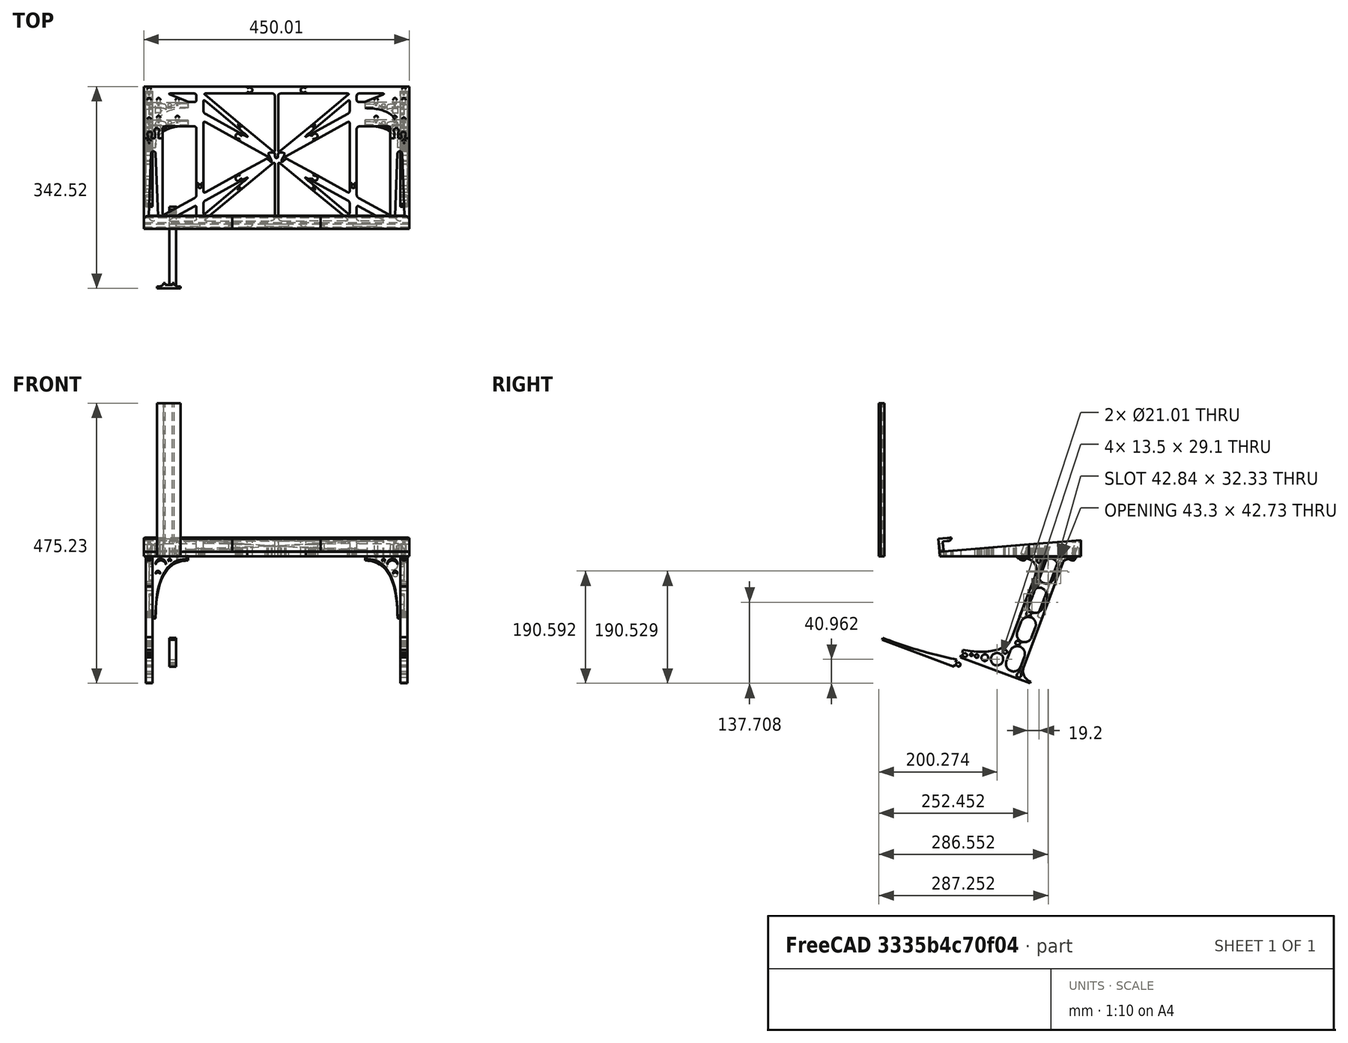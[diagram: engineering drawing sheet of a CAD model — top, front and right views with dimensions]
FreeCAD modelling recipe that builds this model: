
FCSTD DOCUMENT  (FreeCAD 0.19R0.19.2)
Label: laptopStand394
License: All rights reserved
LicenseURL: http://en.wikipedia.org/wiki/All_rights_reserved
objects: Part::Cylinder×164, Part::MultiFuse×151, Part::Box×65, Part::Cut×62, Sketcher::SketchObject×45, Part::Extrusion×44, Part::Fuse×17, Part::Fillet×10, App::MeasureDistance×4, Part::Chamfer×3
note: 561 computed .brp shape members not serialized (recipe doc carries the construction recipe); baked Part::Feature solids carry a one-line shape summary decoded from their .brp

FEATURE [Sketcher::SketchObject] Sketch001  label="legTop"
  FullyConstrained = true
  MapMode = 4
  Placement = pos=(0,0,0) rot=(0.57735,0.57735,0.57735;2.0944rad)
  sketch-geometry (41):
    g0: BSplineCurve PolesCount=3 KnotsCount=2 Degree=2 IsPeriodic=0
    g1: ArcOfCircle CenterX=73.1223 CenterY=-32.291 CenterZ=0 NormalX=0 NormalY=0 NormalZ=1 AngleXU=0 Radius=13 StartAngle=5.92268 EndAngle=9.06428
    g2: ArcOfCircle CenterX=66.7816 CenterY=-49.1439 CenterZ=0 NormalX=0 NormalY=0 NormalZ=1 AngleXU=0 Radius=13 StartAngle=2.78068 EndAngle=5.92131
    g3-g6: Circle x4 (B-spline internal-alignment scaffolding for g7; pole/knot coordinates omitted)
    g7: BSplineCurve PolesCount=4 KnotsCount=2 Degree=3 IsPeriodic=0
    g8: GeomPoint X=28.8094 Y=-19.0875 Z=0
    g9: GeomPoint X=47.0443 Y=-50.4712 Z=0
    g10: Circle CenterX=53.5586 CenterY=-23.2695 CenterZ=0 NormalX=0 NormalY=0 NormalZ=1 AngleXU=0 Radius=3.24518
    g11: LineSegment StartX=17.2232 StartY=-16.0875 StartZ=0 EndX=17.2232 EndY=-19.0875 EndZ=0
    g12: ArcOfCircle CenterX=17.2475 CenterY=-181.166 CenterZ=0 NormalX=0 NormalY=0 NormalZ=1 AngleXU=0 Radius=13 StartAngle=5.92268 EndAngle=7.49361
    g13: ArcOfCircle CenterX=29.5716 CenterY=-148.408 CenterZ=0 NormalX=0 NormalY=0 NormalZ=1 AngleXU=0 Radius=13 StartAngle=4.35228 EndAngle=5.92131
    g14: ArcOfCircle CenterX=35.8967 CenterY=-131.555 CenterZ=0 NormalX=0 NormalY=0 NormalZ=1 AngleXU=0 Radius=13 StartAngle=5.92268 EndAngle=7.49902
    g15: ArcOfCircle CenterX=48.1805 CenterY=-98.7782 CenterZ=0 NormalX=0 NormalY=0 NormalZ=1 AngleXU=0 Radius=13 StartAngle=4.34921 EndAngle=5.92131
    g16: ArcOfCircle CenterX=54.5183 CenterY=-81.9247 CenterZ=0 NormalX=0 NormalY=0 NormalZ=1 AngleXU=0 Radius=13 StartAngle=5.92268 EndAngle=8.70432
    g17: ArcOfCircle CenterX=20.184 CenterY=-217.506 CenterZ=0 NormalX=0 NormalY=0 NormalZ=1 AngleXU=0 Radius=3.81084 StartAngle=1.88136 EndAngle=6.80465
    g18: ArcOfCircle CenterX=36.3663 CenterY=-113.042 CenterZ=0 NormalX=0 NormalY=0 NormalZ=1 AngleXU=0 Radius=3.60555 StartAngle=0.230024 EndAngle=5.3372
    g19: ArcOfCircle CenterX=17.7945 CenterY=-162.686 CenterZ=0 NormalX=0 NormalY=0 NormalZ=1 AngleXU=0 Radius=3.60555 StartAngle=0.230024 EndAngle=5.3372
    g20: ArcOfCircle CenterX=49.8795 CenterY=-62.6074 CenterZ=0 NormalX=0 NormalY=0 NormalZ=1 AngleXU=0 Radius=3.84187 StartAngle=4.46973 EndAngle=9.40343
    g21: LineSegment StartX=48.9563 StartY=-66.3367 StartZ=0 EndX=44.7488 EndY=-73.3482 EndZ=0
    g22: LineSegment StartX=41.085 StartY=-66.3176 StartZ=0 EndX=46.0385 EndY=-62.5254 EndZ=0
    g23: LineSegment StartX=47.0443 StartY=-50.4712 StartZ=0 EndX=41.085 EndY=-66.3176 EndZ=0
    g24: LineSegment StartX=17.2232 StartY=-16.0875 StartZ=0 EndX=117.223 EndY=-16.0875 EndZ=0
    g25: LineSegment StartX=28.8094 StartY=-19.0875 StartZ=0 EndX=17.2232 EndY=-19.0875 EndZ=0
    g26: LineSegment StartX=117.223 StartY=-16.0875 StartZ=0 EndX=117.223 EndY=-19.0875 EndZ=0
    g27: LineSegment StartX=85.2866 StartY=-36.8766 StartZ=0 EndX=78.9396 EndY=-53.7463 EndZ=0
    g28: LineSegment StartX=60.9579 StartY=-27.7053 StartZ=0 EndX=54.6191 EndY=-44.5532 EndZ=0
    g29: LineSegment StartX=23.4884 StartY=-215.608 StartZ=0 EndX=94.6579 EndY=-26.1359 EndZ=0
    g30: LineSegment StartX=19.0195 StartY=-213.878 StartZ=0 EndX=29.4118 EndY=-185.752 EndZ=0
    g31: LineSegment StartX=22.7134 StartY=-166.661 StartZ=0 EndX=21.8316 EndY=-169.001 EndZ=0
    g32: LineSegment StartX=19.9036 StartY=-165.61 StartZ=0 EndX=22.7134 EndY=-166.661 EndZ=0
    g33: LineSegment StartX=21.3051 StartY=-161.864 StartZ=0 EndX=24.1149 EndY=-162.915 EndZ=0
    g34: LineSegment StartX=24.1149 StartY=-162.915 StartZ=0 EndX=24.9906 EndY=-160.574 EndZ=0
    g35: LineSegment StartX=41.7296 StartY=-153.01 StartZ=0 EndX=48.061 EndY=-136.14 EndZ=0
    g36: LineSegment StartX=41.2852 StartY=-117.017 StartZ=0 EndX=40.4148 EndY=-119.365 EndZ=0
    g37: LineSegment StartX=38.4753 StartY=-115.966 StartZ=0 EndX=41.2852 EndY=-117.017 EndZ=0
    g38: LineSegment StartX=39.8769 StartY=-112.22 StartZ=0 EndX=42.6867 EndY=-113.271 EndZ=0
    g39: LineSegment StartX=42.6867 StartY=-113.271 StartZ=0 EndX=43.5622 EndY=-110.93 EndZ=0
    g40: LineSegment StartX=66.6827 StartY=-86.5104 StartZ=0 EndX=60.3386 EndY=-103.381 EndZ=0
  constraints (65):
    c: Block(g0)
    c: Block(g1)
    c: Block(g2)
    c: Weight(g3) = 1
    c: Equal(g3,g4)
    c: Equal(g3,g5)
    c: Equal(g3,g6)
    c: InternalAlignment(g3-g6 -> g7) x4
    c: InternalAlignment(g8,g7)
    c: InternalAlignment(g9,g7)
    c: Block(g10)
    c: Block(g7)
    c: Vertical(g11)
    c: Block(g12)
    c: Block(g13)
    c: Block(g14)
    c: Block(g15)
    c: Block(g16)
    c: Block(g17)
    c: Block(g18)
    c: Block(g19)
    c: Block(g20)
    c: Coincident(g21,g20)
    c: Coincident(g21,g16)
    c: Coincident(g22,g20)
    c: Block(g22)
    c: Coincident(g23,g7)
    c: Coincident(g23,g22)
    c: Coincident(g24,g11)
    c: Horizontal(g24)
    c: Coincident(g25,g7)
    c: Coincident(g25,g11)
    c: Horizontal(g25)
    c: Coincident(g26,g24)
    c: Coincident(g26,g0)
    c: Vertical(g26)
    c: Block(g24)
    c: Coincident(g27,g1)
    c: Coincident(g27,g2)
    c: Coincident(g28,g1)
    c: Coincident(g28,g2)
    c: Coincident(g29,g17)
    c: Coincident(g29,g0)
    c: Coincident(g30,g17)
    c: Coincident(g30,g12)
    c: Coincident(g31,g12)
    c: Coincident(g32,g19)
    c: Coincident(g32,g31)
    c: Block(g31)
    c: Coincident(g33,g19)
    c: Coincident(g34,g33)
    c: Coincident(g34,g13)
    c: Block(g34)
    c: Coincident(g35,g13)
    c: Coincident(g35,g14)
    c: Coincident(g36,g14)
    c: Coincident(g37,g18)
    c: Coincident(g37,g36)
    c: Block(g36)
    c: Coincident(g38,g18)
    c: Coincident(g39,g38)
    c: Coincident(g39,g15)
    c: Block(g39)
    c: Coincident(g40,g16)
    c: Coincident(g40,g15)
FEATURE [Sketcher::SketchObject] Sketch002
  FullyConstrained = true
  sketch-geometry (15):
    g0: LineSegment StartX=-6.77179 StartY=-200.304 StartZ=0 EndX=5.22821 EndY=-200.304 EndZ=0
    g1: LineSegment StartX=5.22821 StartY=-200.304 StartZ=0 EndX=5.22821 EndY=-197.304 EndZ=0
    g2: LineSegment StartX=-6.77179 StartY=-200.304 StartZ=0 EndX=-6.77179 EndY=-197.304 EndZ=0
    g3: LineSegment StartX=5.22821 StartY=-197.304 StartZ=0 EndX=8.22821 EndY=-197.304 EndZ=0
    g4: LineSegment StartX=19.2282 StartY=-203.304 StartZ=0 EndX=19.2282 EndY=-206.304 EndZ=0
    g5: Circle CenterX=19.2282 CenterY=-203.304 CenterZ=0 NormalX=0 NormalY=0 NormalZ=1 AngleXU=0 Radius=1
    g6: Circle CenterX=8.22821 CenterY=-203.304 CenterZ=0 NormalX=0 NormalY=0 NormalZ=1 AngleXU=0 Radius=1
    g7: Circle CenterX=8.22821 CenterY=-197.304 CenterZ=0 NormalX=0 NormalY=0 NormalZ=1 AngleXU=0 Radius=1
    g8: BSplineCurve PolesCount=3 KnotsCount=2 Degree=2 IsPeriodic=0
    g9: GeomPoint X=19.2282 Y=-203.304 Z=0
    g10: GeomPoint X=8.22821 Y=-197.304 Z=0
    g11: LineSegment StartX=19.2282 StartY=-206.304 StartZ=0 EndX=-20.7718 EndY=-206.304 EndZ=0
    g12: LineSegment StartX=-20.7718 StartY=-206.304 StartZ=0 EndX=-20.7718 EndY=-203.304 EndZ=0
    g13: BSplineCurve PolesCount=3 KnotsCount=2 Degree=2 IsPeriodic=0
    g14: LineSegment StartX=-9.77179 StartY=-197.304 StartZ=0 EndX=-6.77179 EndY=-197.304 EndZ=0
  constraints (35):
    c: Horizontal(g0)
    c: Distance(g0) = 12
    c: Coincident(g1,g0)
    c: Vertical(g1)
    c: Distance(g1) = 3
    c: Coincident(g2,g0)
    c: Vertical(g2)
    c: Distance(g2) = 3
    c: Coincident(g3,g1)
    c: Horizontal(g3)
    c: Distance(g3) = 3
    c: Vertical(g4)
    c: Coincident(g8,g4)
    c: Weight(g5) = 1
    c: Equal(g5,g6)
    c: Equal(g5,g7)
    c: Coincident(g8,g3)
    c: InternalAlignment(g5,g8)
    c: InternalAlignment(g6,g8)
    c: InternalAlignment(g7,g8)
    c: InternalAlignment(g9,g8)
    c: InternalAlignment(g10,g8)
    c: Block(g8)
    c: Coincident(g11,g4)
    c: Horizontal(g11)
    c: Distance(g11) = 40
    c: Block(g11)
    c: Coincident(g12,g11)
    c: Vertical(g12)
    c: Block(g12)
    c: Block(g13)
    c: Coincident(g13,g12)
    c: Coincident(g14,g13)
    c: Coincident(g14,g2)
    c: Horizontal(g14)
FEATURE [Part::Extrusion] Extrude003
  Base = -> Sketch002
  Dir = (0,0,1)
  DirMode = 2
  FaceMakerClass = Part::FaceMakerBullseye
  LengthFwd = 260
  LengthRev = 0
  Solid = true
  Symmetric = false
FEATURE [Sketcher::SketchObject] Sketch003  label="original"
  FullyConstrained = false
  sketch-geometry (469):
    g0: LineSegment StartX=-42.9272 StartY=136.221 StartZ=0 EndX=-42.9272 EndY=-103.779 EndZ=0
    g1: LineSegment StartX=407.073 StartY=136.221 StartZ=0 EndX=407.073 EndY=-103.779 EndZ=0
    g2: ArcOfCircle CenterX=-26.9272 CenterY=-83.7794 CenterZ=0 NormalX=0 NormalY=0 NormalZ=1 AngleXU=0 Radius=8 StartAngle=3.14159 EndAngle=6.28319
    g3: ArcOfCircle CenterX=391.073 CenterY=-83.7794 CenterZ=0 NormalX=0 NormalY=0 NormalZ=1 AngleXU=0 Radius=8 StartAngle=3.14159 EndAngle=6.28319
    g4: Circle CenterX=175.022 CenterY=27.0628 CenterZ=0 NormalX=0 NormalY=0 NormalZ=1 AngleXU=0 Radius=1
    g5: Circle CenterX=179.022 CenterY=24.8665 CenterZ=0 NormalX=0 NormalY=0 NormalZ=1 AngleXU=0 Radius=1
    g6: Circle CenterX=179.022 CenterY=27.0628 CenterZ=0 NormalX=0 NormalY=0 NormalZ=1 AngleXU=0 Radius=1
    g7: BSplineCurve PolesCount=3 KnotsCount=2 Degree=2 IsPeriodic=0
    g8: GeomPoint X=175.022 Y=27.0628 Z=0
    g9: GeomPoint X=179.022 Y=27.0628 Z=0
    g10: Circle CenterX=189.124 CenterY=27.0628 CenterZ=0 NormalX=0 NormalY=0 NormalZ=1 AngleXU=0 Radius=1
    g11: Circle CenterX=185.124 CenterY=24.8665 CenterZ=0 NormalX=0 NormalY=0 NormalZ=1 AngleXU=0 Radius=1
    g12: Circle CenterX=185.124 CenterY=27.0628 CenterZ=0 NormalX=0 NormalY=0 NormalZ=1 AngleXU=0 Radius=1
    g13: BSplineCurve PolesCount=3 KnotsCount=2 Degree=2 IsPeriodic=0
    g14: GeomPoint X=189.124 Y=27.0628 Z=0
    g15: GeomPoint X=185.124 Y=27.0628 Z=0
    g16: Circle CenterX=175.022 CenterY=5.37834 CenterZ=0 NormalX=0 NormalY=0 NormalZ=1 AngleXU=0 Radius=1
    g17: Circle CenterX=179.022 CenterY=7.57463 CenterZ=0 NormalX=0 NormalY=0 NormalZ=1 AngleXU=0 Radius=1
    g18: Circle CenterX=179.022 CenterY=5.34704 CenterZ=0 NormalX=0 NormalY=0 NormalZ=1 AngleXU=0 Radius=1
    g19: BSplineCurve PolesCount=3 KnotsCount=2 Degree=2 IsPeriodic=0
    g20: GeomPoint X=175.022 Y=5.37834 Z=0
    g21: GeomPoint X=179.022 Y=5.34704 Z=0
    g22: Circle CenterX=189.124 CenterY=5.37834 CenterZ=0 NormalX=0 NormalY=0 NormalZ=1 AngleXU=0 Radius=1
    g23: Circle CenterX=185.124 CenterY=7.57463 CenterZ=0 NormalX=0 NormalY=0 NormalZ=1 AngleXU=0 Radius=1
    g24: Circle CenterX=185.124 CenterY=5.34704 CenterZ=0 NormalX=0 NormalY=0 NormalZ=1 AngleXU=0 Radius=1
    g25: BSplineCurve PolesCount=3 KnotsCount=2 Degree=2 IsPeriodic=0
    g26: GeomPoint X=189.124 Y=5.37834 Z=0
    g27: GeomPoint X=185.124 Y=5.34704 Z=0
    g28: Circle CenterX=165.871 CenterY=18.1458 CenterZ=0 NormalX=0 NormalY=0 NormalZ=1 AngleXU=0 Radius=1
    g29: Circle CenterX=169.377 CenterY=16.2206 CenterZ=0 NormalX=0 NormalY=0 NormalZ=1 AngleXU=0 Radius=1
    g30: Circle CenterX=165.871 CenterY=14.2956 CenterZ=0 NormalX=0 NormalY=0 NormalZ=1 AngleXU=0 Radius=1
    g31: BSplineCurve PolesCount=3 KnotsCount=2 Degree=2 IsPeriodic=0
    g32: GeomPoint X=165.871 Y=18.1458 Z=0
    g33: GeomPoint X=165.871 Y=14.2956 Z=0
    g34: Circle CenterX=198.275 CenterY=18.1318 CenterZ=0 NormalX=0 NormalY=0 NormalZ=1 AngleXU=0 Radius=1
    g35: Circle CenterX=194.768 CenterY=16.2206 CenterZ=0 NormalX=0 NormalY=0 NormalZ=1 AngleXU=0 Radius=1
    g36: Circle CenterX=198.264 CenterY=14.2963 CenterZ=0 NormalX=0 NormalY=0 NormalZ=1 AngleXU=0 Radius=1
    g37: BSplineCurve PolesCount=3 KnotsCount=2 Degree=2 IsPeriodic=0
    g38: GeomPoint X=198.275 Y=18.1318 Z=0
    g39: GeomPoint X=198.264 Y=14.2963 Z=0
    g40: LineSegment StartX=407.073 StartY=-103.779 StartZ=0 EndX=-42.9272 EndY=-103.779 EndZ=0
    g41: Circle CenterX=125.607 CenterY=54.1951 CenterZ=0 NormalX=0 NormalY=0 NormalZ=1 AngleXU=0 Radius=1
    g42: Circle CenterX=139.632 CenterY=46.4944 CenterZ=0 NormalX=0 NormalY=0 NormalZ=1 AngleXU=0 Radius=1
    g43: Circle CenterX=127.326 CenterY=56.7187 CenterZ=0 NormalX=0 NormalY=0 NormalZ=1 AngleXU=0 Radius=1
    g44: BSplineCurve PolesCount=3 KnotsCount=2 Degree=2 IsPeriodic=0
    g45: GeomPoint X=125.607 Y=54.1951 Z=0
    g46: GeomPoint X=127.326 Y=56.7187 Z=0
    g47: Circle CenterX=236.824 CenterY=56.7187 CenterZ=0 NormalX=0 NormalY=0 NormalZ=1 AngleXU=0 Radius=1
    g48: Circle CenterX=224.513 CenterY=46.4944 CenterZ=0 NormalX=0 NormalY=0 NormalZ=1 AngleXU=0 Radius=1
    g49: Circle CenterX=238.538 CenterY=54.1951 CenterZ=0 NormalX=0 NormalY=0 NormalZ=1 AngleXU=0 Radius=1
    g50: BSplineCurve PolesCount=3 KnotsCount=2 Degree=2 IsPeriodic=0
    g51: GeomPoint X=236.824 Y=56.7187 Z=0
    g52: GeomPoint X=238.538 Y=54.1951 Z=0
    g53: Circle CenterX=238.538 CenterY=-21.7516 CenterZ=0 NormalX=0 NormalY=0 NormalZ=1 AngleXU=0 Radius=1
    g54: Circle CenterX=224.513 CenterY=-14.0532 CenterZ=0 NormalX=0 NormalY=0 NormalZ=1 AngleXU=0 Radius=1
    g55: Circle CenterX=236.584 CenterY=-24.2775 CenterZ=0 NormalX=0 NormalY=0 NormalZ=1 AngleXU=0 Radius=1
    g56: BSplineCurve PolesCount=3 KnotsCount=2 Degree=2 IsPeriodic=0
    g57: GeomPoint X=238.538 Y=-21.7516 Z=0
    g58: GeomPoint X=236.584 Y=-24.2775 Z=0
    g59: Circle CenterX=125.607 CenterY=-21.7539 CenterZ=0 NormalX=0 NormalY=0 NormalZ=1 AngleXU=0 Radius=1
    g60: Circle CenterX=139.632 CenterY=-14.0532 CenterZ=0 NormalX=0 NormalY=0 NormalZ=1 AngleXU=0 Radius=1
    g61: Circle CenterX=127.325 CenterY=-24.2775 CenterZ=0 NormalX=0 NormalY=0 NormalZ=1 AngleXU=0 Radius=1
    g62: BSplineCurve PolesCount=3 KnotsCount=2 Degree=2 IsPeriodic=0
    g63: GeomPoint X=125.607 Y=-21.7539 Z=0
    g64: GeomPoint X=127.325 Y=-24.2775 Z=0
    g65: Circle CenterX=302.996 CenterY=111.695 CenterZ=0 NormalX=0 NormalY=0 NormalZ=1 AngleXU=0 Radius=1
    g66: Circle CenterX=306.073 CenterY=114.251 CenterZ=0 NormalX=0 NormalY=0 NormalZ=1 AngleXU=0 Radius=1
    g67: Circle CenterX=306.073 CenterY=110.251 CenterZ=0 NormalX=0 NormalY=0 NormalZ=1 AngleXU=0 Radius=1
    g68: BSplineCurve PolesCount=3 KnotsCount=2 Degree=2 IsPeriodic=0
    g69: GeomPoint X=302.996 Y=111.695 Z=0
    g70: GeomPoint X=306.073 Y=110.251 Z=0
    g71: Circle CenterX=306.073 CenterY=95.2763 CenterZ=0 NormalX=0 NormalY=0 NormalZ=1 AngleXU=0 Radius=1
    g72: Circle CenterX=306.073 CenterY=91.2763 CenterZ=0 NormalX=0 NormalY=0 NormalZ=1 AngleXU=0 Radius=1
    g73: Circle CenterX=302.567 CenterY=89.3511 CenterZ=0 NormalX=0 NormalY=0 NormalZ=1 AngleXU=0 Radius=1
    g74: BSplineCurve PolesCount=3 KnotsCount=2 Degree=2 IsPeriodic=0
    g75: GeomPoint X=306.073 Y=95.2763 Z=0
    g76: GeomPoint X=302.567 Y=89.3511 Z=0
    g77: LineSegment StartX=306.073 StartY=110.251 StartZ=0 EndX=306.073 EndY=95.2763 EndZ=0
    g78: LineSegment StartX=302.996 StartY=111.695 StartZ=0 EndX=236.824 EndY=56.7187 EndZ=0
    g79: LineSegment StartX=238.538 StartY=54.1951 StartZ=0 EndX=302.567 EndY=89.3511 EndZ=0
    g80: Circle CenterX=61.1496 CenterY=111.695 CenterZ=0 NormalX=0 NormalY=0 NormalZ=1 AngleXU=0 Radius=1
    g81: Circle CenterX=58.0728 CenterY=114.251 CenterZ=0 NormalX=0 NormalY=0 NormalZ=1 AngleXU=0 Radius=1
    g82: Circle CenterX=58.0728 CenterY=110.251 CenterZ=0 NormalX=0 NormalY=0 NormalZ=1 AngleXU=0 Radius=1
    g83: BSplineCurve PolesCount=3 KnotsCount=2 Degree=2 IsPeriodic=0
    g84: GeomPoint X=61.1496 Y=111.695 Z=0
    g85: GeomPoint X=58.0728 Y=110.251 Z=0
    g86: Circle CenterX=61.5791 CenterY=89.3511 CenterZ=0 NormalX=0 NormalY=0 NormalZ=1 AngleXU=0 Radius=1
    g87: Circle CenterX=58.0728 CenterY=91.2763 CenterZ=0 NormalX=0 NormalY=0 NormalZ=1 AngleXU=0 Radius=1
    g88: Circle CenterX=58.0728 CenterY=95.2763 CenterZ=0 NormalX=0 NormalY=0 NormalZ=1 AngleXU=0 Radius=1
    g89: BSplineCurve PolesCount=3 KnotsCount=2 Degree=2 IsPeriodic=0
    g90: GeomPoint X=61.5791 Y=89.3511 Z=0
    g91: GeomPoint X=58.0728 Y=95.2763 Z=0
    g92: LineSegment StartX=58.0728 StartY=110.251 StartZ=0 EndX=58.0728 EndY=95.2763 EndZ=0
    g93: LineSegment StartX=61.1496 StartY=111.695 StartZ=0 EndX=127.326 EndY=56.7187 EndZ=0
    g94: LineSegment StartX=125.607 StartY=54.1951 StartZ=0 EndX=61.5791 EndY=89.3511 EndZ=0
    g95: Circle CenterX=61.5791 CenterY=-56.9099 CenterZ=0 NormalX=0 NormalY=0 NormalZ=1 AngleXU=0 Radius=1
    g96: Circle CenterX=58.0728 CenterY=-58.8351 CenterZ=0 NormalX=0 NormalY=0 NormalZ=1 AngleXU=0 Radius=1
    g97: Circle CenterX=58.0728 CenterY=-62.8351 CenterZ=0 NormalX=0 NormalY=0 NormalZ=1 AngleXU=0 Radius=1
    g98: BSplineCurve PolesCount=3 KnotsCount=2 Degree=2 IsPeriodic=0
    g99: GeomPoint X=61.5791 Y=-56.9099 Z=0
    g100: GeomPoint X=58.0728 Y=-62.8351 Z=0
    g101: Circle CenterX=58.0728 CenterY=-77.8102 CenterZ=0 NormalX=0 NormalY=0 NormalZ=1 AngleXU=0 Radius=1
    g102: Circle CenterX=58.0728 CenterY=-81.8102 CenterZ=0 NormalX=0 NormalY=0 NormalZ=1 AngleXU=0 Radius=1
    g103: Circle CenterX=61.1496 CenterY=-79.2541 CenterZ=0 NormalX=0 NormalY=0 NormalZ=1 AngleXU=0 Radius=1
    g104: BSplineCurve PolesCount=3 KnotsCount=2 Degree=2 IsPeriodic=0
    g105: GeomPoint X=58.0728 Y=-77.8102 Z=0
    g106: GeomPoint X=61.1496 Y=-79.2541 Z=0
    g107: LineSegment StartX=58.0728 StartY=-62.8351 StartZ=0 EndX=58.0728 EndY=-77.8102 EndZ=0
    g108: LineSegment StartX=61.1496 StartY=-79.2541 StartZ=0 EndX=127.325 EndY=-24.2775 EndZ=0
    g109: LineSegment StartX=125.607 StartY=-21.7539 StartZ=0 EndX=61.5791 EndY=-56.9099 EndZ=0
    g110: Circle CenterX=302.567 CenterY=-56.9099 CenterZ=0 NormalX=0 NormalY=0 NormalZ=1 AngleXU=0 Radius=1
    g111: Circle CenterX=306.073 CenterY=-58.8351 CenterZ=0 NormalX=0 NormalY=0 NormalZ=1 AngleXU=0 Radius=1
    g112: Circle CenterX=306.073 CenterY=-62.8351 CenterZ=0 NormalX=0 NormalY=0 NormalZ=1 AngleXU=0 Radius=1
    g113: BSplineCurve PolesCount=3 KnotsCount=2 Degree=2 IsPeriodic=0
    g114: GeomPoint X=302.567 Y=-56.9099 Z=0
    g115: GeomPoint X=306.073 Y=-62.8351 Z=0
    g116: Circle CenterX=302.996 CenterY=-79.2541 CenterZ=0 NormalX=0 NormalY=0 NormalZ=1 AngleXU=0 Radius=1
    g117: Circle CenterX=306.073 CenterY=-81.8102 CenterZ=0 NormalX=0 NormalY=0 NormalZ=1 AngleXU=0 Radius=1
    g118: Circle CenterX=306.073 CenterY=-77.8102 CenterZ=0 NormalX=0 NormalY=0 NormalZ=1 AngleXU=0 Radius=1
    g119: BSplineCurve PolesCount=3 KnotsCount=2 Degree=2 IsPeriodic=0
    g120: GeomPoint X=302.996 Y=-79.2541 Z=0
    g121: GeomPoint X=306.073 Y=-77.8102 Z=0
    g122: LineSegment StartX=306.073 StartY=-62.8351 StartZ=0 EndX=306.073 EndY=-77.8102 EndZ=0
    g123: LineSegment StartX=302.996 StartY=-79.2541 StartZ=0 EndX=236.584 EndY=-24.2775 EndZ=0
    g124: LineSegment StartX=238.538 StartY=-21.7516 StartZ=0 EndX=302.567 EndY=-56.9099 EndZ=0
    g125: Circle CenterX=61.6457 CenterY=-88.8112 CenterZ=0 NormalX=0 NormalY=0 NormalZ=1 AngleXU=0 Radius=1
    g126: Circle CenterX=58.0728 CenterY=-91.7794 CenterZ=0 NormalX=0 NormalY=0 NormalZ=1 AngleXU=0 Radius=1
    g127: Circle CenterX=63.9135 CenterY=-91.7791 CenterZ=0 NormalX=0 NormalY=0 NormalZ=1 AngleXU=0 Radius=1
    g128: BSplineCurve PolesCount=3 KnotsCount=2 Degree=2 IsPeriodic=0
    g129: GeomPoint X=61.6457 Y=-88.8112 Z=0
    g130: GeomPoint X=63.9135 Y=-91.7791 Z=0
    g131: Circle CenterX=179.022 CenterY=-85.8163 CenterZ=0 NormalX=0 NormalY=0 NormalZ=1 AngleXU=0 Radius=1
    g132: Circle CenterX=179.022 CenterY=-91.7794 CenterZ=0 NormalX=0 NormalY=0 NormalZ=1 AngleXU=0 Radius=1
    g133: Circle CenterX=171.895 CenterY=-91.7791 CenterZ=0 NormalX=0 NormalY=0 NormalZ=1 AngleXU=0 Radius=1
    g134: BSplineCurve PolesCount=3 KnotsCount=2 Degree=2 IsPeriodic=0
    g135: GeomPoint X=179.022 Y=-85.8163 Z=0
    g136: GeomPoint X=171.895 Y=-91.7791 Z=0
    g137: Circle CenterX=185.124 CenterY=-86.2028 CenterZ=0 NormalX=0 NormalY=0 NormalZ=1 AngleXU=0 Radius=1
    g138: Circle CenterX=185.124 CenterY=-91.7794 CenterZ=0 NormalX=0 NormalY=0 NormalZ=1 AngleXU=0 Radius=1
    g139: Circle CenterX=191.747 CenterY=-91.7794 CenterZ=0 NormalX=0 NormalY=0 NormalZ=1 AngleXU=0 Radius=1
    g140: BSplineCurve PolesCount=3 KnotsCount=2 Degree=2 IsPeriodic=0
    g141: GeomPoint X=185.124 Y=-86.2028 Z=0
    g142: GeomPoint X=191.747 Y=-91.7794 Z=0
    g143: Circle CenterX=299.888 CenterY=-86.6413 CenterZ=0 NormalX=0 NormalY=0 NormalZ=1 AngleXU=0 Radius=1
    g144: Circle CenterX=306.073 CenterY=-91.7794 CenterZ=0 NormalX=0 NormalY=0 NormalZ=1 AngleXU=0 Radius=1
    g145: Circle CenterX=298.776 CenterY=-91.7794 CenterZ=0 NormalX=0 NormalY=0 NormalZ=1 AngleXU=0 Radius=1
    g146: BSplineCurve PolesCount=3 KnotsCount=2 Degree=2 IsPeriodic=0
    g147: GeomPoint X=299.888 Y=-86.6413 Z=0
    g148: GeomPoint X=298.776 Y=-91.7794 Z=0
    g149: LineSegment StartX=189.124 StartY=5.37834 StartZ=0 EndX=299.888 EndY=-86.6413 EndZ=0
    g150: LineSegment StartX=298.776 StartY=-91.7794 StartZ=0 EndX=191.747 EndY=-91.7794 EndZ=0
    g151: LineSegment StartX=185.124 StartY=-86.2028 StartZ=0 EndX=185.124 EndY=5.34704 EndZ=0
    g152: LineSegment StartX=179.022 StartY=5.34704 StartZ=0 EndX=179.022 EndY=-85.8163 EndZ=0
    g153: LineSegment StartX=171.895 StartY=-91.7791 StartZ=0 EndX=63.9135 EndY=-91.7791 EndZ=0
    g154: LineSegment StartX=61.6457 StartY=-88.8112 StartZ=0 EndX=175.022 EndY=5.37834 EndZ=0
    g155: Circle CenterX=302.073 CenterY=124.221 CenterZ=0 NormalX=0 NormalY=0 NormalZ=1 AngleXU=0 Radius=1
    g156: Circle CenterX=306.073 CenterY=124.221 CenterZ=0 NormalX=0 NormalY=0 NormalZ=1 AngleXU=0 Radius=1
    g157: Circle CenterX=302.996 CenterY=121.665 CenterZ=0 NormalX=0 NormalY=0 NormalZ=1 AngleXU=0 Radius=1
    g158: BSplineCurve PolesCount=3 KnotsCount=2 Degree=2 IsPeriodic=0
    g159: GeomPoint X=302.073 Y=124.221 Z=0
    g160: GeomPoint X=302.996 Y=121.665 Z=0
    g161: Circle CenterX=189.124 CenterY=124.221 CenterZ=0 NormalX=0 NormalY=0 NormalZ=1 AngleXU=0 Radius=1
    g162: Circle CenterX=185.124 CenterY=124.221 CenterZ=0 NormalX=0 NormalY=0 NormalZ=1 AngleXU=0 Radius=1
    g163: Circle CenterX=185.124 CenterY=120.221 CenterZ=0 NormalX=0 NormalY=0 NormalZ=1 AngleXU=0 Radius=1
    g164: BSplineCurve PolesCount=3 KnotsCount=2 Degree=2 IsPeriodic=0
    g165: GeomPoint X=189.124 Y=124.221 Z=0
    g166: GeomPoint X=185.124 Y=120.221 Z=0
    g167: Circle CenterX=175.022 CenterY=124.221 CenterZ=0 NormalX=0 NormalY=0 NormalZ=1 AngleXU=0 Radius=1
    g168: Circle CenterX=179.022 CenterY=124.221 CenterZ=0 NormalX=0 NormalY=0 NormalZ=1 AngleXU=0 Radius=1
    g169: Circle CenterX=179.022 CenterY=120.221 CenterZ=0 NormalX=0 NormalY=0 NormalZ=1 AngleXU=0 Radius=1
    g170: BSplineCurve PolesCount=3 KnotsCount=2 Degree=2 IsPeriodic=0
    g171: GeomPoint X=175.022 Y=124.221 Z=0
    g172: GeomPoint X=179.022 Y=120.221 Z=0
    g173: Circle CenterX=62.0728 CenterY=124.221 CenterZ=0 NormalX=0 NormalY=0 NormalZ=1 AngleXU=0 Radius=1
    g174: Circle CenterX=58.0728 CenterY=124.221 CenterZ=0 NormalX=0 NormalY=0 NormalZ=1 AngleXU=0 Radius=1
    g175: Circle CenterX=61.1496 CenterY=121.665 CenterZ=0 NormalX=0 NormalY=0 NormalZ=1 AngleXU=0 Radius=1
    g176: BSplineCurve PolesCount=3 KnotsCount=2 Degree=2 IsPeriodic=0
    g177: GeomPoint X=62.0728 Y=124.221 Z=0
    g178: GeomPoint X=61.1496 Y=121.665 Z=0
    g179: LineSegment StartX=179.022 StartY=120.221 StartZ=0 EndX=179.022 EndY=27.0628 EndZ=0
    g180: LineSegment StartX=185.124 StartY=27.0628 StartZ=0 EndX=185.124 EndY=120.221 EndZ=0
    g181: LineSegment StartX=302.996 StartY=121.665 StartZ=0 EndX=189.124 EndY=27.0628 EndZ=0
    g182: LineSegment StartX=175.022 StartY=27.0628 StartZ=0 EndX=61.1496 EndY=121.665 EndZ=0
    g183: Circle CenterX=61.5791 CenterY=75.4095 CenterZ=0 NormalX=0 NormalY=0 NormalZ=1 AngleXU=0 Radius=1
    g184: Circle CenterX=58.0728 CenterY=77.3346 CenterZ=0 NormalX=0 NormalY=0 NormalZ=1 AngleXU=0 Radius=1
    g185: Circle CenterX=58.0728 CenterY=73.3346 CenterZ=0 NormalX=0 NormalY=0 NormalZ=1 AngleXU=0 Radius=1
    g186: BSplineCurve PolesCount=3 KnotsCount=2 Degree=2 IsPeriodic=0
    g187: GeomPoint X=61.5791 Y=75.4095 Z=0
    g188: GeomPoint X=58.0728 Y=73.3346 Z=0
    g189: Circle CenterX=58.0728 CenterY=-40.8935 CenterZ=0 NormalX=0 NormalY=0 NormalZ=1 AngleXU=0 Radius=1
    g190: Circle CenterX=58.0728 CenterY=-44.8935 CenterZ=0 NormalX=0 NormalY=0 NormalZ=1 AngleXU=0 Radius=1
    g191: Circle CenterX=61.5791 CenterY=-42.9683 CenterZ=0 NormalX=0 NormalY=0 NormalZ=1 AngleXU=0 Radius=1
    g192: BSplineCurve PolesCount=3 KnotsCount=2 Degree=2 IsPeriodic=0
    g193: GeomPoint X=58.0728 Y=-40.8935 Z=0
    g194: GeomPoint X=61.5791 Y=-42.9683 Z=0
    g195: LineSegment StartX=61.5791 StartY=-42.9683 StartZ=0 EndX=165.871 EndY=14.2956 EndZ=0
    g196: LineSegment StartX=165.871 StartY=18.1458 StartZ=0 EndX=61.5791 EndY=75.4095 EndZ=0
    g197: LineSegment StartX=58.0728 StartY=73.3346 StartZ=0 EndX=58.0728 EndY=-40.8935 EndZ=0
    g198: Circle CenterX=302.567 CenterY=-42.9683 CenterZ=0 NormalX=0 NormalY=0 NormalZ=1 AngleXU=0 Radius=1
    g199: Circle CenterX=306.073 CenterY=-44.8935 CenterZ=0 NormalX=0 NormalY=0 NormalZ=1 AngleXU=0 Radius=1
    g200: Circle CenterX=306.073 CenterY=-40.8935 CenterZ=0 NormalX=0 NormalY=0 NormalZ=1 AngleXU=0 Radius=1
    g201: BSplineCurve PolesCount=3 KnotsCount=2 Degree=2 IsPeriodic=0
    g202: GeomPoint X=302.567 Y=-42.9683 Z=0
    g203: GeomPoint X=306.073 Y=-40.8935 Z=0
    g204: Circle CenterX=306.073 CenterY=73.3346 CenterZ=0 NormalX=0 NormalY=0 NormalZ=1 AngleXU=0 Radius=1
    g205: Circle CenterX=306.073 CenterY=77.3346 CenterZ=0 NormalX=0 NormalY=0 NormalZ=1 AngleXU=0 Radius=1
    g206: Circle CenterX=302.535 CenterY=75.4095 CenterZ=0 NormalX=0 NormalY=0 NormalZ=1 AngleXU=0 Radius=1
    g207: BSplineCurve PolesCount=3 KnotsCount=2 Degree=2 IsPeriodic=0
    g208: GeomPoint X=306.073 Y=73.3346 Z=0
    g209: GeomPoint X=302.535 Y=75.4095 Z=0
    g210: LineSegment StartX=302.567 StartY=-42.9683 StartZ=0 EndX=198.264 EndY=14.2963 EndZ=0
    g211: LineSegment StartX=198.275 StartY=18.1318 StartZ=0 EndX=302.535 EndY=75.4095 EndZ=0
    g212: LineSegment StartX=306.073 StartY=73.3346 StartZ=0 EndX=306.073 EndY=-40.8935 EndZ=0
    g213: LineSegment StartX=322.073 StartY=105.865 StartZ=0 EndX=328.643 EndY=105.865 EndZ=0
    g214: LineSegment StartX=318.073 StartY=120.221 StartZ=0 EndX=318.073 EndY=109.865 EndZ=0
    g215: LineSegment StartX=336.157 StartY=107.779 StartZ=0 EndX=362.567 EndY=122.294 EndZ=0
    g216: Circle CenterX=362.073 CenterY=124.221 CenterZ=0 NormalX=0 NormalY=0 NormalZ=1 AngleXU=0 Radius=1
    g217: Circle CenterX=366.073 CenterY=124.221 CenterZ=0 NormalX=0 NormalY=0 NormalZ=1 AngleXU=0 Radius=1
    g218: Circle CenterX=362.567 CenterY=122.294 CenterZ=0 NormalX=0 NormalY=0 NormalZ=1 AngleXU=0 Radius=1
    g219: BSplineCurve PolesCount=3 KnotsCount=2 Degree=2 IsPeriodic=0
    g220: GeomPoint X=362.073 Y=124.221 Z=0
    g221: GeomPoint X=362.567 Y=122.294 Z=0
    g222: Circle CenterX=322.073 CenterY=124.221 CenterZ=0 NormalX=0 NormalY=0 NormalZ=1 AngleXU=0 Radius=1
    g223: Circle CenterX=318.073 CenterY=124.221 CenterZ=0 NormalX=0 NormalY=0 NormalZ=1 AngleXU=0 Radius=1
    g224: Circle CenterX=318.073 CenterY=120.221 CenterZ=0 NormalX=0 NormalY=0 NormalZ=1 AngleXU=0 Radius=1
    g225: BSplineCurve PolesCount=3 KnotsCount=2 Degree=2 IsPeriodic=0
    g226: GeomPoint X=322.073 Y=124.221 Z=0
    g227: GeomPoint X=318.073 Y=120.221 Z=0
    g228: Circle CenterX=322.073 CenterY=105.865 CenterZ=0 NormalX=0 NormalY=0 NormalZ=1 AngleXU=0 Radius=1
    g229: Circle CenterX=318.073 CenterY=105.865 CenterZ=0 NormalX=0 NormalY=0 NormalZ=1 AngleXU=0 Radius=1
    g230: Circle CenterX=318.073 CenterY=109.865 CenterZ=0 NormalX=0 NormalY=0 NormalZ=1 AngleXU=0 Radius=1
    g231: BSplineCurve PolesCount=3 KnotsCount=2 Degree=2 IsPeriodic=0
    g232: GeomPoint X=322.073 Y=105.865 Z=0
    g233: GeomPoint X=318.073 Y=109.865 Z=0
    g234: Circle CenterX=336.157 CenterY=107.779 CenterZ=0 NormalX=0 NormalY=0 NormalZ=1 AngleXU=0 Radius=1
    g235: Circle CenterX=332.651 CenterY=105.853 CenterZ=0 NormalX=0 NormalY=0 NormalZ=1 AngleXU=0 Radius=1
    g236: Circle CenterX=328.643 CenterY=105.865 CenterZ=0 NormalX=0 NormalY=0 NormalZ=1 AngleXU=0 Radius=1
    g237: BSplineCurve PolesCount=3 KnotsCount=2 Degree=2 IsPeriodic=0
    g238: GeomPoint X=336.157 Y=107.779 Z=0
    g239: GeomPoint X=328.643 Y=105.865 Z=0
    g240: LineSegment StartX=322.073 StartY=124.221 StartZ=0 EndX=362.073 EndY=124.221 EndZ=0
    g241: Circle CenterX=371.567 CenterY=-80.8644 CenterZ=0 NormalX=0 NormalY=0 NormalZ=1 AngleXU=0 Radius=1
    g242: Circle CenterX=375.073 CenterY=-82.7896 CenterZ=0 NormalX=0 NormalY=0 NormalZ=1 AngleXU=0 Radius=1
    g243: Circle CenterX=375.073 CenterY=-78.7896 CenterZ=0 NormalX=0 NormalY=0 NormalZ=1 AngleXU=0 Radius=1
    g244: BSplineCurve PolesCount=3 KnotsCount=2 Degree=2 IsPeriodic=0
    g245: GeomPoint X=371.567 Y=-80.8644 Z=0
    g246: GeomPoint X=375.073 Y=-78.7896 Z=0
    g247: Circle CenterX=321.579 CenterY=-53.4075 CenterZ=0 NormalX=0 NormalY=0 NormalZ=1 AngleXU=0 Radius=1
    g248: Circle CenterX=318.073 CenterY=-51.4823 CenterZ=0 NormalX=0 NormalY=0 NormalZ=1 AngleXU=0 Radius=1
    g249: Circle CenterX=318.073 CenterY=-47.4805 CenterZ=0 NormalX=0 NormalY=0 NormalZ=1 AngleXU=0 Radius=1
    g250: BSplineCurve PolesCount=3 KnotsCount=2 Degree=2 IsPeriodic=0
    g251: GeomPoint X=321.579 Y=-53.4075 Z=0
    g252: GeomPoint X=318.073 Y=-47.4805 Z=0
    g253: LineSegment StartX=371.567 StartY=-80.8644 StartZ=0 EndX=321.579 EndY=-53.4075 EndZ=0
    g254: Circle CenterX=321.579 CenterY=-67.3492 CenterZ=0 NormalX=0 NormalY=0 NormalZ=1 AngleXU=0 Radius=1
    g255: Circle CenterX=318.073 CenterY=-65.424 CenterZ=0 NormalX=0 NormalY=0 NormalZ=1 AngleXU=0 Radius=1
    g256: Circle CenterX=318.073 CenterY=-69.424 CenterZ=0 NormalX=0 NormalY=0 NormalZ=1 AngleXU=0 Radius=1
    g257: BSplineCurve PolesCount=3 KnotsCount=2 Degree=2 IsPeriodic=0
    g258: GeomPoint X=321.579 Y=-67.3492 Z=0
    g259: GeomPoint X=318.073 Y=-69.424 Z=0
    g260: Circle CenterX=362.567 CenterY=-89.8542 CenterZ=0 NormalX=0 NormalY=0 NormalZ=1 AngleXU=0 Radius=1
    g261: Circle CenterX=366.073 CenterY=-91.7794 CenterZ=0 NormalX=0 NormalY=0 NormalZ=1 AngleXU=0 Radius=1
    g262: Circle CenterX=362.073 CenterY=-91.7794 CenterZ=0 NormalX=0 NormalY=0 NormalZ=1 AngleXU=0 Radius=1
    g263: BSplineCurve PolesCount=3 KnotsCount=2 Degree=2 IsPeriodic=0
    g264: GeomPoint X=362.567 Y=-89.8542 Z=0
    g265: GeomPoint X=362.073 Y=-91.7794 Z=0
    g266: Circle CenterX=322.073 CenterY=-91.7794 CenterZ=0 NormalX=0 NormalY=0 NormalZ=1 AngleXU=0 Radius=1
    g267: Circle CenterX=318.073 CenterY=-91.7794 CenterZ=0 NormalX=0 NormalY=0 NormalZ=1 AngleXU=0 Radius=1
    g268: Circle CenterX=318.073 CenterY=-87.7794 CenterZ=0 NormalX=0 NormalY=0 NormalZ=1 AngleXU=0 Radius=1
    g269: BSplineCurve PolesCount=3 KnotsCount=2 Degree=2 IsPeriodic=0
    g270: GeomPoint X=322.073 Y=-91.7794 Z=0
    g271: GeomPoint X=318.073 Y=-87.7794 Z=0
    g272: LineSegment StartX=362.567 StartY=-89.8542 StartZ=0 EndX=321.579 EndY=-67.3492 EndZ=0
    g273: LineSegment StartX=318.073 StartY=-69.424 StartZ=0 EndX=318.073 EndY=-87.7794 EndZ=0
    g274: LineSegment StartX=322.073 StartY=-91.7794 StartZ=0 EndX=362.073 EndY=-91.7794 EndZ=0
    g275: Circle CenterX=2.07281 CenterY=124.221 CenterZ=0 NormalX=0 NormalY=0 NormalZ=1 AngleXU=0 Radius=1
    g276: Circle CenterX=1.57905 CenterY=122.295 CenterZ=0 NormalX=0 NormalY=0 NormalZ=1 AngleXU=0 Radius=1
    g277: BSplineCurve PolesCount=3 KnotsCount=2 Degree=2 IsPeriodic=0
    g278: GeomPoint X=2.07281 Y=124.221 Z=0
    g279: GeomPoint X=1.57905 Y=122.295 Z=0
    g280: Circle CenterX=42.0728 CenterY=124.221 CenterZ=0 NormalX=0 NormalY=0 NormalZ=1 AngleXU=0 Radius=1
    g281: Circle CenterX=46.0728 CenterY=124.221 CenterZ=0 NormalX=0 NormalY=0 NormalZ=1 AngleXU=0 Radius=1
    g282: Circle CenterX=46.0728 CenterY=120.221 CenterZ=0 NormalX=0 NormalY=0 NormalZ=1 AngleXU=0 Radius=1
    g283: BSplineCurve PolesCount=3 KnotsCount=2 Degree=2 IsPeriodic=0
    g284: GeomPoint X=42.0728 Y=124.221 Z=0
    g285: GeomPoint X=46.0728 Y=120.221 Z=0
    g286: Circle CenterX=46.0728 CenterY=109.865 CenterZ=0 NormalX=0 NormalY=0 NormalZ=1 AngleXU=0 Radius=1
    g287: Circle CenterX=46.0728 CenterY=105.865 CenterZ=0 NormalX=0 NormalY=0 NormalZ=1 AngleXU=0 Radius=1
    g288: Circle CenterX=42.0728 CenterY=105.865 CenterZ=0 NormalX=0 NormalY=0 NormalZ=1 AngleXU=0 Radius=1
    g289: BSplineCurve PolesCount=3 KnotsCount=2 Degree=2 IsPeriodic=0
    g290: GeomPoint X=46.0728 Y=109.865 Z=0
    g291: GeomPoint X=42.0728 Y=105.865 Z=0
    g292: Circle CenterX=35.5028 CenterY=105.865 CenterZ=0 NormalX=0 NormalY=0 NormalZ=1 AngleXU=0 Radius=1
    g293: Circle CenterX=31.5028 CenterY=105.865 CenterZ=0 NormalX=0 NormalY=0 NormalZ=1 AngleXU=0 Radius=1
    g294: Circle CenterX=27.9965 CenterY=107.79 CenterZ=0 NormalX=0 NormalY=0 NormalZ=1 AngleXU=0 Radius=1
    g295: BSplineCurve PolesCount=3 KnotsCount=2 Degree=2 IsPeriodic=0
    g296: GeomPoint X=35.5028 Y=105.865 Z=0
    g297: GeomPoint X=27.9965 Y=107.79 Z=0
    g298: LineSegment StartX=2.07281 StartY=124.221 StartZ=0 EndX=42.0728 EndY=124.221 EndZ=0
    g299: LineSegment StartX=46.0728 StartY=120.221 StartZ=0 EndX=46.0728 EndY=109.865 EndZ=0
    g300: LineSegment StartX=42.0728 StartY=105.865 StartZ=0 EndX=35.5028 EndY=105.865 EndZ=0
    g301: LineSegment StartX=27.9965 StartY=107.79 StartZ=0 EndX=1.57905 EndY=122.295 EndZ=0
    g302: Circle CenterX=42.5666 CenterY=-67.3492 CenterZ=0 NormalX=0 NormalY=0 NormalZ=1 AngleXU=0 Radius=1
    g303: Circle CenterX=46.0728 CenterY=-65.424 CenterZ=0 NormalX=0 NormalY=0 NormalZ=1 AngleXU=0 Radius=1
    g304: Circle CenterX=46.0728 CenterY=-69.424 CenterZ=0 NormalX=0 NormalY=0 NormalZ=1 AngleXU=0 Radius=1
    g305: BSplineCurve PolesCount=3 KnotsCount=2 Degree=2 IsPeriodic=0
    g306: GeomPoint X=42.5666 Y=-67.3492 Z=0
    g307: GeomPoint X=46.0728 Y=-69.424 Z=0
    g308: Circle CenterX=46.0728 CenterY=-87.7794 CenterZ=0 NormalX=0 NormalY=0 NormalZ=1 AngleXU=0 Radius=1
    g309: Circle CenterX=46.0728 CenterY=-91.7794 CenterZ=0 NormalX=0 NormalY=0 NormalZ=1 AngleXU=0 Radius=1
    g310: Circle CenterX=42.0728 CenterY=-91.7794 CenterZ=0 NormalX=0 NormalY=0 NormalZ=1 AngleXU=0 Radius=1
    g311: BSplineCurve PolesCount=3 KnotsCount=2 Degree=2 IsPeriodic=0
    g312: GeomPoint X=46.0728 Y=-87.7794 Z=0
    g313: GeomPoint X=42.0728 Y=-91.7794 Z=0
    g314: Circle CenterX=2.07281 CenterY=-91.7794 CenterZ=0 NormalX=0 NormalY=0 NormalZ=1 AngleXU=0 Radius=1
    g315: Circle CenterX=-1.92719 CenterY=-91.7794 CenterZ=0 NormalX=0 NormalY=0 NormalZ=1 AngleXU=0 Radius=1
    g316: Circle CenterX=1.57905 CenterY=-89.8542 CenterZ=0 NormalX=0 NormalY=0 NormalZ=1 AngleXU=0 Radius=1
    g317: BSplineCurve PolesCount=3 KnotsCount=2 Degree=2 IsPeriodic=0
    g318: GeomPoint X=2.07281 Y=-91.7794 Z=0
    g319: GeomPoint X=1.57905 Y=-89.8542 Z=0
    g320: LineSegment StartX=2.07281 StartY=-91.7794 StartZ=0 EndX=42.0728 EndY=-91.7794 EndZ=0
    g321: LineSegment StartX=46.0728 StartY=-87.7794 StartZ=0 EndX=46.0728 EndY=-69.424 EndZ=0
    g322: LineSegment StartX=42.5666 StartY=-67.3492 StartZ=0 EndX=1.57905 EndY=-89.8542 EndZ=0
    g323: Circle CenterX=322.073 CenterY=76.4095 CenterZ=0 NormalX=0 NormalY=0 NormalZ=1 AngleXU=0 Radius=4
    g324: BSplineCurve PolesCount=3 KnotsCount=2 Degree=2 IsPeriodic=0
    g325: GeomPoint X=318.073 Y=72.4095 Z=0
    g326: GeomPoint X=322.073 Y=76.4095 Z=0
    g327: Circle CenterX=375.073 CenterY=72.4095 CenterZ=0 NormalX=0 NormalY=0 NormalZ=1 AngleXU=0 Radius=1
    g328: Circle CenterX=375.073 CenterY=76.4095 CenterZ=0 NormalX=0 NormalY=0 NormalZ=1 AngleXU=0 Radius=1
    g329: Circle CenterX=371.073 CenterY=76.4095 CenterZ=0 NormalX=0 NormalY=0 NormalZ=1 AngleXU=0 Radius=1
    g330: BSplineCurve PolesCount=3 KnotsCount=2 Degree=2 IsPeriodic=0
    g331: GeomPoint X=375.073 Y=72.4095 Z=0
    g332: GeomPoint X=371.073 Y=76.4095 Z=0
    g333: LineSegment StartX=322.073 StartY=76.4095 StartZ=0 EndX=371.073 EndY=76.4095 EndZ=0
    g334: LineSegment StartX=318.073 StartY=72.4095 StartZ=0 EndX=318.073 EndY=-47.4805 EndZ=0
    g335: LineSegment StartX=375.073 StartY=72.4095 StartZ=0 EndX=375.073 EndY=-78.7896 EndZ=0
    g336: ArcOfCircle CenterX=-26.9272 CenterY=22.1087 CenterZ=0 NormalX=0 NormalY=0 NormalZ=1 AngleXU=0 Radius=4 StartAngle=5e-16 EndAngle=3.14159
    g337: LineSegment StartX=-22.9272 StartY=22.1087 StartZ=0 EndX=-18.9272 EndY=-83.7794 EndZ=0
    g338: LineSegment StartX=-34.9272 StartY=-83.7794 StartZ=0 EndX=-30.9272 EndY=22.1087 EndZ=0
    g339: ArcOfCircle CenterX=391.073 CenterY=22.1087 CenterZ=0 NormalX=0 NormalY=0 NormalZ=1 AngleXU=0 Radius=4 StartAngle=0 EndAngle=3.14159
    g340: LineSegment StartX=387.073 StartY=22.1087 StartZ=0 EndX=383.073 EndY=-83.7794 EndZ=0
    g341: LineSegment StartX=395.073 StartY=22.1087 StartZ=0 EndX=399.073 EndY=-83.7794 EndZ=0
    g342: Circle CenterX=-10.9272 CenterY=-78.7794 CenterZ=0 NormalX=0 NormalY=0 NormalZ=1 AngleXU=0 Radius=1
    g343: Circle CenterX=-10.9272 CenterY=-82.7794 CenterZ=0 NormalX=0 NormalY=0 NormalZ=1 AngleXU=0 Radius=1
    g344: Circle CenterX=-7.42095 CenterY=-80.8542 CenterZ=0 NormalX=0 NormalY=0 NormalZ=1 AngleXU=0 Radius=1
    g345: BSplineCurve PolesCount=3 KnotsCount=2 Degree=2 IsPeriodic=0
    g346: GeomPoint X=-10.9272 Y=-78.7794 Z=0
    g347: GeomPoint X=-7.42095 Y=-80.8542 Z=0
    g348: Circle CenterX=42.5666 CenterY=-53.4075 CenterZ=0 NormalX=0 NormalY=0 NormalZ=1 AngleXU=0 Radius=1
    g349: Circle CenterX=46.0728 CenterY=-51.4823 CenterZ=0 NormalX=0 NormalY=0 NormalZ=1 AngleXU=0 Radius=1
    g350: Circle CenterX=46.0728 CenterY=-47.4823 CenterZ=0 NormalX=0 NormalY=0 NormalZ=1 AngleXU=0 Radius=1
    g351: BSplineCurve PolesCount=3 KnotsCount=2 Degree=2 IsPeriodic=0
    g352: GeomPoint X=42.5666 Y=-53.4075 Z=0
    g353: GeomPoint X=46.0728 Y=-47.4823 Z=0
    g354: Circle CenterX=46.0728 CenterY=72.4095 CenterZ=0 NormalX=0 NormalY=0 NormalZ=1 AngleXU=0 Radius=1
    g355: Circle CenterX=46.0728 CenterY=76.4095 CenterZ=0 NormalX=0 NormalY=0 NormalZ=1 AngleXU=0 Radius=1
    g356: Circle CenterX=42.0728 CenterY=76.4095 CenterZ=0 NormalX=0 NormalY=0 NormalZ=1 AngleXU=0 Radius=1
    g357: BSplineCurve PolesCount=3 KnotsCount=2 Degree=2 IsPeriodic=0
    g358: GeomPoint X=46.0728 Y=72.4095 Z=0
    g359: GeomPoint X=42.0728 Y=76.4095 Z=0
    g360: Circle CenterX=-6.92719 CenterY=76.4095 CenterZ=0 NormalX=0 NormalY=0 NormalZ=1 AngleXU=0 Radius=1
    g361: Circle CenterX=-10.9272 CenterY=76.4095 CenterZ=0 NormalX=0 NormalY=0 NormalZ=1 AngleXU=0 Radius=1
    g362: Circle CenterX=-10.9272 CenterY=72.4095 CenterZ=0 NormalX=0 NormalY=0 NormalZ=1 AngleXU=0 Radius=1
    g363: BSplineCurve PolesCount=3 KnotsCount=2 Degree=2 IsPeriodic=0
    g364: GeomPoint X=-6.92719 Y=76.4095 Z=0
    g365: GeomPoint X=-10.9272 Y=72.4095 Z=0
    g366: LineSegment StartX=-10.9272 StartY=72.4095 StartZ=0 EndX=-10.9272 EndY=-78.7794 EndZ=0
    g367: LineSegment StartX=-7.42095 StartY=-80.8542 StartZ=0 EndX=42.5666 EndY=-53.4075 EndZ=0
    g368: LineSegment StartX=46.0728 StartY=-47.4823 StartZ=0 EndX=46.0728 EndY=72.4095 EndZ=0
    g369: LineSegment StartX=42.0728 StartY=76.4095 StartZ=0 EndX=-6.92719 EndY=76.4095 EndZ=0
    g370: LineSegment StartX=-42.9272 StartY=136.221 StartZ=0 EndX=407.073 EndY=136.221 EndZ=0
    g371: LineSegment StartX=232.072 StartY=136.221 StartZ=0 EndX=220.072 EndY=136.221 EndZ=0
    g372: LineSegment StartX=232.072 StartY=136.221 StartZ=0 EndX=232.072 EndY=124.221 EndZ=0
    g373: LineSegment StartX=220.072 StartY=136.221 StartZ=0 EndX=220.072 EndY=124.221 EndZ=0
    g374: LineSegment StartX=220.072 StartY=136.221 StartZ=0 EndX=226.072 EndY=136.221 EndZ=0
    g375: LineSegment StartX=220.072 StartY=136.221 StartZ=0 EndX=220.072 EndY=130.221 EndZ=0
    g376: LineSegment StartX=220.072 StartY=124.221 StartZ=0 EndX=226.072 EndY=124.221 EndZ=0
    g377: LineSegment StartX=232.072 StartY=124.221 StartZ=0 EndX=232.072 EndY=127.221 EndZ=0
    g378: LineSegment StartX=232.072 StartY=136.221 StartZ=0 EndX=232.072 EndY=133.221 EndZ=0
    g379-g383: Circle x5 (B-spline internal-alignment scaffolding for g384; pole/knot coordinates omitted)
    g384: BSplineCurve PolesCount=5 KnotsCount=3 Degree=3 IsPeriodic=0
    g385: GeomPoint X=232.072 Y=133.221 Z=0
    g386: GeomPoint X=223.072 Y=130.221 Z=0
    g387: GeomPoint X=232.072 Y=127.221 Z=0
    g388: LineSegment StartX=189.124 StartY=124.221 StartZ=0 EndX=302.073 EndY=124.221 EndZ=0
    g389: LineSegment StartX=132.072 StartY=136.221 StartZ=0 EndX=132.072 EndY=124.221 EndZ=0
    g390: LineSegment StartX=132.072 StartY=136.221 StartZ=0 EndX=144.072 EndY=136.221 EndZ=0
    g391: LineSegment StartX=144.072 StartY=136.221 StartZ=0 EndX=144.072 EndY=124.221 EndZ=0
    g392: LineSegment StartX=144.072 StartY=136.221 StartZ=0 EndX=138.072 EndY=136.221 EndZ=0
    g393: LineSegment StartX=144.072 StartY=136.221 StartZ=0 EndX=144.072 EndY=130.221 EndZ=0
    g394: LineSegment StartX=132.072 StartY=136.221 StartZ=0 EndX=132.072 EndY=133.221 EndZ=0
    g395: LineSegment StartX=132.072 StartY=133.221 StartZ=0 EndX=132.072 EndY=127.221 EndZ=0
    g396-g400: Circle x5 (B-spline internal-alignment scaffolding for g401; pole/knot coordinates omitted)
    g401: BSplineCurve PolesCount=5 KnotsCount=3 Degree=3 IsPeriodic=0
    g402: GeomPoint X=132.072 Y=133.221 Z=0
    g403: GeomPoint X=141.072 Y=130.221 Z=0
    g404: GeomPoint X=132.072 Y=127.221 Z=0
    g405: LineSegment StartX=132.072 StartY=124.221 StartZ=0 EndX=175.022 EndY=124.221 EndZ=0
    g406: LineSegment StartX=62.0728 StartY=124.221 StartZ=0 EndX=132.072 EndY=124.221 EndZ=0
    g407: LineSegment StartX=132.072 StartY=136.221 StartZ=0 EndX=131.457 EndY=138.832 EndZ=0
    ... +61 more geometry lines
  constraints (808):
    c: Vertical(g0)
    c: Vertical(g1)
    c: Block(g1)
    c: Block(g0)
    c: Weight(g4) = 1
    c: Equal(g4,g5)
    c: Equal(g4,g6)
    c: InternalAlignment(g4,g7)
    c: InternalAlignment(g5,g7)
    c: InternalAlignment(g6,g7)
    c: InternalAlignment(g8,g7)
    c: InternalAlignment(g9,g7)
    c: Weight(g10) = 1
    c: Equal(g10,g11)
    c: Equal(g10,g12)
    c: InternalAlignment(g10,g13)
    c: InternalAlignment(g11,g13)
    c: InternalAlignment(g12,g13)
    c: InternalAlignment(g14,g13)
    c: InternalAlignment(g15,g13)
    c: Block(g13)
    c: Block(g7)
    c: Weight(g16) = 1
    c: Equal(g16,g17)
    c: Equal(g16,g18)
    c: InternalAlignment(g16,g19)
    c: InternalAlignment(g17,g19)
    c: InternalAlignment(g18,g19)
    c: InternalAlignment(g20,g19)
    c: InternalAlignment(g21,g19)
    c: Weight(g22) = 1
    c: Equal(g22,g23)
    c: Equal(g22,g24)
    c: InternalAlignment(g22,g25)
    c: InternalAlignment(g23,g25)
    c: InternalAlignment(g24,g25)
    c: InternalAlignment(g26,g25)
    c: InternalAlignment(g27,g25)
    c: Block(g25)
    c: Block(g19)
    c: Weight(g28) = 1
    c: Equal(g28,g29)
    c: Equal(g28,g30)
    c: InternalAlignment(g28,g31)
    c: InternalAlignment(g29,g31)
    c: InternalAlignment(g30,g31)
    c: InternalAlignment(g32,g31)
    c: InternalAlignment(g33,g31)
    c: Weight(g34) = 1
    c: Equal(g34,g35)
    c: Equal(g34,g36)
    c: InternalAlignment(g34,g37)
    c: InternalAlignment(g35,g37)
    c: InternalAlignment(g36,g37)
    c: InternalAlignment(g38,g37)
    c: InternalAlignment(g39,g37)
    c: Block(g31)
    c: Block(g37)
    c: Coincident(g40,g1)
    c: Coincident(g40,g0)
    c: Horizontal(g40)
    c: Distance(g40) = 450
    c: Weight(g41) = 1
    c: Equal(g41,g42)
    c: Equal(g41,g43)
    c: InternalAlignment(g41,g44)
    c: InternalAlignment(g42,g44)
    c: InternalAlignment(g43,g44)
    c: InternalAlignment(g45,g44)
    c: InternalAlignment(g46,g44)
    c: Block(g44)
    c: Weight(g47) = 1
    c: Equal(g47,g48)
    c: Equal(g47,g49)
    c: InternalAlignment(g47,g50)
    c: InternalAlignment(g48,g50)
    c: InternalAlignment(g49,g50)
    c: InternalAlignment(g51,g50)
    c: InternalAlignment(g52,g50)
    c: Block(g50)
    c: Weight(g53) = 1
    c: Equal(g53,g54)
    c: Equal(g53,g55)
    c: InternalAlignment(g53,g56)
    c: InternalAlignment(g54,g56)
    c: InternalAlignment(g55,g56)
    c: InternalAlignment(g57,g56)
    c: InternalAlignment(g58,g56)
    c: Block(g56)
    c: Weight(g59) = 1
    c: Equal(g59,g60)
    c: Equal(g59,g61)
    c: InternalAlignment(g59,g62)
    c: InternalAlignment(g60,g62)
    c: InternalAlignment(g61,g62)
    c: InternalAlignment(g63,g62)
    c: InternalAlignment(g64,g62)
    c: Block(g62)
    c: Weight(g65) = 1
    c: Equal(g65,g66)
    c: Equal(g65,g67)
    c: InternalAlignment(g65,g68)
    c: InternalAlignment(g66,g68)
    c: InternalAlignment(g67,g68)
    c: InternalAlignment(g69,g68)
    c: InternalAlignment(g70,g68)
    c: Weight(g71) = 1
    c: Equal(g71,g72)
    c: Equal(g71,g73)
    c: InternalAlignment(g71,g74)
    c: InternalAlignment(g72,g74)
    c: InternalAlignment(g73,g74)
    c: InternalAlignment(g75,g74)
    c: InternalAlignment(g76,g74)
    c: Block(g68)
    c: Block(g74)
    c: Coincident(g77,g68)
    c: Coincident(g77,g74)
    c: Vertical(g77)
    c: Coincident(g78,g68)
    c: Coincident(g78,g50)
    c: Coincident(g79,g50)
    c: Coincident(g79,g74)
    c: Weight(g80) = 1
    c: Equal(g80,g81)
    c: Equal(g80,g82)
    c: InternalAlignment(g80,g83)
    c: InternalAlignment(g81,g83)
    c: InternalAlignment(g82,g83)
    c: InternalAlignment(g84,g83)
    c: InternalAlignment(g85,g83)
    c: Weight(g86) = 1
    c: Equal(g86,g87)
    c: Equal(g86,g88)
    c: InternalAlignment(g86,g89)
    c: InternalAlignment(g87,g89)
    c: InternalAlignment(g88,g89)
    c: InternalAlignment(g90,g89)
    c: InternalAlignment(g91,g89)
    c: Block(g83)
    c: Block(g89)
    c: Coincident(g92,g83)
    c: Coincident(g92,g89)
    c: Vertical(g92)
    c: Coincident(g93,g83)
    c: Coincident(g93,g44)
    c: Coincident(g94,g44)
    c: Coincident(g94,g89)
    c: Weight(g95) = 1
    c: Equal(g95,g96)
    c: Equal(g95,g97)
    c: InternalAlignment(g95,g98)
    c: InternalAlignment(g96,g98)
    c: InternalAlignment(g97,g98)
    c: InternalAlignment(g99,g98)
    c: InternalAlignment(g100,g98)
    c: Weight(g101) = 1
    c: Equal(g101,g102)
    c: Equal(g101,g103)
    c: InternalAlignment(g101,g104)
    c: InternalAlignment(g102,g104)
    c: InternalAlignment(g103,g104)
    c: InternalAlignment(g105,g104)
    c: InternalAlignment(g106,g104)
    c: Block(g98)
    c: Block(g104)
    c: Coincident(g107,g98)
    c: Coincident(g107,g104)
    c: Vertical(g107)
    c: Coincident(g108,g104)
    c: Coincident(g108,g62)
    c: Coincident(g109,g62)
    c: Coincident(g109,g98)
    c: Weight(g110) = 1
    c: Equal(g110,g111)
    c: Equal(g110,g112)
    c: InternalAlignment(g110,g113)
    c: InternalAlignment(g111,g113)
    c: InternalAlignment(g112,g113)
    c: InternalAlignment(g114,g113)
    c: InternalAlignment(g115,g113)
    c: Weight(g116) = 1
    c: Equal(g116,g117)
    c: Equal(g116,g118)
    c: InternalAlignment(g116,g119)
    c: InternalAlignment(g117,g119)
    c: InternalAlignment(g118,g119)
    c: InternalAlignment(g120,g119)
    c: InternalAlignment(g121,g119)
    c: Block(g113)
    c: Block(g119)
    c: Coincident(g122,g113)
    c: Coincident(g122,g119)
    c: Vertical(g122)
    c: Coincident(g123,g119)
    c: Coincident(g123,g56)
    c: Coincident(g124,g56)
    c: Coincident(g124,g113)
    c: Weight(g125) = 1
    c: Equal(g125,g126)
    c: Equal(g125,g127)
    c: InternalAlignment(g125,g128)
    c: InternalAlignment(g126,g128)
    c: InternalAlignment(g127,g128)
    c: InternalAlignment(g129,g128)
    c: InternalAlignment(g130,g128)
    c: Weight(g131) = 1
    c: Equal(g131,g132)
    c: Equal(g131,g133)
    c: InternalAlignment(g131,g134)
    c: InternalAlignment(g132,g134)
    c: InternalAlignment(g133,g134)
    c: InternalAlignment(g135,g134)
    c: InternalAlignment(g136,g134)
    c: Weight(g137) = 1
    c: Equal(g137,g138)
    c: Equal(g137,g139)
    c: InternalAlignment(g137,g140)
    c: InternalAlignment(g138,g140)
    c: InternalAlignment(g139,g140)
    c: InternalAlignment(g141,g140)
    c: InternalAlignment(g142,g140)
    c: Weight(g143) = 1
    c: Equal(g143,g144)
    c: Equal(g143,g145)
    c: InternalAlignment(g143,g146)
    c: InternalAlignment(g144,g146)
    c: InternalAlignment(g145,g146)
    c: InternalAlignment(g147,g146)
    c: InternalAlignment(g148,g146)
    c: Block(g146)
    c: Block(g140)
    c: Block(g134)
    c: Block(g128)
    c: Coincident(g149,g25)
    c: Coincident(g149,g146)
    c: Coincident(g150,g146)
    c: Coincident(g150,g140)
    c: Horizontal(g150)
    c: Coincident(g151,g140)
    c: Coincident(g151,g25)
    c: Vertical(g151)
    c: Coincident(g152,g19)
    c: Coincident(g152,g134)
    c: Vertical(g152)
    c: Coincident(g153,g134)
    c: Coincident(g153,g128)
    c: Horizontal(g153)
    c: Coincident(g154,g128)
    c: Coincident(g154,g19)
    c: Weight(g155) = 1
    c: Equal(g155,g156)
    c: Equal(g155,g157)
    c: InternalAlignment(g155,g158)
    c: InternalAlignment(g156,g158)
    c: InternalAlignment(g157,g158)
    c: InternalAlignment(g159,g158)
    c: InternalAlignment(g160,g158)
    c: Weight(g161) = 1
    c: Equal(g161,g162)
    c: Equal(g161,g163)
    c: InternalAlignment(g161,g164)
    c: InternalAlignment(g162,g164)
    c: InternalAlignment(g163,g164)
    c: InternalAlignment(g165,g164)
    c: InternalAlignment(g166,g164)
    c: Weight(g167) = 1
    c: Equal(g167,g168)
    c: Equal(g167,g169)
    c: InternalAlignment(g167,g170)
    c: InternalAlignment(g168,g170)
    c: InternalAlignment(g169,g170)
    c: InternalAlignment(g171,g170)
    c: InternalAlignment(g172,g170)
    c: Weight(g173) = 1
    c: Equal(g173,g174)
    c: Equal(g173,g175)
    c: InternalAlignment(g173,g176)
    c: InternalAlignment(g174,g176)
    c: InternalAlignment(g175,g176)
    c: InternalAlignment(g177,g176)
    c: InternalAlignment(g178,g176)
    c: Block(g176)
    c: Block(g170)
    c: Block(g164)
    c: Block(g158)
    c: Coincident(g179,g170)
    c: Coincident(g179,g7)
    c: Vertical(g179)
    c: Coincident(g180,g13)
    c: Coincident(g180,g164)
    c: Vertical(g180)
    c: Coincident(g181,g158)
    c: Coincident(g181,g13)
    c: Coincident(g182,g7)
    c: Weight(g183) = 1
    c: Equal(g183,g184)
    c: Equal(g183,g185)
    c: InternalAlignment(g183,g186)
    c: InternalAlignment(g184,g186)
    c: InternalAlignment(g185,g186)
    c: InternalAlignment(g187,g186)
    c: InternalAlignment(g188,g186)
    c: Weight(g189) = 1
    c: Equal(g189,g190)
    c: Equal(g189,g191)
    c: InternalAlignment(g189,g192)
    c: InternalAlignment(g190,g192)
    c: InternalAlignment(g191,g192)
    c: InternalAlignment(g193,g192)
    c: InternalAlignment(g194,g192)
    c: Block(g192)
    c: Block(g186)
    c: Coincident(g195,g192)
    c: Coincident(g195,g31)
    c: Coincident(g196,g31)
    c: Coincident(g196,g186)
    c: Coincident(g197,g186)
    c: Coincident(g197,g192)
    c: Vertical(g197)
    c: Weight(g198) = 1
    c: Equal(g198,g199)
    c: Equal(g198,g200)
    c: InternalAlignment(g198,g201)
    c: InternalAlignment(g199,g201)
    c: InternalAlignment(g200,g201)
    c: InternalAlignment(g202,g201)
    c: InternalAlignment(g203,g201)
    c: Weight(g204) = 1
    c: Equal(g204,g205)
    c: Equal(g204,g206)
    c: InternalAlignment(g204,g207)
    c: InternalAlignment(g205,g207)
    c: InternalAlignment(g206,g207)
    c: InternalAlignment(g208,g207)
    c: InternalAlignment(g209,g207)
    c: Block(g207)
    c: Block(g201)
    c: Coincident(g210,g201)
    c: Coincident(g210,g37)
    c: Coincident(g211,g37)
    c: Coincident(g211,g207)
    c: Coincident(g212,g207)
    c: Coincident(g212,g201)
    c: Vertical(g212)
    c: Horizontal(g213)
    c: Block(g213)
    c: Vertical(g214)
    c: Block(g214)
    c: Block(g215)
    c: Weight(g216) = 1
    c: Equal(g216,g217)
    c: Equal(g216,g218)
    c: InternalAlignment(g216,g219)
    c: InternalAlignment(g217,g219)
    c: InternalAlignment(g218,g219)
    c: InternalAlignment(g220,g219)
    c: InternalAlignment(g221,g219)
    c: Weight(g222) = 1
    c: Equal(g222,g223)
    c: Equal(g222,g224)
    c: InternalAlignment(g222,g225)
    c: InternalAlignment(g223,g225)
    c: InternalAlignment(g224,g225)
    c: InternalAlignment(g226,g225)
    c: InternalAlignment(g227,g225)
    c: Weight(g228) = 1
    c: Equal(g228,g229)
    c: Equal(g228,g230)
    c: InternalAlignment(g228,g231)
    c: InternalAlignment(g229,g231)
    c: InternalAlignment(g230,g231)
    c: InternalAlignment(g232,g231)
    c: InternalAlignment(g233,g231)
    c: Weight(g234) = 1
    c: Equal(g234,g235)
    c: Equal(g234,g236)
    c: InternalAlignment(g234,g237)
    c: InternalAlignment(g235,g237)
    c: InternalAlignment(g236,g237)
    c: InternalAlignment(g238,g237)
    c: InternalAlignment(g239,g237)
    c: Block(g219)
    c: Block(g225)
    c: Block(g231)
    c: Block(g237)
    c: Coincident(g240,g225)
    c: Coincident(g240,g219)
    c: Horizontal(g240)
    c: Block(g182)
    c: Weight(g241) = 1
    c: Equal(g241,g242)
    c: Equal(g241,g243)
    c: InternalAlignment(g241,g244)
    c: InternalAlignment(g242,g244)
    c: InternalAlignment(g243,g244)
    c: InternalAlignment(g245,g244)
    c: InternalAlignment(g246,g244)
    c: Weight(g247) = 1
    c: Equal(g247,g248)
    c: Equal(g247,g249)
    c: InternalAlignment(g247,g250)
    c: InternalAlignment(g248,g250)
    c: InternalAlignment(g249,g250)
    c: InternalAlignment(g251,g250)
    c: InternalAlignment(g252,g250)
    c: Block(g244)
    c: Block(g250)
    c: Coincident(g253,g244)
    c: Coincident(g253,g250)
    c: Weight(g254) = 1
    c: Equal(g254,g255)
    c: Equal(g254,g256)
    c: InternalAlignment(g254,g257)
    c: InternalAlignment(g255,g257)
    c: InternalAlignment(g256,g257)
    c: InternalAlignment(g258,g257)
    c: InternalAlignment(g259,g257)
    c: Weight(g260) = 1
    c: Equal(g260,g261)
    c: Equal(g260,g262)
    c: InternalAlignment(g260,g263)
    c: InternalAlignment(g261,g263)
    c: InternalAlignment(g262,g263)
    c: InternalAlignment(g264,g263)
    c: InternalAlignment(g265,g263)
    c: Weight(g266) = 1
    c: Equal(g266,g267)
    c: Equal(g266,g268)
    c: InternalAlignment(g266,g269)
    c: InternalAlignment(g267,g269)
    c: InternalAlignment(g268,g269)
    c: InternalAlignment(g270,g269)
    c: InternalAlignment(g271,g269)
    c: Block(g269)
    c: Block(g263)
    c: Block(g257)
    c: Coincident(g272,g263)
    c: Coincident(g272,g257)
    c: Coincident(g273,g257)
    c: Coincident(g273,g269)
    c: Vertical(g273)
    c: Coincident(g274,g269)
    c: Coincident(g274,g263)
    c: Horizontal(g274)
    c: Weight(g275) = 1
    c: Equal(g275,g276)
    c: InternalAlignment(g275,g277)
    c: InternalAlignment(g276,g277)
    c: InternalAlignment(g278,g277)
    c: InternalAlignment(g279,g277)
    c: Weight(g280) = 1
    c: InternalAlignment(g281,g283)
    c: InternalAlignment(g282,g283)
    c: InternalAlignment(g284,g283)
    c: InternalAlignment(g285,g283)
    c: Weight(g286) = 1
    c: Equal(g286,g287)
    c: Equal(g286,g288)
    c: InternalAlignment(g286,g289)
    c: InternalAlignment(g287,g289)
    c: InternalAlignment(g288,g289)
    c: InternalAlignment(g290,g289)
    c: InternalAlignment(g291,g289)
    c: Equal(g292,g293)
    c: Equal(g292,g294)
    c: InternalAlignment(g292,g295)
    c: InternalAlignment(g293,g295)
    c: InternalAlignment(g294,g295)
    c: InternalAlignment(g296,g295)
    c: InternalAlignment(g297,g295)
    c: Block(g283)
    c: Block(g289)
    c: Block(g295)
    c: Block(g277)
    c: Coincident(g298,g277)
    c: Coincident(g298,g283)
    c: Horizontal(g298)
    c: Coincident(g299,g283)
    c: Coincident(g299,g289)
    c: Vertical(g299)
    c: Coincident(g300,g289)
    c: Coincident(g300,g295)
    c: Horizontal(g300)
    c: Coincident(g301,g295)
    c: Coincident(g301,g277)
    c: Weight(g302) = 1
    c: Equal(g302,g303)
    c: Equal(g302,g304)
    c: InternalAlignment(g302,g305)
    c: InternalAlignment(g303,g305)
    c: InternalAlignment(g304,g305)
    c: InternalAlignment(g306,g305)
    c: InternalAlignment(g307,g305)
    c: Weight(g308) = 1
    c: Equal(g308,g309)
    c: Equal(g308,g310)
    c: InternalAlignment(g308,g311)
    c: InternalAlignment(g309,g311)
    c: InternalAlignment(g310,g311)
    c: InternalAlignment(g312,g311)
    c: Weight(g314) = 1
    c: Equal(g314,g315)
    c: Equal(g314,g316)
    c: InternalAlignment(g314,g317)
    c: InternalAlignment(g315,g317)
    c: InternalAlignment(g316,g317)
    c: InternalAlignment(g318,g317)
    c: InternalAlignment(g319,g317)
    c: Block(g317)
    c: Block(g311)
    c: Block(g305)
    c: Coincident(g320,g317)
    c: Coincident(g320,g311)
    c: Horizontal(g320)
    c: Coincident(g321,g311)
    c: Coincident(g321,g305)
    c: Vertical(g321)
    c: Coincident(g322,g305)
    c: Coincident(g322,g317)
    c: InternalAlignment(g323,g324)
    c: InternalAlignment(g325,g324)
    c: InternalAlignment(g326,g324)
    c: Block(g324)
    c: Equal(g327,g328)
    c: Equal(g327,g329)
    c: InternalAlignment(g327,g330)
    c: InternalAlignment(g328,g330)
    c: InternalAlignment(g329,g330)
    c: InternalAlignment(g331,g330)
    c: InternalAlignment(g332,g330)
    c: Block(g330)
    c: Coincident(g333,g324)
    c: Horizontal(g333)
    c: Block(g333)
    c: Coincident(g334,g324)
    c: Coincident(g334,g250)
    c: Vertical(g334)
    c: Coincident(g335,g330)
    c: Coincident(g335,g244)
    c: Vertical(g335)
    c: Block(g336)
    c: Block(g2)
    c: Distance(g334) = 119.89
    c: Coincident(g337,g336)
    c: Coincident(g337,g2)
    c: Coincident(g338,g2)
    c: Coincident(g338,g336)
    c: Block(g3)
    c: Block(g339)
    c: Coincident(g340,g339)
    c: Coincident(g340,g3)
    c: Coincident(g341,g339)
    c: Coincident(g341,g3)
    c: Block(g341)
    c: Block(g340)
    c: Weight(g342) = 1
    c: Equal(g342,g344)
    c: InternalAlignment(g342,g345)
    c: InternalAlignment(g343,g345)
    c: InternalAlignment(g344,g345)
    c: InternalAlignment(g346,g345)
    c: InternalAlignment(g347,g345)
    c: InternalAlignment(g352,g351)
    c: InternalAlignment(g353,g351)
    c: InternalAlignment(g355,g357)
    c: Horizontal(g369)
    c: Coincident(g370,g0)
    c: Horizontal(g370)
    c: Block(g370)
    c: Distance(g370) = 450
    c: Horizontal(g371)
    c: Distance(g371) = 12
    c: Coincident(g373,g371)
    c: Vertical(g373)
    c: Horizontal(g374)
    c: Vertical(g375)
    c: Distance(g375) = 6
    c: Coincident(g375,g371)
    c: Coincident(g374,g371)
    c: Block(g373)
    c: Coincident(g376,g373)
    c: Horizontal(g376)
    c: Distance(g376) = 6
    c: Vertical(g377)
    c: Distance(g377) = 3
    c: Vertical(g378)
    c: Distance(g378) = 3
    c: Coincident(g372,g377)
    c: Coincident(g384,g378)
    c: Weight(g379) = 1
    c: Equal(g379,g380)
    c: Coincident(g380,g374)
    c: Equal(g379,g381)
    c: Coincident(g381,g375)
    c: Equal(g379,g382)
    c: Coincident(g382,g376)
    c: Equal(g379,g383)
    c: Coincident(g384,g377)
    c: InternalAlignment(g379-g383 -> g384) x5
    c: InternalAlignment(g385,g384)
    c: InternalAlignment(g386,g384)
    c: InternalAlignment(g387,g384)
    c: Coincident(g388,g164)
    c: Coincident(g388,g158)
    c: Coincident(g392,g390)
    c: Vertical(g393)
    c: Distance(g393) = 6
    c: Coincident(g393,g390)
    c: Vertical(g394)
    c: Distance(g394) = 3
    c: Vertical(g395)
    c: Distance(g395) = 6
    c: Coincident(g395,g394)
    c: Coincident(g401,g394)
    c: Weight(g396) = 1
    c: Equal(g396,g397)
    c: Coincident(g397,g392)
    c: Equal(g396,g398)
    c: Coincident(g398,g393)
    c: Equal(g396,g399)
    c: Equal(g396,g400)
    c: Coincident(g401,g395)
    c: InternalAlignment(g396-g400 -> g401) x5
    c: InternalAlignment(g402,g401)
    c: InternalAlignment(g403,g401)
    c: InternalAlignment(g404,g401)
    c: Coincident(g405,g389)
    c: Coincident(g405,g170)
    c: Horizontal(g405)
    c: Block(g401)
    c: Coincident(g406,g176)
    c: Coincident(g406,g389)
    c: Horizontal(g406)
    c: Block(g405)
    c: Coincident(g408,g389)
    c: PointOnObject(g408,g153)
    c: Vertical(g408)
    c: Block(g409)
    c: Coincident(g410,g409)
    c: Vertical(g410)
    c: PointOnObject(g410,g40)
    c: Block(g410)
    c: Coincident(g411,g409)
    c: Vertical(g411)
    c: Block(g411)
    c: Vertical(g412)
    c: Distance(g412) = 3
    c: Equal(g379,g415) = 1
    c: Equal(g415,g416)
    c: InternalAlignment(g415,g417)
    c: InternalAlignment(g416,g417)
    c: InternalAlignment(g413,g417)
    c: InternalAlignment(g414,g417)
    c: InternalAlignment(g418,g417)
    c: Block(g417)
    c: Coincident(g418,g412)
    c: Coincident(g419,g417)
    c: PointOnObject(g419,g150)
    c: Vertical(g419)
    c: Distance(g420) = 3
    c: Block(g420)
    c: Distance(g421) = 3
    c: Parallel(g421,g420)
    c: Coincident(g421,g420)
    c: Coincident(g422,g420)
    c: Perpendicular(g422,g420)
    c: Distance(g422) = 3
    c: Coincident(g423,g421)
    c: Perpendicular(g423,g421)
    c: Distance(g423) = 3
    c: Coincident(g424,g420)
    c: Perpendicular(g424,g421)
    c: Distance(g424) = 6
    c: Coincident(g425,g424)
    c: PointOnObject(g423,g425)
    c: Coincident(g426,g420)
    c: PointOnObject(g426,g79)
    c: Block(g426)
    c: Distance(g427) = 2.76
    c: Coincident(g428,g427)
    c: Parallel(g427,g428)
    c: PointOnObject(g428,g181)
    c: Distance(g428) = 2.41
    c: Block(g428)
    c: Coincident(g429,g427)
    c: Distance(g429) = 6.6
    c: Perpendicular(g429,g428)
    c: Distance(g430) = 6.6
    c: Coincident(g431,g429)
    c: Coincident(g431,g430)
    c: Block(g432)
    c: Coincident(g433,g432)
    c: Vertical(g433)
    c: Distance(g433) = 3.6
    c: Coincident(g434,g427)
    c: Parallel(g427,g434)
    c: PointOnObject(g434,g78)
    c: Block(g434)
    c: Coincident(g435,g421)
    c: Parallel(g435,g421)
    c: PointOnObject(g435,g211)
    c: Block(g435)
    c: Coincident(g436,g435)
    c: Vertical(g436)
    c: PointOnObject(g436,g210)
    c: Coincident(g437,g436)
    c: Perpendicular(g437,g210)
    c: Distance(g437) = 3
    c: Coincident(g438,g437)
    c: Block(g437)
    c: Distance(g438) = 3
    c: Parallel(g437,g438)
    c: Coincident(g439,g438)
    c: Distance(g439) = 3
    c: Parallel(g438,g439)
    c: Coincident(g440,g439)
    c: Parallel(g440,g437)
    c: PointOnObject(g440,g124)
    c: PointOnObject(g441,g53)
    c: Tangent(g440,g441)
    c: Coincident(g442,g439)
    c: Perpendicular(g442,g439)
    c: Coincident(g443,g437)
    c: Parallel(g443,g442)
    c: Distance(g443) = 3
    c: Distance(g442) = 3
    c: PointOnObject(g442,g444)
    c: Block(g444)
    c: PointOnObject(g445,g123)
    c: Perpendicular(g123,g445)
    c: Distance(g445) = 2.41
    c: Block(g445)
    c: Coincident(g446,g445)
    c: Perpendicular(g123,g446)
    c: Distance(g446) = 2.76
    c: Coincident(g447,g446)
    c: Perpendicular(g123,g447)
    c: PointOnObject(g447,g149)
    c: Coincident(g448,g445)
    c: Parallel(g123,g448)
    c: Distance(g448) = 6.6
    c: Coincident(g449,g446)
    c: Parallel(g123,g449)
    c: Coincident(g450,g448)
    c: Distance(g449) = 6.6
    c: Coincident(g449,g450)
    c: Block(g149)
    c: Block(g124)
    c: Block(g211)
    c: Block(g181)
    c: Block(g78)
    c: Block(g79)
    c: Block(g430)
    c: Coincident(g451,g447)
    c: Distance(g451) = 46
    c: Parallel(g149,g451)
    c: Coincident(g452,g451)
    c: Horizontal(g452)
    c: PointOnObject(g452,g154)
    c: Coincident(g453,g451)
    c: Vertical(g453)
    c: Distance(g453) = 9
    c: Block(g452)
    c: PointOnObject(g454,g93)
    c: Distance(g455) = 6.6
    c: Distance(g456) = 6.6
    c: Block(g454)
    c: Coincident(g457,g456)
    c: Coincident(g457,g455)
    c: Perpendicular(g457,g182)
    c: Coincident(g458,g455)
    c: Perpendicular(g458,g182)
    c: PointOnObject(g458,g182)
    c: Block(g458)
    c: Block(g457)
    c: Block(g456)
    c: PointOnObject(g459,g196)
    c: Perpendicular(g196,g459)
    c: Distance(g459) = 3
    c: Coincident(g460,g459)
    c: Perpendicular(g196,g460)
    c: Distance(g460) = 3
    c: Coincident(g461,g460)
    c: Perpendicular(g196,g461)
    c: Distance(g461) = 3
    c: Coincident(g462,g461)
    c: Tangent(g462,g41)
    c: PointOnObject(g462,g94)
    c: Block(g462)
    c: Block(g459)
    c: Coincident(g463,g459)
    c: Parallel(g196,g463)
    c: Distance(g463) = 3
    c: Coincident(g464,g461)
    c: Distance(g464) = 3
    c: Parallel(g196,g464)
    c: Coincident(g465,g460)
    c: Distance(g465) = 6
    c: Parallel(g465,g196)
    c: Coincident(g466,g465)
    c: PointOnObject(g464,g466)
    c: Block(g466)
    c: Coincident(g467,g458)
    c: Vertical(g467)
    c: PointOnObject(g467,g195)
    c: Coincident(g468,g467)
    c: Perpendicular(g195,g468)
FEATURE [Sketcher::SketchObject] Sketch004  label="rightSideBottom"
  FullyConstrained = false
  sketch-geometry (91):
    g0: ArcOfCircle CenterX=391.073 CenterY=-83.7794 CenterZ=0 NormalX=0 NormalY=0 NormalZ=1 AngleXU=0 Radius=8 StartAngle=3.14159 EndAngle=6.28319
    g1: Circle CenterX=306.073 CenterY=-81.8102 CenterZ=0 NormalX=0 NormalY=0 NormalZ=1 AngleXU=0 Radius=1
    g2: Circle CenterX=306.073 CenterY=-77.8102 CenterZ=0 NormalX=0 NormalY=0 NormalZ=1 AngleXU=0 Radius=1
    g3: Circle CenterX=302.567 CenterY=-42.9683 CenterZ=0 NormalX=0 NormalY=0 NormalZ=1 AngleXU=0 Radius=1
    g4: Circle CenterX=306.073 CenterY=-44.8935 CenterZ=0 NormalX=0 NormalY=0 NormalZ=1 AngleXU=0 Radius=1
    g5: Circle CenterX=306.073 CenterY=-40.8935 CenterZ=0 NormalX=0 NormalY=0 NormalZ=1 AngleXU=0 Radius=1
    g6: BSplineCurve PolesCount=3 KnotsCount=2 Degree=2 IsPeriodic=0
    g7: GeomPoint X=302.567 Y=-42.9683 Z=0
    g8: GeomPoint X=306.073 Y=-40.8935 Z=0
    g9: Circle CenterX=371.567 CenterY=-80.8644 CenterZ=0 NormalX=0 NormalY=0 NormalZ=1 AngleXU=0 Radius=1
    g10: Circle CenterX=375.073 CenterY=-82.7896 CenterZ=0 NormalX=0 NormalY=0 NormalZ=1 AngleXU=0 Radius=1
    g11: Circle CenterX=375.073 CenterY=-78.7896 CenterZ=0 NormalX=0 NormalY=0 NormalZ=1 AngleXU=0 Radius=1
    g12: GeomPoint X=371.567 Y=-80.8644 Z=0
    g13: GeomPoint X=375.073 Y=-78.7896 Z=0
    g14: Circle CenterX=318.073 CenterY=-51.4823 CenterZ=0 NormalX=0 NormalY=0 NormalZ=1 AngleXU=0 Radius=1
    g15: Circle CenterX=318.073 CenterY=-47.4805 CenterZ=0 NormalX=0 NormalY=0 NormalZ=1 AngleXU=0 Radius=1
    g16: GeomPoint X=321.579 Y=-53.4075 Z=0
    g17: GeomPoint X=318.073 Y=-47.4805 Z=0
    g18: Circle CenterX=321.579 CenterY=-67.3492 CenterZ=0 NormalX=0 NormalY=0 NormalZ=1 AngleXU=0 Radius=1
    g19: Circle CenterX=318.073 CenterY=-65.424 CenterZ=0 NormalX=0 NormalY=0 NormalZ=1 AngleXU=0 Radius=1
    g20: Circle CenterX=318.073 CenterY=-69.424 CenterZ=0 NormalX=0 NormalY=0 NormalZ=1 AngleXU=0 Radius=1
    g21: GeomPoint X=321.579 Y=-67.3492 Z=0
    g22: GeomPoint X=318.073 Y=-69.424 Z=0
    g23: Circle CenterX=362.567 CenterY=-89.8542 CenterZ=0 NormalX=0 NormalY=0 NormalZ=1 AngleXU=0 Radius=1
    g24: Circle CenterX=366.073 CenterY=-91.7794 CenterZ=0 NormalX=0 NormalY=0 NormalZ=1 AngleXU=0 Radius=1
    g25: Circle CenterX=362.073 CenterY=-91.7794 CenterZ=0 NormalX=0 NormalY=0 NormalZ=1 AngleXU=0 Radius=1
    g26: GeomPoint X=362.567 Y=-89.8542 Z=0
    g27: GeomPoint X=362.073 Y=-91.7794 Z=0
    g28: Circle CenterX=322.073 CenterY=-91.7794 CenterZ=0 NormalX=0 NormalY=0 NormalZ=1 AngleXU=0 Radius=1
    g29: Circle CenterX=318.073 CenterY=-91.7794 CenterZ=0 NormalX=0 NormalY=0 NormalZ=1 AngleXU=0 Radius=1
    g30: Circle CenterX=318.073 CenterY=-87.7794 CenterZ=0 NormalX=0 NormalY=0 NormalZ=1 AngleXU=0 Radius=1
    g31: GeomPoint X=322.073 Y=-91.7794 Z=0
    g32: GeomPoint X=318.073 Y=-87.7794 Z=0
    g33: ArcOfCircle CenterX=391.073 CenterY=22.1087 CenterZ=0 NormalX=0 NormalY=0 NormalZ=1 AngleXU=0 Radius=4 StartAngle=0 EndAngle=3.14159
    g34: LineSegment StartX=387.073 StartY=22.1087 StartZ=0 EndX=383.073 EndY=-83.7794 EndZ=0
    g35: LineSegment StartX=395.073 StartY=22.1087 StartZ=0 EndX=399.073 EndY=-83.7794 EndZ=0
    g36: LineSegment StartX=232.072 StartY=-103.779 StartZ=0 EndX=232.072 EndY=-100.779 EndZ=0
    g37: GeomPoint X=232.072 Y=-94.7794 Z=0
    g38: GeomPoint X=223.072 Y=-97.7794 Z=0
    g39: Circle CenterX=232.072 CenterY=-94.7794 CenterZ=0 NormalX=0 NormalY=0 NormalZ=1 AngleXU=0 Radius=1
    g40: Circle CenterX=232.072 CenterY=-100.779 CenterZ=0 NormalX=0 NormalY=0 NormalZ=1 AngleXU=0 Radius=1
    g41: BSplineCurve PolesCount=5 KnotsCount=3 Degree=3 IsPeriodic=0
    g42: GeomPoint X=232.072 Y=-100.779 Z=0
    g43: LineSegment StartX=232.072 StartY=-94.7794 StartZ=0 EndX=232.072 EndY=-91.7794 EndZ=0
    g44: LineSegment StartX=245.072 StartY=-31.3037 StartZ=0 EndX=243.535 EndY=-33.1602 EndZ=0
    g45: LineSegment StartX=241.775 StartY=-35.2862 StartZ=0 EndX=240.266 EndY=-37.1092 EndZ=0
    g46: LineSegment StartX=243.535 StartY=-33.1602 StartZ=0 EndX=248.619 EndY=-37.3688 EndZ=0
    g47: LineSegment StartX=241.775 StartY=-35.2862 StartZ=0 EndX=246.859 EndY=-39.4949 EndZ=0
    g48: LineSegment StartX=248.619 StartY=-37.3688 StartZ=0 EndX=246.859 EndY=-39.4949 EndZ=0
    g49: LineSegment StartX=232.072 StartY=-103.779 StartZ=0 EndX=407.073 EndY=-103.779 EndZ=0
    g50: LineSegment StartX=299.888 StartY=-86.6413 StartZ=0 EndX=240.266 EndY=-37.1092 EndZ=0
    g51: LineSegment StartX=245.072 StartY=-11.4025 StartZ=0 EndX=302.567 EndY=-42.9683 EndZ=0
    g52: BSplineCurve PolesCount=3 KnotsCount=2 Degree=2 IsPeriodic=0
    g53: BSplineCurve PolesCount=3 KnotsCount=2 Degree=2 IsPeriodic=0
    g54: LineSegment StartX=321.579 StartY=-53.4075 StartZ=0 EndX=371.567 EndY=-80.8644 EndZ=0
    g55: BSplineCurve PolesCount=3 KnotsCount=2 Degree=2 IsPeriodic=0
    g56: BSplineCurve PolesCount=3 KnotsCount=2 Degree=2 IsPeriodic=0
    g57: BSplineCurve PolesCount=3 KnotsCount=2 Degree=2 IsPeriodic=0
    g58: LineSegment StartX=318.073 StartY=-69.424 StartZ=0 EndX=318.073 EndY=-87.7794 EndZ=0
    g59: LineSegment StartX=321.579 StartY=-67.3492 StartZ=0 EndX=362.567 EndY=-89.8542 EndZ=0
    g60: LineSegment StartX=362.073 StartY=-91.7794 StartZ=0 EndX=322.073 EndY=-91.7794 EndZ=0
    g61: BSplineCurve PolesCount=3 KnotsCount=2 Degree=2 IsPeriodic=0
    g62: BSplineCurve PolesCount=3 KnotsCount=2 Degree=2 IsPeriodic=0
    g63: LineSegment StartX=245.072 StartY=-31.3037 StartZ=0 EndX=302.996 EndY=-79.2541 EndZ=0
    g64: LineSegment StartX=302.567 StartY=-56.9099 StartZ=0 EndX=239.193 EndY=-22.1109 EndZ=0
    g65: LineSegment StartX=306.073 StartY=-62.8351 StartZ=0 EndX=306.073 EndY=-77.8102 EndZ=0
    g66: BSplineCurve PolesCount=3 KnotsCount=2 Degree=2 IsPeriodic=0
    g67: LineSegment StartX=298.776 StartY=-91.7794 StartZ=0 EndX=232.072 EndY=-91.7794 EndZ=0
    g68: LineSegment StartX=245.072 StartY=-11.4025 StartZ=0 EndX=243.628 EndY=-14.0323 EndZ=0
    g69: LineSegment StartX=240.741 StartY=-19.2917 StartZ=0 EndX=239.193 EndY=-22.1109 EndZ=0
    g70: LineSegment StartX=243.628 StartY=-14.0323 StartZ=0 EndX=246.258 EndY=-15.476 EndZ=0
    g71: LineSegment StartX=240.741 StartY=-19.2917 StartZ=0 EndX=243.37 EndY=-20.7355 EndZ=0
    g72: ArcOfCircle CenterX=247.444 CenterY=-19.5495 CenterZ=0 NormalX=0 NormalY=0 NormalZ=1 AngleXU=0 Radius=4.24264 StartAngle=3.4249 EndAngle=8.13729
    g73: LineSegment StartX=407.073 StartY=-103.779 StartZ=0 EndX=407.073 EndY=48.2206 EndZ=0
    g74: LineSegment StartX=375.073 StartY=48.2206 StartZ=0 EndX=375.073 EndY=-78.7896 EndZ=0
    g75: LineSegment StartX=375.073 StartY=48.2206 StartZ=0 EndX=382.073 EndY=48.2206 EndZ=0
    g76: LineSegment StartX=407.073 StartY=48.2206 StartZ=0 EndX=400.073 EndY=48.2206 EndZ=0
    g77: LineSegment StartX=394.073 StartY=48.2206 StartZ=0 EndX=394.073 EndY=52.2206 EndZ=0
    g78: LineSegment StartX=388.073 StartY=48.2206 StartZ=0 EndX=388.073 EndY=58.2206 EndZ=0
    g79: ArcOfCircle CenterX=385.073 CenterY=61.2206 CenterZ=0 NormalX=0 NormalY=0 NormalZ=1 AngleXU=0 Radius=4.24264 StartAngle=5.49779 EndAngle=10.2102
    g80: ArcOfCircle CenterX=397.073 CenterY=55.2206 CenterZ=0 NormalX=0 NormalY=0 NormalZ=1 AngleXU=0 Radius=4.24264 StartAngle=5.49779 EndAngle=10.2102
    g81: LineSegment StartX=382.073 StartY=58.2206 StartZ=0 EndX=382.073 EndY=48.2206 EndZ=0
    g82: LineSegment StartX=400.073 StartY=52.2206 StartZ=0 EndX=400.073 EndY=48.2206 EndZ=0
    g83: LineSegment StartX=394.073 StartY=48.2206 StartZ=0 EndX=388.073 EndY=48.2206 EndZ=0
    g84: LineSegment StartX=306.073 StartY=-40.8935 StartZ=0 EndX=306.073 EndY=-27.5935 EndZ=0
    g85: LineSegment StartX=318.073 StartY=-27.5935 StartZ=0 EndX=318.073 EndY=-47.4805 EndZ=0
    g86: LineSegment StartX=306.073 StartY=-27.5935 StartZ=0 EndX=310.073 EndY=-27.5935 EndZ=0
    g87: LineSegment StartX=318.073 StartY=-27.5935 StartZ=0 EndX=314.073 EndY=-27.5935 EndZ=0
    g88: LineSegment StartX=310.073 StartY=-27.5935 StartZ=0 EndX=310.073 EndY=-31.5935 EndZ=0
    g89: LineSegment StartX=314.073 StartY=-27.5935 StartZ=0 EndX=314.073 EndY=-31.5935 EndZ=0
    g90: ArcOfCircle CenterX=312.073 CenterY=-33.5935 CenterZ=0 NormalX=0 NormalY=0 NormalZ=1 AngleXU=0 Radius=2.82843 StartAngle=2.35619 EndAngle=7.06858
  constraints (121):
    c: Distance(g44) = 2.41
    c: Block(g44)
    c: Coincident(g46,g44)
    c: Coincident(g49,g36)
    c: Horizontal(g49)
    c: Block(g49)
    c: Coincident(g50,g45)
    c: Block(g50)
    c: Coincident(g51,g6)
    c: Block(g51)
    c: Coincident(g54,g52)
    c: Coincident(g54,g53)
    c: Coincident(g58,g56)
    c: Coincident(g58,g57)
    c: Vertical(g58)
    c: Coincident(g59,g56)
    c: Coincident(g59,g55)
    c: Coincident(g60,g55)
    c: Coincident(g60,g57)
    c: Horizontal(g60)
    c: Block(g61)
    c: Block(g62)
    c: Coincident(g63,g44)
    c: Coincident(g63,g62)
    c: Coincident(g64,g61)
    c: Coincident(g65,g61)
    c: Coincident(g65,g62)
    c: Vertical(g65)
    c: Block(g66)
    c: Coincident(g66,g50)
    c: Coincident(g67,g66)
    c: Coincident(g67,g43)
    c: Horizontal(g67)
    c: Coincident(g68,g51)
    c: Perpendicular(g68,g51)
    c: Coincident(g69,g64)
    c: Coincident(g70,g68)
    c: Distance(g70) = 3
    c: Distance(g71) = 3
    c: Perpendicular(g68,g70)
    c: Coincident(g72,g70)
    c: Coincident(g72,g71)
    c: Block(g72)
    c: Block(g69)
    c: Block(g71)
    c: Block(g54)
    c: Block(g59)
    c: Block(g58)
    c: Block(g60)
    c: Block(g67)
    c: Block(g43)
    c: Block(g36)
    c: Block(g48)
    c: Block(g46)
    c: Block(g47)
    c: Block(g45)
    c: Block(g35)
    c: Block(g34)
    c: Block(g0)
    c: Block(g33)
    c: Block(g52)
    c: Block(g6)
    c: Block(g41)
    c: Block(g57)
    c: Block(g55)
    c: Block(g53)
    c: Block(g68)
    c: Distance(g48) = 2.76
    c: Distance(g47) = 6.6
    c: Distance(g45) = 2.36657
    c: Coincident(g73,g49)
    c: Vertical(g73)
    c: Distance(g73) = 152
    c: Coincident(g74,g53)
    c: Vertical(g74)
    c: Block(g74)
    c: Coincident(g75,g74)
    c: Horizontal(g75)
    c: Distance(g75) = 7
    c: Horizontal(g76)
    c: Distance(g76) = 7
    c: Coincident(g76,g73)
    c: Vertical(g77)
    c: Distance(g77) = 4
    c: Vertical(g78)
    c: Distance(g78) = 10
    c: Coincident(g79,g78)
    c: Coincident(g80,g77)
    c: Block(g80)
    c: Block(g79)
    c: Coincident(g81,g79)
    c: Coincident(g81,g75)
    c: Vertical(g81)
    c: Coincident(g82,g80)
    c: Coincident(g82,g76)
    c: Vertical(g82)
    c: Coincident(g83,g77)
    c: Coincident(g83,g78)
    c: Horizontal(g83)
    c: Coincident(g84,g6)
    c: Vertical(g84)
    c: Distance(g84) = 13.3
    c: Coincident(g85,g52)
    c: Vertical(g85)
    c: Block(g85)
    c: Coincident(g86,g84)
    c: Horizontal(g86)
    c: Distance(g86) = 4
    c: Coincident(g87,g85)
    c: Horizontal(g87)
    c: Distance(g87) = 4
    c: Coincident(g88,g86)
    c: Vertical(g88)
    c: Coincident(g89,g87)
    c: Vertical(g89)
    c: Distance(g88) = 4
    c: Distance(g89) = 4
    c: Coincident(g90,g88)
    c: Coincident(g90,g89)
    c: Block(g90)
    c: Block(g56)
FEATURE [Sketcher::SketchObject] Sketch005  label="middleTop"
  FullyConstrained = true
  sketch-geometry (133):
    g0: Circle CenterX=175.025 CenterY=27.0667 CenterZ=0 NormalX=0 NormalY=0 NormalZ=1 AngleXU=0 Radius=1
    g1: Circle CenterX=179.022 CenterY=24.8665 CenterZ=0 NormalX=0 NormalY=0 NormalZ=1 AngleXU=0 Radius=1
    g2: Circle CenterX=179.022 CenterY=27.0606 CenterZ=0 NormalX=0 NormalY=0 NormalZ=1 AngleXU=0 Radius=1
    g3: BSplineCurve PolesCount=3 KnotsCount=2 Degree=2 IsPeriodic=0
    g4: GeomPoint X=175.025 Y=27.0667 Z=0
    g5: GeomPoint X=179.022 Y=27.0606 Z=0
    g6: Circle CenterX=189.124 CenterY=27.0628 CenterZ=0 NormalX=0 NormalY=0 NormalZ=1 AngleXU=0 Radius=1
    g7: Circle CenterX=185.124 CenterY=24.8665 CenterZ=0 NormalX=0 NormalY=0 NormalZ=1 AngleXU=0 Radius=1
    g8: Circle CenterX=185.124 CenterY=27.0606 CenterZ=0 NormalX=0 NormalY=0 NormalZ=1 AngleXU=0 Radius=1
    g9: BSplineCurve PolesCount=3 KnotsCount=2 Degree=2 IsPeriodic=0
    g10: GeomPoint X=189.124 Y=27.0628 Z=0
    g11: GeomPoint X=185.124 Y=27.0606 Z=0
    g12: Circle CenterX=165.871 CenterY=18.1458 CenterZ=0 NormalX=0 NormalY=0 NormalZ=1 AngleXU=0 Radius=1
    g13: Circle CenterX=169.377 CenterY=16.2206 CenterZ=0 NormalX=0 NormalY=0 NormalZ=1 AngleXU=0 Radius=1
    g14: Circle CenterX=165.871 CenterY=14.2956 CenterZ=0 NormalX=0 NormalY=0 NormalZ=1 AngleXU=0 Radius=1
    g15: BSplineCurve PolesCount=3 KnotsCount=2 Degree=2 IsPeriodic=0
    g16: GeomPoint X=165.871 Y=18.1458 Z=0
    g17: GeomPoint X=165.871 Y=14.2956 Z=0
    g18: Circle CenterX=198.275 CenterY=18.1318 CenterZ=0 NormalX=0 NormalY=0 NormalZ=1 AngleXU=0 Radius=1
    g19: Circle CenterX=194.768 CenterY=16.2206 CenterZ=0 NormalX=0 NormalY=0 NormalZ=1 AngleXU=0 Radius=1
    g20: Circle CenterX=198.264 CenterY=14.2963 CenterZ=0 NormalX=0 NormalY=0 NormalZ=1 AngleXU=0 Radius=1
    g21: BSplineCurve PolesCount=3 KnotsCount=2 Degree=2 IsPeriodic=0
    g22: GeomPoint X=198.275 Y=18.1318 Z=0
    g23: GeomPoint X=198.264 Y=14.2963 Z=0
    g24: Circle CenterX=125.607 CenterY=54.1951 CenterZ=0 NormalX=0 NormalY=0 NormalZ=1 AngleXU=0 Radius=1
    g25: Circle CenterX=139.632 CenterY=46.4944 CenterZ=0 NormalX=0 NormalY=0 NormalZ=1 AngleXU=0 Radius=1
    g26: Circle CenterX=127.326 CenterY=56.7187 CenterZ=0 NormalX=0 NormalY=0 NormalZ=1 AngleXU=0 Radius=1
    g27: BSplineCurve PolesCount=3 KnotsCount=2 Degree=2 IsPeriodic=0
    g28: GeomPoint X=125.607 Y=54.1951 Z=0
    g29: GeomPoint X=127.326 Y=56.7187 Z=0
    g30: Circle CenterX=236.824 CenterY=56.7187 CenterZ=0 NormalX=0 NormalY=0 NormalZ=1 AngleXU=0 Radius=1
    g31: Circle CenterX=224.513 CenterY=46.4944 CenterZ=0 NormalX=0 NormalY=0 NormalZ=1 AngleXU=0 Radius=1
    g32: Circle CenterX=238.538 CenterY=54.1951 CenterZ=0 NormalX=0 NormalY=0 NormalZ=1 AngleXU=0 Radius=1
    g33: BSplineCurve PolesCount=3 KnotsCount=2 Degree=2 IsPeriodic=0
    g34: GeomPoint X=236.824 Y=56.7187 Z=0
    g35: GeomPoint X=238.538 Y=54.1951 Z=0
    g36: Circle CenterX=189.121 CenterY=124.221 CenterZ=0 NormalX=0 NormalY=0 NormalZ=1 AngleXU=0 Radius=1
    g37: Circle CenterX=185.124 CenterY=124.221 CenterZ=0 NormalX=0 NormalY=0 NormalZ=1 AngleXU=0 Radius=1
    g38: Circle CenterX=185.124 CenterY=120.221 CenterZ=0 NormalX=0 NormalY=0 NormalZ=1 AngleXU=0 Radius=1
    g39: BSplineCurve PolesCount=3 KnotsCount=2 Degree=2 IsPeriodic=0
    g40: GeomPoint X=189.121 Y=124.221 Z=0
    g41: GeomPoint X=185.124 Y=120.221 Z=0
    g42: Circle CenterX=175.022 CenterY=124.221 CenterZ=0 NormalX=0 NormalY=0 NormalZ=1 AngleXU=0 Radius=1
    g43: Circle CenterX=179.022 CenterY=124.221 CenterZ=0 NormalX=0 NormalY=0 NormalZ=1 AngleXU=0 Radius=1
    g44: Circle CenterX=179.022 CenterY=120.221 CenterZ=0 NormalX=0 NormalY=0 NormalZ=1 AngleXU=0 Radius=1
    g45: BSplineCurve PolesCount=3 KnotsCount=2 Degree=2 IsPeriodic=0
    g46: GeomPoint X=175.022 Y=124.221 Z=0
    g47: GeomPoint X=179.022 Y=120.221 Z=0
    g48: LineSegment StartX=232.071 StartY=124.221 StartZ=0 EndX=232.071 EndY=127.221 EndZ=0
    g49-g52: Circle x4 (B-spline internal-alignment scaffolding for g53; pole/knot coordinates omitted)
    g53: BSplineCurve PolesCount=5 KnotsCount=3 Degree=3 IsPeriodic=0
    g54: GeomPoint X=232.072 Y=133.221 Z=0
    g55: GeomPoint X=223.072 Y=130.221 Z=0
    g56: GeomPoint X=232.071 Y=127.221 Z=0
    g57-g61: Circle x5 (B-spline internal-alignment scaffolding for g62; pole/knot coordinates omitted)
    g62: BSplineCurve PolesCount=5 KnotsCount=3 Degree=3 IsPeriodic=0
    g63: GeomPoint X=132.072 Y=133.221 Z=0
    g64: GeomPoint X=141.072 Y=130.221 Z=0
    g65: GeomPoint X=132.072 Y=127.221 Z=0
    g66: ArcOfCircle CenterX=247.391 CenterY=52.0843 CenterZ=0 NormalX=0 NormalY=0 NormalZ=1 AngleXU=0 Radius=4.24264 StartAngle=4.42912 EndAngle=9.14151
    g67: LineSegment StartX=240.687 StartY=51.8263 StartZ=0 EndX=239.192 EndY=54.5542 EndZ=0
    g68: LineSegment StartX=243.575 StartY=46.5669 StartZ=0 EndX=245.072 EndY=43.8408 EndZ=0
    g69: LineSegment StartX=240.168 StartY=69.471 StartZ=0 EndX=241.708 EndY=67.6172 EndZ=0
    g70: LineSegment StartX=246.783 StartY=71.8328 StartZ=0 EndX=248.546 EndY=69.7098 EndZ=0
    g71: LineSegment StartX=245.073 StartY=63.5726 StartZ=0 EndX=243.476 EndY=65.4955 EndZ=0
    g72: LineSegment StartX=123.967 StartY=69.4706 StartZ=0 EndX=122.37 EndY=67.5474 EndZ=0
    g73: LineSegment StartX=232.072 StartY=133.221 StartZ=0 EndX=232.072 EndY=136.221 EndZ=0
    g74: LineSegment StartX=232.072 StartY=136.221 StartZ=0 EndX=132.072 EndY=136.221 EndZ=0
    g75: LineSegment StartX=132.072 StartY=136.221 StartZ=0 EndX=132.072 EndY=133.221 EndZ=0
    g76: LineSegment StartX=132.072 StartY=127.221 StartZ=0 EndX=132.072 EndY=124.221 EndZ=0
    g77: LineSegment StartX=132.072 StartY=124.221 StartZ=0 EndX=175.022 EndY=124.221 EndZ=0
    g78: LineSegment StartX=189.121 StartY=124.221 StartZ=0 EndX=232.071 EndY=124.221 EndZ=0
    g79: LineSegment StartX=185.124 StartY=120.221 StartZ=0 EndX=185.124 EndY=27.0606 EndZ=0
    g80: LineSegment StartX=189.124 StartY=27.0628 StartZ=0 EndX=240.168 EndY=69.471 EndZ=0
    g81: LineSegment StartX=241.708 StartY=67.6172 StartZ=0 EndX=246.783 EndY=71.8328 EndZ=0
    g82: LineSegment StartX=248.546 StartY=69.7098 StartZ=0 EndX=243.476 EndY=65.4955 EndZ=0
    g83: LineSegment StartX=245.073 StartY=63.5726 StartZ=0 EndX=236.824 EndY=56.7187 EndZ=0
    g84: LineSegment StartX=238.538 StartY=54.1951 StartZ=0 EndX=239.192 EndY=54.5542 EndZ=0
    g85: LineSegment StartX=240.687 StartY=51.8263 StartZ=0 EndX=243.317 EndY=53.2701 EndZ=0
    g86: LineSegment StartX=246.205 StartY=48.0108 StartZ=0 EndX=243.575 EndY=46.5669 EndZ=0
    g87: LineSegment StartX=245.072 StartY=43.8408 StartZ=0 EndX=198.275 EndY=18.1318 EndZ=0
    g88: LineSegment StartX=165.871 StartY=18.1458 StartZ=0 EndX=118.934 EndY=43.9178 EndZ=0
    g89: LineSegment StartX=118.934 StartY=43.9178 StartZ=0 EndX=120.377 EndY=46.5474 EndZ=0
    g90: LineSegment StartX=117.748 StartY=47.9913 StartZ=0 EndX=120.377 EndY=46.5474 EndZ=0
    g91: LineSegment StartX=120.635 StartY=53.2507 StartZ=0 EndX=123.265 EndY=51.8068 EndZ=0
    g92: LineSegment StartX=123.265 StartY=51.8068 StartZ=0 EndX=124.73 EndY=54.6766 EndZ=0
    g93: ArcOfCircle CenterX=116.562 CenterY=52.0649 CenterZ=0 NormalX=0 NormalY=0 NormalZ=1 AngleXU=0 Radius=4.24264 StartAngle=0.283267 EndAngle=4.99566
    g94: LineSegment StartX=124.73 StartY=54.6766 StartZ=0 EndX=125.607 EndY=54.1951 EndZ=0
    g95: LineSegment StartX=127.326 StartY=56.7187 StartZ=0 EndX=119.072 EndY=63.5741 EndZ=0
    g96: LineSegment StartX=119.072 StartY=63.5741 StartZ=0 EndX=120.669 EndY=65.4973 EndZ=0
    g97: LineSegment StartX=120.669 StartY=65.4973 StartZ=0 EndX=115.591 EndY=69.7147 EndZ=0
    g98: LineSegment StartX=115.591 StartY=69.7147 StartZ=0 EndX=117.293 EndY=71.7641 EndZ=0
    g99: LineSegment StartX=117.293 StartY=71.7641 StartZ=0 EndX=122.37 EndY=67.5474 EndZ=0
    g100: LineSegment StartX=123.967 StartY=69.4706 StartZ=0 EndX=175.025 EndY=27.0667 EndZ=0
    g101: LineSegment StartX=179.022 StartY=27.0606 StartZ=0 EndX=179.022 EndY=120.221 EndZ=0
    g102-g117: Circle x16 (B-spline internal-alignment scaffolding for g118; pole/knot coordinates omitted)
    g118: BSplineCurve PolesCount=16 KnotsCount=14 Degree=3 IsPeriodic=0
    g119-g132: GeomPoint x14 (B-spline internal-alignment scaffolding for g118; pole/knot coordinates omitted)
  constraints (180):
    c: Weight(g0) = 1
    c: Equal(g0,g1)
    c: Equal(g0,g2)
    c: InternalAlignment(g0,g3)
    c: InternalAlignment(g1,g3)
    c: InternalAlignment(g2,g3)
    c: InternalAlignment(g4,g3)
    c: InternalAlignment(g5,g3)
    c: Weight(g6) = 1
    c: Equal(g6,g7)
    c: Equal(g6,g8)
    c: InternalAlignment(g6,g9)
    c: InternalAlignment(g7,g9)
    c: InternalAlignment(g8,g9)
    c: InternalAlignment(g10,g9)
    c: InternalAlignment(g11,g9)
    c: Block(g9)
    c: Block(g3)
    c: Weight(g12) = 1
    c: Equal(g12,g13)
    c: Equal(g12,g14)
    c: InternalAlignment(g12,g15)
    c: InternalAlignment(g13,g15)
    c: InternalAlignment(g14,g15)
    c: InternalAlignment(g16,g15)
    c: InternalAlignment(g17,g15)
    c: Weight(g18) = 1
    c: Equal(g18,g19)
    c: Equal(g18,g20)
    c: InternalAlignment(g18,g21)
    c: InternalAlignment(g19,g21)
    c: InternalAlignment(g20,g21)
    c: InternalAlignment(g22,g21)
    c: InternalAlignment(g23,g21)
    c: Block(g15)
    c: Block(g21)
    c: Weight(g24) = 1
    c: Equal(g24,g25)
    c: Equal(g24,g26)
    c: InternalAlignment(g24,g27)
    c: InternalAlignment(g25,g27)
    c: InternalAlignment(g26,g27)
    c: InternalAlignment(g28,g27)
    c: InternalAlignment(g29,g27)
    c: Block(g27)
    c: Weight(g30) = 1
    c: Equal(g30,g31)
    c: Equal(g30,g32)
    c: InternalAlignment(g30,g33)
    c: InternalAlignment(g31,g33)
    c: InternalAlignment(g32,g33)
    c: InternalAlignment(g34,g33)
    c: InternalAlignment(g35,g33)
    c: Block(g33)
    c: Weight(g36) = 1
    c: Equal(g36,g37)
    c: Equal(g36,g38)
    c: InternalAlignment(g36,g39)
    c: InternalAlignment(g37,g39)
    c: InternalAlignment(g38,g39)
    c: InternalAlignment(g40,g39)
    c: InternalAlignment(g41,g39)
    c: Weight(g42) = 1
    c: Equal(g42,g43)
    c: Equal(g42,g44)
    c: InternalAlignment(g42,g45)
    c: InternalAlignment(g43,g45)
    c: InternalAlignment(g44,g45)
    c: InternalAlignment(g46,g45)
    c: InternalAlignment(g47,g45)
    c: Block(g45)
    c: Block(g39)
    c: Vertical(g48)
    c: Distance(g48) = 3
    c: Weight(g49) = 1
    c: Equal(g49,g50)
    c: Equal(g49,g51)
    c: Equal(g49,g52)
    c: Coincident(g53,g48)
    c: InternalAlignment(g49-g52 -> g53) x4
    c: InternalAlignment(g54,g53)
    c: InternalAlignment(g55,g53)
    c: InternalAlignment(g56,g53)
    c: Weight(g57) = 1
    c: Equal(g57, g58-g61) x4
    c: InternalAlignment(g57-g61 -> g62) x5
    c: InternalAlignment(g63,g62)
    c: InternalAlignment(g64,g62)
    c: InternalAlignment(g65,g62)
    c: Block(g62)
    c: Block(g67)
    c: Block(g68)
    c: Distance(g69) = 2.41
    c: Distance(g70) = 2.76
    c: Distance(g71) = 2.5
    c: Distance(g72) = 2.5
    c: Block(g66)
    c: Block(g48)
    c: Block(g53)
    c: Coincident(g73,g53)
    c: Vertical(g73)
    c: Distance(g73) = 3
    c: Coincident(g74,g73)
    c: Horizontal(g74)
    c: Distance(g74) = 100
    c: Coincident(g75,g74)
    c: Coincident(g75,g62)
    c: Vertical(g75)
    c: Distance(g75) = 3
    c: Coincident(g76,g62)
    c: Vertical(g76)
    c: Distance(g76) = 3
    c: Coincident(g77,g76)
    c: Coincident(g77,g45)
    c: Horizontal(g77)
    c: Distance(g77) = 42.95
    c: Coincident(g78,g39)
    c: Coincident(g78,g48)
    c: Horizontal(g78)
    c: Distance(g78) = 42.95
    c: Coincident(g79,g39)
    c: Coincident(g79,g9)
    c: Vertical(g79)
    c: Distance(g79) = 93.16
    c: Coincident(g80,g9)
    c: Coincident(g80,g69)
    c: Angle(g80) = 0.693245
    c: Block(g80)
    c: Coincident(g81,g69)
    c: Coincident(g81,g70)
    c: Block(g81)
    c: Coincident(g82,g70)
    c: Coincident(g82,g71)
    c: Block(g82)
    c: Coincident(g83,g71)
    c: Coincident(g83,g33)
    c: Block(g71)
    c: Coincident(g84,g33)
    c: Coincident(g84,g67)
    c: Coincident(g85,g67)
    c: Coincident(g85,g66)
    c: Coincident(g86,g66)
    c: Coincident(g86,g68)
    c: Coincident(g87,g68)
    c: Coincident(g87,g21)
    c: Coincident(g88,g15)
    c: Coincident(g89,g88)
    c: Block(g89)
    c: Coincident(g90,g89)
    c: Block(g90)
    c: Block(g91)
    c: Coincident(g92,g91)
    c: Block(g92)
    c: Coincident(g93,g91)
    c: Coincident(g93,g90)
    c: Block(g93)
    c: Coincident(g94,g92)
    c: Coincident(g94,g27)
    c: Coincident(g95,g27)
    c: Block(g95)
    c: Coincident(g96,g95)
    c: Coincident(g97,g96)
    c: Coincident(g98,g97)
    c: Coincident(g99,g98)
    c: Coincident(g99,g72)
    c: Block(g98)
    c: Block(g96)
    c: Block(g72)
    c: Coincident(g100,g72)
    c: Coincident(g100,g3)
    c: Coincident(g101,g3)
    c: Coincident(g101,g45)
    c: Vertical(g101)
    c: Coincident(g118,g21)
    c: Weight(g102) = 1
    c: Equal(g102, g103-g117) x15
    c: Coincident(g118,g15)
    c: InternalAlignment(g102-g117 -> g118) x16
    c: InternalAlignment(g119-g132 -> g118) x14
    c: Block(g118)
FEATURE [Sketcher::SketchObject] Sketch006  label="leftSideTop"
  FullyConstrained = true
  sketch-geometry (89):
    g0: Circle CenterX=61.1495 CenterY=111.695 CenterZ=0 NormalX=0 NormalY=0 NormalZ=1 AngleXU=0 Radius=1
    g1: Circle CenterX=58.0728 CenterY=114.251 CenterZ=0 NormalX=0 NormalY=0 NormalZ=1 AngleXU=0 Radius=1
    g2: Circle CenterX=58.0728 CenterY=110.251 CenterZ=0 NormalX=0 NormalY=0 NormalZ=1 AngleXU=0 Radius=1
    g3: BSplineCurve PolesCount=3 KnotsCount=2 Degree=2 IsPeriodic=0
    g4: GeomPoint X=61.1495 Y=111.695 Z=0
    g5: GeomPoint X=58.0728 Y=110.251 Z=0
    g6: Circle CenterX=61.5791 CenterY=89.3511 CenterZ=0 NormalX=0 NormalY=0 NormalZ=1 AngleXU=0 Radius=1
    g7: Circle CenterX=58.0728 CenterY=91.2763 CenterZ=0 NormalX=0 NormalY=0 NormalZ=1 AngleXU=0 Radius=1
    g8: Circle CenterX=58.0728 CenterY=95.2763 CenterZ=0 NormalX=0 NormalY=0 NormalZ=1 AngleXU=0 Radius=1
    g9: BSplineCurve PolesCount=3 KnotsCount=2 Degree=2 IsPeriodic=0
    g10: GeomPoint X=61.5791 Y=89.3511 Z=0
    g11: GeomPoint X=58.0728 Y=95.2763 Z=0
    g12: Circle CenterX=62.0728 CenterY=124.221 CenterZ=0 NormalX=0 NormalY=0 NormalZ=1 AngleXU=0 Radius=1
    g13: Circle CenterX=58.0728 CenterY=124.221 CenterZ=0 NormalX=0 NormalY=0 NormalZ=1 AngleXU=0 Radius=1
    g14: Circle CenterX=61.1496 CenterY=121.665 CenterZ=0 NormalX=0 NormalY=0 NormalZ=1 AngleXU=0 Radius=1
    g15: BSplineCurve PolesCount=3 KnotsCount=2 Degree=2 IsPeriodic=0
    g16: GeomPoint X=62.0728 Y=124.221 Z=0
    g17: GeomPoint X=61.1496 Y=121.665 Z=0
    g18: Circle CenterX=61.5791 CenterY=75.4095 CenterZ=0 NormalX=0 NormalY=0 NormalZ=1 AngleXU=0 Radius=1
    g19: Circle CenterX=58.0728 CenterY=77.3346 CenterZ=0 NormalX=0 NormalY=0 NormalZ=1 AngleXU=0 Radius=1
    g20: Circle CenterX=58.0728 CenterY=73.3346 CenterZ=0 NormalX=0 NormalY=0 NormalZ=1 AngleXU=0 Radius=1
    g21: BSplineCurve PolesCount=3 KnotsCount=2 Degree=2 IsPeriodic=0
    g22: GeomPoint X=61.5791 Y=75.4095 Z=0
    g23: GeomPoint X=58.0728 Y=73.3346 Z=0
    g24: Circle CenterX=2.07281 CenterY=124.221 CenterZ=0 NormalX=0 NormalY=0 NormalZ=1 AngleXU=0 Radius=1
    g25: Circle CenterX=1.57905 CenterY=122.295 CenterZ=0 NormalX=0 NormalY=0 NormalZ=1 AngleXU=0 Radius=1
    g26: BSplineCurve PolesCount=3 KnotsCount=2 Degree=2 IsPeriodic=0
    g27: GeomPoint X=2.07281 Y=124.221 Z=0
    g28: GeomPoint X=1.57905 Y=122.295 Z=0
    g29: Circle CenterX=46.0728 CenterY=124.221 CenterZ=0 NormalX=0 NormalY=0 NormalZ=1 AngleXU=0 Radius=1
    g30: Circle CenterX=46.0728 CenterY=120.221 CenterZ=0 NormalX=0 NormalY=0 NormalZ=1 AngleXU=0 Radius=1
    g31: BSplineCurve PolesCount=3 KnotsCount=2 Degree=2 IsPeriodic=0
    g32: GeomPoint X=42.0728 Y=124.221 Z=0
    g33: GeomPoint X=46.0728 Y=120.221 Z=0
    g34-g38: Circle x5 (B-spline internal-alignment scaffolding for g39; pole/knot coordinates omitted)
    g39: BSplineCurve PolesCount=5 KnotsCount=3 Degree=3 IsPeriodic=0
    g40: GeomPoint X=132.072 Y=133.221 Z=0
    g41: GeomPoint X=141.072 Y=130.221 Z=0
    g42: GeomPoint X=132.072 Y=127.221 Z=0
    g43: ArcOfCircle CenterX=116.562 CenterY=52.0649 CenterZ=0 NormalX=0 NormalY=0 NormalZ=1 AngleXU=0 Radius=4.24264 StartAngle=0.283268 EndAngle=4.99566
    g44: LineSegment StartX=123.967 StartY=69.4706 StartZ=0 EndX=122.37 EndY=67.5474 EndZ=0
    g45: LineSegment StartX=117.293 StartY=71.7641 StartZ=0 EndX=115.591 EndY=69.7147 EndZ=0
    g46: LineSegment StartX=120.669 StartY=65.4973 StartZ=0 EndX=119.072 EndY=63.5741 EndZ=0
    g47: LineSegment StartX=124.73 StartY=54.6766 StartZ=0 EndX=123.265 EndY=51.8068 EndZ=0
    g48: LineSegment StartX=120.377 StartY=46.5474 StartZ=0 EndX=118.934 EndY=43.9178 EndZ=0
    g49: LineSegment StartX=61.5791 StartY=75.4095 StartZ=0 EndX=118.934 EndY=43.9178 EndZ=0
    g50: LineSegment StartX=117.748 StartY=47.9913 StartZ=0 EndX=120.377 EndY=46.5474 EndZ=0
    g51: LineSegment StartX=120.635 StartY=53.2507 StartZ=0 EndX=123.265 EndY=51.8068 EndZ=0
    g52: LineSegment StartX=124.73 StartY=54.6766 StartZ=0 EndX=61.5791 EndY=89.3511 EndZ=0
    g53: LineSegment StartX=58.0728 StartY=95.2763 StartZ=0 EndX=58.0728 EndY=110.251 EndZ=0
    g54: LineSegment StartX=61.1495 StartY=111.695 StartZ=0 EndX=119.072 EndY=63.5741 EndZ=0
    g55: LineSegment StartX=120.669 StartY=65.4973 StartZ=0 EndX=115.591 EndY=69.7147 EndZ=0
    g56: LineSegment StartX=117.293 StartY=71.7641 StartZ=0 EndX=122.37 EndY=67.5474 EndZ=0
    g57: LineSegment StartX=123.967 StartY=69.4706 StartZ=0 EndX=61.1496 EndY=121.665 EndZ=0
    g58: LineSegment StartX=62.0728 StartY=124.221 StartZ=0 EndX=132.072 EndY=124.221 EndZ=0
    g59: LineSegment StartX=132.072 StartY=127.221 StartZ=0 EndX=132.072 EndY=124.221 EndZ=0
    g60: LineSegment StartX=132.072 StartY=133.221 StartZ=0 EndX=132.072 EndY=136.221 EndZ=0
    g61: LineSegment StartX=132.072 StartY=136.221 StartZ=0 EndX=-42.9272 EndY=136.221 EndZ=0
    g62: LineSegment StartX=2.07281 StartY=124.221 StartZ=0 EndX=42.0728 EndY=124.221 EndZ=0
    g63: LineSegment StartX=-17.9272 StartY=48.2206 StartZ=0 EndX=-17.9272 EndY=58.2206 EndZ=0
    g64: LineSegment StartX=-35.9272 StartY=48.2206 StartZ=0 EndX=-35.9272 EndY=52.2206 EndZ=0
    g65: LineSegment StartX=-29.9272 StartY=48.2206 StartZ=0 EndX=-29.9272 EndY=52.2206 EndZ=0
    g66: LineSegment StartX=-23.9272 StartY=48.2206 StartZ=0 EndX=-23.9272 EndY=58.2206 EndZ=0
    g67: ArcOfCircle CenterX=-32.9272 CenterY=55.2206 CenterZ=0 NormalX=0 NormalY=0 NormalZ=1 AngleXU=0 Radius=4.24264 StartAngle=5.49779 EndAngle=10.2102
    g68: ArcOfCircle CenterX=-20.9272 CenterY=61.2206 CenterZ=0 NormalX=0 NormalY=0 NormalZ=1 AngleXU=0 Radius=4.24264 StartAngle=5.49779 EndAngle=10.2102
    g69: LineSegment StartX=-42.9272 StartY=48.2206 StartZ=0 EndX=-42.9272 EndY=136.221 EndZ=0
    g70: LineSegment StartX=58.0728 StartY=-27.5905 StartZ=0 EndX=58.0728 EndY=73.3346 EndZ=0
    g71: LineSegment StartX=50.0728 StartY=-27.5905 StartZ=0 EndX=50.0728 EndY=-31.5905 EndZ=0
    g72: LineSegment StartX=54.0728 StartY=-27.5905 StartZ=0 EndX=54.0728 EndY=-31.5905 EndZ=0
    g73: ArcOfCircle CenterX=52.0728 CenterY=-33.5905 CenterZ=0 NormalX=0 NormalY=0 NormalZ=1 AngleXU=0 Radius=2.82843 StartAngle=2.35619 EndAngle=7.06858
    g74: LineSegment StartX=54.0728 StartY=-27.5905 StartZ=0 EndX=58.0728 EndY=-27.5905 EndZ=0
    g75: LineSegment StartX=-17.9272 StartY=48.2206 StartZ=0 EndX=-10.9272 EndY=48.2206 EndZ=0
    g76: LineSegment StartX=-29.9272 StartY=48.2206 StartZ=0 EndX=-23.9272 EndY=48.2206 EndZ=0
    g77: LineSegment StartX=-42.9272 StartY=48.2206 StartZ=0 EndX=-35.9272 EndY=48.2206 EndZ=0
    g78: BSplineCurve PolesCount=3 KnotsCount=2 Degree=2 IsPeriodic=0
    g79: LineSegment StartX=46.0728 StartY=-27.5905 StartZ=0 EndX=46.0728 EndY=64.4095 EndZ=0
    g80: BSplineCurve PolesCount=3 KnotsCount=2 Degree=2 IsPeriodic=0
    g81: LineSegment StartX=-6.92718 StartY=68.4095 StartZ=0 EndX=42.0728 EndY=68.4095 EndZ=0
    g82: LineSegment StartX=-10.9272 StartY=64.4095 StartZ=0 EndX=-10.9272 EndY=48.2206 EndZ=0
    g83: LineSegment StartX=46.0728 StartY=-27.5905 StartZ=0 EndX=50.0728 EndY=-27.5905 EndZ=0
    g84: LineSegment StartX=46.0728 StartY=120.221 StartZ=0 EndX=46.0728 EndY=113.861 EndZ=0
    g85: BSplineCurve PolesCount=3 KnotsCount=2 Degree=2 IsPeriodic=0
    g86: LineSegment StartX=42.0728 StartY=109.861 StartZ=0 EndX=35.5028 EndY=109.861 EndZ=0
    g87: BSplineCurve PolesCount=3 KnotsCount=2 Degree=2 IsPeriodic=0
    g88: LineSegment StartX=1.57905 StartY=122.295 StartZ=0 EndX=27.9965 EndY=111.786 EndZ=0
  constraints (158):
    c: Weight(g0) = 1
    c: Equal(g0,g1)
    c: Equal(g0,g2)
    c: InternalAlignment(g0,g3)
    c: InternalAlignment(g1,g3)
    c: InternalAlignment(g2,g3)
    c: InternalAlignment(g4,g3)
    c: InternalAlignment(g5,g3)
    c: Weight(g6) = 1
    c: Equal(g6,g7)
    c: Equal(g6,g8)
    c: InternalAlignment(g6,g9)
    c: InternalAlignment(g7,g9)
    c: InternalAlignment(g8,g9)
    c: InternalAlignment(g10,g9)
    c: InternalAlignment(g11,g9)
    c: Block(g3)
    c: Block(g9)
    c: Weight(g12) = 1
    c: Equal(g12,g13)
    c: Equal(g12,g14)
    c: InternalAlignment(g12,g15)
    c: InternalAlignment(g13,g15)
    c: InternalAlignment(g14,g15)
    c: InternalAlignment(g16,g15)
    c: InternalAlignment(g17,g15)
    c: Block(g15)
    c: Weight(g18) = 1
    c: Equal(g18,g19)
    c: Equal(g18,g20)
    c: InternalAlignment(g18,g21)
    c: InternalAlignment(g19,g21)
    c: InternalAlignment(g20,g21)
    c: InternalAlignment(g22,g21)
    c: InternalAlignment(g23,g21)
    c: Block(g21)
    c: Weight(g24) = 1
    c: Equal(g24,g25)
    c: InternalAlignment(g24,g26)
    c: InternalAlignment(g25,g26)
    c: InternalAlignment(g27,g26)
    c: InternalAlignment(g28,g26)
    c: InternalAlignment(g29,g31)
    c: InternalAlignment(g30,g31)
    c: InternalAlignment(g32,g31)
    c: InternalAlignment(g33,g31)
    c: Block(g31)
    c: Block(g26)
    c: Weight(g34) = 1
    c: Equal(g34, g35-g38) x4
    c: InternalAlignment(g34-g38 -> g39) x5
    c: InternalAlignment(g40,g39)
    c: InternalAlignment(g41,g39)
    c: InternalAlignment(g42,g39)
    c: Block(g39)
    c: Block(g43)
    c: Block(g44)
    c: Block(g45)
    c: Block(g46)
    c: Block(g47)
    c: Block(g48)
    c: Coincident(g70,g21)
    c: Coincident(g49,g21)
    c: Coincident(g49,g48)
    c: Coincident(g50,g43)
    c: Coincident(g50,g48)
    c: Coincident(g51,g43)
    c: Coincident(g51,g47)
    c: Coincident(g52,g47)
    c: Coincident(g52,g9)
    c: Coincident(g53,g9)
    c: Coincident(g53,g3)
    c: Vertical(g53)
    c: Coincident(g54,g3)
    c: Coincident(g54,g46)
    c: Coincident(g55,g46)
    c: Coincident(g55,g45)
    c: Coincident(g56,g45)
    c: Coincident(g56,g44)
    c: Coincident(g57,g44)
    c: Coincident(g57,g15)
    c: Coincident(g58,g15)
    c: Horizontal(g58)
    c: Coincident(g59,g39)
    c: Coincident(g59,g58)
    c: Vertical(g59)
    c: Coincident(g60,g39)
    c: Vertical(g60)
    c: Coincident(g61,g60)
    c: Horizontal(g61)
    c: Coincident(g62,g26)
    c: Coincident(g62,g31)
    c: Horizontal(g62)
    c: Vertical(g63)
    c: Distance(g63) = 10
    c: Vertical(g64)
    c: Distance(g64) = 4
    c: Vertical(g65)
    c: Distance(g65) = 4
    c: Vertical(g66)
    c: Distance(g66) = 10
    c: Coincident(g67,g65)
    c: Coincident(g67,g64)
    c: Block(g67)
    c: Coincident(g68,g66)
    c: Coincident(g68,g63)
    c: Block(g68)
    c: Coincident(g69,g61)
    c: Vertical(g69)
    c: Block(g61)
    c: Block(g70)
    c: Vertical(g71)
    c: Distance(g71) = 4
    c: Vertical(g72)
    c: Distance(g72) = 4
    c: Coincident(g73,g71)
    c: Coincident(g73,g72)
    c: Block(g73)
    c: Coincident(g74,g72)
    c: Coincident(g74,g70)
    c: Horizontal(g74)
    c: Distance(g74) = 4
    c: Block(g69)
    c: Coincident(g75,g63)
    c: Horizontal(g75)
    c: Coincident(g76,g65)
    c: Coincident(g76,g66)
    c: Horizontal(g76)
    c: Coincident(g77,g69)
    c: Coincident(g77,g64)
    c: Horizontal(g77)
    c: Block(g78)
    c: Vertical(g79)
    c: Distance(g79) = 92
    c: Block(g80)
    c: Coincident(g80,g79)
    c: Coincident(g81,g78)
    c: Coincident(g81,g80)
    c: Horizontal(g81)
    c: Coincident(g82,g78)
    c: Coincident(g82,g75)
    c: Vertical(g82)
    c: Coincident(g83,g79)
    c: Coincident(g83,g71)
    c: Horizontal(g83)
    c: Coincident(g84,g31)
    c: Vertical(g84)
    c: Distance(g84) = 6.36
    c: Block(g85)
    c: Coincident(g85,g84)
    c: Horizontal(g86)
    c: Coincident(g86,g85)
    c: Block(g87)
    c: Coincident(g87,g86)
    c: Coincident(g88,g26)
    c: Coincident(g88,g87)
    c: Distance(g61) = 174.999
    c: Distance(g61) = 174.999
FEATURE [Sketcher::SketchObject] Sketch007  label="leftSideBottom"
  FullyConstrained = true
  sketch-geometry (92):
    g0: ArcOfCircle CenterX=-26.9272 CenterY=-83.7794 CenterZ=0 NormalX=0 NormalY=0 NormalZ=1 AngleXU=0 Radius=8 StartAngle=3.14159 EndAngle=6.28319
    g1: Circle CenterX=61.5791 CenterY=-56.9099 CenterZ=0 NormalX=0 NormalY=0 NormalZ=1 AngleXU=0 Radius=1
    g2: Circle CenterX=58.0728 CenterY=-58.8351 CenterZ=0 NormalX=0 NormalY=0 NormalZ=1 AngleXU=0 Radius=1
    g3: Circle CenterX=58.0728 CenterY=-62.8351 CenterZ=0 NormalX=0 NormalY=0 NormalZ=1 AngleXU=0 Radius=1
    g4: BSplineCurve PolesCount=3 KnotsCount=2 Degree=2 IsPeriodic=0
    g5: GeomPoint X=61.5791 Y=-56.9099 Z=0
    g6: GeomPoint X=58.0728 Y=-62.8351 Z=0
    g7: Circle CenterX=58.0728 CenterY=-77.8102 CenterZ=0 NormalX=0 NormalY=0 NormalZ=1 AngleXU=0 Radius=1
    g8: Circle CenterX=58.0728 CenterY=-81.8102 CenterZ=0 NormalX=0 NormalY=0 NormalZ=1 AngleXU=0 Radius=1
    g9: Circle CenterX=61.1496 CenterY=-79.2541 CenterZ=0 NormalX=0 NormalY=0 NormalZ=1 AngleXU=0 Radius=1
    g10: BSplineCurve PolesCount=3 KnotsCount=2 Degree=2 IsPeriodic=0
    g11: GeomPoint X=58.0728 Y=-77.8102 Z=0
    g12: GeomPoint X=61.1496 Y=-79.2541 Z=0
    g13: Circle CenterX=61.6457 CenterY=-88.8112 CenterZ=0 NormalX=0 NormalY=0 NormalZ=1 AngleXU=0 Radius=1
    g14: Circle CenterX=58.0728 CenterY=-91.7794 CenterZ=0 NormalX=0 NormalY=0 NormalZ=1 AngleXU=0 Radius=1
    g15: Circle CenterX=63.9135 CenterY=-91.8014 CenterZ=0 NormalX=0 NormalY=0 NormalZ=1 AngleXU=0 Radius=1
    g16: BSplineCurve PolesCount=3 KnotsCount=2 Degree=2 IsPeriodic=0
    g17: GeomPoint X=61.6457 Y=-88.8112 Z=0
    g18: GeomPoint X=63.9135 Y=-91.8014 Z=0
    g19: Circle CenterX=58.0728 CenterY=-40.8935 CenterZ=0 NormalX=0 NormalY=0 NormalZ=1 AngleXU=0 Radius=1
    g20: Circle CenterX=58.0728 CenterY=-44.8935 CenterZ=0 NormalX=0 NormalY=0 NormalZ=1 AngleXU=0 Radius=1
    g21: Circle CenterX=61.5791 CenterY=-42.9683 CenterZ=0 NormalX=0 NormalY=0 NormalZ=1 AngleXU=0 Radius=1
    g22: BSplineCurve PolesCount=3 KnotsCount=2 Degree=2 IsPeriodic=0
    g23: GeomPoint X=58.0728 Y=-40.8935 Z=0
    g24: GeomPoint X=61.5791 Y=-42.9683 Z=0
    g25: Circle CenterX=42.5666 CenterY=-67.3492 CenterZ=0 NormalX=0 NormalY=0 NormalZ=1 AngleXU=0 Radius=1
    g26: Circle CenterX=46.0728 CenterY=-65.424 CenterZ=0 NormalX=0 NormalY=0 NormalZ=1 AngleXU=0 Radius=1
    g27: Circle CenterX=46.0728 CenterY=-69.424 CenterZ=0 NormalX=0 NormalY=0 NormalZ=1 AngleXU=0 Radius=1
    g28: BSplineCurve PolesCount=3 KnotsCount=2 Degree=2 IsPeriodic=0
    g29: GeomPoint X=42.5666 Y=-67.3492 Z=0
    g30: GeomPoint X=46.0728 Y=-69.424 Z=0
    g31: Circle CenterX=2.07281 CenterY=-91.7794 CenterZ=0 NormalX=0 NormalY=0 NormalZ=1 AngleXU=0 Radius=1
    g32: Circle CenterX=-1.92719 CenterY=-91.7794 CenterZ=0 NormalX=0 NormalY=0 NormalZ=1 AngleXU=0 Radius=1
    g33: Circle CenterX=1.57905 CenterY=-89.8542 CenterZ=0 NormalX=0 NormalY=0 NormalZ=1 AngleXU=0 Radius=1
    g34: BSplineCurve PolesCount=3 KnotsCount=2 Degree=2 IsPeriodic=0
    g35: GeomPoint X=2.07281 Y=-91.7794 Z=0
    g36: GeomPoint X=1.57905 Y=-89.8542 Z=0
    g37: ArcOfCircle CenterX=-26.9272 CenterY=22.1087 CenterZ=0 NormalX=0 NormalY=0 NormalZ=1 AngleXU=0 Radius=4 StartAngle=5e-16 EndAngle=3.14159
    g38: Circle CenterX=-10.9272 CenterY=-78.7794 CenterZ=0 NormalX=0 NormalY=0 NormalZ=1 AngleXU=0 Radius=1
    g39: Circle CenterX=-10.9272 CenterY=-82.7794 CenterZ=0 NormalX=0 NormalY=0 NormalZ=1 AngleXU=0 Radius=1
    g40: Circle CenterX=-7.42095 CenterY=-80.8542 CenterZ=0 NormalX=0 NormalY=0 NormalZ=1 AngleXU=0 Radius=1
    g41: BSplineCurve PolesCount=3 KnotsCount=2 Degree=2 IsPeriodic=0
    g42: GeomPoint X=-10.9272 Y=-78.7794 Z=0
    g43: GeomPoint X=-7.42095 Y=-80.8542 Z=0
    g44: BSplineCurve PolesCount=3 KnotsCount=2 Degree=2 IsPeriodic=0
    g45: GeomPoint X=42.5666 Y=-53.4075 Z=0
    g46: GeomPoint X=46.0728 Y=-47.4823 Z=0
    g47: BSplineCurve PolesCount=5 KnotsCount=3 Degree=3 IsPeriodic=0
    g48: LineSegment StartX=124.814 StartY=-22.1885 StartZ=0 EndX=123.265 EndY=-19.3655 EndZ=0
    g49: ArcOfCircle CenterX=116.562 CenterY=-19.6236 CenterZ=0 NormalX=0 NormalY=0 NormalZ=1 AngleXU=0 Radius=4.24264 StartAngle=1.28753 EndAngle=6.00037
    g50: LineSegment StartX=-30.9272 StartY=22.1087 StartZ=0 EndX=-34.9272 EndY=-83.7794 EndZ=0
    g51: LineSegment StartX=-22.9272 StartY=22.1087 StartZ=0 EndX=-18.9272 EndY=-83.7794 EndZ=0
    g52: LineSegment StartX=118.934 StartY=-11.4765 StartZ=0 EndX=120.377 EndY=-14.1062 EndZ=0
    g53: LineSegment StartX=118.86 StartY=-31.3104 StartZ=0 EndX=120.377 EndY=-33.1447 EndZ=0
    g54: LineSegment StartX=115.291 StartY=-37.3514 StartZ=0 EndX=117.05 EndY=-39.4781 EndZ=0
    g55: LineSegment StartX=122.136 StartY=-35.2714 StartZ=0 EndX=123.656 EndY=-37.1092 EndZ=0
    g56: BSplineCurve PolesCount=3 KnotsCount=2 Degree=2 IsPeriodic=0
    g57: LineSegment StartX=132.072 StartY=-100.779 StartZ=0 EndX=132.072 EndY=-103.779 EndZ=0
    g58: LineSegment StartX=132.072 StartY=-91.8014 StartZ=0 EndX=132.072 EndY=-94.7791 EndZ=0
    g59: LineSegment StartX=63.9135 StartY=-91.8014 StartZ=0 EndX=132.072 EndY=-91.8014 EndZ=0
    g60: LineSegment StartX=61.6457 StartY=-88.8112 StartZ=0 EndX=123.656 EndY=-37.1092 EndZ=0
    g61: LineSegment StartX=122.136 StartY=-35.2714 StartZ=0 EndX=117.05 EndY=-39.4781 EndZ=0
    g62: LineSegment StartX=115.291 StartY=-37.3514 StartZ=0 EndX=120.377 EndY=-33.1447 EndZ=0
    g63: LineSegment StartX=118.86 StartY=-31.3104 StartZ=0 EndX=61.1496 EndY=-79.2541 EndZ=0
    g64: LineSegment StartX=58.0728 StartY=-77.8102 StartZ=0 EndX=58.0728 EndY=-62.8351 EndZ=0
    g65: LineSegment StartX=61.5791 StartY=-56.9099 StartZ=0 EndX=124.814 EndY=-22.1885 EndZ=0
    g66: LineSegment StartX=120.636 StartY=-20.8076 StartZ=0 EndX=123.265 EndY=-19.3655 EndZ=0
    g67: LineSegment StartX=117.748 StartY=-15.55 StartZ=0 EndX=120.377 EndY=-14.1062 EndZ=0
    g68: LineSegment StartX=118.934 StartY=-11.4765 StartZ=0 EndX=61.5791 EndY=-42.9683 EndZ=0
    g69: LineSegment StartX=-42.9272 StartY=-103.779 StartZ=0 EndX=132.072 EndY=-103.779 EndZ=0
    g70: LineSegment StartX=42.5666 StartY=-53.4075 StartZ=0 EndX=-7.42095 EndY=-80.8542 EndZ=0
    g71: LineSegment StartX=-10.9272 StartY=-78.7794 StartZ=0 EndX=-10.9272 EndY=48.2206 EndZ=0
    g72: LineSegment StartX=2.07281 StartY=-91.7794 StartZ=0 EndX=42.0728 EndY=-91.7794 EndZ=0
    g73: LineSegment StartX=46.0728 StartY=-87.7794 StartZ=0 EndX=46.0728 EndY=-69.424 EndZ=0
    g74: LineSegment StartX=42.5666 StartY=-67.3492 StartZ=0 EndX=1.57905 EndY=-89.8542 EndZ=0
    g75: LineSegment StartX=-42.9272 StartY=-103.779 StartZ=0 EndX=-42.9272 EndY=48.2206 EndZ=0
    g76: LineSegment StartX=-17.9272 StartY=48.2206 StartZ=0 EndX=-17.9272 EndY=58.2206 EndZ=0
    g77: LineSegment StartX=-35.9272 StartY=48.2206 StartZ=0 EndX=-35.9272 EndY=52.2206 EndZ=0
    g78: LineSegment StartX=-29.9272 StartY=48.2206 StartZ=0 EndX=-29.9272 EndY=52.2206 EndZ=0
    g79: LineSegment StartX=-23.9272 StartY=48.2206 StartZ=0 EndX=-23.9272 EndY=58.2206 EndZ=0
    g80: ArcOfCircle CenterX=-32.9272 CenterY=55.2206 CenterZ=0 NormalX=0 NormalY=0 NormalZ=1 AngleXU=0 Radius=4.24264 StartAngle=5.49779 EndAngle=10.2102
    g81: ArcOfCircle CenterX=-20.9272 CenterY=61.2206 CenterZ=0 NormalX=0 NormalY=0 NormalZ=1 AngleXU=0 Radius=4.24264 StartAngle=5.49779 EndAngle=10.2102
    g82: LineSegment StartX=-17.9272 StartY=48.2206 StartZ=0 EndX=-10.9272 EndY=48.2206 EndZ=0
    g83: LineSegment StartX=-42.9272 StartY=48.2206 StartZ=0 EndX=-35.9272 EndY=48.2206 EndZ=0
    g84: LineSegment StartX=50.0728 StartY=-27.5905 StartZ=0 EndX=50.0728 EndY=-31.5905 EndZ=0
    g85: LineSegment StartX=54.0728 StartY=-27.5905 StartZ=0 EndX=54.0728 EndY=-31.5905 EndZ=0
    g86: ArcOfCircle CenterX=52.0728 CenterY=-33.5905 CenterZ=0 NormalX=0 NormalY=0 NormalZ=1 AngleXU=0 Radius=2.82843 StartAngle=2.35619 EndAngle=7.06858
    g87: LineSegment StartX=46.0728 StartY=-27.5905 StartZ=0 EndX=50.0728 EndY=-27.5905 EndZ=0
    g88: LineSegment StartX=54.0728 StartY=-27.5905 StartZ=0 EndX=58.0728 EndY=-27.5905 EndZ=0
    g89: LineSegment StartX=46.0728 StartY=-27.5905 StartZ=0 EndX=46.0728 EndY=-47.4823 EndZ=0
    g90: LineSegment StartX=58.0728 StartY=-27.5905 StartZ=0 EndX=58.0728 EndY=-40.8935 EndZ=0
    g91: LineSegment StartX=-29.9272 StartY=48.2206 StartZ=0 EndX=-23.9272 EndY=48.2206 EndZ=0
  constraints (170):
    c: Weight(g1) = 1
    c: Equal(g1,g2)
    c: Equal(g1,g3)
    c: InternalAlignment(g1,g4)
    c: InternalAlignment(g2,g4)
    c: InternalAlignment(g3,g4)
    c: InternalAlignment(g5,g4)
    c: InternalAlignment(g6,g4)
    c: Weight(g7) = 1
    c: Equal(g7,g8)
    c: Equal(g7,g9)
    c: InternalAlignment(g7,g10)
    c: InternalAlignment(g8,g10)
    c: InternalAlignment(g9,g10)
    c: InternalAlignment(g11,g10)
    c: InternalAlignment(g12,g10)
    c: Block(g4)
    c: Block(g10)
    c: Weight(g13) = 1
    c: Equal(g13,g14)
    c: Equal(g13,g15)
    c: InternalAlignment(g13,g16)
    c: InternalAlignment(g14,g16)
    c: InternalAlignment(g15,g16)
    c: InternalAlignment(g17,g16)
    c: InternalAlignment(g18,g16)
    c: Block(g16)
    c: Weight(g19) = 1
    c: Equal(g19,g20)
    c: Equal(g19,g21)
    c: InternalAlignment(g19,g22)
    c: InternalAlignment(g20,g22)
    c: InternalAlignment(g21,g22)
    c: InternalAlignment(g23,g22)
    c: InternalAlignment(g24,g22)
    c: Block(g22)
    c: Weight(g25) = 1
    c: Equal(g25,g26)
    c: Equal(g25,g27)
    c: InternalAlignment(g25,g28)
    c: InternalAlignment(g26,g28)
    c: InternalAlignment(g27,g28)
    c: InternalAlignment(g29,g28)
    c: InternalAlignment(g30,g28)
    c: Weight(g31) = 1
    c: Equal(g31,g32)
    c: Equal(g31,g33)
    c: InternalAlignment(g31,g34)
    c: InternalAlignment(g32,g34)
    c: InternalAlignment(g33,g34)
    c: InternalAlignment(g35,g34)
    c: InternalAlignment(g36,g34)
    c: Block(g34)
    c: Block(g28)
    c: Block(g37)
    c: Block(g0)
    c: Weight(g38) = 1
    c: Equal(g38,g40)
    c: InternalAlignment(g38,g41)
    c: InternalAlignment(g39,g41)
    c: InternalAlignment(g40,g41)
    c: InternalAlignment(g42,g41)
    c: InternalAlignment(g43,g41)
    c: InternalAlignment(g45,g44)
    c: InternalAlignment(g46,g44)
    c: Block(g47)
    c: Block(g44)
    c: Block(g41)
    c: Block(g48)
    c: Block(g49)
    c: Coincident(g50,g37)
    c: Coincident(g50,g0)
    c: Coincident(g51,g37)
    c: Coincident(g51,g0)
    c: Block(g51)
    c: Block(g50)
    c: Block(g52)
    c: Block(g53)
    c: Block(g54)
    c: Block(g55)
    c: Block(g56)
    c: Coincident(g57,g47)
    c: Vertical(g57)
    c: Coincident(g58,g47)
    c: Vertical(g58)
    c: Coincident(g59,g16)
    c: Coincident(g59,g58)
    c: Horizontal(g59)
    c: Coincident(g60,g16)
    c: Coincident(g60,g55)
    c: Coincident(g61,g55)
    c: Coincident(g61,g54)
    c: Coincident(g62,g54)
    c: Coincident(g62,g53)
    c: Coincident(g63,g53)
    c: Coincident(g63,g10)
    c: Coincident(g64,g10)
    c: Coincident(g64,g4)
    c: Vertical(g64)
    c: Coincident(g65,g4)
    c: Coincident(g65,g48)
    c: Coincident(g66,g49)
    c: Coincident(g66,g48)
    c: Coincident(g67,g49)
    c: Coincident(g67,g52)
    c: Coincident(g68,g52)
    c: Coincident(g68,g22)
    c: Coincident(g69,g57)
    c: Horizontal(g69)
    c: Coincident(g70,g44)
    c: Coincident(g70,g41)
    c: Coincident(g71,g41)
    c: Vertical(g71)
    c: Coincident(g72,g34)
    c: Coincident(g72,g56)
    c: Horizontal(g72)
    c: Coincident(g73,g56)
    c: Coincident(g73,g28)
    c: Vertical(g73)
    c: Coincident(g74,g28)
    c: Coincident(g74,g34)
    c: Block(g69)
    c: Coincident(g75,g69)
    c: Vertical(g75)
    c: Distance(g75) = 152
    c: Block(g71)
    c: Vertical(g76)
    c: Distance(g76) = 10
    c: Vertical(g77)
    c: Distance(g77) = 4
    c: Vertical(g78)
    c: Distance(g78) = 4
    c: Vertical(g79)
    c: Distance(g79) = 10
    c: Coincident(g80,g78)
    c: Coincident(g80,g77)
    c: Block(g80)
    c: Coincident(g81,g79)
    c: Coincident(g81,g76)
    c: Block(g81)
    c: Coincident(g82,g76)
    c: Coincident(g82,g71)
    c: Horizontal(g82)
    c: Coincident(g83,g75)
    c: Coincident(g83,g77)
    c: Horizontal(g83)
    c: Distance(g83) = 7
    c: Distance(g82) = 7
    c: Vertical(g84)
    c: Distance(g84) = 4
    c: Vertical(g85)
    c: Distance(g85) = 4
    c: Coincident(g86,g84)
    c: Coincident(g86,g85)
    c: Block(g86)
    c: Coincident(g87,g84)
    c: Horizontal(g87)
    c: Distance(g87) = 4
    c: Coincident(g88,g85)
    c: Horizontal(g88)
    c: Distance(g88) = 4
    c: Coincident(g89,g87)
    c: Coincident(g89,g44)
    c: Vertical(g89)
    c: Coincident(g90,g88)
    c: Coincident(g90,g22)
    c: Vertical(g90)
    c: Coincident(g91,g78)
    c: Coincident(g91,g79)
    c: Horizontal(g91)
FEATURE [Sketcher::SketchObject] Sketch008  label="rightSideTop"
  FullyConstrained = false
  sketch-geometry (93):
    g0: Circle CenterX=302.996 CenterY=111.695 CenterZ=0 NormalX=0 NormalY=0 NormalZ=1 AngleXU=0 Radius=1
    g1: Circle CenterX=306.073 CenterY=114.251 CenterZ=0 NormalX=0 NormalY=0 NormalZ=1 AngleXU=0 Radius=1
    g2: Circle CenterX=306.073 CenterY=110.251 CenterZ=0 NormalX=0 NormalY=0 NormalZ=1 AngleXU=0 Radius=1
    g3: BSplineCurve PolesCount=3 KnotsCount=2 Degree=2 IsPeriodic=0
    g4: GeomPoint X=302.996 Y=111.695 Z=0
    g5: GeomPoint X=306.073 Y=110.251 Z=0
    g6: Circle CenterX=306.073 CenterY=95.2763 CenterZ=0 NormalX=0 NormalY=0 NormalZ=1 AngleXU=0 Radius=1
    g7: Circle CenterX=306.073 CenterY=91.2763 CenterZ=0 NormalX=0 NormalY=0 NormalZ=1 AngleXU=0 Radius=1
    g8: Circle CenterX=302.567 CenterY=89.3511 CenterZ=0 NormalX=0 NormalY=0 NormalZ=1 AngleXU=0 Radius=1
    g9: BSplineCurve PolesCount=3 KnotsCount=2 Degree=2 IsPeriodic=0
    g10: GeomPoint X=306.073 Y=95.2763 Z=0
    g11: GeomPoint X=302.567 Y=89.3511 Z=0
    g12: LineSegment StartX=306.073 StartY=110.251 StartZ=0 EndX=306.073 EndY=95.2763 EndZ=0
    g13: Circle CenterX=302.073 CenterY=124.221 CenterZ=0 NormalX=0 NormalY=0 NormalZ=1 AngleXU=0 Radius=1
    g14: Circle CenterX=306.073 CenterY=124.221 CenterZ=0 NormalX=0 NormalY=0 NormalZ=1 AngleXU=0 Radius=1
    g15: Circle CenterX=302.996 CenterY=121.665 CenterZ=0 NormalX=0 NormalY=0 NormalZ=1 AngleXU=0 Radius=1
    g16: BSplineCurve PolesCount=3 KnotsCount=2 Degree=2 IsPeriodic=0
    g17: GeomPoint X=302.073 Y=124.221 Z=0
    g18: GeomPoint X=302.996 Y=121.665 Z=0
    g19: Circle CenterX=306.073 CenterY=73.3346 CenterZ=0 NormalX=0 NormalY=0 NormalZ=1 AngleXU=0 Radius=1
    g20: Circle CenterX=306.073 CenterY=77.3346 CenterZ=0 NormalX=0 NormalY=0 NormalZ=1 AngleXU=0 Radius=1
    g21: Circle CenterX=302.535 CenterY=75.4095 CenterZ=0 NormalX=0 NormalY=0 NormalZ=1 AngleXU=0 Radius=1
    g22: BSplineCurve PolesCount=3 KnotsCount=2 Degree=2 IsPeriodic=0
    g23: GeomPoint X=306.073 Y=73.3346 Z=0
    g24: GeomPoint X=302.535 Y=75.4095 Z=0
    g25: Circle CenterX=362.073 CenterY=124.221 CenterZ=0 NormalX=0 NormalY=0 NormalZ=1 AngleXU=0 Radius=1
    g26: Circle CenterX=366.073 CenterY=124.221 CenterZ=0 NormalX=0 NormalY=0 NormalZ=1 AngleXU=0 Radius=1
    g27: Circle CenterX=362.567 CenterY=122.294 CenterZ=0 NormalX=0 NormalY=0 NormalZ=1 AngleXU=0 Radius=1
    g28: BSplineCurve PolesCount=3 KnotsCount=2 Degree=2 IsPeriodic=0
    g29: GeomPoint X=362.073 Y=124.221 Z=0
    g30: GeomPoint X=362.567 Y=122.294 Z=0
    g31: Circle CenterX=322.073 CenterY=124.221 CenterZ=0 NormalX=0 NormalY=0 NormalZ=1 AngleXU=0 Radius=1
    g32: Circle CenterX=318.073 CenterY=124.221 CenterZ=0 NormalX=0 NormalY=0 NormalZ=1 AngleXU=0 Radius=1
    g33: Circle CenterX=318.073 CenterY=120.221 CenterZ=0 NormalX=0 NormalY=0 NormalZ=1 AngleXU=0 Radius=1
    g34: BSplineCurve PolesCount=3 KnotsCount=2 Degree=2 IsPeriodic=0
    g35: GeomPoint X=322.073 Y=124.221 Z=0
    g36: GeomPoint X=318.073 Y=120.221 Z=0
    g37: Circle CenterX=318.073 CenterY=109.865 CenterZ=0 NormalX=0 NormalY=0 NormalZ=1 AngleXU=0 Radius=1
    g38: GeomPoint X=318.073 Y=109.865 Z=0
    g39: Circle CenterX=322.073 CenterY=76.4095 CenterZ=0 NormalX=0 NormalY=0 NormalZ=1 AngleXU=0 Radius=4
    g40: Circle CenterX=232.072 CenterY=133.221 CenterZ=0 NormalX=0 NormalY=0 NormalZ=1 AngleXU=0 Radius=1
    g41: Circle CenterX=226.072 CenterY=136.221 CenterZ=0 NormalX=0 NormalY=0 NormalZ=1 AngleXU=0 Radius=1
    g42: Circle CenterX=226.072 CenterY=124.221 CenterZ=0 NormalX=0 NormalY=0 NormalZ=1 AngleXU=0 Radius=1
    g43: Circle CenterX=232.072 CenterY=127.221 CenterZ=0 NormalX=0 NormalY=0 NormalZ=1 AngleXU=0 Radius=1
    g44: BSplineCurve PolesCount=5 KnotsCount=3 Degree=3 IsPeriodic=0
    g45: GeomPoint X=232.072 Y=133.221 Z=0
    g46: GeomPoint X=223.072 Y=130.221 Z=0
    g47: GeomPoint X=232.072 Y=127.221 Z=0
    g48: LineSegment StartX=240.687 StartY=51.8263 StartZ=0 EndX=243.317 EndY=53.2701 EndZ=0
    g49: LineSegment StartX=243.575 StartY=46.5669 StartZ=0 EndX=246.205 EndY=48.0108 EndZ=0
    g50: ArcOfCircle CenterX=247.391 CenterY=52.0843 CenterZ=0 NormalX=0 NormalY=0 NormalZ=1 AngleXU=0 Radius=4.24264 StartAngle=4.42912 EndAngle=9.14151
    g51: LineSegment StartX=243.475 StartY=65.4951 StartZ=0 EndX=245.073 EndY=63.5726 EndZ=0
    g52: LineSegment StartX=243.575 StartY=46.5669 StartZ=0 EndX=245.072 EndY=43.8408 EndZ=0
    g53: LineSegment StartX=245.072 StartY=43.8408 StartZ=0 EndX=302.535 EndY=75.4095 EndZ=0
    g54: LineSegment StartX=239.192 StartY=54.5542 StartZ=0 EndX=302.567 EndY=89.3511 EndZ=0
    g55: LineSegment StartX=232.072 StartY=127.221 StartZ=0 EndX=232.072 EndY=124.221 EndZ=0
    g56: LineSegment StartX=232.072 StartY=136.221 StartZ=0 EndX=232.072 EndY=133.221 EndZ=0
    g57: LineSegment StartX=232.072 StartY=136.221 StartZ=0 EndX=407.073 EndY=136.221 EndZ=0
    g58: LineSegment StartX=322.073 StartY=124.221 StartZ=0 EndX=362.073 EndY=124.221 EndZ=0
    g59: LineSegment StartX=232.072 StartY=124.221 StartZ=0 EndX=302.073 EndY=124.221 EndZ=0
    g60: LineSegment StartX=302.996 StartY=121.665 StartZ=0 EndX=240.171 EndY=69.471 EndZ=0
    g61: LineSegment StartX=240.171 StartY=69.471 StartZ=0 EndX=241.711 EndY=67.6177 EndZ=0
    g62: LineSegment StartX=241.711 StartY=67.6177 StartZ=0 EndX=246.787 EndY=71.8365 EndZ=0
    g63: LineSegment StartX=246.787 StartY=71.8365 StartZ=0 EndX=248.551 EndY=69.712 EndZ=0
    g64: LineSegment StartX=248.551 StartY=69.712 StartZ=0 EndX=243.475 EndY=65.4951 EndZ=0
    g65: LineSegment StartX=245.073 StartY=63.5726 StartZ=0 EndX=302.996 EndY=111.695 EndZ=0
    g66: LineSegment StartX=239.192 StartY=54.5542 StartZ=0 EndX=240.687 EndY=51.8263 EndZ=0
    g67: LineSegment StartX=375.073 StartY=48.2206 StartZ=0 EndX=382.073 EndY=48.2206 EndZ=0
    g68: LineSegment StartX=407.073 StartY=48.2206 StartZ=0 EndX=400.073 EndY=48.2206 EndZ=0
    g69: LineSegment StartX=394.073 StartY=48.2206 StartZ=0 EndX=394.073 EndY=52.2206 EndZ=0
    g70: LineSegment StartX=388.073 StartY=48.2206 StartZ=0 EndX=388.073 EndY=58.2206 EndZ=0
    g71: ArcOfCircle CenterX=385.073 CenterY=61.2206 CenterZ=0 NormalX=0 NormalY=0 NormalZ=1 AngleXU=0 Radius=4.24264 StartAngle=5.49779 EndAngle=10.2102
    g72: ArcOfCircle CenterX=397.073 CenterY=55.2206 CenterZ=0 NormalX=0 NormalY=0 NormalZ=1 AngleXU=0 Radius=4.24264 StartAngle=5.49779 EndAngle=10.2102
    g73: LineSegment StartX=382.073 StartY=58.2206 StartZ=0 EndX=382.073 EndY=48.2206 EndZ=0
    g74: LineSegment StartX=400.073 StartY=52.2206 StartZ=0 EndX=400.073 EndY=48.2206 EndZ=0
    g75: LineSegment StartX=394.073 StartY=48.2206 StartZ=0 EndX=388.073 EndY=48.2206 EndZ=0
    g76: LineSegment StartX=306.073 StartY=-27.5935 StartZ=0 EndX=310.073 EndY=-27.5935 EndZ=0
    g77: LineSegment StartX=318.073 StartY=-27.5935 StartZ=0 EndX=314.073 EndY=-27.5935 EndZ=0
    g78: LineSegment StartX=310.073 StartY=-27.5935 StartZ=0 EndX=310.073 EndY=-31.5935 EndZ=0
    g79: LineSegment StartX=314.073 StartY=-27.5935 StartZ=0 EndX=314.073 EndY=-31.5935 EndZ=0
    g80: ArcOfCircle CenterX=312.073 CenterY=-33.5935 CenterZ=0 NormalX=0 NormalY=0 NormalZ=1 AngleXU=0 Radius=2.82843 StartAngle=2.35619 EndAngle=7.06858
    g81: LineSegment StartX=407.073 StartY=48.2206 StartZ=0 EndX=407.073 EndY=136.221 EndZ=0
    g82: LineSegment StartX=306.073 StartY=73.3346 StartZ=0 EndX=306.073 EndY=-27.5935 EndZ=0
    g83: BSplineCurve PolesCount=3 KnotsCount=2 Degree=2 IsPeriodic=0
    g84: BSplineCurve PolesCount=3 KnotsCount=2 Degree=2 IsPeriodic=0
    g85: LineSegment StartX=375.073 StartY=64.4106 StartZ=0 EndX=375.073 EndY=48.2206 EndZ=0
    g86: LineSegment StartX=318.073 StartY=64.4065 StartZ=0 EndX=318.073 EndY=-27.5935 EndZ=0
    g87: LineSegment StartX=322.073 StartY=68.4065 StartZ=0 EndX=371.073 EndY=68.4065 EndZ=0
    g88: BSplineCurve PolesCount=3 KnotsCount=2 Degree=2 IsPeriodic=0
    g89: LineSegment StartX=318.073 StartY=120.221 StartZ=0 EndX=318.073 EndY=113.865 EndZ=0
    g90: BSplineCurve PolesCount=3 KnotsCount=2 Degree=2 IsPeriodic=0
    g91: LineSegment StartX=322.073 StartY=109.865 StartZ=0 EndX=328.643 EndY=109.865 EndZ=0
    g92: LineSegment StartX=336.157 StartY=111.779 StartZ=0 EndX=362.567 EndY=122.294 EndZ=0
  constraints (140):
    c: Weight(g0) = 1
    c: Equal(g0,g1)
    c: Equal(g0,g2)
    c: InternalAlignment(g0,g3)
    c: InternalAlignment(g1,g3)
    c: InternalAlignment(g2,g3)
    c: InternalAlignment(g4,g3)
    c: InternalAlignment(g5,g3)
    c: Weight(g6) = 1
    c: Equal(g6,g7)
    c: Equal(g6,g8)
    c: InternalAlignment(g6,g9)
    c: InternalAlignment(g7,g9)
    c: InternalAlignment(g8,g9)
    c: InternalAlignment(g10,g9)
    c: InternalAlignment(g11,g9)
    c: Block(g3)
    c: Block(g9)
    c: Coincident(g12,g3)
    c: Coincident(g12,g9)
    c: Vertical(g12)
    c: Weight(g13) = 1
    c: Equal(g13,g14)
    c: Equal(g13,g15)
    c: InternalAlignment(g14,g16)
    c: InternalAlignment(g15,g16)
    c: InternalAlignment(g17,g16)
    c: InternalAlignment(g18,g16)
    c: Block(g51)
    c: Block(g52)
    c: Coincident(g53,g52)
    c: Coincident(g53,g22)
    c: Block(g53)
    c: Coincident(g50,g49)
    c: Coincident(g50,g48)
    c: Coincident(g54,g9)
    c: Block(g54)
    c: Distance(g51) = 2.5
    c: Block(g44)
    c: Coincident(g55,g44)
    c: Vertical(g55)
    c: Coincident(g56,g44)
    c: Vertical(g56)
    c: Coincident(g57,g56)
    c: Horizontal(g57)
    c: Coincident(g58,g34)
    c: Coincident(g58,g28)
    c: Horizontal(g58)
    c: Block(g34)
    c: Block(g28)
    c: Coincident(g59,g55)
    c: Coincident(g59,g16)
    c: Horizontal(g59)
    c: Coincident(g60,g16)
    c: Block(g59)
    c: Block(g60)
    c: Block(g16)
    c: Coincident(g61,g60)
    c: Block(g61)
    c: Coincident(g62,g61)
    c: Block(g62)
    c: Coincident(g63,g62)
    c: Coincident(g64,g63)
    c: Coincident(g64,g51)
    c: Block(g64)
    c: Coincident(g65,g51)
    c: Coincident(g65,g3)
    c: Block(g65)
    c: Coincident(g66,g54)
    c: Coincident(g66,g48)
    c: Block(g50)
    c: Block(g48)
    c: Block(g49)
    c: Block(g22)
    c: Horizontal(g67)
    c: Distance(g67) = 7
    c: Horizontal(g68)
    c: Distance(g68) = 7
    c: Vertical(g69)
    c: Distance(g69) = 4
    c: Vertical(g70)
    c: Distance(g70) = 10
    c: Coincident(g71,g70)
    c: Coincident(g72,g69)
    c: Block(g72)
    c: Block(g71)
    c: Coincident(g73,g71)
    c: Coincident(g73,g67)
    c: Vertical(g73)
    c: Coincident(g74,g72)
    c: Coincident(g74,g68)
    c: Vertical(g74)
    c: Coincident(g75,g69)
    c: Coincident(g75,g70)
    c: Horizontal(g75)
    c: Horizontal(g76)
    c: Distance(g76) = 4
    c: Horizontal(g77)
    c: Distance(g77) = 4
    c: Coincident(g78,g76)
    c: Vertical(g78)
    c: Coincident(g79,g77)
    c: Vertical(g79)
    c: Distance(g78) = 4
    c: Distance(g79) = 4
    c: Coincident(g80,g78)
    c: Coincident(g80,g79)
    c: Block(g80)
    c: Coincident(g81,g68)
    c: Coincident(g81,g57)
    c: Vertical(g81)
    c: Block(g57)
    c: Block(g81)
    c: Coincident(g82,g22)
    c: Coincident(g82,g76)
    c: Vertical(g82)
    c: Block(g67)
    c: Block(g83)
    c: Block(g84)
    c: Coincident(g85,g83)
    c: Coincident(g85,g67)
    c: Vertical(g85)
    c: Coincident(g86,g84)
    c: Coincident(g86,g77)
    c: Vertical(g86)
    c: Coincident(g87,g84)
    c: Coincident(g87,g83)
    c: Horizontal(g87)
    c: Block(g88)
    c: Coincident(g89,g34)
    c: Coincident(g89,g88)
    c: Vertical(g89)
    c: Block(g90)
    c: Coincident(g91,g88)
    c: Coincident(g91,g90)
    c: Horizontal(g91)
    c: Coincident(g92,g90)
    c: Coincident(g92,g28)
    c: Distance(g57) = 175.001
    c: Distance(g81) = 88
FEATURE [Sketcher::SketchObject] Sketch009  label="middleBottom"
  FullyConstrained = true
  sketch-geometry (109):
    g0: Circle CenterX=175.022 CenterY=5.37834 CenterZ=0 NormalX=0 NormalY=0 NormalZ=1 AngleXU=0 Radius=1
    g1: Circle CenterX=179.022 CenterY=7.57463 CenterZ=0 NormalX=0 NormalY=0 NormalZ=1 AngleXU=0 Radius=1
    g2: Circle CenterX=179.022 CenterY=5.34704 CenterZ=0 NormalX=0 NormalY=0 NormalZ=1 AngleXU=0 Radius=1
    g3: BSplineCurve PolesCount=3 KnotsCount=2 Degree=2 IsPeriodic=0
    g4: GeomPoint X=175.022 Y=5.37834 Z=0
    g5: GeomPoint X=179.022 Y=5.34704 Z=0
    g6: Circle CenterX=189.124 CenterY=5.37834 CenterZ=0 NormalX=0 NormalY=0 NormalZ=1 AngleXU=0 Radius=1
    g7: Circle CenterX=185.124 CenterY=7.57463 CenterZ=0 NormalX=0 NormalY=0 NormalZ=1 AngleXU=0 Radius=1
    g8: Circle CenterX=185.124 CenterY=5.34704 CenterZ=0 NormalX=0 NormalY=0 NormalZ=1 AngleXU=0 Radius=1
    g9: BSplineCurve PolesCount=3 KnotsCount=2 Degree=2 IsPeriodic=0
    g10: GeomPoint X=189.124 Y=5.37834 Z=0
    g11: GeomPoint X=185.124 Y=5.34704 Z=0
    g12: Circle CenterX=224.513 CenterY=-14.0532 CenterZ=0 NormalX=0 NormalY=0 NormalZ=1 AngleXU=0 Radius=1
    g13: Circle CenterX=236.584 CenterY=-24.2775 CenterZ=0 NormalX=0 NormalY=0 NormalZ=1 AngleXU=0 Radius=1
    g14: BSplineCurve PolesCount=3 KnotsCount=2 Degree=2 IsPeriodic=0
    g15: GeomPoint X=236.584 Y=-24.2775 Z=0
    g16: Circle CenterX=125.607 CenterY=-21.7539 CenterZ=0 NormalX=0 NormalY=0 NormalZ=1 AngleXU=0 Radius=1
    g17: Circle CenterX=139.632 CenterY=-14.0532 CenterZ=0 NormalX=0 NormalY=0 NormalZ=1 AngleXU=0 Radius=1
    g18: Circle CenterX=127.325 CenterY=-24.2775 CenterZ=0 NormalX=0 NormalY=0 NormalZ=1 AngleXU=0 Radius=1
    g19: BSplineCurve PolesCount=3 KnotsCount=2 Degree=2 IsPeriodic=0
    g20: GeomPoint X=125.607 Y=-21.7539 Z=0
    g21: GeomPoint X=127.325 Y=-24.2775 Z=0
    g22: Circle CenterX=179.022 CenterY=-85.8163 CenterZ=0 NormalX=0 NormalY=0 NormalZ=1 AngleXU=0 Radius=1
    g23: Circle CenterX=179.022 CenterY=-91.7794 CenterZ=0 NormalX=0 NormalY=0 NormalZ=1 AngleXU=0 Radius=1
    g24: Circle CenterX=171.895 CenterY=-91.8014 CenterZ=0 NormalX=0 NormalY=0 NormalZ=1 AngleXU=0 Radius=1
    g25: BSplineCurve PolesCount=3 KnotsCount=2 Degree=2 IsPeriodic=0
    g26: GeomPoint X=179.022 Y=-85.8163 Z=0
    g27: GeomPoint X=171.895 Y=-91.8014 Z=0
    g28: Circle CenterX=185.124 CenterY=-86.2028 CenterZ=0 NormalX=0 NormalY=0 NormalZ=1 AngleXU=0 Radius=1
    g29: Circle CenterX=185.124 CenterY=-91.7794 CenterZ=0 NormalX=0 NormalY=0 NormalZ=1 AngleXU=0 Radius=1
    g30: Circle CenterX=191.747 CenterY=-91.7794 CenterZ=0 NormalX=0 NormalY=0 NormalZ=1 AngleXU=0 Radius=1
    g31: BSplineCurve PolesCount=3 KnotsCount=2 Degree=2 IsPeriodic=0
    g32: GeomPoint X=185.124 Y=-86.2028 Z=0
    g33: GeomPoint X=191.747 Y=-91.7794 Z=0
    g34: BSplineCurve PolesCount=5 KnotsCount=3 Degree=3 IsPeriodic=0
    g35: LineSegment StartX=132.072 StartY=-100.779 StartZ=0 EndX=132.072 EndY=-103.779 EndZ=0
    g36: GeomPoint X=232.072 Y=-94.7794 Z=0
    g37: GeomPoint X=223.072 Y=-97.7794 Z=0
    g38: Circle CenterX=232.072 CenterY=-94.7794 CenterZ=0 NormalX=0 NormalY=0 NormalZ=1 AngleXU=0 Radius=1
    g39: Circle CenterX=232.072 CenterY=-100.779 CenterZ=0 NormalX=0 NormalY=0 NormalZ=1 AngleXU=0 Radius=1
    g40: BSplineCurve PolesCount=5 KnotsCount=3 Degree=3 IsPeriodic=0
    g41: GeomPoint X=232.072 Y=-100.779 Z=0
    g42: LineSegment StartX=123.656 StartY=-37.1092 StartZ=0 EndX=122.136 EndY=-35.2714 EndZ=0
    g43: LineSegment StartX=117.05 StartY=-39.4781 StartZ=0 EndX=115.291 EndY=-37.3514 EndZ=0
    g44: LineSegment StartX=120.377 StartY=-33.1447 StartZ=0 EndX=118.86 EndY=-31.3104 EndZ=0
    g45: ArcOfCircle CenterX=116.562 CenterY=-19.6236 CenterZ=0 NormalX=0 NormalY=0 NormalZ=1 AngleXU=0 Radius=4.24264 StartAngle=1.28753 EndAngle=5.99992
    g46: LineSegment StartX=240.266 StartY=-37.1092 StartZ=0 EndX=189.124 EndY=5.37834 EndZ=0
    g47: LineSegment StartX=191.747 StartY=-91.7794 StartZ=0 EndX=232.072 EndY=-91.7794 EndZ=0
    g48: LineSegment StartX=232.072 StartY=-91.7794 StartZ=0 EndX=232.072 EndY=-94.7794 EndZ=0
    g49: LineSegment StartX=232.072 StartY=-100.779 StartZ=0 EndX=232.072 EndY=-103.779 EndZ=0
    g50: LineSegment StartX=132.072 StartY=-103.779 StartZ=0 EndX=232.072 EndY=-103.779 EndZ=0
    g51: LineSegment StartX=132.072 StartY=-91.8014 StartZ=0 EndX=132.072 EndY=-94.7791 EndZ=0
    g52: LineSegment StartX=132.072 StartY=-91.8014 StartZ=0 EndX=171.895 EndY=-91.8014 EndZ=0
    g53: LineSegment StartX=179.022 StartY=-85.8163 StartZ=0 EndX=179.022 EndY=5.34704 EndZ=0
    g54: LineSegment StartX=175.022 StartY=5.37834 StartZ=0 EndX=123.656 EndY=-37.1092 EndZ=0
    g55: LineSegment StartX=185.124 StartY=5.34704 StartZ=0 EndX=185.124 EndY=-86.2028 EndZ=0
    g56: LineSegment StartX=122.136 StartY=-35.2714 StartZ=0 EndX=117.05 EndY=-39.4781 EndZ=0
    g57: LineSegment StartX=115.291 StartY=-37.3514 StartZ=0 EndX=120.377 EndY=-33.1447 EndZ=0
    g58: LineSegment StartX=118.86 StartY=-31.3104 StartZ=0 EndX=127.325 EndY=-24.2775 EndZ=0
    g59: LineSegment StartX=125.607 StartY=-21.7539 StartZ=0 EndX=124.815 EndY=-22.1887 EndZ=0
    g60: LineSegment StartX=123.265 StartY=-19.3655 StartZ=0 EndX=124.815 EndY=-22.1887 EndZ=0
    g61: LineSegment StartX=120.636 StartY=-20.8094 StartZ=0 EndX=123.265 EndY=-19.3655 EndZ=0
    g62: LineSegment StartX=117.748 StartY=-15.55 StartZ=0 EndX=120.377 EndY=-14.1062 EndZ=0
    g63: LineSegment StartX=120.377 StartY=-14.1062 StartZ=0 EndX=118.934 EndY=-11.4765 EndZ=0
    g64: LineSegment StartX=236.584 StartY=-24.2775 StartZ=0 EndX=245.072 EndY=-31.3037 EndZ=0
    g65: LineSegment StartX=245.072 StartY=-31.3037 StartZ=0 EndX=243.535 EndY=-33.1602 EndZ=0
    g66: LineSegment StartX=243.535 StartY=-33.1602 StartZ=0 EndX=248.619 EndY=-37.3688 EndZ=0
    g67: LineSegment StartX=248.619 StartY=-37.3688 StartZ=0 EndX=246.855 EndY=-39.5064 EndZ=0
    g68: LineSegment StartX=246.855 StartY=-39.5064 StartZ=0 EndX=241.778 EndY=-35.2889 EndZ=0
    g69: LineSegment StartX=241.778 StartY=-35.2889 StartZ=0 EndX=240.266 EndY=-37.1092 EndZ=0
    g70: LineSegment StartX=243.628 StartY=-14.0323 StartZ=0 EndX=246.258 EndY=-15.476 EndZ=0
    g71: LineSegment StartX=240.741 StartY=-19.2917 StartZ=0 EndX=243.37 EndY=-20.7355 EndZ=0
    g72: ArcOfCircle CenterX=247.444 CenterY=-19.5496 CenterZ=0 NormalX=0 NormalY=0 NormalZ=1 AngleXU=0 Radius=4.24264 StartAngle=3.4249 EndAngle=8.13729
    g73: LineSegment StartX=240.741 StartY=-19.2917 StartZ=0 EndX=239.201 EndY=-22.0968 EndZ=0
    g74: LineSegment StartX=238.538 StartY=-21.7516 StartZ=0 EndX=239.201 EndY=-22.0968 EndZ=0
    g75: LineSegment StartX=245.072 StartY=-11.4025 StartZ=0 EndX=243.628 EndY=-14.0323 EndZ=0
    g76-g91: Circle x16 (B-spline internal-alignment scaffolding for g92; pole/knot coordinates omitted)
    g92: BSplineCurve PolesCount=16 KnotsCount=14 Degree=3 IsPeriodic=0
    g93-g106: GeomPoint x14 (B-spline internal-alignment scaffolding for g92; pole/knot coordinates omitted)
    g107: LineSegment StartX=165.871 StartY=14.2956 StartZ=0 EndX=118.934 EndY=-11.4765 EndZ=0
    g108: LineSegment StartX=198.264 StartY=14.2963 StartZ=0 EndX=245.072 EndY=-11.4025 EndZ=0
  constraints (146):
    c: Weight(g0) = 1
    c: Equal(g0,g1)
    c: Equal(g0,g2)
    c: InternalAlignment(g0,g3)
    c: InternalAlignment(g1,g3)
    c: InternalAlignment(g2,g3)
    c: InternalAlignment(g4,g3)
    c: InternalAlignment(g5,g3)
    c: Weight(g6) = 1
    c: Equal(g6,g7)
    c: Equal(g6,g8)
    c: InternalAlignment(g6,g9)
    c: InternalAlignment(g7,g9)
    c: InternalAlignment(g8,g9)
    c: InternalAlignment(g10,g9)
    c: InternalAlignment(g11,g9)
    c: Block(g9)
    c: Block(g3)
    c: InternalAlignment(g12,g14)
    c: InternalAlignment(g13,g14)
    c: InternalAlignment(g15,g14)
    c: Block(g14)
    c: Weight(g16) = 1
    c: Equal(g16,g17)
    c: Equal(g16,g18)
    c: InternalAlignment(g16,g19)
    c: InternalAlignment(g17,g19)
    c: InternalAlignment(g18,g19)
    c: InternalAlignment(g20,g19)
    c: InternalAlignment(g21,g19)
    c: Block(g19)
    c: Weight(g22) = 1
    c: Equal(g22,g23)
    c: Equal(g22,g24)
    c: InternalAlignment(g22,g25)
    c: InternalAlignment(g23,g25)
    c: InternalAlignment(g24,g25)
    c: InternalAlignment(g26,g25)
    c: InternalAlignment(g27,g25)
    c: Weight(g28) = 1
    c: Equal(g28,g29)
    c: Equal(g28,g30)
    c: InternalAlignment(g28,g31)
    c: InternalAlignment(g29,g31)
    c: InternalAlignment(g30,g31)
    c: InternalAlignment(g32,g31)
    c: InternalAlignment(g33,g31)
    c: Block(g31)
    c: Block(g25)
    c: Block(g34)
    c: Coincident(g35,g34)
    c: Vertical(g35)
    c: Block(g35)
    c: Equal(g38,g39)
    c: InternalAlignment(g38,g40)
    c: InternalAlignment(g39,g40)
    c: InternalAlignment(g36,g40)
    c: InternalAlignment(g37,g40)
    c: InternalAlignment(g41,g40)
    c: Block(g40)
    c: Distance(g42) = 2.385
    c: Distance(g43) = 2.76
    c: Parallel(g42,g44)
    c: Block(g45)
    c: Coincident(g46,g9)
    c: Coincident(g47,g31)
    c: Horizontal(g47)
    c: Block(g47)
    c: Coincident(g48,g47)
    c: Coincident(g48,g40)
    c: Vertical(g48)
    c: Block(g48)
    c: Coincident(g49,g40)
    c: Vertical(g49)
    c: Block(g49)
    c: Coincident(g50,g35)
    c: Coincident(g50,g49)
    c: Horizontal(g50)
    c: Block(g50)
    c: Coincident(g51,g34)
    c: Vertical(g51)
    c: Coincident(g52,g51)
    c: Coincident(g52,g25)
    c: Horizontal(g52)
    c: Coincident(g53,g25)
    c: Coincident(g53,g3)
    c: Vertical(g53)
    c: Coincident(g54,g3)
    c: Coincident(g54,g42)
    c: Coincident(g55,g9)
    c: Coincident(g55,g31)
    c: Vertical(g55)
    c: Block(g42)
    c: Coincident(g56,g42)
    c: Coincident(g56,g43)
    c: Coincident(g57,g43)
    c: Coincident(g57,g44)
    c: Block(g57)
    c: Block(g56)
    c: Coincident(g58,g44)
    c: Coincident(g58,g19)
    c: Block(g58)
    c: Coincident(g59,g19)
    c: Block(g59)
    c: Coincident(g60,g59)
    c: Block(g60)
    c: Coincident(g61,g45)
    c: Coincident(g61,g60)
    c: Coincident(g62,g45)
    c: Coincident(g63,g62)
    c: Block(g63)
    c: Coincident(g64,g14)
    c: Block(g64)
    c: Coincident(g65,g64)
    c: Coincident(g66,g65)
    c: Coincident(g67,g66)
    c: Coincident(g68,g67)
    c: Coincident(g69,g68)
    c: Coincident(g69,g46)
    c: Block(g46)
    c: Block(g68)
    c: Block(g66)
    c: Distance(g70) = 3
    c: Distance(g71) = 3
    c: Coincident(g72,g70)
    c: Coincident(g72,g71)
    c: Block(g72)
    c: Coincident(g73,g71)
    c: Distance(g73) = 3.2
    c: Coincident(g74,g14)
    c: Coincident(g74,g73)
    c: Coincident(g75,g70)
    c: Block(g75)
    c: Block(g73)
    c: Distance(g63) = 3
    c: Distance(g60) = 3.22077
    c: Weight(g76) = 1
    c: Equal(g76, g77-g91) x15
    c: InternalAlignment(g76-g91 -> g92) x16
    c: InternalAlignment(g93-g106 -> g92) x14
    c: Coincident(g107,g92)
    c: Coincident(g107,g63)
    c: Block(g107)
    c: Block(g92)
    c: Coincident(g108,g92)
    c: Coincident(g108,g75)
FEATURE [Sketcher::SketchObject] Sketch010  label="legBottomBack"
  FullyConstrained = true
  MapMode = 4
  Placement = pos=(0,0,0) rot=(0.57735,0.57735,0.57735;2.0944rad)
  sketch-geometry (76):
    g0: Circle CenterX=-17.0256 CenterY=-190.268 CenterZ=0 NormalX=0 NormalY=0 NormalZ=1 AngleXU=0 Radius=10.5072
    g1: Circle CenterX=-37.7758 CenterY=-187.672 CenterZ=0 NormalX=0 NormalY=0 NormalZ=1 AngleXU=0 Radius=5.64388
    g2: Circle CenterX=-51.4606 CenterY=-185.091 CenterZ=0 NormalX=0 NormalY=0 NormalZ=1 AngleXU=0 Radius=3.01653
    g3: Circle CenterX=-60.4835 CenterY=-182.688 CenterZ=0 NormalX=0 NormalY=0 NormalZ=1 AngleXU=0 Radius=2.12826
    g4: Circle CenterX=-3.29005 CenterY=-177.662 CenterZ=0 NormalX=0 NormalY=0 NormalZ=1 AngleXU=0 Radius=3.26661
    g5: ArcOfCircle CenterX=11.0205 CenterY=-198.019 CenterZ=0 NormalX=0 NormalY=0 NormalZ=1 AngleXU=0 Radius=13 StartAngle=2.78068 EndAngle=5.92131
    g6: LineSegment StartX=5.08312 StartY=-176.581 StartZ=0 EndX=-1.14188 EndY=-193.429 EndZ=0
    g7: ArcOfCircle CenterX=17.2475 CenterY=-181.166 CenterZ=0 NormalX=0 NormalY=0 NormalZ=1 AngleXU=0 Radius=13 StartAngle=1.21042 EndAngle=2.78109
    g8: LineSegment StartX=38.8952 StartY=-231.233 StartZ=0 EndX=39.9512 EndY=-228.425 EndZ=0
    g9: ArcOfCircle CenterX=46.9911 CenterY=-209.705 CenterZ=0 NormalX=0 NormalY=0 NormalZ=1 AngleXU=0 Radius=20 StartAngle=2.78766 EndAngle=4.35269
    g10: LineSegment StartX=23.7323 StartY=-126.969 StartZ=0 EndX=17.4091 EndY=-143.817 EndZ=0
    g11: ArcOfCircle CenterX=29.5716 CenterY=-148.408 CenterZ=0 NormalX=0 NormalY=0 NormalZ=1 AngleXU=0 Radius=13 StartAngle=2.78068 EndAngle=4.35262
    g12: ArcOfCircle CenterX=35.8967 CenterY=-131.555 CenterZ=0 NormalX=0 NormalY=0 NormalZ=1 AngleXU=0 Radius=13 StartAngle=1.21584 EndAngle=2.78109
    g13: ArcOfCircle CenterX=48.1805 CenterY=-98.7782 CenterZ=0 NormalX=0 NormalY=0 NormalZ=1 AngleXU=0 Radius=13 StartAngle=2.78068 EndAngle=4.35005
    g14: LineSegment StartX=42.354 StartY=-77.3391 StartZ=0 EndX=36.018 EndY=-94.1875 EndZ=0
    g15: ArcOfCircle CenterX=54.5183 CenterY=-81.9247 CenterZ=0 NormalX=0 NormalY=0 NormalZ=1 AngleXU=0 Radius=13 StartAngle=2.42113 EndAngle=2.78109
    g16: ArcOfCircle CenterX=20.184 CenterY=-217.506 CenterZ=0 NormalX=0 NormalY=0 NormalZ=1 AngleXU=0 Radius=3.81084 StartAngle=1.88136 EndAngle=6.80465
    g17: LineSegment StartX=38.4753 StartY=-115.966 StartZ=0 EndX=41.2852 EndY=-117.017 EndZ=0
    g18: ArcOfCircle CenterX=36.3663 CenterY=-113.042 CenterZ=0 NormalX=0 NormalY=0 NormalZ=1 AngleXU=0 Radius=3.60555 StartAngle=0.230024 EndAngle=5.3372
    g19: LineSegment StartX=39.8769 StartY=-112.22 StartZ=0 EndX=42.6867 EndY=-113.271 EndZ=0
    g20: LineSegment StartX=19.9036 StartY=-165.61 StartZ=0 EndX=22.7134 EndY=-166.661 EndZ=0
    g21: ArcOfCircle CenterX=17.7945 CenterY=-162.686 CenterZ=0 NormalX=0 NormalY=0 NormalZ=1 AngleXU=0 Radius=3.60555 StartAngle=0.230024 EndAngle=5.3372
    g22: LineSegment StartX=21.3051 StartY=-161.864 StartZ=0 EndX=24.1149 EndY=-162.915 EndZ=0
    g23: LineSegment StartX=41.085 StartY=-66.3176 StartZ=0 EndX=46.0385 EndY=-62.5254 EndZ=0
    g24: LineSegment StartX=48.9563 StartY=-66.3367 StartZ=0 EndX=44.7488 EndY=-73.3482 EndZ=0
    g25: ArcOfCircle CenterX=49.8795 CenterY=-62.6074 CenterZ=0 NormalX=0 NormalY=0 NormalZ=1 AngleXU=0 Radius=3.84187 StartAngle=4.46973 EndAngle=9.40343
    g26: LineSegment StartX=43.5724 StartY=-110.934 StartZ=0 EndX=42.6867 EndY=-113.271 EndZ=0
    g27: LineSegment StartX=40.4148 StartY=-119.365 StartZ=0 EndX=41.2852 EndY=-117.017 EndZ=0
    g28: LineSegment StartX=21.8316 StartY=-169.001 StartZ=0 EndX=22.7134 EndY=-166.661 EndZ=0
    g29: LineSegment StartX=24.9948 StartY=-160.575 StartZ=0 EndX=24.1149 EndY=-162.915 EndZ=0
    g30: LineSegment StartX=23.1786 StartY=-202.622 StartZ=0 EndX=19.0195 EndY=-213.878 EndZ=0
    g31: LineSegment StartX=28.2308 StartY=-202.773 StartZ=0 EndX=23.4884 EndY=-215.608 EndZ=0
    g32: LineSegment StartX=-76.2249 StartY=-179.393 StartZ=0 EndX=-72.8553 EndY=-180.66 EndZ=0
    g33: ArcOfCircle CenterX=-71.1257 CenterY=-183.448 CenterZ=0 NormalX=0 NormalY=0 NormalZ=1 AngleXU=0 Radius=3.28025 StartAngle=3.43759 EndAngle=8.40938
    g34: LineSegment StartX=-79.0409 StartY=-186.881 StartZ=0 EndX=38.8952 EndY=-231.233 EndZ=0
    g35-g53: Circle x19 (B-spline internal-alignment scaffolding for g54; pole/knot coordinates omitted)
    g54: BSplineCurve PolesCount=19 KnotsCount=17 Degree=3 IsPeriodic=0
    g55-g71: GeomPoint x17 (B-spline internal-alignment scaffolding for g54; pole/knot coordinates omitted)
    g72: LineSegment StartX=-74.2633 StartY=-184.404 StartZ=0 EndX=-77.6329 EndY=-183.137 EndZ=0
    g73: LineSegment StartX=-79.0409 StartY=-186.881 StartZ=0 EndX=-77.6329 EndY=-183.137 EndZ=0
    g74: LineSegment StartX=8.65492 StartY=-152.553 StartZ=0 EndX=41.085 EndY=-66.3176 EndZ=0
    g75: LineSegment StartX=-74.4658 StartY=-174.715 StartZ=0 EndX=-76.2249 EndY=-179.393 EndZ=0
  constraints (76):
    c: Block(g5)
    c: Block(g7)
    c: Block(g0)
    c: Block(g4)
    c: Block(g1)
    c: Block(g2)
    c: Block(g3)
    c: Block(g9)
    c: Coincident(g8,g9)
    c: Block(g8)
    c: Coincident(g6,g7)
    c: Coincident(g6,g5)
    c: Block(g11)
    c: Block(g12)
    c: Coincident(g10,g12)
    c: Coincident(g10,g11)
    c: Block(g13)
    c: Block(g15)
    c: Coincident(g14,g15)
    c: Coincident(g14,g13)
    c: Block(g16)
    c: Block(g18)
    c: Coincident(g19,g18)
    c: Coincident(g17,g18)
    c: Parallel(g19,g17)
    c: Block(g17)
    c: Block(g19)
    c: Block(g21)
    c: Coincident(g22,g21)
    c: Coincident(g20,g21)
    c: Parallel(g22,g20)
    c: Block(g20)
    c: Block(g22)
    c: Block(g23)
    c: Coincident(g25,g23)
    c: Coincident(g25,g24)
    c: Block(g25)
    c: Block(g24)
    c: Coincident(g26,g19)
    c: Block(g26)
    c: Coincident(g27,g17)
    c: Block(g27)
    c: Coincident(g28,g20)
    c: Coincident(g29,g22)
    c: Block(g29)
    c: Block(g28)
    c: Coincident(g30,g5)
    c: Coincident(g30,g16)
    c: Block(g30)
    c: Coincident(g7,g28)
    c: Coincident(g11,g29)
    c: Coincident(g12,g27)
    c: Coincident(g13,g26)
    c: Coincident(g15,g24)
    c: Coincident(g31,g9)
    c: Coincident(g31,g16)
    c: Distance(g32) = 3.6
    c: Block(g32)
    c: Coincident(g33,g32)
    c: Coincident(g34,g8)
    c: Weight(g35) = 1
    c: Equal(g35, g36-g53) x18
    c: InternalAlignment(g35-g53 -> g54) x19
    c: InternalAlignment(g55-g71 -> g54) x17
    c: Block(g33)
    c: Block(g54)
    c: Coincident(g72,g33)
    c: Coincident(g73,g34)
    c: Block(g34)
    c: Parallel(g72,g34)
    c: Perpendicular(g73,g34)
    c: Coincident(g72,g73)
    c: Coincident(g74,g54)
    c: Coincident(g74,g23)
    c: Coincident(g75,g54)
    c: Coincident(g75,g32)
FEATURE [Sketcher::SketchObject] Sketch011  label="legBottomFront"
  FullyConstrained = true
  MapMode = 4
  Placement = pos=(0,0,0) rot=(0.57735,0.57735,0.57735;2.0944rad)
  sketch-geometry (13):
    g0: LineSegment StartX=-199.665 StartY=-138.314 StartZ=0 EndX=-200.721 EndY=-141.122 EndZ=0
    g1: LineSegment StartX=-200.721 StartY=-141.122 StartZ=0 EndX=-79.0409 EndY=-186.881 EndZ=0
    g2: ArcOfCircle CenterX=-71.1257 CenterY=-183.448 CenterZ=0 NormalX=0 NormalY=0 NormalZ=1 AngleXU=0 Radius=3.28025 StartAngle=3.43759 EndAngle=8.40938
    g3: LineSegment StartX=-74.4626 StartY=-174.707 StartZ=0 EndX=-76.2249 EndY=-179.393 EndZ=0
    g4: LineSegment StartX=-76.2249 StartY=-179.393 StartZ=0 EndX=-72.8553 EndY=-180.66 EndZ=0
    g5: Circle CenterX=-74.4626 CenterY=-174.707 CenterZ=0 NormalX=0 NormalY=0 NormalZ=1 AngleXU=0 Radius=1
    g6: Circle CenterX=-130.185 CenterY=-164.454 CenterZ=0 NormalX=0 NormalY=0 NormalZ=1 AngleXU=0 Radius=1
    g7: Circle CenterX=-199.665 CenterY=-138.314 CenterZ=0 NormalX=0 NormalY=0 NormalZ=1 AngleXU=0 Radius=1
    g8: BSplineCurve PolesCount=3 KnotsCount=2 Degree=2 IsPeriodic=0
    g9: GeomPoint X=-74.4626 Y=-174.707 Z=0
    g10: GeomPoint X=-199.665 Y=-138.314 Z=0
    g11: LineSegment StartX=-77.6329 StartY=-183.137 StartZ=0 EndX=-79.0409 EndY=-186.881 EndZ=0
    g12: LineSegment StartX=-77.6329 StartY=-183.137 StartZ=0 EndX=-74.2633 EndY=-184.404 EndZ=0
  constraints (24):
    c: Coincident(g1,g0)
    c: Block(g0)
    c: Perpendicular(g1,g0)
    c: Distance(g1) = 130
    c: Coincident(g4,g3)
    c: Coincident(g4,g2)
    c: Block(g2)
    c: Block(g4)
    c: Coincident(g8,g3)
    c: Weight(g5) = 1
    c: Equal(g5,g6)
    c: Equal(g5,g7)
    c: Coincident(g8,g0)
    c: InternalAlignment(g5,g8)
    c: InternalAlignment(g6,g8)
    c: InternalAlignment(g7,g8)
    c: InternalAlignment(g9,g8)
    c: InternalAlignment(g10,g8)
    c: Block(g8)
    c: Block(g3)
    c: Coincident(g11,g1)
    c: Coincident(g12,g11)
    c: Coincident(g12,g2)
    c: Block(g12)
FEATURE [Sketcher::SketchObject] Sketch
  FullyConstrained = true
  Placement = pos=(0,0,0) rot=(1,0,0;1.5708rad)
  sketch-geometry (15):
    g0: LineSegment StartX=19.9194 StartY=-115.939 StartZ=0 EndX=24.9194 EndY=-115.939 EndZ=0
    g1: LineSegment StartX=79.9194 StartY=-5.9387 StartZ=0 EndX=79.9194 EndY=-10.9387 EndZ=0
    g2: Circle CenterX=79.9194 CenterY=-10.9387 CenterZ=0 NormalX=0 NormalY=0 NormalZ=1 AngleXU=0 Radius=1
    g3: Circle CenterX=24.9194 CenterY=-10.9387 CenterZ=0 NormalX=0 NormalY=0 NormalZ=1 AngleXU=0 Radius=1
    g4: Circle CenterX=24.9194 CenterY=-115.939 CenterZ=0 NormalX=0 NormalY=0 NormalZ=1 AngleXU=0 Radius=1
    g5: BSplineCurve PolesCount=3 KnotsCount=2 Degree=2 IsPeriodic=0
    g6: GeomPoint X=79.9194 Y=-10.9387 Z=0
    g7: GeomPoint X=24.9194 Y=-115.939 Z=0
    g8: LineSegment StartX=19.9194 StartY=-5.9387 StartZ=0 EndX=19.9194 EndY=-115.939 EndZ=0
    g9: Circle CenterX=33.6194 CenterY=-19.6387 CenterZ=0 NormalX=0 NormalY=0 NormalZ=1 AngleXU=0 Radius=8.7
    g10: Circle CenterX=28.8194 CenterY=-36.6387 CenterZ=0 NormalX=0 NormalY=0 NormalZ=1 AngleXU=0 Radius=3.9
    g11: Circle CenterX=48.6194 CenterY=-13.5387 CenterZ=0 NormalX=0 NormalY=0 NormalZ=1 AngleXU=0 Radius=2.6
    g12: LineSegment StartX=79.9194 StartY=-5.9387 StartZ=0 EndX=79.9194 EndY=-1.9387 EndZ=0
    g13: LineSegment StartX=19.9194 StartY=-5.9387 StartZ=0 EndX=19.9194 EndY=-1.9387 EndZ=0
    g14: LineSegment StartX=79.9194 StartY=-1.9387 StartZ=0 EndX=19.9194 EndY=-1.9387 EndZ=0
  constraints (30):
    c: Horizontal(g0)
    c: Distance(g0) = 5
    c: Vertical(g1)
    c: Distance(g1) = 5
    c: Coincident(g5,g1)
    c: Weight(g2) = 1
    c: Equal(g2,g3)
    c: Equal(g2,g4)
    c: Coincident(g5,g0)
    c: InternalAlignment(g2,g5)
    c: InternalAlignment(g3,g5)
    c: InternalAlignment(g4,g5)
    c: InternalAlignment(g6,g5)
    c: InternalAlignment(g7,g5)
    c: Coincident(g8,g0)
    c: Vertical(g8)
    c: Block(g3)
    c: Block(g9)
    c: Block(g5)
    c: Block(g10)
    c: Block(g11)
    c: Vertical(g12)
    c: Distance(g12) = 4
    c: Coincident(g13,g8)
    c: Vertical(g13)
    c: Distance(g13) = 4
    c: Coincident(g14,g12)
    c: Horizontal(g14)
    c: Block(g12)
    c: Coincident(g14,g13)
FEATURE [Part::Extrusion] Extrude  label="legBrace"
  Base = -> Sketch
  Dir = (0,-1,3e-16)
  DirMode = 2
  FaceMakerClass = Part::FaceMakerBullseye
  LengthFwd = 8
  LengthRev = 0
  Placement = pos=(-47.92,80.9,3.4) rot=(-1,0,0;0.361109rad)
  Solid = true
  Symmetric = false
FEATURE [Part::Extrusion] Extrude004
  Base = -> Sketch011
  Dir = (1,0,0)
  DirMode = 2
  FaceMakerClass = Part::FaceMakerBullseye
  LengthFwd = 12
  LengthRev = 0
  Solid = true
  Symmetric = false
FEATURE [Part::Extrusion] Extrude005
  Base = -> Sketch010
  Dir = (1,0,0)
  DirMode = 2
  FaceMakerClass = Part::FaceMakerBullseye
  LengthFwd = 12
  LengthRev = 0
  Placement = pos=(-40,11,16) rot=(0,0,1;0rad)
  Solid = true
  Symmetric = false
FEATURE [Part::Extrusion] Extrude006  label="topLegLeft"
  Base = -> Sketch001
  Dir = (1,0,0)
  DirMode = 2
  FaceMakerClass = Part::FaceMakerBullseye
  LengthFwd = 12
  LengthRev = 0
  Placement = pos=(-40,11,16) rot=(0,0,1;0rad)
  Solid = true
  Symmetric = false
FEATURE [Part::Extrusion] Extrude007
  Base = -> Sketch006
  Dir = (0,0,1)
  DirMode = 2
  FaceMakerClass = Part::FaceMakerBullseye
  LengthFwd = 28
  LengthRev = 0
  Solid = true
  Symmetric = false
FEATURE [Part::Extrusion] Extrude008
  Base = -> Sketch005
  Dir = (0,0,1)
  DirMode = 2
  FaceMakerClass = Part::FaceMakerBullseye
  LengthFwd = 28
  LengthRev = 0
  Solid = true
  Symmetric = false
FEATURE [Part::Extrusion] Extrude009
  Base = -> Sketch008
  Dir = (0,0,1)
  DirMode = 2
  FaceMakerClass = Part::FaceMakerBullseye
  LengthFwd = 28
  LengthRev = 0
  Solid = true
  Symmetric = false
FEATURE [Part::Extrusion] Extrude010
  Base = -> Sketch007
  Dir = (0,0,1)
  DirMode = 2
  FaceMakerClass = Part::FaceMakerBullseye
  LengthFwd = 28
  LengthRev = 0
  Solid = true
  Symmetric = false
FEATURE [Part::Extrusion] Extrude011
  Base = -> Sketch009
  Dir = (0,0,1)
  DirMode = 2
  FaceMakerClass = Part::FaceMakerBullseye
  LengthFwd = 28
  LengthRev = 0
  Solid = true
  Symmetric = false
FEATURE [Part::Extrusion] Extrude012
  Base = -> Sketch004
  Dir = (0,0,1)
  DirMode = 2
  FaceMakerClass = Part::FaceMakerBullseye
  LengthFwd = 28
  LengthRev = 0
  Solid = true
  Symmetric = false
FEATURE [Sketcher::SketchObject] Sketch012
  FullyConstrained = true
  Placement = pos=(0,0,0) rot=(1,0,0;1.5708rad)
  sketch-geometry (15):
    g0: LineSegment StartX=19.9194 StartY=-115.939 StartZ=0 EndX=24.9194 EndY=-115.939 EndZ=0
    g1: LineSegment StartX=79.9194 StartY=-5.9387 StartZ=0 EndX=79.9194 EndY=-10.9387 EndZ=0
    g2: Circle CenterX=79.9194 CenterY=-10.9387 CenterZ=0 NormalX=0 NormalY=0 NormalZ=1 AngleXU=0 Radius=1
    g3: Circle CenterX=24.9194 CenterY=-10.9387 CenterZ=0 NormalX=0 NormalY=0 NormalZ=1 AngleXU=0 Radius=1
    g4: Circle CenterX=24.9194 CenterY=-115.939 CenterZ=0 NormalX=0 NormalY=0 NormalZ=1 AngleXU=0 Radius=1
    g5: BSplineCurve PolesCount=3 KnotsCount=2 Degree=2 IsPeriodic=0
    g6: GeomPoint X=79.9194 Y=-10.9387 Z=0
    g7: GeomPoint X=24.9194 Y=-115.939 Z=0
    g8: LineSegment StartX=19.9194 StartY=-5.9387 StartZ=0 EndX=19.9194 EndY=-115.939 EndZ=0
    g9: Circle CenterX=33.6194 CenterY=-19.6387 CenterZ=0 NormalX=0 NormalY=0 NormalZ=1 AngleXU=0 Radius=8.7
    g10: Circle CenterX=28.8194 CenterY=-36.6387 CenterZ=0 NormalX=0 NormalY=0 NormalZ=1 AngleXU=0 Radius=3.9
    g11: Circle CenterX=48.6194 CenterY=-13.5387 CenterZ=0 NormalX=0 NormalY=0 NormalZ=1 AngleXU=0 Radius=2.6
    g12: LineSegment StartX=79.9194 StartY=-5.9387 StartZ=0 EndX=79.9194 EndY=-1.9387 EndZ=0
    g13: LineSegment StartX=19.9194 StartY=-5.9387 StartZ=0 EndX=19.9194 EndY=-1.9387 EndZ=0
    g14: LineSegment StartX=79.9194 StartY=-1.9387 StartZ=0 EndX=19.9194 EndY=-1.9387 EndZ=0
  constraints (30):
    c: Horizontal(g0)
    c: Distance(g0) = 5
    c: Vertical(g1)
    c: Distance(g1) = 5
    c: Coincident(g5,g1)
    c: Weight(g2) = 1
    c: Equal(g2,g3)
    c: Equal(g2,g4)
    c: Coincident(g5,g0)
    c: InternalAlignment(g2,g5)
    c: InternalAlignment(g3,g5)
    c: InternalAlignment(g4,g5)
    c: InternalAlignment(g6,g5)
    c: InternalAlignment(g7,g5)
    c: Coincident(g8,g0)
    c: Vertical(g8)
    c: Block(g3)
    c: Block(g9)
    c: Block(g5)
    c: Block(g10)
    c: Block(g11)
    c: Vertical(g12)
    c: Distance(g12) = 4
    c: Coincident(g13,g8)
    c: Vertical(g13)
    c: Distance(g13) = 4
    c: Coincident(g14,g12)
    c: Horizontal(g14)
    c: Block(g12)
    c: Coincident(g14,g13)
FEATURE [Part::Extrusion] Extrude013  label="legBrace001"
  Base = -> Sketch012
  Dir = (0,-1,3e-16)
  DirMode = 2
  FaceMakerClass = Part::FaceMakerBullseye
  LengthFwd = 8
  LengthRev = 0
  Placement = pos=(-47.92,111.4,3.4) rot=(-1,0,0;0.361109rad)
  Solid = true
  Symmetric = false
FEATURE [Sketcher::SketchObject] Sketch013
  FullyConstrained = true
  Placement = pos=(0,0,0) rot=(1,0,0;1.5708rad)
  sketch-geometry (15):
    g0: LineSegment StartX=19.9194 StartY=-115.939 StartZ=0 EndX=24.9194 EndY=-115.939 EndZ=0
    g1: LineSegment StartX=79.9194 StartY=-5.9387 StartZ=0 EndX=79.9194 EndY=-10.9387 EndZ=0
    g2: Circle CenterX=79.9194 CenterY=-10.9387 CenterZ=0 NormalX=0 NormalY=0 NormalZ=1 AngleXU=0 Radius=1
    g3: Circle CenterX=24.9194 CenterY=-10.9387 CenterZ=0 NormalX=0 NormalY=0 NormalZ=1 AngleXU=0 Radius=1
    g4: Circle CenterX=24.9194 CenterY=-115.939 CenterZ=0 NormalX=0 NormalY=0 NormalZ=1 AngleXU=0 Radius=1
    g5: BSplineCurve PolesCount=3 KnotsCount=2 Degree=2 IsPeriodic=0
    g6: GeomPoint X=79.9194 Y=-10.9387 Z=0
    g7: GeomPoint X=24.9194 Y=-115.939 Z=0
    g8: LineSegment StartX=19.9194 StartY=-5.9387 StartZ=0 EndX=19.9194 EndY=-115.939 EndZ=0
    g9: Circle CenterX=33.6194 CenterY=-19.6387 CenterZ=0 NormalX=0 NormalY=0 NormalZ=1 AngleXU=0 Radius=8.7
    g10: Circle CenterX=28.8194 CenterY=-36.6387 CenterZ=0 NormalX=0 NormalY=0 NormalZ=1 AngleXU=0 Radius=3.9
    g11: Circle CenterX=48.6194 CenterY=-13.5387 CenterZ=0 NormalX=0 NormalY=0 NormalZ=1 AngleXU=0 Radius=2.6
    g12: LineSegment StartX=79.9194 StartY=-5.9387 StartZ=0 EndX=79.9194 EndY=-1.9387 EndZ=0
    g13: LineSegment StartX=19.9194 StartY=-5.9387 StartZ=0 EndX=19.9194 EndY=-1.9387 EndZ=0
    g14: LineSegment StartX=79.9194 StartY=-1.9387 StartZ=0 EndX=19.9194 EndY=-1.9387 EndZ=0
  constraints (30):
    c: Horizontal(g0)
    c: Distance(g0) = 5
    c: Vertical(g1)
    c: Distance(g1) = 5
    c: Coincident(g5,g1)
    c: Weight(g2) = 1
    c: Equal(g2,g3)
    c: Equal(g2,g4)
    c: Coincident(g5,g0)
    c: InternalAlignment(g2,g5)
    c: InternalAlignment(g3,g5)
    c: InternalAlignment(g4,g5)
    c: InternalAlignment(g6,g5)
    c: InternalAlignment(g7,g5)
    c: Coincident(g8,g0)
    c: Vertical(g8)
    c: Block(g3)
    c: Block(g9)
    c: Block(g5)
    c: Block(g10)
    c: Block(g11)
    c: Vertical(g12)
    c: Distance(g12) = 4
    c: Coincident(g13,g8)
    c: Vertical(g13)
    c: Distance(g13) = 4
    c: Coincident(g14,g12)
    c: Horizontal(g14)
    c: Block(g12)
    c: Coincident(g14,g13)
FEATURE [Sketcher::SketchObject] Sketch014
  FullyConstrained = true
  Placement = pos=(0,0,0) rot=(1,0,0;1.5708rad)
  sketch-geometry (15):
    g0: LineSegment StartX=19.9194 StartY=-115.939 StartZ=0 EndX=24.9194 EndY=-115.939 EndZ=0
    g1: LineSegment StartX=79.9194 StartY=-5.9387 StartZ=0 EndX=79.9194 EndY=-10.9387 EndZ=0
    g2: Circle CenterX=79.9194 CenterY=-10.9387 CenterZ=0 NormalX=0 NormalY=0 NormalZ=1 AngleXU=0 Radius=1
    g3: Circle CenterX=24.9194 CenterY=-10.9387 CenterZ=0 NormalX=0 NormalY=0 NormalZ=1 AngleXU=0 Radius=1
    g4: Circle CenterX=24.9194 CenterY=-115.939 CenterZ=0 NormalX=0 NormalY=0 NormalZ=1 AngleXU=0 Radius=1
    g5: BSplineCurve PolesCount=3 KnotsCount=2 Degree=2 IsPeriodic=0
    g6: GeomPoint X=79.9194 Y=-10.9387 Z=0
    g7: GeomPoint X=24.9194 Y=-115.939 Z=0
    g8: LineSegment StartX=19.9194 StartY=-5.9387 StartZ=0 EndX=19.9194 EndY=-115.939 EndZ=0
    g9: Circle CenterX=33.6194 CenterY=-19.6387 CenterZ=0 NormalX=0 NormalY=0 NormalZ=1 AngleXU=0 Radius=8.7
    g10: Circle CenterX=28.8194 CenterY=-36.6387 CenterZ=0 NormalX=0 NormalY=0 NormalZ=1 AngleXU=0 Radius=3.9
    g11: Circle CenterX=48.6194 CenterY=-13.5387 CenterZ=0 NormalX=0 NormalY=0 NormalZ=1 AngleXU=0 Radius=2.6
    g12: LineSegment StartX=79.9194 StartY=-5.9387 StartZ=0 EndX=79.9194 EndY=-1.9387 EndZ=0
    g13: LineSegment StartX=19.9194 StartY=-5.9387 StartZ=0 EndX=19.9194 EndY=-1.9387 EndZ=0
    g14: LineSegment StartX=79.9194 StartY=-1.9387 StartZ=0 EndX=19.9194 EndY=-1.9387 EndZ=0
  constraints (30):
    c: Horizontal(g0)
    c: Distance(g0) = 5
    c: Vertical(g1)
    c: Distance(g1) = 5
    c: Coincident(g5,g1)
    c: Weight(g2) = 1
    c: Equal(g2,g3)
    c: Equal(g2,g4)
    c: Coincident(g5,g0)
    c: InternalAlignment(g2,g5)
    c: InternalAlignment(g3,g5)
    c: InternalAlignment(g4,g5)
    c: InternalAlignment(g6,g5)
    c: InternalAlignment(g7,g5)
    c: Coincident(g8,g0)
    c: Vertical(g8)
    c: Block(g3)
    c: Block(g9)
    c: Block(g5)
    c: Block(g10)
    c: Block(g11)
    c: Vertical(g12)
    c: Distance(g12) = 4
    c: Coincident(g13,g8)
    c: Vertical(g13)
    c: Distance(g13) = 4
    c: Coincident(g14,g12)
    c: Horizontal(g14)
    c: Block(g12)
    c: Coincident(g14,g13)
FEATURE [Part::Extrusion] Extrude015  label="legBrace003"
  Base = -> Sketch014
  Dir = (0,-1,3e-16)
  DirMode = 2
  FaceMakerClass = Part::FaceMakerBullseye
  LengthFwd = 8
  LengthRev = 0
  Placement = pos=(100,110.16,3.4) rot=(-1,0,0;0rad)
  Solid = true
  Symmetric = false
FEATURE [Part::Extrusion] Extrude014  label="legBrace002"
  Base = -> Sketch013
  Dir = (0,-1,2e-16)
  DirMode = 2
  FaceMakerClass = Part::FaceMakerBullseye
  LengthFwd = 8
  LengthRev = 0
  Placement = pos=(100,110.16,3.4) rot=(-1,0,0;0rad)
  Solid = true
  Symmetric = false
FEATURE [Part::Fuse] Fusion  label="legBraceRight01"
  Base = -> Extrude014
  Placement = pos=(0,0,0) rot=(0,0,1;3.14159rad)
  Tool = -> Extrude015
FEATURE [Sketcher::SketchObject] Sketch015
  FullyConstrained = true
  Placement = pos=(0,0,0) rot=(1,0,0;1.5708rad)
  sketch-geometry (15):
    g0: LineSegment StartX=19.9194 StartY=-115.939 StartZ=0 EndX=24.9194 EndY=-115.939 EndZ=0
    g1: LineSegment StartX=79.9194 StartY=-5.9387 StartZ=0 EndX=79.9194 EndY=-10.9387 EndZ=0
    g2: Circle CenterX=79.9194 CenterY=-10.9387 CenterZ=0 NormalX=0 NormalY=0 NormalZ=1 AngleXU=0 Radius=1
    g3: Circle CenterX=24.9194 CenterY=-10.9387 CenterZ=0 NormalX=0 NormalY=0 NormalZ=1 AngleXU=0 Radius=1
    g4: Circle CenterX=24.9194 CenterY=-115.939 CenterZ=0 NormalX=0 NormalY=0 NormalZ=1 AngleXU=0 Radius=1
    g5: BSplineCurve PolesCount=3 KnotsCount=2 Degree=2 IsPeriodic=0
    g6: GeomPoint X=79.9194 Y=-10.9387 Z=0
    g7: GeomPoint X=24.9194 Y=-115.939 Z=0
    g8: LineSegment StartX=19.9194 StartY=-5.9387 StartZ=0 EndX=19.9194 EndY=-115.939 EndZ=0
    g9: Circle CenterX=33.6194 CenterY=-19.6387 CenterZ=0 NormalX=0 NormalY=0 NormalZ=1 AngleXU=0 Radius=8.7
    g10: Circle CenterX=28.8194 CenterY=-36.6387 CenterZ=0 NormalX=0 NormalY=0 NormalZ=1 AngleXU=0 Radius=3.9
    g11: Circle CenterX=48.6194 CenterY=-13.5387 CenterZ=0 NormalX=0 NormalY=0 NormalZ=1 AngleXU=0 Radius=2.6
    g12: LineSegment StartX=79.9194 StartY=-5.9387 StartZ=0 EndX=79.9194 EndY=-1.9387 EndZ=0
    g13: LineSegment StartX=19.9194 StartY=-5.9387 StartZ=0 EndX=19.9194 EndY=-1.9387 EndZ=0
    g14: LineSegment StartX=79.9194 StartY=-1.9387 StartZ=0 EndX=19.9194 EndY=-1.9387 EndZ=0
  constraints (30):
    c: Horizontal(g0)
    c: Distance(g0) = 5
    c: Vertical(g1)
    c: Distance(g1) = 5
    c: Coincident(g5,g1)
    c: Weight(g2) = 1
    c: Equal(g2,g3)
    c: Equal(g2,g4)
    c: Coincident(g5,g0)
    c: InternalAlignment(g2,g5)
    c: InternalAlignment(g3,g5)
    c: InternalAlignment(g4,g5)
    c: InternalAlignment(g6,g5)
    c: InternalAlignment(g7,g5)
    c: Coincident(g8,g0)
    c: Vertical(g8)
    c: Block(g3)
    c: Block(g9)
    c: Block(g5)
    c: Block(g10)
    c: Block(g11)
    c: Vertical(g12)
    c: Distance(g12) = 4
    c: Coincident(g13,g8)
    c: Vertical(g13)
    c: Distance(g13) = 4
    c: Coincident(g14,g12)
    c: Horizontal(g14)
    c: Block(g12)
    c: Coincident(g14,g13)
FEATURE [Part::Extrusion] Extrude016  label="legBrace004"
  Base = -> Sketch015
  Dir = (0,-1,2e-16)
  DirMode = 2
  FaceMakerClass = Part::FaceMakerBullseye
  LengthFwd = 8
  LengthRev = 0
  Placement = pos=(100,110.16,3.4) rot=(-1,0,0;0rad)
  Solid = true
  Symmetric = false
FEATURE [Sketcher::SketchObject] Sketch016
  FullyConstrained = true
  Placement = pos=(0,0,0) rot=(1,0,0;1.5708rad)
  sketch-geometry (15):
    g0: LineSegment StartX=19.9194 StartY=-115.939 StartZ=0 EndX=24.9194 EndY=-115.939 EndZ=0
    g1: LineSegment StartX=79.9194 StartY=-5.9387 StartZ=0 EndX=79.9194 EndY=-10.9387 EndZ=0
    g2: Circle CenterX=79.9194 CenterY=-10.9387 CenterZ=0 NormalX=0 NormalY=0 NormalZ=1 AngleXU=0 Radius=1
    g3: Circle CenterX=24.9194 CenterY=-10.9387 CenterZ=0 NormalX=0 NormalY=0 NormalZ=1 AngleXU=0 Radius=1
    g4: Circle CenterX=24.9194 CenterY=-115.939 CenterZ=0 NormalX=0 NormalY=0 NormalZ=1 AngleXU=0 Radius=1
    g5: BSplineCurve PolesCount=3 KnotsCount=2 Degree=2 IsPeriodic=0
    g6: GeomPoint X=79.9194 Y=-10.9387 Z=0
    g7: GeomPoint X=24.9194 Y=-115.939 Z=0
    g8: LineSegment StartX=19.9194 StartY=-5.9387 StartZ=0 EndX=19.9194 EndY=-115.939 EndZ=0
    g9: Circle CenterX=33.6194 CenterY=-19.6387 CenterZ=0 NormalX=0 NormalY=0 NormalZ=1 AngleXU=0 Radius=8.7
    g10: Circle CenterX=28.8194 CenterY=-36.6387 CenterZ=0 NormalX=0 NormalY=0 NormalZ=1 AngleXU=0 Radius=3.9
    g11: Circle CenterX=48.6194 CenterY=-13.5387 CenterZ=0 NormalX=0 NormalY=0 NormalZ=1 AngleXU=0 Radius=2.6
    g12: LineSegment StartX=79.9194 StartY=-5.9387 StartZ=0 EndX=79.9194 EndY=-1.9387 EndZ=0
    g13: LineSegment StartX=19.9194 StartY=-5.9387 StartZ=0 EndX=19.9194 EndY=-1.9387 EndZ=0
    g14: LineSegment StartX=79.9194 StartY=-1.9387 StartZ=0 EndX=19.9194 EndY=-1.9387 EndZ=0
  constraints (30):
    c: Horizontal(g0)
    c: Distance(g0) = 5
    c: Vertical(g1)
    c: Distance(g1) = 5
    c: Coincident(g5,g1)
    c: Weight(g2) = 1
    c: Equal(g2,g3)
    c: Equal(g2,g4)
    c: Coincident(g5,g0)
    c: InternalAlignment(g2,g5)
    c: InternalAlignment(g3,g5)
    c: InternalAlignment(g4,g5)
    c: InternalAlignment(g6,g5)
    c: InternalAlignment(g7,g5)
    c: Coincident(g8,g0)
    c: Vertical(g8)
    c: Block(g3)
    c: Block(g9)
    c: Block(g5)
    c: Block(g10)
    c: Block(g11)
    c: Vertical(g12)
    c: Distance(g12) = 4
    c: Coincident(g13,g8)
    c: Vertical(g13)
    c: Distance(g13) = 4
    c: Coincident(g14,g12)
    c: Horizontal(g14)
    c: Block(g12)
    c: Coincident(g14,g13)
FEATURE [Part::Extrusion] Extrude017  label="legBrace005"
  Base = -> Sketch016
  Dir = (0,-1,2e-16)
  DirMode = 2
  FaceMakerClass = Part::FaceMakerBullseye
  LengthFwd = 8
  LengthRev = 0
  Placement = pos=(100,110.16,3.4) rot=(-1,0,0;0rad)
  Solid = true
  Symmetric = false
FEATURE [Part::Fuse] Fusion001  label="legBraceRight002"
  Base = -> Extrude016
  Placement = pos=(0,0,0) rot=(0,0,1;3.14159rad)
  Tool = -> Extrude017
FEATURE [Part::Fuse] Fusion002  label="rightLeftBrace002"
  Base = -> Fusion
  Placement = pos=(512.26,205.15,-35.87) rot=(-1,0,0;0.361109rad)
  Tool = -> Fusion001
FEATURE [Sketcher::SketchObject] Sketch017
  FullyConstrained = true
  Placement = pos=(0,0,0) rot=(1,0,0;1.5708rad)
  sketch-geometry (15):
    g0: LineSegment StartX=19.9194 StartY=-115.939 StartZ=0 EndX=24.9194 EndY=-115.939 EndZ=0
    g1: LineSegment StartX=79.9194 StartY=-5.9387 StartZ=0 EndX=79.9194 EndY=-10.9387 EndZ=0
    g2: Circle CenterX=79.9194 CenterY=-10.9387 CenterZ=0 NormalX=0 NormalY=0 NormalZ=1 AngleXU=0 Radius=1
    g3: Circle CenterX=24.9194 CenterY=-10.9387 CenterZ=0 NormalX=0 NormalY=0 NormalZ=1 AngleXU=0 Radius=1
    g4: Circle CenterX=24.9194 CenterY=-115.939 CenterZ=0 NormalX=0 NormalY=0 NormalZ=1 AngleXU=0 Radius=1
    g5: BSplineCurve PolesCount=3 KnotsCount=2 Degree=2 IsPeriodic=0
    g6: GeomPoint X=79.9194 Y=-10.9387 Z=0
    g7: GeomPoint X=24.9194 Y=-115.939 Z=0
    g8: LineSegment StartX=19.9194 StartY=-5.9387 StartZ=0 EndX=19.9194 EndY=-115.939 EndZ=0
    g9: Circle CenterX=33.6194 CenterY=-19.6387 CenterZ=0 NormalX=0 NormalY=0 NormalZ=1 AngleXU=0 Radius=8.7
    g10: Circle CenterX=28.8194 CenterY=-36.6387 CenterZ=0 NormalX=0 NormalY=0 NormalZ=1 AngleXU=0 Radius=3.9
    g11: Circle CenterX=48.6194 CenterY=-13.5387 CenterZ=0 NormalX=0 NormalY=0 NormalZ=1 AngleXU=0 Radius=2.6
    g12: LineSegment StartX=79.9194 StartY=-5.9387 StartZ=0 EndX=79.9194 EndY=-1.9387 EndZ=0
    g13: LineSegment StartX=19.9194 StartY=-5.9387 StartZ=0 EndX=19.9194 EndY=-1.9387 EndZ=0
    g14: LineSegment StartX=79.9194 StartY=-1.9387 StartZ=0 EndX=19.9194 EndY=-1.9387 EndZ=0
  constraints (30):
    c: Horizontal(g0)
    c: Distance(g0) = 5
    c: Vertical(g1)
    c: Distance(g1) = 5
    c: Coincident(g5,g1)
    c: Weight(g2) = 1
    c: Equal(g2,g3)
    c: Equal(g2,g4)
    c: Coincident(g5,g0)
    c: InternalAlignment(g2,g5)
    c: InternalAlignment(g3,g5)
    c: InternalAlignment(g4,g5)
    c: InternalAlignment(g6,g5)
    c: InternalAlignment(g7,g5)
    c: Coincident(g8,g0)
    c: Vertical(g8)
    c: Block(g3)
    c: Block(g9)
    c: Block(g5)
    c: Block(g10)
    c: Block(g11)
    c: Vertical(g12)
    c: Distance(g12) = 4
    c: Coincident(g13,g8)
    c: Vertical(g13)
    c: Distance(g13) = 4
    c: Coincident(g14,g12)
    c: Horizontal(g14)
    c: Block(g12)
    c: Coincident(g14,g13)
FEATURE [Part::Extrusion] Extrude018  label="legBrace006"
  Base = -> Sketch017
  Dir = (0,-1,2e-16)
  DirMode = 2
  FaceMakerClass = Part::FaceMakerBullseye
  LengthFwd = 8
  LengthRev = 0
  Placement = pos=(100,110.16,3.4) rot=(-1,0,0;0rad)
  Solid = true
  Symmetric = false
FEATURE [Sketcher::SketchObject] Sketch018
  FullyConstrained = true
  Placement = pos=(0,0,0) rot=(1,0,0;1.5708rad)
  sketch-geometry (15):
    g0: LineSegment StartX=19.9194 StartY=-115.939 StartZ=0 EndX=24.9194 EndY=-115.939 EndZ=0
    g1: LineSegment StartX=79.9194 StartY=-5.9387 StartZ=0 EndX=79.9194 EndY=-10.9387 EndZ=0
    g2: Circle CenterX=79.9194 CenterY=-10.9387 CenterZ=0 NormalX=0 NormalY=0 NormalZ=1 AngleXU=0 Radius=1
    g3: Circle CenterX=24.9194 CenterY=-10.9387 CenterZ=0 NormalX=0 NormalY=0 NormalZ=1 AngleXU=0 Radius=1
    g4: Circle CenterX=24.9194 CenterY=-115.939 CenterZ=0 NormalX=0 NormalY=0 NormalZ=1 AngleXU=0 Radius=1
    g5: BSplineCurve PolesCount=3 KnotsCount=2 Degree=2 IsPeriodic=0
    g6: GeomPoint X=79.9194 Y=-10.9387 Z=0
    g7: GeomPoint X=24.9194 Y=-115.939 Z=0
    g8: LineSegment StartX=19.9194 StartY=-5.9387 StartZ=0 EndX=19.9194 EndY=-115.939 EndZ=0
    g9: Circle CenterX=33.6194 CenterY=-19.6387 CenterZ=0 NormalX=0 NormalY=0 NormalZ=1 AngleXU=0 Radius=8.7
    g10: Circle CenterX=28.8194 CenterY=-36.6387 CenterZ=0 NormalX=0 NormalY=0 NormalZ=1 AngleXU=0 Radius=3.9
    g11: Circle CenterX=48.6194 CenterY=-13.5387 CenterZ=0 NormalX=0 NormalY=0 NormalZ=1 AngleXU=0 Radius=2.6
    g12: LineSegment StartX=79.9194 StartY=-5.9387 StartZ=0 EndX=79.9194 EndY=-1.9387 EndZ=0
    g13: LineSegment StartX=19.9194 StartY=-5.9387 StartZ=0 EndX=19.9194 EndY=-1.9387 EndZ=0
    g14: LineSegment StartX=79.9194 StartY=-1.9387 StartZ=0 EndX=19.9194 EndY=-1.9387 EndZ=0
  constraints (30):
    c: Horizontal(g0)
    c: Distance(g0) = 5
    c: Vertical(g1)
    c: Distance(g1) = 5
    c: Coincident(g5,g1)
    c: Weight(g2) = 1
    c: Equal(g2,g3)
    c: Equal(g2,g4)
    c: Coincident(g5,g0)
    c: InternalAlignment(g2,g5)
    c: InternalAlignment(g3,g5)
    c: InternalAlignment(g4,g5)
    c: InternalAlignment(g6,g5)
    c: InternalAlignment(g7,g5)
    c: Coincident(g8,g0)
    c: Vertical(g8)
    c: Block(g3)
    c: Block(g9)
    c: Block(g5)
    c: Block(g10)
    c: Block(g11)
    c: Vertical(g12)
    c: Distance(g12) = 4
    c: Coincident(g13,g8)
    c: Vertical(g13)
    c: Distance(g13) = 4
    c: Coincident(g14,g12)
    c: Horizontal(g14)
    c: Block(g12)
    c: Coincident(g14,g13)
FEATURE [Part::Extrusion] Extrude019  label="legBrace007"
  Base = -> Sketch018
  Dir = (0,-1,3e-16)
  DirMode = 2
  FaceMakerClass = Part::FaceMakerBullseye
  LengthFwd = 8
  LengthRev = 0
  Placement = pos=(100,110.16,3.4) rot=(-1,0,0;0rad)
  Solid = true
  Symmetric = false
FEATURE [Sketcher::SketchObject] Sketch019
  FullyConstrained = true
  Placement = pos=(0,0,0) rot=(1,0,0;1.5708rad)
  sketch-geometry (15):
    g0: LineSegment StartX=19.9194 StartY=-115.939 StartZ=0 EndX=24.9194 EndY=-115.939 EndZ=0
    g1: LineSegment StartX=79.9194 StartY=-5.9387 StartZ=0 EndX=79.9194 EndY=-10.9387 EndZ=0
    g2: Circle CenterX=79.9194 CenterY=-10.9387 CenterZ=0 NormalX=0 NormalY=0 NormalZ=1 AngleXU=0 Radius=1
    g3: Circle CenterX=24.9194 CenterY=-10.9387 CenterZ=0 NormalX=0 NormalY=0 NormalZ=1 AngleXU=0 Radius=1
    g4: Circle CenterX=24.9194 CenterY=-115.939 CenterZ=0 NormalX=0 NormalY=0 NormalZ=1 AngleXU=0 Radius=1
    g5: BSplineCurve PolesCount=3 KnotsCount=2 Degree=2 IsPeriodic=0
    g6: GeomPoint X=79.9194 Y=-10.9387 Z=0
    g7: GeomPoint X=24.9194 Y=-115.939 Z=0
    g8: LineSegment StartX=19.9194 StartY=-5.9387 StartZ=0 EndX=19.9194 EndY=-115.939 EndZ=0
    g9: Circle CenterX=33.6194 CenterY=-19.6387 CenterZ=0 NormalX=0 NormalY=0 NormalZ=1 AngleXU=0 Radius=8.7
    g10: Circle CenterX=28.8194 CenterY=-36.6387 CenterZ=0 NormalX=0 NormalY=0 NormalZ=1 AngleXU=0 Radius=3.9
    g11: Circle CenterX=48.6194 CenterY=-13.5387 CenterZ=0 NormalX=0 NormalY=0 NormalZ=1 AngleXU=0 Radius=2.6
    g12: LineSegment StartX=79.9194 StartY=-5.9387 StartZ=0 EndX=79.9194 EndY=-1.9387 EndZ=0
    g13: LineSegment StartX=19.9194 StartY=-5.9387 StartZ=0 EndX=19.9194 EndY=-1.9387 EndZ=0
    g14: LineSegment StartX=79.9194 StartY=-1.9387 StartZ=0 EndX=19.9194 EndY=-1.9387 EndZ=0
  constraints (30):
    c: Horizontal(g0)
    c: Distance(g0) = 5
    c: Vertical(g1)
    c: Distance(g1) = 5
    c: Coincident(g5,g1)
    c: Weight(g2) = 1
    c: Equal(g2,g3)
    c: Equal(g2,g4)
    c: Coincident(g5,g0)
    c: InternalAlignment(g2,g5)
    c: InternalAlignment(g3,g5)
    c: InternalAlignment(g4,g5)
    c: InternalAlignment(g6,g5)
    c: InternalAlignment(g7,g5)
    c: Coincident(g8,g0)
    c: Vertical(g8)
    c: Block(g3)
    c: Block(g9)
    c: Block(g5)
    c: Block(g10)
    c: Block(g11)
    c: Vertical(g12)
    c: Distance(g12) = 4
    c: Coincident(g13,g8)
    c: Vertical(g13)
    c: Distance(g13) = 4
    c: Coincident(g14,g12)
    c: Horizontal(g14)
    c: Block(g12)
    c: Coincident(g14,g13)
FEATURE [Part::Extrusion] Extrude020  label="legBrace008"
  Base = -> Sketch019
  Dir = (0,-1,2e-16)
  DirMode = 2
  FaceMakerClass = Part::FaceMakerBullseye
  LengthFwd = 8
  LengthRev = 0
  Placement = pos=(100,110.16,3.4) rot=(-1,0,0;0rad)
  Solid = true
  Symmetric = false
FEATURE [Sketcher::SketchObject] Sketch020
  FullyConstrained = true
  Placement = pos=(0,0,0) rot=(1,0,0;1.5708rad)
  sketch-geometry (15):
    g0: LineSegment StartX=19.9194 StartY=-115.939 StartZ=0 EndX=24.9194 EndY=-115.939 EndZ=0
    g1: LineSegment StartX=79.9194 StartY=-5.9387 StartZ=0 EndX=79.9194 EndY=-10.9387 EndZ=0
    g2: Circle CenterX=79.9194 CenterY=-10.9387 CenterZ=0 NormalX=0 NormalY=0 NormalZ=1 AngleXU=0 Radius=1
    g3: Circle CenterX=24.9194 CenterY=-10.9387 CenterZ=0 NormalX=0 NormalY=0 NormalZ=1 AngleXU=0 Radius=1
    g4: Circle CenterX=24.9194 CenterY=-115.939 CenterZ=0 NormalX=0 NormalY=0 NormalZ=1 AngleXU=0 Radius=1
    g5: BSplineCurve PolesCount=3 KnotsCount=2 Degree=2 IsPeriodic=0
    g6: GeomPoint X=79.9194 Y=-10.9387 Z=0
    g7: GeomPoint X=24.9194 Y=-115.939 Z=0
    g8: LineSegment StartX=19.9194 StartY=-5.9387 StartZ=0 EndX=19.9194 EndY=-115.939 EndZ=0
    g9: Circle CenterX=33.6194 CenterY=-19.6387 CenterZ=0 NormalX=0 NormalY=0 NormalZ=1 AngleXU=0 Radius=8.7
    g10: Circle CenterX=28.8194 CenterY=-36.6387 CenterZ=0 NormalX=0 NormalY=0 NormalZ=1 AngleXU=0 Radius=3.9
    g11: Circle CenterX=48.6194 CenterY=-13.5387 CenterZ=0 NormalX=0 NormalY=0 NormalZ=1 AngleXU=0 Radius=2.6
    g12: LineSegment StartX=79.9194 StartY=-5.9387 StartZ=0 EndX=79.9194 EndY=-1.9387 EndZ=0
    g13: LineSegment StartX=19.9194 StartY=-5.9387 StartZ=0 EndX=19.9194 EndY=-1.9387 EndZ=0
    g14: LineSegment StartX=79.9194 StartY=-1.9387 StartZ=0 EndX=19.9194 EndY=-1.9387 EndZ=0
  constraints (30):
    c: Horizontal(g0)
    c: Distance(g0) = 5
    c: Vertical(g1)
    c: Distance(g1) = 5
    c: Coincident(g5,g1)
    c: Weight(g2) = 1
    c: Equal(g2,g3)
    c: Equal(g2,g4)
    c: Coincident(g5,g0)
    c: InternalAlignment(g2,g5)
    c: InternalAlignment(g3,g5)
    c: InternalAlignment(g4,g5)
    c: InternalAlignment(g6,g5)
    c: InternalAlignment(g7,g5)
    c: Coincident(g8,g0)
    c: Vertical(g8)
    c: Block(g3)
    c: Block(g9)
    c: Block(g5)
    c: Block(g10)
    c: Block(g11)
    c: Vertical(g12)
    c: Distance(g12) = 4
    c: Coincident(g13,g8)
    c: Vertical(g13)
    c: Distance(g13) = 4
    c: Coincident(g14,g12)
    c: Horizontal(g14)
    c: Block(g12)
    c: Coincident(g14,g13)
FEATURE [Part::Extrusion] Extrude021  label="legBrace009"
  Base = -> Sketch020
  Dir = (0,-1,3e-16)
  DirMode = 2
  FaceMakerClass = Part::FaceMakerBullseye
  LengthFwd = 8
  LengthRev = 0
  Placement = pos=(100,110.16,3.4) rot=(-1,0,0;0rad)
  Solid = true
  Symmetric = false
FEATURE [Part::Fuse] Fusion003  label="legBraceRight003"
  Base = -> Extrude020
  Placement = pos=(0,0,0) rot=(0,0,1;3.14159rad)
  Tool = -> Extrude021
FEATURE [Part::Fuse] Fusion004  label="legBraceRight004"
  Base = -> Extrude018
  Placement = pos=(0,0,0) rot=(0,0,1;3.14159rad)
  Tool = -> Extrude019
FEATURE [Part::Fuse] Fusion005  label="rightLeftBrace001"
  Base = -> Fusion003
  Placement = pos=(512.26,174.65,-35.86) rot=(-1,0,0;0.361109rad)
  Tool = -> Fusion004
FEATURE [App::MeasureDistance] Distance  label="Distance: 14.93 mm"
  Distance = 14.9268
  P1 = (-28.0006,108.862,-0.0377614)
  P2 = (-42.9272,108.925,0)
FEATURE [Sketcher::SketchObject] Sketch021  label="legTop001"
  FullyConstrained = true
  MapMode = 4
  Placement = pos=(0,0,0) rot=(0.57735,0.57735,0.57735;2.0944rad)
  sketch-geometry (41):
    g0: BSplineCurve PolesCount=3 KnotsCount=2 Degree=2 IsPeriodic=0
    g1: ArcOfCircle CenterX=73.1223 CenterY=-32.291 CenterZ=0 NormalX=0 NormalY=0 NormalZ=1 AngleXU=0 Radius=13 StartAngle=5.92268 EndAngle=9.06428
    g2: ArcOfCircle CenterX=66.7816 CenterY=-49.1439 CenterZ=0 NormalX=0 NormalY=0 NormalZ=1 AngleXU=0 Radius=13 StartAngle=2.78068 EndAngle=5.92131
    g3-g6: Circle x4 (B-spline internal-alignment scaffolding for g7; pole/knot coordinates omitted)
    g7: BSplineCurve PolesCount=4 KnotsCount=2 Degree=3 IsPeriodic=0
    g8: GeomPoint X=28.8094 Y=-19.0875 Z=0
    g9: GeomPoint X=47.0443 Y=-50.4712 Z=0
    g10: Circle CenterX=53.5586 CenterY=-23.2695 CenterZ=0 NormalX=0 NormalY=0 NormalZ=1 AngleXU=0 Radius=3.24518
    g11: LineSegment StartX=17.2232 StartY=-16.0875 StartZ=0 EndX=17.2232 EndY=-19.0875 EndZ=0
    g12: ArcOfCircle CenterX=17.2475 CenterY=-181.166 CenterZ=0 NormalX=0 NormalY=0 NormalZ=1 AngleXU=0 Radius=13 StartAngle=5.92268 EndAngle=7.49361
    g13: ArcOfCircle CenterX=29.5716 CenterY=-148.408 CenterZ=0 NormalX=0 NormalY=0 NormalZ=1 AngleXU=0 Radius=13 StartAngle=4.35228 EndAngle=5.92131
    g14: ArcOfCircle CenterX=35.8967 CenterY=-131.555 CenterZ=0 NormalX=0 NormalY=0 NormalZ=1 AngleXU=0 Radius=13 StartAngle=5.92268 EndAngle=7.49902
    g15: ArcOfCircle CenterX=48.1805 CenterY=-98.7782 CenterZ=0 NormalX=0 NormalY=0 NormalZ=1 AngleXU=0 Radius=13 StartAngle=4.34921 EndAngle=5.92131
    g16: ArcOfCircle CenterX=54.5183 CenterY=-81.9247 CenterZ=0 NormalX=0 NormalY=0 NormalZ=1 AngleXU=0 Radius=13 StartAngle=5.92268 EndAngle=8.70432
    g17: ArcOfCircle CenterX=20.184 CenterY=-217.506 CenterZ=0 NormalX=0 NormalY=0 NormalZ=1 AngleXU=0 Radius=3.81084 StartAngle=1.88136 EndAngle=6.80465
    g18: ArcOfCircle CenterX=36.3663 CenterY=-113.042 CenterZ=0 NormalX=0 NormalY=0 NormalZ=1 AngleXU=0 Radius=3.60555 StartAngle=0.230024 EndAngle=5.3372
    g19: ArcOfCircle CenterX=17.7945 CenterY=-162.686 CenterZ=0 NormalX=0 NormalY=0 NormalZ=1 AngleXU=0 Radius=3.60555 StartAngle=0.230024 EndAngle=5.3372
    g20: ArcOfCircle CenterX=49.8795 CenterY=-62.6074 CenterZ=0 NormalX=0 NormalY=0 NormalZ=1 AngleXU=0 Radius=3.84187 StartAngle=4.46973 EndAngle=9.40343
    g21: LineSegment StartX=48.9563 StartY=-66.3367 StartZ=0 EndX=44.7488 EndY=-73.3482 EndZ=0
    g22: LineSegment StartX=41.085 StartY=-66.3176 StartZ=0 EndX=46.0385 EndY=-62.5254 EndZ=0
    g23: LineSegment StartX=47.0443 StartY=-50.4712 StartZ=0 EndX=41.085 EndY=-66.3176 EndZ=0
    g24: LineSegment StartX=17.2232 StartY=-16.0875 StartZ=0 EndX=117.223 EndY=-16.0875 EndZ=0
    g25: LineSegment StartX=28.8094 StartY=-19.0875 StartZ=0 EndX=17.2232 EndY=-19.0875 EndZ=0
    g26: LineSegment StartX=117.223 StartY=-16.0875 StartZ=0 EndX=117.223 EndY=-19.0875 EndZ=0
    g27: LineSegment StartX=85.2866 StartY=-36.8766 StartZ=0 EndX=78.9396 EndY=-53.7463 EndZ=0
    g28: LineSegment StartX=60.9579 StartY=-27.7053 StartZ=0 EndX=54.6191 EndY=-44.5532 EndZ=0
    g29: LineSegment StartX=23.4884 StartY=-215.608 StartZ=0 EndX=94.6579 EndY=-26.1359 EndZ=0
    g30: LineSegment StartX=19.0195 StartY=-213.878 StartZ=0 EndX=29.4118 EndY=-185.752 EndZ=0
    g31: LineSegment StartX=22.7134 StartY=-166.661 StartZ=0 EndX=21.8316 EndY=-169.001 EndZ=0
    g32: LineSegment StartX=19.9036 StartY=-165.61 StartZ=0 EndX=22.7134 EndY=-166.661 EndZ=0
    g33: LineSegment StartX=21.3051 StartY=-161.864 StartZ=0 EndX=24.1149 EndY=-162.915 EndZ=0
    g34: LineSegment StartX=24.1149 StartY=-162.915 StartZ=0 EndX=24.9906 EndY=-160.574 EndZ=0
    g35: LineSegment StartX=41.7296 StartY=-153.01 StartZ=0 EndX=48.061 EndY=-136.14 EndZ=0
    g36: LineSegment StartX=41.2852 StartY=-117.017 StartZ=0 EndX=40.4148 EndY=-119.365 EndZ=0
    g37: LineSegment StartX=38.4753 StartY=-115.966 StartZ=0 EndX=41.2852 EndY=-117.017 EndZ=0
    g38: LineSegment StartX=39.8769 StartY=-112.22 StartZ=0 EndX=42.6867 EndY=-113.271 EndZ=0
    g39: LineSegment StartX=42.6867 StartY=-113.271 StartZ=0 EndX=43.5622 EndY=-110.93 EndZ=0
    g40: LineSegment StartX=66.6827 StartY=-86.5104 StartZ=0 EndX=60.3386 EndY=-103.381 EndZ=0
  constraints (65):
    c: Block(g0)
    c: Block(g1)
    c: Block(g2)
    c: Weight(g3) = 1
    c: Equal(g3,g4)
    c: Equal(g3,g5)
    c: Equal(g3,g6)
    c: InternalAlignment(g3-g6 -> g7) x4
    c: InternalAlignment(g8,g7)
    c: InternalAlignment(g9,g7)
    c: Block(g10)
    c: Block(g7)
    c: Vertical(g11)
    c: Block(g12)
    c: Block(g13)
    c: Block(g14)
    c: Block(g15)
    c: Block(g16)
    c: Block(g17)
    c: Block(g18)
    c: Block(g19)
    c: Block(g20)
    c: Coincident(g21,g20)
    c: Coincident(g21,g16)
    c: Coincident(g22,g20)
    c: Block(g22)
    c: Coincident(g23,g7)
    c: Coincident(g23,g22)
    c: Coincident(g24,g11)
    c: Horizontal(g24)
    c: Coincident(g25,g7)
    c: Coincident(g25,g11)
    c: Horizontal(g25)
    c: Coincident(g26,g24)
    c: Coincident(g26,g0)
    c: Vertical(g26)
    c: Block(g24)
    c: Coincident(g27,g1)
    c: Coincident(g27,g2)
    c: Coincident(g28,g1)
    c: Coincident(g28,g2)
    c: Coincident(g29,g17)
    c: Coincident(g29,g0)
    c: Coincident(g30,g17)
    c: Coincident(g30,g12)
    c: Coincident(g31,g12)
    c: Coincident(g32,g19)
    c: Coincident(g32,g31)
    c: Block(g31)
    c: Coincident(g33,g19)
    c: Coincident(g34,g33)
    c: Coincident(g34,g13)
    c: Block(g34)
    c: Coincident(g35,g13)
    c: Coincident(g35,g14)
    c: Coincident(g36,g14)
    c: Coincident(g37,g18)
    c: Coincident(g37,g36)
    c: Block(g36)
    c: Coincident(g38,g18)
    c: Coincident(g39,g38)
    c: Coincident(g39,g15)
    c: Block(g39)
    c: Coincident(g40,g16)
    c: Coincident(g40,g15)
FEATURE [Part::Extrusion] Extrude022  label="topLegRight001"
  Base = -> Sketch021
  Dir = (1,0,0)
  DirMode = 2
  FaceMakerClass = Part::FaceMakerBullseye
  LengthFwd = 12
  LengthRev = 0
  Placement = pos=(392.24,11,16) rot=(0,0,1;0rad)
  Solid = true
  Symmetric = false
FEATURE [App::MeasureDistance] Distance001  label="Distance: 14.83 mm"
  Distance = 14.8334
  P1 = (392.24,108.867,-0.0194206)
  P2 = (407.073,108.936,0)
FEATURE [Sketcher::SketchObject] Sketch022
  FullyConstrained = true
  Placement = pos=(0,0,0) rot=(0.57735,0.57735,0.57735;2.0944rad)
  sketch-geometry (18):
    g0: LineSegment StartX=-152.23 StartY=29.0049 StartZ=0 EndX=-143.23 EndY=29.0049 EndZ=0
    g1: LineSegment StartX=-152.23 StartY=29.0049 StartZ=0 EndX=-152.23 EndY=51.0049 EndZ=0
    g2: LineSegment StartX=-152.23 StartY=51.0049 StartZ=0 EndX=-130.23 EndY=51.0049 EndZ=0
    g3: LineSegment StartX=-130.23 StartY=51.0049 StartZ=0 EndX=-130.23 EndY=46.0049 EndZ=0
    g4: LineSegment StartX=-130.23 StartY=46.0049 StartZ=0 EndX=-143.23 EndY=46.0049 EndZ=0
    g5: Circle CenterX=-145.23 CenterY=31.0049 CenterZ=0 NormalX=0 NormalY=0 NormalZ=1 AngleXU=0 Radius=1
    g6: Circle CenterX=-145.23 CenterY=29.0049 CenterZ=0 NormalX=0 NormalY=0 NormalZ=1 AngleXU=0 Radius=1
    g7: Circle CenterX=-143.23 CenterY=29.0049 CenterZ=0 NormalX=0 NormalY=0 NormalZ=1 AngleXU=0 Radius=1
    g8: BSplineCurve PolesCount=3 KnotsCount=2 Degree=2 IsPeriodic=0
    g9: GeomPoint X=-145.23 Y=31.0049 Z=0
    g10: GeomPoint X=-143.23 Y=29.0049 Z=0
    g11: Circle CenterX=-145.23 CenterY=44.0049 CenterZ=0 NormalX=0 NormalY=0 NormalZ=1 AngleXU=0 Radius=1
    g12: Circle CenterX=-145.23 CenterY=46.0049 CenterZ=0 NormalX=0 NormalY=0 NormalZ=1 AngleXU=0 Radius=1
    g13: Circle CenterX=-143.23 CenterY=46.0049 CenterZ=0 NormalX=0 NormalY=0 NormalZ=1 AngleXU=0 Radius=1
    g14: BSplineCurve PolesCount=3 KnotsCount=2 Degree=2 IsPeriodic=0
    g15: GeomPoint X=-145.23 Y=44.0049 Z=0
    g16: GeomPoint X=-143.23 Y=46.0049 Z=0
    g17: LineSegment StartX=-145.23 StartY=44.0049 StartZ=0 EndX=-145.23 EndY=31.0049 EndZ=0
  constraints (40):
    c: Horizontal(g0)
    c: Distance(g0) = 9
    c: Coincident(g1,g0)
    c: Vertical(g1)
    c: Distance(g1) = 22
    c: Coincident(g2,g1)
    c: Horizontal(g2)
    c: Coincident(g3,g2)
    c: Vertical(g3)
    c: Distance(g3) = 5
    c: Coincident(g4,g3)
    c: Horizontal(g4)
    c: Distance(g4) = 13
    c: PointOnObject(g6,g0)
    c: Weight(g5) = 1
    c: Equal(g5,g6)
    c: Equal(g5,g7)
    c: Coincident(g8,g0)
    c: InternalAlignment(g5,g8)
    c: InternalAlignment(g6,g8)
    c: InternalAlignment(g7,g8)
    c: InternalAlignment(g9,g8)
    c: InternalAlignment(g10,g8)
    c: Weight(g11) = 1
    c: Equal(g11,g12)
    c: Equal(g11,g13)
    c: Coincident(g14,g4)
    c: InternalAlignment(g11,g14)
    c: InternalAlignment(g12,g14)
    c: InternalAlignment(g13,g14)
    c: InternalAlignment(g15,g14)
    c: InternalAlignment(g16,g14)
    c: Coincident(g17,g14)
    c: Coincident(g17,g8)
    c: Vertical(g17)
    c: Block(g4)
    c: Block(g17)
    c: Block(g14)
    c: Block(g8)
    c: Distance(g2) = 22
FEATURE [Part::Extrusion] Extrude023  label="laptopRetainer"
  Base = -> Sketch022
  Dir = (1,0,0)
  DirMode = 2
  FaceMakerClass = Part::FaceMakerBullseye
  LengthFwd = 150
  LengthRev = 0
  Placement = pos=(-42.925,50.355,-8.454) rot=(1,0,0;0.080285rad)
  Solid = true
  Symmetric = false
FEATURE [Sketcher::SketchObject] Sketch023
  FullyConstrained = true
  Placement = pos=(0,0,0) rot=(0.57735,0.57735,0.57735;2.0944rad)
  sketch-geometry (18):
    g0: LineSegment StartX=-152.23 StartY=29.0049 StartZ=0 EndX=-143.23 EndY=29.0049 EndZ=0
    g1: LineSegment StartX=-152.23 StartY=29.0049 StartZ=0 EndX=-152.23 EndY=51.0049 EndZ=0
    g2: LineSegment StartX=-152.23 StartY=51.0049 StartZ=0 EndX=-130.23 EndY=51.0049 EndZ=0
    g3: LineSegment StartX=-130.23 StartY=51.0049 StartZ=0 EndX=-130.23 EndY=46.0049 EndZ=0
    g4: LineSegment StartX=-130.23 StartY=46.0049 StartZ=0 EndX=-143.23 EndY=46.0049 EndZ=0
    g5: Circle CenterX=-145.23 CenterY=31.0049 CenterZ=0 NormalX=0 NormalY=0 NormalZ=1 AngleXU=0 Radius=1
    g6: Circle CenterX=-145.23 CenterY=29.0049 CenterZ=0 NormalX=0 NormalY=0 NormalZ=1 AngleXU=0 Radius=1
    g7: Circle CenterX=-143.23 CenterY=29.0049 CenterZ=0 NormalX=0 NormalY=0 NormalZ=1 AngleXU=0 Radius=1
    g8: BSplineCurve PolesCount=3 KnotsCount=2 Degree=2 IsPeriodic=0
    g9: GeomPoint X=-145.23 Y=31.0049 Z=0
    g10: GeomPoint X=-143.23 Y=29.0049 Z=0
    g11: Circle CenterX=-145.23 CenterY=44.0049 CenterZ=0 NormalX=0 NormalY=0 NormalZ=1 AngleXU=0 Radius=1
    g12: Circle CenterX=-145.23 CenterY=46.0049 CenterZ=0 NormalX=0 NormalY=0 NormalZ=1 AngleXU=0 Radius=1
    g13: Circle CenterX=-143.23 CenterY=46.0049 CenterZ=0 NormalX=0 NormalY=0 NormalZ=1 AngleXU=0 Radius=1
    g14: BSplineCurve PolesCount=3 KnotsCount=2 Degree=2 IsPeriodic=0
    g15: GeomPoint X=-145.23 Y=44.0049 Z=0
    g16: GeomPoint X=-143.23 Y=46.0049 Z=0
    g17: LineSegment StartX=-145.23 StartY=44.0049 StartZ=0 EndX=-145.23 EndY=31.0049 EndZ=0
  constraints (40):
    c: Horizontal(g0)
    c: Distance(g0) = 9
    c: Coincident(g1,g0)
    c: Vertical(g1)
    c: Distance(g1) = 22
    c: Coincident(g2,g1)
    c: Horizontal(g2)
    c: Coincident(g3,g2)
    c: Vertical(g3)
    c: Distance(g3) = 5
    c: Coincident(g4,g3)
    c: Horizontal(g4)
    c: Distance(g4) = 13
    c: PointOnObject(g6,g0)
    c: Weight(g5) = 1
    c: Equal(g5,g6)
    c: Equal(g5,g7)
    c: Coincident(g8,g0)
    c: InternalAlignment(g5,g8)
    c: InternalAlignment(g6,g8)
    c: InternalAlignment(g7,g8)
    c: InternalAlignment(g9,g8)
    c: InternalAlignment(g10,g8)
    c: Weight(g11) = 1
    c: Equal(g11,g12)
    c: Equal(g11,g13)
    c: Coincident(g14,g4)
    c: InternalAlignment(g11,g14)
    c: InternalAlignment(g12,g14)
    c: InternalAlignment(g13,g14)
    c: InternalAlignment(g15,g14)
    c: InternalAlignment(g16,g14)
    c: Coincident(g17,g14)
    c: Coincident(g17,g8)
    c: Vertical(g17)
    c: Block(g4)
    c: Block(g17)
    c: Block(g14)
    c: Block(g8)
    c: Distance(g2) = 22
FEATURE [Part::Extrusion] Extrude024  label="laptopRetainer001"
  Base = -> Sketch023
  Dir = (1,0,0)
  DirMode = 2
  FaceMakerClass = Part::FaceMakerBullseye
  LengthFwd = 150
  LengthRev = 0
  Placement = pos=(107.08,50.35,-8.45) rot=(1,0,0;0.080285rad)
  Solid = true
  Symmetric = false
FEATURE [Sketcher::SketchObject] Sketch024
  FullyConstrained = true
  Placement = pos=(0,0,0) rot=(0.57735,0.57735,0.57735;2.0944rad)
  sketch-geometry (18):
    g0: LineSegment StartX=-152.23 StartY=29.0049 StartZ=0 EndX=-143.23 EndY=29.0049 EndZ=0
    g1: LineSegment StartX=-152.23 StartY=29.0049 StartZ=0 EndX=-152.23 EndY=51.0049 EndZ=0
    g2: LineSegment StartX=-152.23 StartY=51.0049 StartZ=0 EndX=-130.23 EndY=51.0049 EndZ=0
    g3: LineSegment StartX=-130.23 StartY=51.0049 StartZ=0 EndX=-130.23 EndY=46.0049 EndZ=0
    g4: LineSegment StartX=-130.23 StartY=46.0049 StartZ=0 EndX=-143.23 EndY=46.0049 EndZ=0
    g5: Circle CenterX=-145.23 CenterY=31.0049 CenterZ=0 NormalX=0 NormalY=0 NormalZ=1 AngleXU=0 Radius=1
    g6: Circle CenterX=-145.23 CenterY=29.0049 CenterZ=0 NormalX=0 NormalY=0 NormalZ=1 AngleXU=0 Radius=1
    g7: Circle CenterX=-143.23 CenterY=29.0049 CenterZ=0 NormalX=0 NormalY=0 NormalZ=1 AngleXU=0 Radius=1
    g8: BSplineCurve PolesCount=3 KnotsCount=2 Degree=2 IsPeriodic=0
    g9: GeomPoint X=-145.23 Y=31.0049 Z=0
    g10: GeomPoint X=-143.23 Y=29.0049 Z=0
    g11: Circle CenterX=-145.23 CenterY=44.0049 CenterZ=0 NormalX=0 NormalY=0 NormalZ=1 AngleXU=0 Radius=1
    g12: Circle CenterX=-145.23 CenterY=46.0049 CenterZ=0 NormalX=0 NormalY=0 NormalZ=1 AngleXU=0 Radius=1
    g13: Circle CenterX=-143.23 CenterY=46.0049 CenterZ=0 NormalX=0 NormalY=0 NormalZ=1 AngleXU=0 Radius=1
    g14: BSplineCurve PolesCount=3 KnotsCount=2 Degree=2 IsPeriodic=0
    g15: GeomPoint X=-145.23 Y=44.0049 Z=0
    g16: GeomPoint X=-143.23 Y=46.0049 Z=0
    g17: LineSegment StartX=-145.23 StartY=44.0049 StartZ=0 EndX=-145.23 EndY=31.0049 EndZ=0
  constraints (40):
    c: Horizontal(g0)
    c: Distance(g0) = 9
    c: Coincident(g1,g0)
    c: Vertical(g1)
    c: Distance(g1) = 22
    c: Coincident(g2,g1)
    c: Horizontal(g2)
    c: Coincident(g3,g2)
    c: Vertical(g3)
    c: Distance(g3) = 5
    c: Coincident(g4,g3)
    c: Horizontal(g4)
    c: Distance(g4) = 13
    c: PointOnObject(g6,g0)
    c: Weight(g5) = 1
    c: Equal(g5,g6)
    c: Equal(g5,g7)
    c: Coincident(g8,g0)
    c: InternalAlignment(g5,g8)
    c: InternalAlignment(g6,g8)
    c: InternalAlignment(g7,g8)
    c: InternalAlignment(g9,g8)
    c: InternalAlignment(g10,g8)
    c: Weight(g11) = 1
    c: Equal(g11,g12)
    c: Equal(g11,g13)
    c: Coincident(g14,g4)
    c: InternalAlignment(g11,g14)
    c: InternalAlignment(g12,g14)
    c: InternalAlignment(g13,g14)
    c: InternalAlignment(g15,g14)
    c: InternalAlignment(g16,g14)
    c: Coincident(g17,g14)
    c: Coincident(g17,g8)
    c: Vertical(g17)
    c: Block(g4)
    c: Block(g17)
    c: Block(g14)
    c: Block(g8)
    c: Distance(g2) = 22
FEATURE [Part::Extrusion] Extrude025  label="laptopRetainer002"
  Base = -> Sketch024
  Dir = (1,0,0)
  DirMode = 2
  FaceMakerClass = Part::FaceMakerBullseye
  LengthFwd = 150
  LengthRev = 0
  Placement = pos=(257.08,50.35,-8.45) rot=(1,0,0;0.080285rad)
  Solid = true
  Symmetric = false
FEATURE [Part::Box] Box  label="removeFromtTop"
  AttacherType = Attacher::AttachEngine3D
  Height = 56
  Length = 470
  Placement = pos=(-47.93,-106.78,8) rot=(1,0,0;0.080285rad)
  Width = 260
FEATURE [Part::Box] Box001  label="removeFromtTop001"
  AttacherType = Attacher::AttachEngine3D
  Height = 56
  Length = 470
  Placement = pos=(-47.93,-106.78,8) rot=(1,0,0;0.080285rad)
  Width = 260
FEATURE [Part::Cut] Cut
  Base = -> Extrude007
  Tool = -> Box
FEATURE [Part::Box] Box002  label="removeFromtTop002"
  AttacherType = Attacher::AttachEngine3D
  Height = 56
  Length = 470
  Placement = pos=(-47.93,-106.78,8) rot=(1,0,0;0.080285rad)
  Width = 260
FEATURE [Part::Cut] Cut001
  Base = -> Extrude010
  Tool = -> Box001
FEATURE [Part::Box] Box003  label="removeFromtTop003"
  AttacherType = Attacher::AttachEngine3D
  Height = 56
  Length = 470
  Placement = pos=(-47.93,-106.78,8) rot=(1,0,0;0.080285rad)
  Width = 260
FEATURE [Part::Cut] Cut002
  Base = -> Extrude011
  Tool = -> Box002
FEATURE [Part::Box] Box004  label="removeFromtTop004"
  AttacherType = Attacher::AttachEngine3D
  Height = 56
  Length = 470
  Placement = pos=(-47.93,-106.78,8) rot=(1,0,0;0.080285rad)
  Width = 260
FEATURE [Part::Cut] Cut003
  Base = -> Extrude008
  Tool = -> Box003
FEATURE [Part::Box] Box005  label="removeFromtTop005"
  AttacherType = Attacher::AttachEngine3D
  Height = 56
  Length = 470
  Placement = pos=(-47.93,-106.78,8) rot=(1,0,0;0.080285rad)
  Width = 260
FEATURE [Part::Cut] Cut004
  Base = -> Extrude012
  Tool = -> Box004
FEATURE [Part::Cut] Cut005
  Base = -> Extrude009
  Tool = -> Box005
FEATURE [App::MeasureDistance] Distance002  label="Distance: 8.18 mm"
  Distance = 8.17779
  P1 = (-42.9272,-103.768,8.17763)
  P2 = (-42.9272,-103.716,0)
FEATURE [Part::Box] Box006  label="removeFromBottomOfTop"
  AttacherType = Attacher::AttachEngine3D
  Height = 10
  Length = 475
  Placement = pos=(-51,-113,-1) rot=(1,0,0;0.080285rad)
  Width = 10
FEATURE [Part::Box] Box007  label="removeFromBottomOfTop001"
  AttacherType = Attacher::AttachEngine3D
  Height = 10
  Length = 475
  Placement = pos=(-51,-113,-1) rot=(1,0,0;0.080285rad)
  Width = 10
FEATURE [Part::Cut] Cut006
  Base = -> Cut004
  Tool = -> Box006
FEATURE [Part::Box] Box008  label="removeFromBottomOfTop002"
  AttacherType = Attacher::AttachEngine3D
  Height = 10
  Length = 475
  Placement = pos=(-51,-113,-1) rot=(1,0,0;0.080285rad)
  Width = 10
FEATURE [Part::Cut] Cut007
  Base = -> Cut002
  Tool = -> Box007
FEATURE [Part::Cut] Cut008
  Base = -> Cut001
  Tool = -> Box008
FEATURE [Part::Box] Box009  label="Cube"
  AttacherType = Attacher::AttachEngine3D
  Height = 10
  Length = 40
  Placement = pos=(12.07,-101,0) rot=(0,0,1;0rad)
  Width = 4
FEATURE [Part::Box] Box010  label="Cube001"
  AttacherType = Attacher::AttachEngine3D
  Height = 10
  Length = 40
  Placement = pos=(162.7,-101,0) rot=(0,0,1;0rad)
  Width = 4
FEATURE [Part::Box] Box011  label="Cube002"
  AttacherType = Attacher::AttachEngine3D
  Height = 10
  Length = 40
  Placement = pos=(312.07,-101,0) rot=(0,0,1;0rad)
  Width = 4
FEATURE [Part::Fuse] Fusion006  label="laptopRetainer01"
  Base = -> Extrude023
  Tool = -> Box009
FEATURE [Part::Fuse] Fusion007  label="laptopRetainer02"
  Base = -> Extrude024
  Tool = -> Box010
FEATURE [Part::MultiFuse] Fusion008  label="laptopRetainer03"
  Shapes = -> [Extrude025,Box011]
FEATURE [Part::Box] Box012  label="Cube003"
  AttacherType = Attacher::AttachEngine3D
  Height = 10
  Length = 10
  Placement = pos=(101,-102.5,12) rot=(1,0,0;0.080285rad)
  Width = 4
FEATURE [Part::Box] Box013  label="Cube004"
  AttacherType = Attacher::AttachEngine3D
  Height = 10
  Length = 10
  Placement = pos=(253,-102.5,12) rot=(1,0,0;0.080285rad)
  Width = 4
FEATURE [Part::MultiFuse] Fusion009  label="laptopRetainer003"
  Shapes = -> [Box013,Fusion007,Box012]
FEATURE [Sketcher::SketchObject] Sketch025
  FullyConstrained = true
  Placement = pos=(0,0,0) rot=(0.57735,0.57735,0.57735;2.0944rad)
  sketch-geometry (18):
    g0: LineSegment StartX=-152.23 StartY=29.0049 StartZ=0 EndX=-143.23 EndY=29.0049 EndZ=0
    g1: LineSegment StartX=-152.23 StartY=29.0049 StartZ=0 EndX=-152.23 EndY=51.0049 EndZ=0
    g2: LineSegment StartX=-152.23 StartY=51.0049 StartZ=0 EndX=-130.23 EndY=51.0049 EndZ=0
    g3: LineSegment StartX=-130.23 StartY=51.0049 StartZ=0 EndX=-130.23 EndY=46.0049 EndZ=0
    g4: LineSegment StartX=-130.23 StartY=46.0049 StartZ=0 EndX=-143.23 EndY=46.0049 EndZ=0
    g5: Circle CenterX=-145.23 CenterY=31.0049 CenterZ=0 NormalX=0 NormalY=0 NormalZ=1 AngleXU=0 Radius=1
    g6: Circle CenterX=-145.23 CenterY=29.0049 CenterZ=0 NormalX=0 NormalY=0 NormalZ=1 AngleXU=0 Radius=1
    g7: Circle CenterX=-143.23 CenterY=29.0049 CenterZ=0 NormalX=0 NormalY=0 NormalZ=1 AngleXU=0 Radius=1
    g8: BSplineCurve PolesCount=3 KnotsCount=2 Degree=2 IsPeriodic=0
    g9: GeomPoint X=-145.23 Y=31.0049 Z=0
    g10: GeomPoint X=-143.23 Y=29.0049 Z=0
    g11: Circle CenterX=-145.23 CenterY=44.0049 CenterZ=0 NormalX=0 NormalY=0 NormalZ=1 AngleXU=0 Radius=1
    g12: Circle CenterX=-145.23 CenterY=46.0049 CenterZ=0 NormalX=0 NormalY=0 NormalZ=1 AngleXU=0 Radius=1
    g13: Circle CenterX=-143.23 CenterY=46.0049 CenterZ=0 NormalX=0 NormalY=0 NormalZ=1 AngleXU=0 Radius=1
    g14: BSplineCurve PolesCount=3 KnotsCount=2 Degree=2 IsPeriodic=0
    g15: GeomPoint X=-145.23 Y=44.0049 Z=0
    g16: GeomPoint X=-143.23 Y=46.0049 Z=0
    g17: LineSegment StartX=-145.23 StartY=44.0049 StartZ=0 EndX=-145.23 EndY=31.0049 EndZ=0
  constraints (40):
    c: Horizontal(g0)
    c: Distance(g0) = 9
    c: Coincident(g1,g0)
    c: Vertical(g1)
    c: Distance(g1) = 22
    c: Coincident(g2,g1)
    c: Horizontal(g2)
    c: Coincident(g3,g2)
    c: Vertical(g3)
    c: Distance(g3) = 5
    c: Coincident(g4,g3)
    c: Horizontal(g4)
    c: Distance(g4) = 13
    c: PointOnObject(g6,g0)
    c: Weight(g5) = 1
    c: Equal(g5,g6)
    c: Equal(g5,g7)
    c: Coincident(g8,g0)
    c: InternalAlignment(g5,g8)
    c: InternalAlignment(g6,g8)
    c: InternalAlignment(g7,g8)
    c: InternalAlignment(g9,g8)
    c: InternalAlignment(g10,g8)
    c: Weight(g11) = 1
    c: Equal(g11,g12)
    c: Equal(g11,g13)
    c: Coincident(g14,g4)
    c: InternalAlignment(g11,g14)
    c: InternalAlignment(g12,g14)
    c: InternalAlignment(g13,g14)
    c: InternalAlignment(g15,g14)
    c: InternalAlignment(g16,g14)
    c: Coincident(g17,g14)
    c: Coincident(g17,g8)
    c: Vertical(g17)
    c: Block(g4)
    c: Block(g17)
    c: Block(g14)
    c: Block(g8)
    c: Distance(g2) = 22
FEATURE [Part::Extrusion] Extrude026  label="laptopRetainer005"
  Base = -> Sketch025
  Dir = (1,0,0)
  DirMode = 2
  FaceMakerClass = Part::FaceMakerBullseye
  LengthFwd = 150
  LengthRev = 0
  Placement = pos=(107.08,50.35,-8.45) rot=(1,0,0;0.080285rad)
  Solid = true
  Symmetric = false
FEATURE [Part::Box] Box014  label="Cube005"
  AttacherType = Attacher::AttachEngine3D
  Height = 10
  Length = 40
  Placement = pos=(162.7,-101,0) rot=(0,0,1;0rad)
  Width = 4
FEATURE [Part::Fuse] Fusion010  label="laptopRetainer004"
  Base = -> Extrude026
  Tool = -> Box014
FEATURE [Part::Box] Box015  label="Cube006"
  AttacherType = Attacher::AttachEngine3D
  Height = 10
  Length = 10
  Placement = pos=(101,-102.5,12) rot=(1,0,0;0.080285rad)
  Width = 4
FEATURE [Part::Box] Box016  label="Cube007"
  AttacherType = Attacher::AttachEngine3D
  Height = 10
  Length = 10
  Placement = pos=(253,-102.5,12) rot=(1,0,0;0.080285rad)
  Width = 4
FEATURE [Part::MultiFuse] Fusion011  label="laptopRetainer006"
  Shapes = -> [Box016,Fusion010,Box015]
FEATURE [Part::Cut] Cut009  label="laptopRetainer010"
  Base = -> Fusion008
  Tool = -> Fusion009
FEATURE [Sketcher::SketchObject] Sketch026
  FullyConstrained = true
  Placement = pos=(0,0,0) rot=(0.57735,0.57735,0.57735;2.0944rad)
  sketch-geometry (18):
    g0: LineSegment StartX=-152.23 StartY=29.0049 StartZ=0 EndX=-143.23 EndY=29.0049 EndZ=0
    g1: LineSegment StartX=-152.23 StartY=29.0049 StartZ=0 EndX=-152.23 EndY=51.0049 EndZ=0
    g2: LineSegment StartX=-152.23 StartY=51.0049 StartZ=0 EndX=-130.23 EndY=51.0049 EndZ=0
    g3: LineSegment StartX=-130.23 StartY=51.0049 StartZ=0 EndX=-130.23 EndY=46.0049 EndZ=0
    g4: LineSegment StartX=-130.23 StartY=46.0049 StartZ=0 EndX=-143.23 EndY=46.0049 EndZ=0
    g5: Circle CenterX=-145.23 CenterY=31.0049 CenterZ=0 NormalX=0 NormalY=0 NormalZ=1 AngleXU=0 Radius=1
    g6: Circle CenterX=-145.23 CenterY=29.0049 CenterZ=0 NormalX=0 NormalY=0 NormalZ=1 AngleXU=0 Radius=1
    g7: Circle CenterX=-143.23 CenterY=29.0049 CenterZ=0 NormalX=0 NormalY=0 NormalZ=1 AngleXU=0 Radius=1
    g8: BSplineCurve PolesCount=3 KnotsCount=2 Degree=2 IsPeriodic=0
    g9: GeomPoint X=-145.23 Y=31.0049 Z=0
    g10: GeomPoint X=-143.23 Y=29.0049 Z=0
    g11: Circle CenterX=-145.23 CenterY=44.0049 CenterZ=0 NormalX=0 NormalY=0 NormalZ=1 AngleXU=0 Radius=1
    g12: Circle CenterX=-145.23 CenterY=46.0049 CenterZ=0 NormalX=0 NormalY=0 NormalZ=1 AngleXU=0 Radius=1
    g13: Circle CenterX=-143.23 CenterY=46.0049 CenterZ=0 NormalX=0 NormalY=0 NormalZ=1 AngleXU=0 Radius=1
    g14: BSplineCurve PolesCount=3 KnotsCount=2 Degree=2 IsPeriodic=0
    g15: GeomPoint X=-145.23 Y=44.0049 Z=0
    g16: GeomPoint X=-143.23 Y=46.0049 Z=0
    g17: LineSegment StartX=-145.23 StartY=44.0049 StartZ=0 EndX=-145.23 EndY=31.0049 EndZ=0
  constraints (40):
    c: Horizontal(g0)
    c: Distance(g0) = 9
    c: Coincident(g1,g0)
    c: Vertical(g1)
    c: Distance(g1) = 22
    c: Coincident(g2,g1)
    c: Horizontal(g2)
    c: Coincident(g3,g2)
    c: Vertical(g3)
    c: Distance(g3) = 5
    c: Coincident(g4,g3)
    c: Horizontal(g4)
    c: Distance(g4) = 13
    c: PointOnObject(g6,g0)
    c: Weight(g5) = 1
    c: Equal(g5,g6)
    c: Equal(g5,g7)
    c: Coincident(g8,g0)
    c: InternalAlignment(g5,g8)
    c: InternalAlignment(g6,g8)
    c: InternalAlignment(g7,g8)
    c: InternalAlignment(g9,g8)
    c: InternalAlignment(g10,g8)
    c: Weight(g11) = 1
    c: Equal(g11,g12)
    c: Equal(g11,g13)
    c: Coincident(g14,g4)
    c: InternalAlignment(g11,g14)
    c: InternalAlignment(g12,g14)
    c: InternalAlignment(g13,g14)
    c: InternalAlignment(g15,g14)
    c: InternalAlignment(g16,g14)
    c: Coincident(g17,g14)
    c: Coincident(g17,g8)
    c: Vertical(g17)
    c: Block(g4)
    c: Block(g17)
    c: Block(g14)
    c: Block(g8)
    c: Distance(g2) = 22
FEATURE [Part::Extrusion] Extrude027  label="laptopRetainer009"
  Base = -> Sketch026
  Dir = (1,0,0)
  DirMode = 2
  FaceMakerClass = Part::FaceMakerBullseye
  LengthFwd = 150
  LengthRev = 0
  Placement = pos=(107.08,50.35,-8.45) rot=(1,0,0;0.080285rad)
  Solid = true
  Symmetric = false
FEATURE [Part::Box] Box017  label="Cube008"
  AttacherType = Attacher::AttachEngine3D
  Height = 10
  Length = 40
  Placement = pos=(162.7,-101,0) rot=(0,0,1;0rad)
  Width = 4
FEATURE [Part::Fuse] Fusion012  label="laptopRetainer007"
  Base = -> Extrude027
  Tool = -> Box017
FEATURE [Part::Box] Box018  label="Cube009"
  AttacherType = Attacher::AttachEngine3D
  Height = 10
  Length = 10
  Placement = pos=(101,-102.5,12) rot=(1,0,0;0.080285rad)
  Width = 4
FEATURE [Part::Box] Box019  label="Cube010"
  AttacherType = Attacher::AttachEngine3D
  Height = 10
  Length = 10
  Placement = pos=(253,-102.5,12) rot=(1,0,0;0.080285rad)
  Width = 4
FEATURE [Part::MultiFuse] Fusion013  label="laptopRetainer008"
  Shapes = -> [Box019,Fusion012,Box018]
FEATURE [Part::Cut] Cut010  label="laptopRetainer011"
  Base = -> Fusion006
  Tool = -> Fusion011
FEATURE [Sketcher::SketchObject] Sketch027
  FullyConstrained = true
  Placement = pos=(0,0,0) rot=(0.57735,0.57735,0.57735;2.0944rad)
  sketch-geometry (18):
    g0: LineSegment StartX=-152.23 StartY=29.0049 StartZ=0 EndX=-143.23 EndY=29.0049 EndZ=0
    g1: LineSegment StartX=-152.23 StartY=29.0049 StartZ=0 EndX=-152.23 EndY=51.0049 EndZ=0
    g2: LineSegment StartX=-152.23 StartY=51.0049 StartZ=0 EndX=-130.23 EndY=51.0049 EndZ=0
    g3: LineSegment StartX=-130.23 StartY=51.0049 StartZ=0 EndX=-130.23 EndY=46.0049 EndZ=0
    g4: LineSegment StartX=-130.23 StartY=46.0049 StartZ=0 EndX=-143.23 EndY=46.0049 EndZ=0
    g5: Circle CenterX=-145.23 CenterY=31.0049 CenterZ=0 NormalX=0 NormalY=0 NormalZ=1 AngleXU=0 Radius=1
    g6: Circle CenterX=-145.23 CenterY=29.0049 CenterZ=0 NormalX=0 NormalY=0 NormalZ=1 AngleXU=0 Radius=1
    g7: Circle CenterX=-143.23 CenterY=29.0049 CenterZ=0 NormalX=0 NormalY=0 NormalZ=1 AngleXU=0 Radius=1
    g8: BSplineCurve PolesCount=3 KnotsCount=2 Degree=2 IsPeriodic=0
    g9: GeomPoint X=-145.23 Y=31.0049 Z=0
    g10: GeomPoint X=-143.23 Y=29.0049 Z=0
    g11: Circle CenterX=-145.23 CenterY=44.0049 CenterZ=0 NormalX=0 NormalY=0 NormalZ=1 AngleXU=0 Radius=1
    g12: Circle CenterX=-145.23 CenterY=46.0049 CenterZ=0 NormalX=0 NormalY=0 NormalZ=1 AngleXU=0 Radius=1
    g13: Circle CenterX=-143.23 CenterY=46.0049 CenterZ=0 NormalX=0 NormalY=0 NormalZ=1 AngleXU=0 Radius=1
    g14: BSplineCurve PolesCount=3 KnotsCount=2 Degree=2 IsPeriodic=0
    g15: GeomPoint X=-145.23 Y=44.0049 Z=0
    g16: GeomPoint X=-143.23 Y=46.0049 Z=0
    g17: LineSegment StartX=-145.23 StartY=44.0049 StartZ=0 EndX=-145.23 EndY=31.0049 EndZ=0
  constraints (40):
    c: Horizontal(g0)
    c: Distance(g0) = 9
    c: Coincident(g1,g0)
    c: Vertical(g1)
    c: Distance(g1) = 22
    c: Coincident(g2,g1)
    c: Horizontal(g2)
    c: Coincident(g3,g2)
    c: Vertical(g3)
    c: Distance(g3) = 5
    c: Coincident(g4,g3)
    c: Horizontal(g4)
    c: Distance(g4) = 13
    c: PointOnObject(g6,g0)
    c: Weight(g5) = 1
    c: Equal(g5,g6)
    c: Equal(g5,g7)
    c: Coincident(g8,g0)
    c: InternalAlignment(g5,g8)
    c: InternalAlignment(g6,g8)
    c: InternalAlignment(g7,g8)
    c: InternalAlignment(g9,g8)
    c: InternalAlignment(g10,g8)
    c: Weight(g11) = 1
    c: Equal(g11,g12)
    c: Equal(g11,g13)
    c: Coincident(g14,g4)
    c: InternalAlignment(g11,g14)
    c: InternalAlignment(g12,g14)
    c: InternalAlignment(g13,g14)
    c: InternalAlignment(g15,g14)
    c: InternalAlignment(g16,g14)
    c: Coincident(g17,g14)
    c: Coincident(g17,g8)
    c: Vertical(g17)
    c: Block(g4)
    c: Block(g17)
    c: Block(g14)
    c: Block(g8)
    c: Distance(g2) = 22
FEATURE [Part::Extrusion] Extrude028  label="laptopRetainer013"
  Base = -> Sketch027
  Dir = (1,0,0)
  DirMode = 2
  FaceMakerClass = Part::FaceMakerBullseye
  LengthFwd = 150
  LengthRev = 0
  Placement = pos=(-42.925,50.355,-8.454) rot=(1,0,0;0.080285rad)
  Solid = true
  Symmetric = false
FEATURE [Part::Box] Box020  label="Cube011"
  AttacherType = Attacher::AttachEngine3D
  Height = 10
  Length = 40
  Placement = pos=(12.07,-101,0) rot=(0,0,1;0rad)
  Width = 4
FEATURE [Part::Fuse] Fusion014  label="laptopRetainer012"
  Base = -> Extrude028
  Tool = -> Box020
FEATURE [Sketcher::SketchObject] Sketch028
  FullyConstrained = true
  Placement = pos=(0,0,0) rot=(0.57735,0.57735,0.57735;2.0944rad)
  sketch-geometry (18):
    g0: LineSegment StartX=-152.23 StartY=29.0049 StartZ=0 EndX=-143.23 EndY=29.0049 EndZ=0
    g1: LineSegment StartX=-152.23 StartY=29.0049 StartZ=0 EndX=-152.23 EndY=51.0049 EndZ=0
    g2: LineSegment StartX=-152.23 StartY=51.0049 StartZ=0 EndX=-130.23 EndY=51.0049 EndZ=0
    g3: LineSegment StartX=-130.23 StartY=51.0049 StartZ=0 EndX=-130.23 EndY=46.0049 EndZ=0
    g4: LineSegment StartX=-130.23 StartY=46.0049 StartZ=0 EndX=-143.23 EndY=46.0049 EndZ=0
    g5: Circle CenterX=-145.23 CenterY=31.0049 CenterZ=0 NormalX=0 NormalY=0 NormalZ=1 AngleXU=0 Radius=1
    g6: Circle CenterX=-145.23 CenterY=29.0049 CenterZ=0 NormalX=0 NormalY=0 NormalZ=1 AngleXU=0 Radius=1
    g7: Circle CenterX=-143.23 CenterY=29.0049 CenterZ=0 NormalX=0 NormalY=0 NormalZ=1 AngleXU=0 Radius=1
    g8: BSplineCurve PolesCount=3 KnotsCount=2 Degree=2 IsPeriodic=0
    g9: GeomPoint X=-145.23 Y=31.0049 Z=0
    g10: GeomPoint X=-143.23 Y=29.0049 Z=0
    g11: Circle CenterX=-145.23 CenterY=44.0049 CenterZ=0 NormalX=0 NormalY=0 NormalZ=1 AngleXU=0 Radius=1
    g12: Circle CenterX=-145.23 CenterY=46.0049 CenterZ=0 NormalX=0 NormalY=0 NormalZ=1 AngleXU=0 Radius=1
    g13: Circle CenterX=-143.23 CenterY=46.0049 CenterZ=0 NormalX=0 NormalY=0 NormalZ=1 AngleXU=0 Radius=1
    g14: BSplineCurve PolesCount=3 KnotsCount=2 Degree=2 IsPeriodic=0
    g15: GeomPoint X=-145.23 Y=44.0049 Z=0
    g16: GeomPoint X=-143.23 Y=46.0049 Z=0
    g17: LineSegment StartX=-145.23 StartY=44.0049 StartZ=0 EndX=-145.23 EndY=31.0049 EndZ=0
  constraints (40):
    c: Horizontal(g0)
    c: Distance(g0) = 9
    c: Coincident(g1,g0)
    c: Vertical(g1)
    c: Distance(g1) = 22
    c: Coincident(g2,g1)
    c: Horizontal(g2)
    c: Coincident(g3,g2)
    c: Vertical(g3)
    c: Distance(g3) = 5
    c: Coincident(g4,g3)
    c: Horizontal(g4)
    c: Distance(g4) = 13
    c: PointOnObject(g6,g0)
    c: Weight(g5) = 1
    c: Equal(g5,g6)
    c: Equal(g5,g7)
    c: Coincident(g8,g0)
    c: InternalAlignment(g5,g8)
    c: InternalAlignment(g6,g8)
    c: InternalAlignment(g7,g8)
    c: InternalAlignment(g9,g8)
    c: InternalAlignment(g10,g8)
    c: Weight(g11) = 1
    c: Equal(g11,g12)
    c: Equal(g11,g13)
    c: Coincident(g14,g4)
    c: InternalAlignment(g11,g14)
    c: InternalAlignment(g12,g14)
    c: InternalAlignment(g13,g14)
    c: InternalAlignment(g15,g14)
    c: InternalAlignment(g16,g14)
    c: Coincident(g17,g14)
    c: Coincident(g17,g8)
    c: Vertical(g17)
    c: Block(g4)
    c: Block(g17)
    c: Block(g14)
    c: Block(g8)
    c: Distance(g2) = 22
FEATURE [Part::Extrusion] Extrude029  label="laptopRetainer016"
  Base = -> Sketch028
  Dir = (1,0,0)
  DirMode = 2
  FaceMakerClass = Part::FaceMakerBullseye
  LengthFwd = 150
  LengthRev = 0
  Placement = pos=(107.08,50.35,-8.45) rot=(1,0,0;0.080285rad)
  Solid = true
  Symmetric = false
FEATURE [Part::Box] Box021  label="Cube012"
  AttacherType = Attacher::AttachEngine3D
  Height = 10
  Length = 40
  Placement = pos=(162.7,-101,0) rot=(0,0,1;0rad)
  Width = 4
FEATURE [Part::Fuse] Fusion015  label="laptopRetainer014"
  Base = -> Extrude029
  Tool = -> Box021
FEATURE [Part::Box] Box022  label="Cube013"
  AttacherType = Attacher::AttachEngine3D
  Height = 10
  Length = 10
  Placement = pos=(101,-102.5,12) rot=(1,0,0;0.080285rad)
  Width = 4
FEATURE [Part::Box] Box023  label="Cube014"
  AttacherType = Attacher::AttachEngine3D
  Height = 10
  Length = 10
  Placement = pos=(253,-102.5,12) rot=(1,0,0;0.080285rad)
  Width = 4
FEATURE [Part::MultiFuse] Fusion016  label="laptopRetainer015"
  Shapes = -> [Box023,Fusion015,Box022]
FEATURE [Part::Cut] Cut011  label="laptopRetainer017"
  Base = -> Fusion014
  Tool = -> Fusion016
FEATURE [Part::Cut] Cut012
  Base = -> Cut008
  Tool = -> Cut010
FEATURE [Part::Box] Box024  label="Cube015"
  AttacherType = Attacher::AttachEngine3D
  Height = 10
  Length = 40
  Placement = pos=(162.7,-101,0) rot=(0,0,1;0rad)
  Width = 4
FEATURE [Sketcher::SketchObject] Sketch029
  FullyConstrained = true
  Placement = pos=(0,0,0) rot=(0.57735,0.57735,0.57735;2.0944rad)
  sketch-geometry (18):
    g0: LineSegment StartX=-152.23 StartY=29.0049 StartZ=0 EndX=-143.23 EndY=29.0049 EndZ=0
    g1: LineSegment StartX=-152.23 StartY=29.0049 StartZ=0 EndX=-152.23 EndY=51.0049 EndZ=0
    g2: LineSegment StartX=-152.23 StartY=51.0049 StartZ=0 EndX=-130.23 EndY=51.0049 EndZ=0
    g3: LineSegment StartX=-130.23 StartY=51.0049 StartZ=0 EndX=-130.23 EndY=46.0049 EndZ=0
    g4: LineSegment StartX=-130.23 StartY=46.0049 StartZ=0 EndX=-143.23 EndY=46.0049 EndZ=0
    g5: Circle CenterX=-145.23 CenterY=31.0049 CenterZ=0 NormalX=0 NormalY=0 NormalZ=1 AngleXU=0 Radius=1
    g6: Circle CenterX=-145.23 CenterY=29.0049 CenterZ=0 NormalX=0 NormalY=0 NormalZ=1 AngleXU=0 Radius=1
    g7: Circle CenterX=-143.23 CenterY=29.0049 CenterZ=0 NormalX=0 NormalY=0 NormalZ=1 AngleXU=0 Radius=1
    g8: BSplineCurve PolesCount=3 KnotsCount=2 Degree=2 IsPeriodic=0
    g9: GeomPoint X=-145.23 Y=31.0049 Z=0
    g10: GeomPoint X=-143.23 Y=29.0049 Z=0
    g11: Circle CenterX=-145.23 CenterY=44.0049 CenterZ=0 NormalX=0 NormalY=0 NormalZ=1 AngleXU=0 Radius=1
    g12: Circle CenterX=-145.23 CenterY=46.0049 CenterZ=0 NormalX=0 NormalY=0 NormalZ=1 AngleXU=0 Radius=1
    g13: Circle CenterX=-143.23 CenterY=46.0049 CenterZ=0 NormalX=0 NormalY=0 NormalZ=1 AngleXU=0 Radius=1
    g14: BSplineCurve PolesCount=3 KnotsCount=2 Degree=2 IsPeriodic=0
    g15: GeomPoint X=-145.23 Y=44.0049 Z=0
    g16: GeomPoint X=-143.23 Y=46.0049 Z=0
    g17: LineSegment StartX=-145.23 StartY=44.0049 StartZ=0 EndX=-145.23 EndY=31.0049 EndZ=0
  constraints (40):
    c: Horizontal(g0)
    c: Distance(g0) = 9
    c: Coincident(g1,g0)
    c: Vertical(g1)
    c: Distance(g1) = 22
    c: Coincident(g2,g1)
    c: Horizontal(g2)
    c: Coincident(g3,g2)
    c: Vertical(g3)
    c: Distance(g3) = 5
    c: Coincident(g4,g3)
    c: Horizontal(g4)
    c: Distance(g4) = 13
    c: PointOnObject(g6,g0)
    c: Weight(g5) = 1
    c: Equal(g5,g6)
    c: Equal(g5,g7)
    c: Coincident(g8,g0)
    c: InternalAlignment(g5,g8)
    c: InternalAlignment(g6,g8)
    c: InternalAlignment(g7,g8)
    c: InternalAlignment(g9,g8)
    c: InternalAlignment(g10,g8)
    c: Weight(g11) = 1
    c: Equal(g11,g12)
    c: Equal(g11,g13)
    c: Coincident(g14,g4)
    c: InternalAlignment(g11,g14)
    c: InternalAlignment(g12,g14)
    c: InternalAlignment(g13,g14)
    c: InternalAlignment(g15,g14)
    c: InternalAlignment(g16,g14)
    c: Coincident(g17,g14)
    c: Coincident(g17,g8)
    c: Vertical(g17)
    c: Block(g4)
    c: Block(g17)
    c: Block(g14)
    c: Block(g8)
    c: Distance(g2) = 22
FEATURE [Part::Extrusion] Extrude030  label="laptopRetainer018"
  Base = -> Sketch029
  Dir = (1,0,0)
  DirMode = 2
  FaceMakerClass = Part::FaceMakerBullseye
  LengthFwd = 150
  LengthRev = 0
  Placement = pos=(107.08,50.35,-8.45) rot=(1,0,0;0.080285rad)
  Solid = true
  Symmetric = false
FEATURE [Part::Box] Box025  label="Cube016"
  AttacherType = Attacher::AttachEngine3D
  Height = 10
  Length = 10
  Placement = pos=(101,-102.5,12) rot=(1,0,0;0.080285rad)
  Width = 4
FEATURE [Part::Box] Box026  label="Cube017"
  AttacherType = Attacher::AttachEngine3D
  Height = 10
  Length = 10
  Placement = pos=(253,-102.5,12) rot=(1,0,0;0.080285rad)
  Width = 4
FEATURE [Part::Fuse] Fusion017  label="laptopRetainer019"
  Base = -> Extrude030
  Tool = -> Box024
FEATURE [Part::MultiFuse] Fusion018  label="laptopRetainer020"
  Shapes = -> [Box026,Fusion017,Box025]
FEATURE [Part::Cut] Cut013
  Base = -> Cut007
  Tool = -> Fusion013
FEATURE [Sketcher::SketchObject] Sketch030
  FullyConstrained = true
  Placement = pos=(0,0,0) rot=(0.57735,0.57735,0.57735;2.0944rad)
  sketch-geometry (18):
    g0: LineSegment StartX=-152.23 StartY=29.0049 StartZ=0 EndX=-143.23 EndY=29.0049 EndZ=0
    g1: LineSegment StartX=-152.23 StartY=29.0049 StartZ=0 EndX=-152.23 EndY=51.0049 EndZ=0
    g2: LineSegment StartX=-152.23 StartY=51.0049 StartZ=0 EndX=-130.23 EndY=51.0049 EndZ=0
    g3: LineSegment StartX=-130.23 StartY=51.0049 StartZ=0 EndX=-130.23 EndY=46.0049 EndZ=0
    g4: LineSegment StartX=-130.23 StartY=46.0049 StartZ=0 EndX=-143.23 EndY=46.0049 EndZ=0
    g5: Circle CenterX=-145.23 CenterY=31.0049 CenterZ=0 NormalX=0 NormalY=0 NormalZ=1 AngleXU=0 Radius=1
    g6: Circle CenterX=-145.23 CenterY=29.0049 CenterZ=0 NormalX=0 NormalY=0 NormalZ=1 AngleXU=0 Radius=1
    g7: Circle CenterX=-143.23 CenterY=29.0049 CenterZ=0 NormalX=0 NormalY=0 NormalZ=1 AngleXU=0 Radius=1
    g8: BSplineCurve PolesCount=3 KnotsCount=2 Degree=2 IsPeriodic=0
    g9: GeomPoint X=-145.23 Y=31.0049 Z=0
    g10: GeomPoint X=-143.23 Y=29.0049 Z=0
    g11: Circle CenterX=-145.23 CenterY=44.0049 CenterZ=0 NormalX=0 NormalY=0 NormalZ=1 AngleXU=0 Radius=1
    g12: Circle CenterX=-145.23 CenterY=46.0049 CenterZ=0 NormalX=0 NormalY=0 NormalZ=1 AngleXU=0 Radius=1
    g13: Circle CenterX=-143.23 CenterY=46.0049 CenterZ=0 NormalX=0 NormalY=0 NormalZ=1 AngleXU=0 Radius=1
    g14: BSplineCurve PolesCount=3 KnotsCount=2 Degree=2 IsPeriodic=0
    g15: GeomPoint X=-145.23 Y=44.0049 Z=0
    g16: GeomPoint X=-143.23 Y=46.0049 Z=0
    g17: LineSegment StartX=-145.23 StartY=44.0049 StartZ=0 EndX=-145.23 EndY=31.0049 EndZ=0
  constraints (40):
    c: Horizontal(g0)
    c: Distance(g0) = 9
    c: Coincident(g1,g0)
    c: Vertical(g1)
    c: Distance(g1) = 22
    c: Coincident(g2,g1)
    c: Horizontal(g2)
    c: Coincident(g3,g2)
    c: Vertical(g3)
    c: Distance(g3) = 5
    c: Coincident(g4,g3)
    c: Horizontal(g4)
    c: Distance(g4) = 13
    c: PointOnObject(g6,g0)
    c: Weight(g5) = 1
    c: Equal(g5,g6)
    c: Equal(g5,g7)
    c: Coincident(g8,g0)
    c: InternalAlignment(g5,g8)
    c: InternalAlignment(g6,g8)
    c: InternalAlignment(g7,g8)
    c: InternalAlignment(g9,g8)
    c: InternalAlignment(g10,g8)
    c: Weight(g11) = 1
    c: Equal(g11,g12)
    c: Equal(g11,g13)
    c: Coincident(g14,g4)
    c: InternalAlignment(g11,g14)
    c: InternalAlignment(g12,g14)
    c: InternalAlignment(g13,g14)
    c: InternalAlignment(g15,g14)
    c: InternalAlignment(g16,g14)
    c: Coincident(g17,g14)
    c: Coincident(g17,g8)
    c: Vertical(g17)
    c: Block(g4)
    c: Block(g17)
    c: Block(g14)
    c: Block(g8)
    c: Distance(g2) = 22
FEATURE [Sketcher::SketchObject] Sketch031
  FullyConstrained = true
  Placement = pos=(0,0,0) rot=(0.57735,0.57735,0.57735;2.0944rad)
  sketch-geometry (18):
    g0: LineSegment StartX=-152.23 StartY=29.0049 StartZ=0 EndX=-143.23 EndY=29.0049 EndZ=0
    g1: LineSegment StartX=-152.23 StartY=29.0049 StartZ=0 EndX=-152.23 EndY=51.0049 EndZ=0
    g2: LineSegment StartX=-152.23 StartY=51.0049 StartZ=0 EndX=-130.23 EndY=51.0049 EndZ=0
    g3: LineSegment StartX=-130.23 StartY=51.0049 StartZ=0 EndX=-130.23 EndY=46.0049 EndZ=0
    g4: LineSegment StartX=-130.23 StartY=46.0049 StartZ=0 EndX=-143.23 EndY=46.0049 EndZ=0
    g5: Circle CenterX=-145.23 CenterY=31.0049 CenterZ=0 NormalX=0 NormalY=0 NormalZ=1 AngleXU=0 Radius=1
    g6: Circle CenterX=-145.23 CenterY=29.0049 CenterZ=0 NormalX=0 NormalY=0 NormalZ=1 AngleXU=0 Radius=1
    g7: Circle CenterX=-143.23 CenterY=29.0049 CenterZ=0 NormalX=0 NormalY=0 NormalZ=1 AngleXU=0 Radius=1
    g8: BSplineCurve PolesCount=3 KnotsCount=2 Degree=2 IsPeriodic=0
    g9: GeomPoint X=-145.23 Y=31.0049 Z=0
    g10: GeomPoint X=-143.23 Y=29.0049 Z=0
    g11: Circle CenterX=-145.23 CenterY=44.0049 CenterZ=0 NormalX=0 NormalY=0 NormalZ=1 AngleXU=0 Radius=1
    g12: Circle CenterX=-145.23 CenterY=46.0049 CenterZ=0 NormalX=0 NormalY=0 NormalZ=1 AngleXU=0 Radius=1
    g13: Circle CenterX=-143.23 CenterY=46.0049 CenterZ=0 NormalX=0 NormalY=0 NormalZ=1 AngleXU=0 Radius=1
    g14: BSplineCurve PolesCount=3 KnotsCount=2 Degree=2 IsPeriodic=0
    g15: GeomPoint X=-145.23 Y=44.0049 Z=0
    g16: GeomPoint X=-143.23 Y=46.0049 Z=0
    g17: LineSegment StartX=-145.23 StartY=44.0049 StartZ=0 EndX=-145.23 EndY=31.0049 EndZ=0
  constraints (40):
    c: Horizontal(g0)
    c: Distance(g0) = 9
    c: Coincident(g1,g0)
    c: Vertical(g1)
    c: Distance(g1) = 22
    c: Coincident(g2,g1)
    c: Horizontal(g2)
    c: Coincident(g3,g2)
    c: Vertical(g3)
    c: Distance(g3) = 5
    c: Coincident(g4,g3)
    c: Horizontal(g4)
    c: Distance(g4) = 13
    c: PointOnObject(g6,g0)
    c: Weight(g5) = 1
    c: Equal(g5,g6)
    c: Equal(g5,g7)
    c: Coincident(g8,g0)
    c: InternalAlignment(g5,g8)
    c: InternalAlignment(g6,g8)
    c: InternalAlignment(g7,g8)
    c: InternalAlignment(g9,g8)
    c: InternalAlignment(g10,g8)
    c: Weight(g11) = 1
    c: Equal(g11,g12)
    c: Equal(g11,g13)
    c: Coincident(g14,g4)
    c: InternalAlignment(g11,g14)
    c: InternalAlignment(g12,g14)
    c: InternalAlignment(g13,g14)
    c: InternalAlignment(g15,g14)
    c: InternalAlignment(g16,g14)
    c: Coincident(g17,g14)
    c: Coincident(g17,g8)
    c: Vertical(g17)
    c: Block(g4)
    c: Block(g17)
    c: Block(g14)
    c: Block(g8)
    c: Distance(g2) = 22
FEATURE [Part::Extrusion] Extrude031  label="laptopRetainer022"
  Base = -> Sketch030
  Dir = (1,0,0)
  DirMode = 2
  FaceMakerClass = Part::FaceMakerBullseye
  LengthFwd = 150
  LengthRev = 0
  Placement = pos=(107.08,50.35,-8.45) rot=(1,0,0;0.080285rad)
  Solid = true
  Symmetric = false
FEATURE [Part::Extrusion] Extrude032  label="laptopRetainer023"
  Base = -> Sketch031
  Dir = (1,0,0)
  DirMode = 2
  FaceMakerClass = Part::FaceMakerBullseye
  LengthFwd = 150
  LengthRev = 0
  Placement = pos=(257.08,50.35,-8.45) rot=(1,0,0;0.080285rad)
  Solid = true
  Symmetric = false
FEATURE [Part::Box] Box027  label="Cube018"
  AttacherType = Attacher::AttachEngine3D
  Height = 10
  Length = 40
  Placement = pos=(162.7,-101,0) rot=(0,0,1;0rad)
  Width = 4
FEATURE [Part::Fuse] Fusion019  label="laptopRetainer021"
  Base = -> Extrude031
  Tool = -> Box027
FEATURE [Part::Box] Box028  label="Cube019"
  AttacherType = Attacher::AttachEngine3D
  Height = 10
  Length = 40
  Placement = pos=(312.07,-101,0) rot=(0,0,1;0rad)
  Width = 4
FEATURE [Part::Box] Box029  label="Cube020"
  AttacherType = Attacher::AttachEngine3D
  Height = 10
  Length = 10
  Placement = pos=(101,-102.5,12) rot=(1,0,0;0.080285rad)
  Width = 4
FEATURE [Part::MultiFuse] Fusion020  label="laptopRetainer024"
  Shapes = -> [Extrude032,Box028]
FEATURE [Part::Box] Box030  label="Cube021"
  AttacherType = Attacher::AttachEngine3D
  Height = 10
  Length = 10
  Placement = pos=(253,-102.5,12) rot=(1,0,0;0.080285rad)
  Width = 4
FEATURE [Part::MultiFuse] Fusion021  label="laptopRetainer025"
  Shapes = -> [Box030,Fusion019,Box029]
FEATURE [Part::Cut] Cut014  label="laptopRetainer026"
  Base = -> Fusion020
  Tool = -> Fusion021
FEATURE [Part::Cut] Cut015
  Base = -> Cut006
  Tool = -> Cut009
FEATURE [Sketcher::SketchObject] Sketch032  label="leftSideTop001"
  FullyConstrained = true
  sketch-geometry (89):
    g0: Circle CenterX=61.1495 CenterY=111.695 CenterZ=0 NormalX=0 NormalY=0 NormalZ=1 AngleXU=0 Radius=1
    g1: Circle CenterX=58.0728 CenterY=114.251 CenterZ=0 NormalX=0 NormalY=0 NormalZ=1 AngleXU=0 Radius=1
    g2: Circle CenterX=58.0728 CenterY=110.251 CenterZ=0 NormalX=0 NormalY=0 NormalZ=1 AngleXU=0 Radius=1
    g3: BSplineCurve PolesCount=3 KnotsCount=2 Degree=2 IsPeriodic=0
    g4: GeomPoint X=61.1495 Y=111.695 Z=0
    g5: GeomPoint X=58.0728 Y=110.251 Z=0
    g6: Circle CenterX=61.5791 CenterY=89.3511 CenterZ=0 NormalX=0 NormalY=0 NormalZ=1 AngleXU=0 Radius=1
    g7: Circle CenterX=58.0728 CenterY=91.2763 CenterZ=0 NormalX=0 NormalY=0 NormalZ=1 AngleXU=0 Radius=1
    g8: Circle CenterX=58.0728 CenterY=95.2763 CenterZ=0 NormalX=0 NormalY=0 NormalZ=1 AngleXU=0 Radius=1
    g9: BSplineCurve PolesCount=3 KnotsCount=2 Degree=2 IsPeriodic=0
    g10: GeomPoint X=61.5791 Y=89.3511 Z=0
    g11: GeomPoint X=58.0728 Y=95.2763 Z=0
    g12: Circle CenterX=62.0728 CenterY=124.221 CenterZ=0 NormalX=0 NormalY=0 NormalZ=1 AngleXU=0 Radius=1
    g13: Circle CenterX=58.0728 CenterY=124.221 CenterZ=0 NormalX=0 NormalY=0 NormalZ=1 AngleXU=0 Radius=1
    g14: Circle CenterX=61.1496 CenterY=121.665 CenterZ=0 NormalX=0 NormalY=0 NormalZ=1 AngleXU=0 Radius=1
    g15: BSplineCurve PolesCount=3 KnotsCount=2 Degree=2 IsPeriodic=0
    g16: GeomPoint X=62.0728 Y=124.221 Z=0
    g17: GeomPoint X=61.1496 Y=121.665 Z=0
    g18: Circle CenterX=61.5791 CenterY=75.4095 CenterZ=0 NormalX=0 NormalY=0 NormalZ=1 AngleXU=0 Radius=1
    g19: Circle CenterX=58.0728 CenterY=77.3346 CenterZ=0 NormalX=0 NormalY=0 NormalZ=1 AngleXU=0 Radius=1
    g20: Circle CenterX=58.0728 CenterY=73.3346 CenterZ=0 NormalX=0 NormalY=0 NormalZ=1 AngleXU=0 Radius=1
    g21: BSplineCurve PolesCount=3 KnotsCount=2 Degree=2 IsPeriodic=0
    g22: GeomPoint X=61.5791 Y=75.4095 Z=0
    g23: GeomPoint X=58.0728 Y=73.3346 Z=0
    g24: Circle CenterX=2.07281 CenterY=124.221 CenterZ=0 NormalX=0 NormalY=0 NormalZ=1 AngleXU=0 Radius=1
    g25: Circle CenterX=1.57905 CenterY=122.295 CenterZ=0 NormalX=0 NormalY=0 NormalZ=1 AngleXU=0 Radius=1
    g26: BSplineCurve PolesCount=3 KnotsCount=2 Degree=2 IsPeriodic=0
    g27: GeomPoint X=2.07281 Y=124.221 Z=0
    g28: GeomPoint X=1.57905 Y=122.295 Z=0
    g29: Circle CenterX=46.0728 CenterY=124.221 CenterZ=0 NormalX=0 NormalY=0 NormalZ=1 AngleXU=0 Radius=1
    g30: Circle CenterX=46.0728 CenterY=120.221 CenterZ=0 NormalX=0 NormalY=0 NormalZ=1 AngleXU=0 Radius=1
    g31: BSplineCurve PolesCount=3 KnotsCount=2 Degree=2 IsPeriodic=0
    g32: GeomPoint X=42.0728 Y=124.221 Z=0
    g33: GeomPoint X=46.0728 Y=120.221 Z=0
    g34-g38: Circle x5 (B-spline internal-alignment scaffolding for g39; pole/knot coordinates omitted)
    g39: BSplineCurve PolesCount=5 KnotsCount=3 Degree=3 IsPeriodic=0
    g40: GeomPoint X=132.072 Y=133.221 Z=0
    g41: GeomPoint X=141.072 Y=130.221 Z=0
    g42: GeomPoint X=132.072 Y=127.221 Z=0
    g43: ArcOfCircle CenterX=116.562 CenterY=52.0649 CenterZ=0 NormalX=0 NormalY=0 NormalZ=1 AngleXU=0 Radius=4.24264 StartAngle=0.283268 EndAngle=4.99566
    g44: LineSegment StartX=123.967 StartY=69.4706 StartZ=0 EndX=122.37 EndY=67.5474 EndZ=0
    g45: LineSegment StartX=117.293 StartY=71.7641 StartZ=0 EndX=115.591 EndY=69.7147 EndZ=0
    g46: LineSegment StartX=120.669 StartY=65.4973 StartZ=0 EndX=119.072 EndY=63.5741 EndZ=0
    g47: LineSegment StartX=124.73 StartY=54.6766 StartZ=0 EndX=123.265 EndY=51.8068 EndZ=0
    g48: LineSegment StartX=120.377 StartY=46.5474 StartZ=0 EndX=118.934 EndY=43.9178 EndZ=0
    g49: LineSegment StartX=61.5791 StartY=75.4095 StartZ=0 EndX=118.934 EndY=43.9178 EndZ=0
    g50: LineSegment StartX=117.748 StartY=47.9913 StartZ=0 EndX=120.377 EndY=46.5474 EndZ=0
    g51: LineSegment StartX=120.635 StartY=53.2507 StartZ=0 EndX=123.265 EndY=51.8068 EndZ=0
    g52: LineSegment StartX=124.73 StartY=54.6766 StartZ=0 EndX=61.5791 EndY=89.3511 EndZ=0
    g53: LineSegment StartX=58.0728 StartY=95.2763 StartZ=0 EndX=58.0728 EndY=110.251 EndZ=0
    g54: LineSegment StartX=61.1495 StartY=111.695 StartZ=0 EndX=119.072 EndY=63.5741 EndZ=0
    g55: LineSegment StartX=120.669 StartY=65.4973 StartZ=0 EndX=115.591 EndY=69.7147 EndZ=0
    g56: LineSegment StartX=117.293 StartY=71.7641 StartZ=0 EndX=122.37 EndY=67.5474 EndZ=0
    g57: LineSegment StartX=123.967 StartY=69.4706 StartZ=0 EndX=61.1496 EndY=121.665 EndZ=0
    g58: LineSegment StartX=62.0728 StartY=124.221 StartZ=0 EndX=132.072 EndY=124.221 EndZ=0
    g59: LineSegment StartX=132.072 StartY=127.221 StartZ=0 EndX=132.072 EndY=124.221 EndZ=0
    g60: LineSegment StartX=132.072 StartY=133.221 StartZ=0 EndX=132.072 EndY=136.221 EndZ=0
    g61: LineSegment StartX=132.072 StartY=136.221 StartZ=0 EndX=-42.9272 EndY=136.221 EndZ=0
    g62: LineSegment StartX=2.07281 StartY=124.221 StartZ=0 EndX=42.0728 EndY=124.221 EndZ=0
    g63: LineSegment StartX=-17.9272 StartY=48.2206 StartZ=0 EndX=-17.9272 EndY=58.2206 EndZ=0
    g64: LineSegment StartX=-35.9272 StartY=48.2206 StartZ=0 EndX=-35.9272 EndY=52.2206 EndZ=0
    g65: LineSegment StartX=-29.9272 StartY=48.2206 StartZ=0 EndX=-29.9272 EndY=52.2206 EndZ=0
    g66: LineSegment StartX=-23.9272 StartY=48.2206 StartZ=0 EndX=-23.9272 EndY=58.2206 EndZ=0
    g67: ArcOfCircle CenterX=-32.9272 CenterY=55.2206 CenterZ=0 NormalX=0 NormalY=0 NormalZ=1 AngleXU=0 Radius=4.24264 StartAngle=5.49779 EndAngle=10.2102
    g68: ArcOfCircle CenterX=-20.9272 CenterY=61.2206 CenterZ=0 NormalX=0 NormalY=0 NormalZ=1 AngleXU=0 Radius=4.24264 StartAngle=5.49779 EndAngle=10.2102
    g69: LineSegment StartX=-42.9272 StartY=48.2206 StartZ=0 EndX=-42.9272 EndY=136.221 EndZ=0
    g70: LineSegment StartX=58.0728 StartY=-27.5905 StartZ=0 EndX=58.0728 EndY=73.3346 EndZ=0
    g71: LineSegment StartX=50.0728 StartY=-27.5905 StartZ=0 EndX=50.0728 EndY=-31.5905 EndZ=0
    g72: LineSegment StartX=54.0728 StartY=-27.5905 StartZ=0 EndX=54.0728 EndY=-31.5905 EndZ=0
    g73: ArcOfCircle CenterX=52.0728 CenterY=-33.5905 CenterZ=0 NormalX=0 NormalY=0 NormalZ=1 AngleXU=0 Radius=2.82843 StartAngle=2.35619 EndAngle=7.06858
    g74: LineSegment StartX=54.0728 StartY=-27.5905 StartZ=0 EndX=58.0728 EndY=-27.5905 EndZ=0
    g75: LineSegment StartX=-17.9272 StartY=48.2206 StartZ=0 EndX=-10.9272 EndY=48.2206 EndZ=0
    g76: LineSegment StartX=-29.9272 StartY=48.2206 StartZ=0 EndX=-23.9272 EndY=48.2206 EndZ=0
    g77: LineSegment StartX=-42.9272 StartY=48.2206 StartZ=0 EndX=-35.9272 EndY=48.2206 EndZ=0
    g78: BSplineCurve PolesCount=3 KnotsCount=2 Degree=2 IsPeriodic=0
    g79: LineSegment StartX=46.0728 StartY=-27.5905 StartZ=0 EndX=46.0728 EndY=64.4095 EndZ=0
    g80: BSplineCurve PolesCount=3 KnotsCount=2 Degree=2 IsPeriodic=0
    g81: LineSegment StartX=-6.92718 StartY=68.4095 StartZ=0 EndX=42.0728 EndY=68.4095 EndZ=0
    g82: LineSegment StartX=-10.9272 StartY=64.4095 StartZ=0 EndX=-10.9272 EndY=48.2206 EndZ=0
    g83: LineSegment StartX=46.0728 StartY=-27.5905 StartZ=0 EndX=50.0728 EndY=-27.5905 EndZ=0
    g84: LineSegment StartX=46.0728 StartY=120.221 StartZ=0 EndX=46.0728 EndY=113.861 EndZ=0
    g85: BSplineCurve PolesCount=3 KnotsCount=2 Degree=2 IsPeriodic=0
    g86: LineSegment StartX=42.0728 StartY=109.861 StartZ=0 EndX=35.5028 EndY=109.861 EndZ=0
    g87: BSplineCurve PolesCount=3 KnotsCount=2 Degree=2 IsPeriodic=0
    g88: LineSegment StartX=1.57905 StartY=122.295 StartZ=0 EndX=27.9965 EndY=111.786 EndZ=0
  constraints (158):
    c: Weight(g0) = 1
    c: Equal(g0,g1)
    c: Equal(g0,g2)
    c: InternalAlignment(g0,g3)
    c: InternalAlignment(g1,g3)
    c: InternalAlignment(g2,g3)
    c: InternalAlignment(g4,g3)
    c: InternalAlignment(g5,g3)
    c: Weight(g6) = 1
    c: Equal(g6,g7)
    c: Equal(g6,g8)
    c: InternalAlignment(g6,g9)
    c: InternalAlignment(g7,g9)
    c: InternalAlignment(g8,g9)
    c: InternalAlignment(g10,g9)
    c: InternalAlignment(g11,g9)
    c: Block(g3)
    c: Block(g9)
    c: Weight(g12) = 1
    c: Equal(g12,g13)
    c: Equal(g12,g14)
    c: InternalAlignment(g12,g15)
    c: InternalAlignment(g13,g15)
    c: InternalAlignment(g14,g15)
    c: InternalAlignment(g16,g15)
    c: InternalAlignment(g17,g15)
    c: Block(g15)
    c: Weight(g18) = 1
    c: Equal(g18,g19)
    c: Equal(g18,g20)
    c: InternalAlignment(g18,g21)
    c: InternalAlignment(g19,g21)
    c: InternalAlignment(g20,g21)
    c: InternalAlignment(g22,g21)
    c: InternalAlignment(g23,g21)
    c: Block(g21)
    c: Weight(g24) = 1
    c: Equal(g24,g25)
    c: InternalAlignment(g24,g26)
    c: InternalAlignment(g25,g26)
    c: InternalAlignment(g27,g26)
    c: InternalAlignment(g28,g26)
    c: InternalAlignment(g29,g31)
    c: InternalAlignment(g30,g31)
    c: InternalAlignment(g32,g31)
    c: InternalAlignment(g33,g31)
    c: Block(g31)
    c: Block(g26)
    c: Weight(g34) = 1
    c: Equal(g34, g35-g38) x4
    c: InternalAlignment(g34-g38 -> g39) x5
    c: InternalAlignment(g40,g39)
    c: InternalAlignment(g41,g39)
    c: InternalAlignment(g42,g39)
    c: Block(g39)
    c: Block(g43)
    c: Block(g44)
    c: Block(g45)
    c: Block(g46)
    c: Block(g47)
    c: Block(g48)
    c: Coincident(g70,g21)
    c: Coincident(g49,g21)
    c: Coincident(g49,g48)
    c: Coincident(g50,g43)
    c: Coincident(g50,g48)
    c: Coincident(g51,g43)
    c: Coincident(g51,g47)
    c: Coincident(g52,g47)
    c: Coincident(g52,g9)
    c: Coincident(g53,g9)
    c: Coincident(g53,g3)
    c: Vertical(g53)
    c: Coincident(g54,g3)
    c: Coincident(g54,g46)
    c: Coincident(g55,g46)
    c: Coincident(g55,g45)
    c: Coincident(g56,g45)
    c: Coincident(g56,g44)
    c: Coincident(g57,g44)
    c: Coincident(g57,g15)
    c: Coincident(g58,g15)
    c: Horizontal(g58)
    c: Coincident(g59,g39)
    c: Coincident(g59,g58)
    c: Vertical(g59)
    c: Coincident(g60,g39)
    c: Vertical(g60)
    c: Coincident(g61,g60)
    c: Horizontal(g61)
    c: Coincident(g62,g26)
    c: Coincident(g62,g31)
    c: Horizontal(g62)
    c: Vertical(g63)
    c: Distance(g63) = 10
    c: Vertical(g64)
    c: Distance(g64) = 4
    c: Vertical(g65)
    c: Distance(g65) = 4
    c: Vertical(g66)
    c: Distance(g66) = 10
    c: Coincident(g67,g65)
    c: Coincident(g67,g64)
    c: Block(g67)
    c: Coincident(g68,g66)
    c: Coincident(g68,g63)
    c: Block(g68)
    c: Coincident(g69,g61)
    c: Vertical(g69)
    c: Block(g61)
    c: Block(g70)
    c: Vertical(g71)
    c: Distance(g71) = 4
    c: Vertical(g72)
    c: Distance(g72) = 4
    c: Coincident(g73,g71)
    c: Coincident(g73,g72)
    c: Block(g73)
    c: Coincident(g74,g72)
    c: Coincident(g74,g70)
    c: Horizontal(g74)
    c: Distance(g74) = 4
    c: Block(g69)
    c: Coincident(g75,g63)
    c: Horizontal(g75)
    c: Coincident(g76,g65)
    c: Coincident(g76,g66)
    c: Horizontal(g76)
    c: Coincident(g77,g69)
    c: Coincident(g77,g64)
    c: Horizontal(g77)
    c: Block(g78)
    c: Vertical(g79)
    c: Distance(g79) = 92
    c: Block(g80)
    c: Coincident(g80,g79)
    c: Coincident(g81,g78)
    c: Coincident(g81,g80)
    c: Horizontal(g81)
    c: Coincident(g82,g78)
    c: Coincident(g82,g75)
    c: Vertical(g82)
    c: Coincident(g83,g79)
    c: Coincident(g83,g71)
    c: Horizontal(g83)
    c: Coincident(g84,g31)
    c: Vertical(g84)
    c: Distance(g84) = 6.36
    c: Block(g85)
    c: Coincident(g85,g84)
    c: Horizontal(g86)
    c: Coincident(g86,g85)
    c: Block(g87)
    c: Coincident(g87,g86)
    c: Coincident(g88,g26)
    c: Coincident(g88,g87)
    c: Distance(g61) = 174.999
    c: Distance(g61) = 174.999
FEATURE [Part::Extrusion] Extrude033
  Base = -> Sketch032
  Dir = (0,0,1)
  DirMode = 2
  FaceMakerClass = Part::FaceMakerBullseye
  LengthFwd = 28
  LengthRev = 0
  Solid = true
  Symmetric = false
FEATURE [Part::Box] Box031  label="removeFromtTop006"
  AttacherType = Attacher::AttachEngine3D
  Height = 56
  Length = 470
  Placement = pos=(-47.93,-106.78,8) rot=(1,0,0;0.080285rad)
  Width = 260
FEATURE [Part::Cut] Cut016
  Base = -> Extrude033
  Tool = -> Box031
FEATURE [Part::Cut] Cut017  label="legBraceLeft"
  Base = -> Extrude013
  Tool = -> Cut
FEATURE [Sketcher::SketchObject] Sketch033  label="leftSideTop002"
  FullyConstrained = true
  sketch-geometry (89):
    g0: Circle CenterX=61.1495 CenterY=111.695 CenterZ=0 NormalX=0 NormalY=0 NormalZ=1 AngleXU=0 Radius=1
    g1: Circle CenterX=58.0728 CenterY=114.251 CenterZ=0 NormalX=0 NormalY=0 NormalZ=1 AngleXU=0 Radius=1
    g2: Circle CenterX=58.0728 CenterY=110.251 CenterZ=0 NormalX=0 NormalY=0 NormalZ=1 AngleXU=0 Radius=1
    g3: BSplineCurve PolesCount=3 KnotsCount=2 Degree=2 IsPeriodic=0
    g4: GeomPoint X=61.1495 Y=111.695 Z=0
    g5: GeomPoint X=58.0728 Y=110.251 Z=0
    g6: Circle CenterX=61.5791 CenterY=89.3511 CenterZ=0 NormalX=0 NormalY=0 NormalZ=1 AngleXU=0 Radius=1
    g7: Circle CenterX=58.0728 CenterY=91.2763 CenterZ=0 NormalX=0 NormalY=0 NormalZ=1 AngleXU=0 Radius=1
    g8: Circle CenterX=58.0728 CenterY=95.2763 CenterZ=0 NormalX=0 NormalY=0 NormalZ=1 AngleXU=0 Radius=1
    g9: BSplineCurve PolesCount=3 KnotsCount=2 Degree=2 IsPeriodic=0
    g10: GeomPoint X=61.5791 Y=89.3511 Z=0
    g11: GeomPoint X=58.0728 Y=95.2763 Z=0
    g12: Circle CenterX=62.0728 CenterY=124.221 CenterZ=0 NormalX=0 NormalY=0 NormalZ=1 AngleXU=0 Radius=1
    g13: Circle CenterX=58.0728 CenterY=124.221 CenterZ=0 NormalX=0 NormalY=0 NormalZ=1 AngleXU=0 Radius=1
    g14: Circle CenterX=61.1496 CenterY=121.665 CenterZ=0 NormalX=0 NormalY=0 NormalZ=1 AngleXU=0 Radius=1
    g15: BSplineCurve PolesCount=3 KnotsCount=2 Degree=2 IsPeriodic=0
    g16: GeomPoint X=62.0728 Y=124.221 Z=0
    g17: GeomPoint X=61.1496 Y=121.665 Z=0
    g18: Circle CenterX=61.5791 CenterY=75.4095 CenterZ=0 NormalX=0 NormalY=0 NormalZ=1 AngleXU=0 Radius=1
    g19: Circle CenterX=58.0728 CenterY=77.3346 CenterZ=0 NormalX=0 NormalY=0 NormalZ=1 AngleXU=0 Radius=1
    g20: Circle CenterX=58.0728 CenterY=73.3346 CenterZ=0 NormalX=0 NormalY=0 NormalZ=1 AngleXU=0 Radius=1
    g21: BSplineCurve PolesCount=3 KnotsCount=2 Degree=2 IsPeriodic=0
    g22: GeomPoint X=61.5791 Y=75.4095 Z=0
    g23: GeomPoint X=58.0728 Y=73.3346 Z=0
    g24: Circle CenterX=2.07281 CenterY=124.221 CenterZ=0 NormalX=0 NormalY=0 NormalZ=1 AngleXU=0 Radius=1
    g25: Circle CenterX=1.57905 CenterY=122.295 CenterZ=0 NormalX=0 NormalY=0 NormalZ=1 AngleXU=0 Radius=1
    g26: BSplineCurve PolesCount=3 KnotsCount=2 Degree=2 IsPeriodic=0
    g27: GeomPoint X=2.07281 Y=124.221 Z=0
    g28: GeomPoint X=1.57905 Y=122.295 Z=0
    g29: Circle CenterX=46.0728 CenterY=124.221 CenterZ=0 NormalX=0 NormalY=0 NormalZ=1 AngleXU=0 Radius=1
    g30: Circle CenterX=46.0728 CenterY=120.221 CenterZ=0 NormalX=0 NormalY=0 NormalZ=1 AngleXU=0 Radius=1
    g31: BSplineCurve PolesCount=3 KnotsCount=2 Degree=2 IsPeriodic=0
    g32: GeomPoint X=42.0728 Y=124.221 Z=0
    g33: GeomPoint X=46.0728 Y=120.221 Z=0
    g34-g38: Circle x5 (B-spline internal-alignment scaffolding for g39; pole/knot coordinates omitted)
    g39: BSplineCurve PolesCount=5 KnotsCount=3 Degree=3 IsPeriodic=0
    g40: GeomPoint X=132.072 Y=133.221 Z=0
    g41: GeomPoint X=141.072 Y=130.221 Z=0
    g42: GeomPoint X=132.072 Y=127.221 Z=0
    g43: ArcOfCircle CenterX=116.562 CenterY=52.0649 CenterZ=0 NormalX=0 NormalY=0 NormalZ=1 AngleXU=0 Radius=4.24264 StartAngle=0.283268 EndAngle=4.99566
    g44: LineSegment StartX=123.967 StartY=69.4706 StartZ=0 EndX=122.37 EndY=67.5474 EndZ=0
    g45: LineSegment StartX=117.293 StartY=71.7641 StartZ=0 EndX=115.591 EndY=69.7147 EndZ=0
    g46: LineSegment StartX=120.669 StartY=65.4973 StartZ=0 EndX=119.072 EndY=63.5741 EndZ=0
    g47: LineSegment StartX=124.73 StartY=54.6766 StartZ=0 EndX=123.265 EndY=51.8068 EndZ=0
    g48: LineSegment StartX=120.377 StartY=46.5474 StartZ=0 EndX=118.934 EndY=43.9178 EndZ=0
    g49: LineSegment StartX=61.5791 StartY=75.4095 StartZ=0 EndX=118.934 EndY=43.9178 EndZ=0
    g50: LineSegment StartX=117.748 StartY=47.9913 StartZ=0 EndX=120.377 EndY=46.5474 EndZ=0
    g51: LineSegment StartX=120.635 StartY=53.2507 StartZ=0 EndX=123.265 EndY=51.8068 EndZ=0
    g52: LineSegment StartX=124.73 StartY=54.6766 StartZ=0 EndX=61.5791 EndY=89.3511 EndZ=0
    g53: LineSegment StartX=58.0728 StartY=95.2763 StartZ=0 EndX=58.0728 EndY=110.251 EndZ=0
    g54: LineSegment StartX=61.1495 StartY=111.695 StartZ=0 EndX=119.072 EndY=63.5741 EndZ=0
    g55: LineSegment StartX=120.669 StartY=65.4973 StartZ=0 EndX=115.591 EndY=69.7147 EndZ=0
    g56: LineSegment StartX=117.293 StartY=71.7641 StartZ=0 EndX=122.37 EndY=67.5474 EndZ=0
    g57: LineSegment StartX=123.967 StartY=69.4706 StartZ=0 EndX=61.1496 EndY=121.665 EndZ=0
    g58: LineSegment StartX=62.0728 StartY=124.221 StartZ=0 EndX=132.072 EndY=124.221 EndZ=0
    g59: LineSegment StartX=132.072 StartY=127.221 StartZ=0 EndX=132.072 EndY=124.221 EndZ=0
    g60: LineSegment StartX=132.072 StartY=133.221 StartZ=0 EndX=132.072 EndY=136.221 EndZ=0
    g61: LineSegment StartX=132.072 StartY=136.221 StartZ=0 EndX=-42.9272 EndY=136.221 EndZ=0
    g62: LineSegment StartX=2.07281 StartY=124.221 StartZ=0 EndX=42.0728 EndY=124.221 EndZ=0
    g63: LineSegment StartX=-17.9272 StartY=48.2206 StartZ=0 EndX=-17.9272 EndY=58.2206 EndZ=0
    g64: LineSegment StartX=-35.9272 StartY=48.2206 StartZ=0 EndX=-35.9272 EndY=52.2206 EndZ=0
    g65: LineSegment StartX=-29.9272 StartY=48.2206 StartZ=0 EndX=-29.9272 EndY=52.2206 EndZ=0
    g66: LineSegment StartX=-23.9272 StartY=48.2206 StartZ=0 EndX=-23.9272 EndY=58.2206 EndZ=0
    g67: ArcOfCircle CenterX=-32.9272 CenterY=55.2206 CenterZ=0 NormalX=0 NormalY=0 NormalZ=1 AngleXU=0 Radius=4.24264 StartAngle=5.49779 EndAngle=10.2102
    g68: ArcOfCircle CenterX=-20.9272 CenterY=61.2206 CenterZ=0 NormalX=0 NormalY=0 NormalZ=1 AngleXU=0 Radius=4.24264 StartAngle=5.49779 EndAngle=10.2102
    g69: LineSegment StartX=-42.9272 StartY=48.2206 StartZ=0 EndX=-42.9272 EndY=136.221 EndZ=0
    g70: LineSegment StartX=58.0728 StartY=-27.5905 StartZ=0 EndX=58.0728 EndY=73.3346 EndZ=0
    g71: LineSegment StartX=50.0728 StartY=-27.5905 StartZ=0 EndX=50.0728 EndY=-31.5905 EndZ=0
    g72: LineSegment StartX=54.0728 StartY=-27.5905 StartZ=0 EndX=54.0728 EndY=-31.5905 EndZ=0
    g73: ArcOfCircle CenterX=52.0728 CenterY=-33.5905 CenterZ=0 NormalX=0 NormalY=0 NormalZ=1 AngleXU=0 Radius=2.82843 StartAngle=2.35619 EndAngle=7.06858
    g74: LineSegment StartX=54.0728 StartY=-27.5905 StartZ=0 EndX=58.0728 EndY=-27.5905 EndZ=0
    g75: LineSegment StartX=-17.9272 StartY=48.2206 StartZ=0 EndX=-10.9272 EndY=48.2206 EndZ=0
    g76: LineSegment StartX=-29.9272 StartY=48.2206 StartZ=0 EndX=-23.9272 EndY=48.2206 EndZ=0
    g77: LineSegment StartX=-42.9272 StartY=48.2206 StartZ=0 EndX=-35.9272 EndY=48.2206 EndZ=0
    g78: BSplineCurve PolesCount=3 KnotsCount=2 Degree=2 IsPeriodic=0
    g79: LineSegment StartX=46.0728 StartY=-27.5905 StartZ=0 EndX=46.0728 EndY=64.4095 EndZ=0
    g80: BSplineCurve PolesCount=3 KnotsCount=2 Degree=2 IsPeriodic=0
    g81: LineSegment StartX=-6.92718 StartY=68.4095 StartZ=0 EndX=42.0728 EndY=68.4095 EndZ=0
    g82: LineSegment StartX=-10.9272 StartY=64.4095 StartZ=0 EndX=-10.9272 EndY=48.2206 EndZ=0
    g83: LineSegment StartX=46.0728 StartY=-27.5905 StartZ=0 EndX=50.0728 EndY=-27.5905 EndZ=0
    g84: LineSegment StartX=46.0728 StartY=120.221 StartZ=0 EndX=46.0728 EndY=113.861 EndZ=0
    g85: BSplineCurve PolesCount=3 KnotsCount=2 Degree=2 IsPeriodic=0
    g86: LineSegment StartX=42.0728 StartY=109.861 StartZ=0 EndX=35.5028 EndY=109.861 EndZ=0
    g87: BSplineCurve PolesCount=3 KnotsCount=2 Degree=2 IsPeriodic=0
    g88: LineSegment StartX=1.57905 StartY=122.295 StartZ=0 EndX=27.9965 EndY=111.786 EndZ=0
  constraints (158):
    c: Weight(g0) = 1
    c: Equal(g0,g1)
    c: Equal(g0,g2)
    c: InternalAlignment(g0,g3)
    c: InternalAlignment(g1,g3)
    c: InternalAlignment(g2,g3)
    c: InternalAlignment(g4,g3)
    c: InternalAlignment(g5,g3)
    c: Weight(g6) = 1
    c: Equal(g6,g7)
    c: Equal(g6,g8)
    c: InternalAlignment(g6,g9)
    c: InternalAlignment(g7,g9)
    c: InternalAlignment(g8,g9)
    c: InternalAlignment(g10,g9)
    c: InternalAlignment(g11,g9)
    c: Block(g3)
    c: Block(g9)
    c: Weight(g12) = 1
    c: Equal(g12,g13)
    c: Equal(g12,g14)
    c: InternalAlignment(g12,g15)
    c: InternalAlignment(g13,g15)
    c: InternalAlignment(g14,g15)
    c: InternalAlignment(g16,g15)
    c: InternalAlignment(g17,g15)
    c: Block(g15)
    c: Weight(g18) = 1
    c: Equal(g18,g19)
    c: Equal(g18,g20)
    c: InternalAlignment(g18,g21)
    c: InternalAlignment(g19,g21)
    c: InternalAlignment(g20,g21)
    c: InternalAlignment(g22,g21)
    c: InternalAlignment(g23,g21)
    c: Block(g21)
    c: Weight(g24) = 1
    c: Equal(g24,g25)
    c: InternalAlignment(g24,g26)
    c: InternalAlignment(g25,g26)
    c: InternalAlignment(g27,g26)
    c: InternalAlignment(g28,g26)
    c: InternalAlignment(g29,g31)
    c: InternalAlignment(g30,g31)
    c: InternalAlignment(g32,g31)
    c: InternalAlignment(g33,g31)
    c: Block(g31)
    c: Block(g26)
    c: Weight(g34) = 1
    c: Equal(g34, g35-g38) x4
    c: InternalAlignment(g34-g38 -> g39) x5
    c: InternalAlignment(g40,g39)
    c: InternalAlignment(g41,g39)
    c: InternalAlignment(g42,g39)
    c: Block(g39)
    c: Block(g43)
    c: Block(g44)
    c: Block(g45)
    c: Block(g46)
    c: Block(g47)
    c: Block(g48)
    c: Coincident(g70,g21)
    c: Coincident(g49,g21)
    c: Coincident(g49,g48)
    c: Coincident(g50,g43)
    c: Coincident(g50,g48)
    c: Coincident(g51,g43)
    c: Coincident(g51,g47)
    c: Coincident(g52,g47)
    c: Coincident(g52,g9)
    c: Coincident(g53,g9)
    c: Coincident(g53,g3)
    c: Vertical(g53)
    c: Coincident(g54,g3)
    c: Coincident(g54,g46)
    c: Coincident(g55,g46)
    c: Coincident(g55,g45)
    c: Coincident(g56,g45)
    c: Coincident(g56,g44)
    c: Coincident(g57,g44)
    c: Coincident(g57,g15)
    c: Coincident(g58,g15)
    c: Horizontal(g58)
    c: Coincident(g59,g39)
    c: Coincident(g59,g58)
    c: Vertical(g59)
    c: Coincident(g60,g39)
    c: Vertical(g60)
    c: Coincident(g61,g60)
    c: Horizontal(g61)
    c: Coincident(g62,g26)
    c: Coincident(g62,g31)
    c: Horizontal(g62)
    c: Vertical(g63)
    c: Distance(g63) = 10
    c: Vertical(g64)
    c: Distance(g64) = 4
    c: Vertical(g65)
    c: Distance(g65) = 4
    c: Vertical(g66)
    c: Distance(g66) = 10
    c: Coincident(g67,g65)
    c: Coincident(g67,g64)
    c: Block(g67)
    c: Coincident(g68,g66)
    c: Coincident(g68,g63)
    c: Block(g68)
    c: Coincident(g69,g61)
    c: Vertical(g69)
    c: Block(g61)
    c: Block(g70)
    c: Vertical(g71)
    c: Distance(g71) = 4
    c: Vertical(g72)
    c: Distance(g72) = 4
    c: Coincident(g73,g71)
    c: Coincident(g73,g72)
    c: Block(g73)
    c: Coincident(g74,g72)
    c: Coincident(g74,g70)
    c: Horizontal(g74)
    c: Distance(g74) = 4
    c: Block(g69)
    c: Coincident(g75,g63)
    c: Horizontal(g75)
    c: Coincident(g76,g65)
    c: Coincident(g76,g66)
    c: Horizontal(g76)
    c: Coincident(g77,g69)
    c: Coincident(g77,g64)
    c: Horizontal(g77)
    c: Block(g78)
    c: Vertical(g79)
    c: Distance(g79) = 92
    c: Block(g80)
    c: Coincident(g80,g79)
    c: Coincident(g81,g78)
    c: Coincident(g81,g80)
    c: Horizontal(g81)
    c: Coincident(g82,g78)
    c: Coincident(g82,g75)
    c: Vertical(g82)
    c: Coincident(g83,g79)
    c: Coincident(g83,g71)
    c: Horizontal(g83)
    c: Coincident(g84,g31)
    c: Vertical(g84)
    c: Distance(g84) = 6.36
    c: Block(g85)
    c: Coincident(g85,g84)
    c: Horizontal(g86)
    c: Coincident(g86,g85)
    c: Block(g87)
    c: Coincident(g87,g86)
    c: Coincident(g88,g26)
    c: Coincident(g88,g87)
    c: Distance(g61) = 174.999
    c: Distance(g61) = 174.999
FEATURE [Part::Extrusion] Extrude034
  Base = -> Sketch033
  Dir = (0,0,1)
  DirMode = 2
  FaceMakerClass = Part::FaceMakerBullseye
  LengthFwd = 28
  LengthRev = 0
  Solid = true
  Symmetric = false
FEATURE [Part::Box] Box032  label="removeFromtTop007"
  AttacherType = Attacher::AttachEngine3D
  Height = 56
  Length = 470
  Placement = pos=(-47.93,-106.78,8) rot=(1,0,0;0.080285rad)
  Width = 260
FEATURE [Part::Cut] Cut018
  Base = -> Extrude034
  Tool = -> Box032
FEATURE [Part::Cut] Cut019  label="legBraceLeft001"
  Base = -> Extrude
  Tool = -> Cut016
FEATURE [Sketcher::SketchObject] Sketch034  label="rightSideTop001"
  FullyConstrained = false
  sketch-geometry (93):
    g0: Circle CenterX=302.996 CenterY=111.695 CenterZ=0 NormalX=0 NormalY=0 NormalZ=1 AngleXU=0 Radius=1
    g1: Circle CenterX=306.073 CenterY=114.251 CenterZ=0 NormalX=0 NormalY=0 NormalZ=1 AngleXU=0 Radius=1
    g2: Circle CenterX=306.073 CenterY=110.251 CenterZ=0 NormalX=0 NormalY=0 NormalZ=1 AngleXU=0 Radius=1
    g3: BSplineCurve PolesCount=3 KnotsCount=2 Degree=2 IsPeriodic=0
    g4: GeomPoint X=302.996 Y=111.695 Z=0
    g5: GeomPoint X=306.073 Y=110.251 Z=0
    g6: Circle CenterX=306.073 CenterY=95.2763 CenterZ=0 NormalX=0 NormalY=0 NormalZ=1 AngleXU=0 Radius=1
    g7: Circle CenterX=306.073 CenterY=91.2763 CenterZ=0 NormalX=0 NormalY=0 NormalZ=1 AngleXU=0 Radius=1
    g8: Circle CenterX=302.567 CenterY=89.3511 CenterZ=0 NormalX=0 NormalY=0 NormalZ=1 AngleXU=0 Radius=1
    g9: BSplineCurve PolesCount=3 KnotsCount=2 Degree=2 IsPeriodic=0
    g10: GeomPoint X=306.073 Y=95.2763 Z=0
    g11: GeomPoint X=302.567 Y=89.3511 Z=0
    g12: LineSegment StartX=306.073 StartY=110.251 StartZ=0 EndX=306.073 EndY=95.2763 EndZ=0
    g13: Circle CenterX=302.073 CenterY=124.221 CenterZ=0 NormalX=0 NormalY=0 NormalZ=1 AngleXU=0 Radius=1
    g14: Circle CenterX=306.073 CenterY=124.221 CenterZ=0 NormalX=0 NormalY=0 NormalZ=1 AngleXU=0 Radius=1
    g15: Circle CenterX=302.996 CenterY=121.665 CenterZ=0 NormalX=0 NormalY=0 NormalZ=1 AngleXU=0 Radius=1
    g16: BSplineCurve PolesCount=3 KnotsCount=2 Degree=2 IsPeriodic=0
    g17: GeomPoint X=302.073 Y=124.221 Z=0
    g18: GeomPoint X=302.996 Y=121.665 Z=0
    g19: Circle CenterX=306.073 CenterY=73.3346 CenterZ=0 NormalX=0 NormalY=0 NormalZ=1 AngleXU=0 Radius=1
    g20: Circle CenterX=306.073 CenterY=77.3346 CenterZ=0 NormalX=0 NormalY=0 NormalZ=1 AngleXU=0 Radius=1
    g21: Circle CenterX=302.535 CenterY=75.4095 CenterZ=0 NormalX=0 NormalY=0 NormalZ=1 AngleXU=0 Radius=1
    g22: BSplineCurve PolesCount=3 KnotsCount=2 Degree=2 IsPeriodic=0
    g23: GeomPoint X=306.073 Y=73.3346 Z=0
    g24: GeomPoint X=302.535 Y=75.4095 Z=0
    g25: Circle CenterX=362.073 CenterY=124.221 CenterZ=0 NormalX=0 NormalY=0 NormalZ=1 AngleXU=0 Radius=1
    g26: Circle CenterX=366.073 CenterY=124.221 CenterZ=0 NormalX=0 NormalY=0 NormalZ=1 AngleXU=0 Radius=1
    g27: Circle CenterX=362.567 CenterY=122.294 CenterZ=0 NormalX=0 NormalY=0 NormalZ=1 AngleXU=0 Radius=1
    g28: BSplineCurve PolesCount=3 KnotsCount=2 Degree=2 IsPeriodic=0
    g29: GeomPoint X=362.073 Y=124.221 Z=0
    g30: GeomPoint X=362.567 Y=122.294 Z=0
    g31: Circle CenterX=322.073 CenterY=124.221 CenterZ=0 NormalX=0 NormalY=0 NormalZ=1 AngleXU=0 Radius=1
    g32: Circle CenterX=318.073 CenterY=124.221 CenterZ=0 NormalX=0 NormalY=0 NormalZ=1 AngleXU=0 Radius=1
    g33: Circle CenterX=318.073 CenterY=120.221 CenterZ=0 NormalX=0 NormalY=0 NormalZ=1 AngleXU=0 Radius=1
    g34: BSplineCurve PolesCount=3 KnotsCount=2 Degree=2 IsPeriodic=0
    g35: GeomPoint X=322.073 Y=124.221 Z=0
    g36: GeomPoint X=318.073 Y=120.221 Z=0
    g37: Circle CenterX=318.073 CenterY=109.865 CenterZ=0 NormalX=0 NormalY=0 NormalZ=1 AngleXU=0 Radius=1
    g38: GeomPoint X=318.073 Y=109.865 Z=0
    g39: Circle CenterX=322.073 CenterY=76.4095 CenterZ=0 NormalX=0 NormalY=0 NormalZ=1 AngleXU=0 Radius=4
    g40: Circle CenterX=232.072 CenterY=133.221 CenterZ=0 NormalX=0 NormalY=0 NormalZ=1 AngleXU=0 Radius=1
    g41: Circle CenterX=226.072 CenterY=136.221 CenterZ=0 NormalX=0 NormalY=0 NormalZ=1 AngleXU=0 Radius=1
    g42: Circle CenterX=226.072 CenterY=124.221 CenterZ=0 NormalX=0 NormalY=0 NormalZ=1 AngleXU=0 Radius=1
    g43: Circle CenterX=232.072 CenterY=127.221 CenterZ=0 NormalX=0 NormalY=0 NormalZ=1 AngleXU=0 Radius=1
    g44: BSplineCurve PolesCount=5 KnotsCount=3 Degree=3 IsPeriodic=0
    g45: GeomPoint X=232.072 Y=133.221 Z=0
    g46: GeomPoint X=223.072 Y=130.221 Z=0
    g47: GeomPoint X=232.072 Y=127.221 Z=0
    g48: LineSegment StartX=240.687 StartY=51.8263 StartZ=0 EndX=243.317 EndY=53.2701 EndZ=0
    g49: LineSegment StartX=243.575 StartY=46.5669 StartZ=0 EndX=246.205 EndY=48.0108 EndZ=0
    g50: ArcOfCircle CenterX=247.391 CenterY=52.0843 CenterZ=0 NormalX=0 NormalY=0 NormalZ=1 AngleXU=0 Radius=4.24264 StartAngle=4.42912 EndAngle=9.14151
    g51: LineSegment StartX=243.475 StartY=65.4951 StartZ=0 EndX=245.073 EndY=63.5726 EndZ=0
    g52: LineSegment StartX=243.575 StartY=46.5669 StartZ=0 EndX=245.072 EndY=43.8408 EndZ=0
    g53: LineSegment StartX=245.072 StartY=43.8408 StartZ=0 EndX=302.535 EndY=75.4095 EndZ=0
    g54: LineSegment StartX=239.192 StartY=54.5542 StartZ=0 EndX=302.567 EndY=89.3511 EndZ=0
    g55: LineSegment StartX=232.072 StartY=127.221 StartZ=0 EndX=232.072 EndY=124.221 EndZ=0
    g56: LineSegment StartX=232.072 StartY=136.221 StartZ=0 EndX=232.072 EndY=133.221 EndZ=0
    g57: LineSegment StartX=232.072 StartY=136.221 StartZ=0 EndX=407.073 EndY=136.221 EndZ=0
    g58: LineSegment StartX=322.073 StartY=124.221 StartZ=0 EndX=362.073 EndY=124.221 EndZ=0
    g59: LineSegment StartX=232.072 StartY=124.221 StartZ=0 EndX=302.073 EndY=124.221 EndZ=0
    g60: LineSegment StartX=302.996 StartY=121.665 StartZ=0 EndX=240.171 EndY=69.471 EndZ=0
    g61: LineSegment StartX=240.171 StartY=69.471 StartZ=0 EndX=241.711 EndY=67.6177 EndZ=0
    g62: LineSegment StartX=241.711 StartY=67.6177 StartZ=0 EndX=246.787 EndY=71.8365 EndZ=0
    g63: LineSegment StartX=246.787 StartY=71.8365 StartZ=0 EndX=248.551 EndY=69.712 EndZ=0
    g64: LineSegment StartX=248.551 StartY=69.712 StartZ=0 EndX=243.475 EndY=65.4951 EndZ=0
    g65: LineSegment StartX=245.073 StartY=63.5726 StartZ=0 EndX=302.996 EndY=111.695 EndZ=0
    g66: LineSegment StartX=239.192 StartY=54.5542 StartZ=0 EndX=240.687 EndY=51.8263 EndZ=0
    g67: LineSegment StartX=375.073 StartY=48.2206 StartZ=0 EndX=382.073 EndY=48.2206 EndZ=0
    g68: LineSegment StartX=407.073 StartY=48.2206 StartZ=0 EndX=400.073 EndY=48.2206 EndZ=0
    g69: LineSegment StartX=394.073 StartY=48.2206 StartZ=0 EndX=394.073 EndY=52.2206 EndZ=0
    g70: LineSegment StartX=388.073 StartY=48.2206 StartZ=0 EndX=388.073 EndY=58.2206 EndZ=0
    g71: ArcOfCircle CenterX=385.073 CenterY=61.2206 CenterZ=0 NormalX=0 NormalY=0 NormalZ=1 AngleXU=0 Radius=4.24264 StartAngle=5.49779 EndAngle=10.2102
    g72: ArcOfCircle CenterX=397.073 CenterY=55.2206 CenterZ=0 NormalX=0 NormalY=0 NormalZ=1 AngleXU=0 Radius=4.24264 StartAngle=5.49779 EndAngle=10.2102
    g73: LineSegment StartX=382.073 StartY=58.2206 StartZ=0 EndX=382.073 EndY=48.2206 EndZ=0
    g74: LineSegment StartX=400.073 StartY=52.2206 StartZ=0 EndX=400.073 EndY=48.2206 EndZ=0
    g75: LineSegment StartX=394.073 StartY=48.2206 StartZ=0 EndX=388.073 EndY=48.2206 EndZ=0
    g76: LineSegment StartX=306.073 StartY=-27.5935 StartZ=0 EndX=310.073 EndY=-27.5935 EndZ=0
    g77: LineSegment StartX=318.073 StartY=-27.5935 StartZ=0 EndX=314.073 EndY=-27.5935 EndZ=0
    g78: LineSegment StartX=310.073 StartY=-27.5935 StartZ=0 EndX=310.073 EndY=-31.5935 EndZ=0
    g79: LineSegment StartX=314.073 StartY=-27.5935 StartZ=0 EndX=314.073 EndY=-31.5935 EndZ=0
    g80: ArcOfCircle CenterX=312.073 CenterY=-33.5935 CenterZ=0 NormalX=0 NormalY=0 NormalZ=1 AngleXU=0 Radius=2.82843 StartAngle=2.35619 EndAngle=7.06858
    g81: LineSegment StartX=407.073 StartY=48.2206 StartZ=0 EndX=407.073 EndY=136.221 EndZ=0
    g82: LineSegment StartX=306.073 StartY=73.3346 StartZ=0 EndX=306.073 EndY=-27.5935 EndZ=0
    g83: BSplineCurve PolesCount=3 KnotsCount=2 Degree=2 IsPeriodic=0
    g84: BSplineCurve PolesCount=3 KnotsCount=2 Degree=2 IsPeriodic=0
    g85: LineSegment StartX=375.073 StartY=64.4106 StartZ=0 EndX=375.073 EndY=48.2206 EndZ=0
    g86: LineSegment StartX=318.073 StartY=64.4065 StartZ=0 EndX=318.073 EndY=-27.5935 EndZ=0
    g87: LineSegment StartX=322.073 StartY=68.4065 StartZ=0 EndX=371.073 EndY=68.4065 EndZ=0
    g88: BSplineCurve PolesCount=3 KnotsCount=2 Degree=2 IsPeriodic=0
    g89: LineSegment StartX=318.073 StartY=120.221 StartZ=0 EndX=318.073 EndY=113.865 EndZ=0
    g90: BSplineCurve PolesCount=3 KnotsCount=2 Degree=2 IsPeriodic=0
    g91: LineSegment StartX=322.073 StartY=109.865 StartZ=0 EndX=328.643 EndY=109.865 EndZ=0
    g92: LineSegment StartX=336.157 StartY=111.779 StartZ=0 EndX=362.567 EndY=122.294 EndZ=0
  constraints (140):
    c: Weight(g0) = 1
    c: Equal(g0,g1)
    c: Equal(g0,g2)
    c: InternalAlignment(g0,g3)
    c: InternalAlignment(g1,g3)
    c: InternalAlignment(g2,g3)
    c: InternalAlignment(g4,g3)
    c: InternalAlignment(g5,g3)
    c: Weight(g6) = 1
    c: Equal(g6,g7)
    c: Equal(g6,g8)
    c: InternalAlignment(g6,g9)
    c: InternalAlignment(g7,g9)
    c: InternalAlignment(g8,g9)
    c: InternalAlignment(g10,g9)
    c: InternalAlignment(g11,g9)
    c: Block(g3)
    c: Block(g9)
    c: Coincident(g12,g3)
    c: Coincident(g12,g9)
    c: Vertical(g12)
    c: Weight(g13) = 1
    c: Equal(g13,g14)
    c: Equal(g13,g15)
    c: InternalAlignment(g14,g16)
    c: InternalAlignment(g15,g16)
    c: InternalAlignment(g17,g16)
    c: InternalAlignment(g18,g16)
    c: Block(g51)
    c: Block(g52)
    c: Coincident(g53,g52)
    c: Coincident(g53,g22)
    c: Block(g53)
    c: Coincident(g50,g49)
    c: Coincident(g50,g48)
    c: Coincident(g54,g9)
    c: Block(g54)
    c: Distance(g51) = 2.5
    c: Block(g44)
    c: Coincident(g55,g44)
    c: Vertical(g55)
    c: Coincident(g56,g44)
    c: Vertical(g56)
    c: Coincident(g57,g56)
    c: Horizontal(g57)
    c: Coincident(g58,g34)
    c: Coincident(g58,g28)
    c: Horizontal(g58)
    c: Block(g34)
    c: Block(g28)
    c: Coincident(g59,g55)
    c: Coincident(g59,g16)
    c: Horizontal(g59)
    c: Coincident(g60,g16)
    c: Block(g59)
    c: Block(g60)
    c: Block(g16)
    c: Coincident(g61,g60)
    c: Block(g61)
    c: Coincident(g62,g61)
    c: Block(g62)
    c: Coincident(g63,g62)
    c: Coincident(g64,g63)
    c: Coincident(g64,g51)
    c: Block(g64)
    c: Coincident(g65,g51)
    c: Coincident(g65,g3)
    c: Block(g65)
    c: Coincident(g66,g54)
    c: Coincident(g66,g48)
    c: Block(g50)
    c: Block(g48)
    c: Block(g49)
    c: Block(g22)
    c: Horizontal(g67)
    c: Distance(g67) = 7
    c: Horizontal(g68)
    c: Distance(g68) = 7
    c: Vertical(g69)
    c: Distance(g69) = 4
    c: Vertical(g70)
    c: Distance(g70) = 10
    c: Coincident(g71,g70)
    c: Coincident(g72,g69)
    c: Block(g72)
    c: Block(g71)
    c: Coincident(g73,g71)
    c: Coincident(g73,g67)
    c: Vertical(g73)
    c: Coincident(g74,g72)
    c: Coincident(g74,g68)
    c: Vertical(g74)
    c: Coincident(g75,g69)
    c: Coincident(g75,g70)
    c: Horizontal(g75)
    c: Horizontal(g76)
    c: Distance(g76) = 4
    c: Horizontal(g77)
    c: Distance(g77) = 4
    c: Coincident(g78,g76)
    c: Vertical(g78)
    c: Coincident(g79,g77)
    c: Vertical(g79)
    c: Distance(g78) = 4
    c: Distance(g79) = 4
    c: Coincident(g80,g78)
    c: Coincident(g80,g79)
    c: Block(g80)
    c: Coincident(g81,g68)
    c: Coincident(g81,g57)
    c: Vertical(g81)
    c: Block(g57)
    c: Block(g81)
    c: Coincident(g82,g22)
    c: Coincident(g82,g76)
    c: Vertical(g82)
    c: Block(g67)
    c: Block(g83)
    c: Block(g84)
    c: Coincident(g85,g83)
    c: Coincident(g85,g67)
    c: Vertical(g85)
    c: Coincident(g86,g84)
    c: Coincident(g86,g77)
    c: Vertical(g86)
    c: Coincident(g87,g84)
    c: Coincident(g87,g83)
    c: Horizontal(g87)
    c: Block(g88)
    c: Coincident(g89,g34)
    c: Coincident(g89,g88)
    c: Vertical(g89)
    c: Block(g90)
    c: Coincident(g91,g88)
    c: Coincident(g91,g90)
    c: Horizontal(g91)
    c: Coincident(g92,g90)
    c: Coincident(g92,g28)
    c: Distance(g57) = 175.001
    c: Distance(g81) = 88
FEATURE [Part::Extrusion] Extrude035
  Base = -> Sketch034
  Dir = (0,0,1)
  DirMode = 2
  FaceMakerClass = Part::FaceMakerBullseye
  LengthFwd = 28
  LengthRev = 0
  Solid = true
  Symmetric = false
FEATURE [Part::Box] Box033  label="removeFromtTop008"
  AttacherType = Attacher::AttachEngine3D
  Height = 56
  Length = 470
  Placement = pos=(-47.93,-106.78,8) rot=(1,0,0;0.080285rad)
  Width = 260
FEATURE [Part::Cut] Cut020
  Base = -> Extrude035
  Tool = -> Box033
FEATURE [Part::Cut] Cut021  label="legBraceRight"
  Base = -> Fusion002
  Tool = -> Cut020
FEATURE [Sketcher::SketchObject] Sketch035  label="rightSideTop002"
  FullyConstrained = false
  sketch-geometry (93):
    g0: Circle CenterX=302.996 CenterY=111.695 CenterZ=0 NormalX=0 NormalY=0 NormalZ=1 AngleXU=0 Radius=1
    g1: Circle CenterX=306.073 CenterY=114.251 CenterZ=0 NormalX=0 NormalY=0 NormalZ=1 AngleXU=0 Radius=1
    g2: Circle CenterX=306.073 CenterY=110.251 CenterZ=0 NormalX=0 NormalY=0 NormalZ=1 AngleXU=0 Radius=1
    g3: BSplineCurve PolesCount=3 KnotsCount=2 Degree=2 IsPeriodic=0
    g4: GeomPoint X=302.996 Y=111.695 Z=0
    g5: GeomPoint X=306.073 Y=110.251 Z=0
    g6: Circle CenterX=306.073 CenterY=95.2763 CenterZ=0 NormalX=0 NormalY=0 NormalZ=1 AngleXU=0 Radius=1
    g7: Circle CenterX=306.073 CenterY=91.2763 CenterZ=0 NormalX=0 NormalY=0 NormalZ=1 AngleXU=0 Radius=1
    g8: Circle CenterX=302.567 CenterY=89.3511 CenterZ=0 NormalX=0 NormalY=0 NormalZ=1 AngleXU=0 Radius=1
    g9: BSplineCurve PolesCount=3 KnotsCount=2 Degree=2 IsPeriodic=0
    g10: GeomPoint X=306.073 Y=95.2763 Z=0
    g11: GeomPoint X=302.567 Y=89.3511 Z=0
    g12: LineSegment StartX=306.073 StartY=110.251 StartZ=0 EndX=306.073 EndY=95.2763 EndZ=0
    g13: Circle CenterX=302.073 CenterY=124.221 CenterZ=0 NormalX=0 NormalY=0 NormalZ=1 AngleXU=0 Radius=1
    g14: Circle CenterX=306.073 CenterY=124.221 CenterZ=0 NormalX=0 NormalY=0 NormalZ=1 AngleXU=0 Radius=1
    g15: Circle CenterX=302.996 CenterY=121.665 CenterZ=0 NormalX=0 NormalY=0 NormalZ=1 AngleXU=0 Radius=1
    g16: BSplineCurve PolesCount=3 KnotsCount=2 Degree=2 IsPeriodic=0
    g17: GeomPoint X=302.073 Y=124.221 Z=0
    g18: GeomPoint X=302.996 Y=121.665 Z=0
    g19: Circle CenterX=306.073 CenterY=73.3346 CenterZ=0 NormalX=0 NormalY=0 NormalZ=1 AngleXU=0 Radius=1
    g20: Circle CenterX=306.073 CenterY=77.3346 CenterZ=0 NormalX=0 NormalY=0 NormalZ=1 AngleXU=0 Radius=1
    g21: Circle CenterX=302.535 CenterY=75.4095 CenterZ=0 NormalX=0 NormalY=0 NormalZ=1 AngleXU=0 Radius=1
    g22: BSplineCurve PolesCount=3 KnotsCount=2 Degree=2 IsPeriodic=0
    g23: GeomPoint X=306.073 Y=73.3346 Z=0
    g24: GeomPoint X=302.535 Y=75.4095 Z=0
    g25: Circle CenterX=362.073 CenterY=124.221 CenterZ=0 NormalX=0 NormalY=0 NormalZ=1 AngleXU=0 Radius=1
    g26: Circle CenterX=366.073 CenterY=124.221 CenterZ=0 NormalX=0 NormalY=0 NormalZ=1 AngleXU=0 Radius=1
    g27: Circle CenterX=362.567 CenterY=122.294 CenterZ=0 NormalX=0 NormalY=0 NormalZ=1 AngleXU=0 Radius=1
    g28: BSplineCurve PolesCount=3 KnotsCount=2 Degree=2 IsPeriodic=0
    g29: GeomPoint X=362.073 Y=124.221 Z=0
    g30: GeomPoint X=362.567 Y=122.294 Z=0
    g31: Circle CenterX=322.073 CenterY=124.221 CenterZ=0 NormalX=0 NormalY=0 NormalZ=1 AngleXU=0 Radius=1
    g32: Circle CenterX=318.073 CenterY=124.221 CenterZ=0 NormalX=0 NormalY=0 NormalZ=1 AngleXU=0 Radius=1
    g33: Circle CenterX=318.073 CenterY=120.221 CenterZ=0 NormalX=0 NormalY=0 NormalZ=1 AngleXU=0 Radius=1
    g34: BSplineCurve PolesCount=3 KnotsCount=2 Degree=2 IsPeriodic=0
    g35: GeomPoint X=322.073 Y=124.221 Z=0
    g36: GeomPoint X=318.073 Y=120.221 Z=0
    g37: Circle CenterX=318.073 CenterY=109.865 CenterZ=0 NormalX=0 NormalY=0 NormalZ=1 AngleXU=0 Radius=1
    g38: GeomPoint X=318.073 Y=109.865 Z=0
    g39: Circle CenterX=322.073 CenterY=76.4095 CenterZ=0 NormalX=0 NormalY=0 NormalZ=1 AngleXU=0 Radius=4
    g40: Circle CenterX=232.072 CenterY=133.221 CenterZ=0 NormalX=0 NormalY=0 NormalZ=1 AngleXU=0 Radius=1
    g41: Circle CenterX=226.072 CenterY=136.221 CenterZ=0 NormalX=0 NormalY=0 NormalZ=1 AngleXU=0 Radius=1
    g42: Circle CenterX=226.072 CenterY=124.221 CenterZ=0 NormalX=0 NormalY=0 NormalZ=1 AngleXU=0 Radius=1
    g43: Circle CenterX=232.072 CenterY=127.221 CenterZ=0 NormalX=0 NormalY=0 NormalZ=1 AngleXU=0 Radius=1
    g44: BSplineCurve PolesCount=5 KnotsCount=3 Degree=3 IsPeriodic=0
    g45: GeomPoint X=232.072 Y=133.221 Z=0
    g46: GeomPoint X=223.072 Y=130.221 Z=0
    g47: GeomPoint X=232.072 Y=127.221 Z=0
    g48: LineSegment StartX=240.687 StartY=51.8263 StartZ=0 EndX=243.317 EndY=53.2701 EndZ=0
    g49: LineSegment StartX=243.575 StartY=46.5669 StartZ=0 EndX=246.205 EndY=48.0108 EndZ=0
    g50: ArcOfCircle CenterX=247.391 CenterY=52.0843 CenterZ=0 NormalX=0 NormalY=0 NormalZ=1 AngleXU=0 Radius=4.24264 StartAngle=4.42912 EndAngle=9.14151
    g51: LineSegment StartX=243.475 StartY=65.4951 StartZ=0 EndX=245.073 EndY=63.5726 EndZ=0
    g52: LineSegment StartX=243.575 StartY=46.5669 StartZ=0 EndX=245.072 EndY=43.8408 EndZ=0
    g53: LineSegment StartX=245.072 StartY=43.8408 StartZ=0 EndX=302.535 EndY=75.4095 EndZ=0
    g54: LineSegment StartX=239.192 StartY=54.5542 StartZ=0 EndX=302.567 EndY=89.3511 EndZ=0
    g55: LineSegment StartX=232.072 StartY=127.221 StartZ=0 EndX=232.072 EndY=124.221 EndZ=0
    g56: LineSegment StartX=232.072 StartY=136.221 StartZ=0 EndX=232.072 EndY=133.221 EndZ=0
    g57: LineSegment StartX=232.072 StartY=136.221 StartZ=0 EndX=407.073 EndY=136.221 EndZ=0
    g58: LineSegment StartX=322.073 StartY=124.221 StartZ=0 EndX=362.073 EndY=124.221 EndZ=0
    g59: LineSegment StartX=232.072 StartY=124.221 StartZ=0 EndX=302.073 EndY=124.221 EndZ=0
    g60: LineSegment StartX=302.996 StartY=121.665 StartZ=0 EndX=240.171 EndY=69.471 EndZ=0
    g61: LineSegment StartX=240.171 StartY=69.471 StartZ=0 EndX=241.711 EndY=67.6177 EndZ=0
    g62: LineSegment StartX=241.711 StartY=67.6177 StartZ=0 EndX=246.787 EndY=71.8365 EndZ=0
    g63: LineSegment StartX=246.787 StartY=71.8365 StartZ=0 EndX=248.551 EndY=69.712 EndZ=0
    g64: LineSegment StartX=248.551 StartY=69.712 StartZ=0 EndX=243.475 EndY=65.4951 EndZ=0
    g65: LineSegment StartX=245.073 StartY=63.5726 StartZ=0 EndX=302.996 EndY=111.695 EndZ=0
    g66: LineSegment StartX=239.192 StartY=54.5542 StartZ=0 EndX=240.687 EndY=51.8263 EndZ=0
    g67: LineSegment StartX=375.073 StartY=48.2206 StartZ=0 EndX=382.073 EndY=48.2206 EndZ=0
    g68: LineSegment StartX=407.073 StartY=48.2206 StartZ=0 EndX=400.073 EndY=48.2206 EndZ=0
    g69: LineSegment StartX=394.073 StartY=48.2206 StartZ=0 EndX=394.073 EndY=52.2206 EndZ=0
    g70: LineSegment StartX=388.073 StartY=48.2206 StartZ=0 EndX=388.073 EndY=58.2206 EndZ=0
    g71: ArcOfCircle CenterX=385.073 CenterY=61.2206 CenterZ=0 NormalX=0 NormalY=0 NormalZ=1 AngleXU=0 Radius=4.24264 StartAngle=5.49779 EndAngle=10.2102
    g72: ArcOfCircle CenterX=397.073 CenterY=55.2206 CenterZ=0 NormalX=0 NormalY=0 NormalZ=1 AngleXU=0 Radius=4.24264 StartAngle=5.49779 EndAngle=10.2102
    g73: LineSegment StartX=382.073 StartY=58.2206 StartZ=0 EndX=382.073 EndY=48.2206 EndZ=0
    g74: LineSegment StartX=400.073 StartY=52.2206 StartZ=0 EndX=400.073 EndY=48.2206 EndZ=0
    g75: LineSegment StartX=394.073 StartY=48.2206 StartZ=0 EndX=388.073 EndY=48.2206 EndZ=0
    g76: LineSegment StartX=306.073 StartY=-27.5935 StartZ=0 EndX=310.073 EndY=-27.5935 EndZ=0
    g77: LineSegment StartX=318.073 StartY=-27.5935 StartZ=0 EndX=314.073 EndY=-27.5935 EndZ=0
    g78: LineSegment StartX=310.073 StartY=-27.5935 StartZ=0 EndX=310.073 EndY=-31.5935 EndZ=0
    g79: LineSegment StartX=314.073 StartY=-27.5935 StartZ=0 EndX=314.073 EndY=-31.5935 EndZ=0
    g80: ArcOfCircle CenterX=312.073 CenterY=-33.5935 CenterZ=0 NormalX=0 NormalY=0 NormalZ=1 AngleXU=0 Radius=2.82843 StartAngle=2.35619 EndAngle=7.06858
    g81: LineSegment StartX=407.073 StartY=48.2206 StartZ=0 EndX=407.073 EndY=136.221 EndZ=0
    g82: LineSegment StartX=306.073 StartY=73.3346 StartZ=0 EndX=306.073 EndY=-27.5935 EndZ=0
    g83: BSplineCurve PolesCount=3 KnotsCount=2 Degree=2 IsPeriodic=0
    g84: BSplineCurve PolesCount=3 KnotsCount=2 Degree=2 IsPeriodic=0
    g85: LineSegment StartX=375.073 StartY=64.4106 StartZ=0 EndX=375.073 EndY=48.2206 EndZ=0
    g86: LineSegment StartX=318.073 StartY=64.4065 StartZ=0 EndX=318.073 EndY=-27.5935 EndZ=0
    g87: LineSegment StartX=322.073 StartY=68.4065 StartZ=0 EndX=371.073 EndY=68.4065 EndZ=0
    g88: BSplineCurve PolesCount=3 KnotsCount=2 Degree=2 IsPeriodic=0
    g89: LineSegment StartX=318.073 StartY=120.221 StartZ=0 EndX=318.073 EndY=113.865 EndZ=0
    g90: BSplineCurve PolesCount=3 KnotsCount=2 Degree=2 IsPeriodic=0
    g91: LineSegment StartX=322.073 StartY=109.865 StartZ=0 EndX=328.643 EndY=109.865 EndZ=0
    g92: LineSegment StartX=336.157 StartY=111.779 StartZ=0 EndX=362.567 EndY=122.294 EndZ=0
  constraints (140):
    c: Weight(g0) = 1
    c: Equal(g0,g1)
    c: Equal(g0,g2)
    c: InternalAlignment(g0,g3)
    c: InternalAlignment(g1,g3)
    c: InternalAlignment(g2,g3)
    c: InternalAlignment(g4,g3)
    c: InternalAlignment(g5,g3)
    c: Weight(g6) = 1
    c: Equal(g6,g7)
    c: Equal(g6,g8)
    c: InternalAlignment(g6,g9)
    c: InternalAlignment(g7,g9)
    c: InternalAlignment(g8,g9)
    c: InternalAlignment(g10,g9)
    c: InternalAlignment(g11,g9)
    c: Block(g3)
    c: Block(g9)
    c: Coincident(g12,g3)
    c: Coincident(g12,g9)
    c: Vertical(g12)
    c: Weight(g13) = 1
    c: Equal(g13,g14)
    c: Equal(g13,g15)
    c: InternalAlignment(g14,g16)
    c: InternalAlignment(g15,g16)
    c: InternalAlignment(g17,g16)
    c: InternalAlignment(g18,g16)
    c: Block(g51)
    c: Block(g52)
    c: Coincident(g53,g52)
    c: Coincident(g53,g22)
    c: Block(g53)
    c: Coincident(g50,g49)
    c: Coincident(g50,g48)
    c: Coincident(g54,g9)
    c: Block(g54)
    c: Distance(g51) = 2.5
    c: Block(g44)
    c: Coincident(g55,g44)
    c: Vertical(g55)
    c: Coincident(g56,g44)
    c: Vertical(g56)
    c: Coincident(g57,g56)
    c: Horizontal(g57)
    c: Coincident(g58,g34)
    c: Coincident(g58,g28)
    c: Horizontal(g58)
    c: Block(g34)
    c: Block(g28)
    c: Coincident(g59,g55)
    c: Coincident(g59,g16)
    c: Horizontal(g59)
    c: Coincident(g60,g16)
    c: Block(g59)
    c: Block(g60)
    c: Block(g16)
    c: Coincident(g61,g60)
    c: Block(g61)
    c: Coincident(g62,g61)
    c: Block(g62)
    c: Coincident(g63,g62)
    c: Coincident(g64,g63)
    c: Coincident(g64,g51)
    c: Block(g64)
    c: Coincident(g65,g51)
    c: Coincident(g65,g3)
    c: Block(g65)
    c: Coincident(g66,g54)
    c: Coincident(g66,g48)
    c: Block(g50)
    c: Block(g48)
    c: Block(g49)
    c: Block(g22)
    c: Horizontal(g67)
    c: Distance(g67) = 7
    c: Horizontal(g68)
    c: Distance(g68) = 7
    c: Vertical(g69)
    c: Distance(g69) = 4
    c: Vertical(g70)
    c: Distance(g70) = 10
    c: Coincident(g71,g70)
    c: Coincident(g72,g69)
    c: Block(g72)
    c: Block(g71)
    c: Coincident(g73,g71)
    c: Coincident(g73,g67)
    c: Vertical(g73)
    c: Coincident(g74,g72)
    c: Coincident(g74,g68)
    c: Vertical(g74)
    c: Coincident(g75,g69)
    c: Coincident(g75,g70)
    c: Horizontal(g75)
    c: Horizontal(g76)
    c: Distance(g76) = 4
    c: Horizontal(g77)
    c: Distance(g77) = 4
    c: Coincident(g78,g76)
    c: Vertical(g78)
    c: Coincident(g79,g77)
    c: Vertical(g79)
    c: Distance(g78) = 4
    c: Distance(g79) = 4
    c: Coincident(g80,g78)
    c: Coincident(g80,g79)
    c: Block(g80)
    c: Coincident(g81,g68)
    c: Coincident(g81,g57)
    c: Vertical(g81)
    c: Block(g57)
    c: Block(g81)
    c: Coincident(g82,g22)
    c: Coincident(g82,g76)
    c: Vertical(g82)
    c: Block(g67)
    c: Block(g83)
    c: Block(g84)
    c: Coincident(g85,g83)
    c: Coincident(g85,g67)
    c: Vertical(g85)
    c: Coincident(g86,g84)
    c: Coincident(g86,g77)
    c: Vertical(g86)
    c: Coincident(g87,g84)
    c: Coincident(g87,g83)
    c: Horizontal(g87)
    c: Block(g88)
    c: Coincident(g89,g34)
    c: Coincident(g89,g88)
    c: Vertical(g89)
    c: Block(g90)
    c: Coincident(g91,g88)
    c: Coincident(g91,g90)
    c: Horizontal(g91)
    c: Coincident(g92,g90)
    c: Coincident(g92,g28)
    c: Distance(g57) = 175.001
    c: Distance(g81) = 88
FEATURE [Part::Extrusion] Extrude036
  Base = -> Sketch035
  Dir = (0,0,1)
  DirMode = 2
  FaceMakerClass = Part::FaceMakerBullseye
  LengthFwd = 28
  LengthRev = 0
  Solid = true
  Symmetric = false
FEATURE [Part::Box] Box034  label="removeFromtTop009"
  AttacherType = Attacher::AttachEngine3D
  Height = 56
  Length = 470
  Placement = pos=(-47.93,-106.78,8) rot=(1,0,0;0.080285rad)
  Width = 260
FEATURE [Part::Cut] Cut022
  Base = -> Extrude036
  Tool = -> Box034
FEATURE [Part::Cut] Cut023  label="legBraceRight005"
  Base = -> Fusion005
  Tool = -> Cut005
FEATURE [Part::Fillet] Fillet
  Base = -> Cut019
  Edges = 1 edges r=3: [Edge6]
FEATURE [Part::Fillet] Fillet001
  Base = -> Cut017
  Edges = 1 edges r=3: [Edge16]
  Placement = pos=(0,-0.62,0) rot=(0,0,1;0rad)
FEATURE [Part::Fillet] Fillet002
  Base = -> Cut023
  Edges = 1 edges r=3: [Edge18]
  Placement = pos=(0,0.62,0) rot=(0,0,1;0rad)
FEATURE [Part::Fillet] Fillet003
  Base = -> Cut021
  Edges = 1 edges r=3: [Edge11]
FEATURE [Part::Cylinder] Cylinder
  Angle = 360
  AttacherType = Attacher::AttachEngine3D
  Height = 10
  Placement = pos=(-49,103,-5) rot=(1,0,0;-0.328122rad)
  Radius = 1.1
FEATURE [App::MeasureDistance] Distance003  label="Distance: 3.30 mm"
  Distance = 3.29872
  P1 = (-50.1,104,-3)
  P2 = (-50.08,104.865,0.183159)
FEATURE [Part::Cylinder] Cylinder001
  Angle = 360
  AttacherType = Attacher::AttachEngine3D
  Height = 30
  Placement = pos=(-49,106,4) rot=(-1,0,0;0.328122rad)
  Radius = 3
FEATURE [Part::MultiFuse] Fusion022
  Placement = pos=(15,0,0) rot=(0,0,1;0rad)
  Shapes = -> [Cylinder,Cylinder001]
FEATURE [Part::Cylinder] Cylinder002
  Angle = 360
  AttacherType = Attacher::AttachEngine3D
  Height = 10
  Placement = pos=(-49,103,-5) rot=(-1,0,0;0.328122rad)
  Radius = 1.1
FEATURE [Part::Cylinder] Cylinder003
  Angle = 360
  AttacherType = Attacher::AttachEngine3D
  Height = 30
  Placement = pos=(-49,106,4) rot=(-1,0,0;0.328122rad)
  Radius = 3
FEATURE [Part::MultiFuse] Fusion023
  Placement = pos=(15,-32,0) rot=(0,0,1;0rad)
  Shapes = -> [Cylinder002,Cylinder003]
FEATURE [Part::MultiFuse] Fusion024
  Shapes = -> [Fusion022,Fusion023]
FEATURE [Part::Cylinder] Cylinder004
  Angle = 360
  AttacherType = Attacher::AttachEngine3D
  Height = 10
  Placement = pos=(-49,103,-5) rot=(-1,0,0;0.328122rad)
  Radius = 1.1
FEATURE [Part::Cylinder] Cylinder005
  Angle = 360
  AttacherType = Attacher::AttachEngine3D
  Height = 30
  Placement = pos=(-49,106,4) rot=(-1,0,0;0.328122rad)
  Radius = 3
FEATURE [Part::MultiFuse] Fusion025
  Placement = pos=(15,0,0) rot=(0,0,1;0rad)
  Shapes = -> [Cylinder004,Cylinder005]
FEATURE [Part::Cylinder] Cylinder006
  Angle = 360
  AttacherType = Attacher::AttachEngine3D
  Height = 10
  Placement = pos=(-49,103,-5) rot=(-1,0,0;0.328122rad)
  Radius = 1.1
FEATURE [Part::Cylinder] Cylinder007
  Angle = 360
  AttacherType = Attacher::AttachEngine3D
  Height = 30
  Placement = pos=(-49,106,4) rot=(-1,0,0;0.328122rad)
  Radius = 3
FEATURE [Part::MultiFuse] Fusion026
  Placement = pos=(15,-32,0) rot=(0,0,1;0rad)
  Shapes = -> [Cylinder006,Cylinder007]
FEATURE [Part::MultiFuse] Fusion027
  Placement = pos=(432,0,0) rot=(0,0,1;0rad)
  Shapes = -> [Fusion025,Fusion026]
FEATURE [Part::Cylinder] Cylinder008
  Angle = 360
  AttacherType = Attacher::AttachEngine3D
  Height = 10
  Placement = pos=(-49,103,-5) rot=(-1,0,0;0.328122rad)
  Radius = 1.1
FEATURE [Part::Cylinder] Cylinder009
  Angle = 360
  AttacherType = Attacher::AttachEngine3D
  Height = 30
  Placement = pos=(-49,106,4) rot=(-1,0,0;0.328122rad)
  Radius = 3
FEATURE [Part::MultiFuse] Fusion028
  Placement = pos=(31,0,0) rot=(0,0,1;0rad)
  Shapes = -> [Cylinder008,Cylinder009]
FEATURE [Part::Cylinder] Cylinder010
  Angle = 360
  AttacherType = Attacher::AttachEngine3D
  Height = 10
  Placement = pos=(-49,103,-5) rot=(-1,0,0;0.328122rad)
  Radius = 1.1
FEATURE [Part::Cylinder] Cylinder011
  Angle = 360
  AttacherType = Attacher::AttachEngine3D
  Height = 30
  Placement = pos=(-49,106,4) rot=(-1,0,0;0.328122rad)
  Radius = 3
FEATURE [Part::MultiFuse] Fusion029
  Placement = pos=(63,0,0) rot=(0,0,1;0rad)
  Shapes = -> [Cylinder010,Cylinder011]
FEATURE [Part::Cylinder] Cylinder012
  Angle = 360
  AttacherType = Attacher::AttachEngine3D
  Height = 10
  Placement = pos=(-49,103,-5) rot=(-1,0,0;0.328122rad)
  Radius = 1.1
FEATURE [Part::Cylinder] Cylinder013
  Angle = 360
  AttacherType = Attacher::AttachEngine3D
  Height = 30
  Placement = pos=(-49,106,4) rot=(-1,0,0;0.328122rad)
  Radius = 3
FEATURE [Part::MultiFuse] Fusion030
  Placement = pos=(31,-29.4,0) rot=(0,0,1;0rad)
  Shapes = -> [Cylinder012,Cylinder013]
FEATURE [Part::Cylinder] Cylinder014
  Angle = 360
  AttacherType = Attacher::AttachEngine3D
  Height = 10
  Placement = pos=(-49,103,-5) rot=(-1,0,0;0.328122rad)
  Radius = 1.1
FEATURE [Part::Cylinder] Cylinder015
  Angle = 360
  AttacherType = Attacher::AttachEngine3D
  Height = 30
  Placement = pos=(-49,106,4) rot=(-1,0,0;0.328122rad)
  Radius = 3
FEATURE [Part::MultiFuse] Fusion031
  Placement = pos=(63,-29.4,0) rot=(0,0,1;0rad)
  Shapes = -> [Cylinder014,Cylinder015]
FEATURE [Part::MultiFuse] Fusion032
  Shapes = -> [Fusion031,Fusion030,Fusion029,Fusion028]
FEATURE [Part::Cylinder] Cylinder016
  Angle = 360
  AttacherType = Attacher::AttachEngine3D
  Height = 10
  Placement = pos=(-49,103,-5) rot=(-1,0,0;0.328122rad)
  Radius = 1.1
FEATURE [Part::Cylinder] Cylinder017
  Angle = 360
  AttacherType = Attacher::AttachEngine3D
  Height = 30
  Placement = pos=(-49,106,4) rot=(-1,0,0;0.328122rad)
  Radius = 3
FEATURE [Part::MultiFuse] Fusion033
  Placement = pos=(31,0,0) rot=(0,0,1;0rad)
  Shapes = -> [Cylinder016,Cylinder017]
FEATURE [Part::Cylinder] Cylinder018
  Angle = 360
  AttacherType = Attacher::AttachEngine3D
  Height = 10
  Placement = pos=(-49,103,-5) rot=(-1,0,0;0.328122rad)
  Radius = 1.1
FEATURE [Part::Cylinder] Cylinder019
  Angle = 360
  AttacherType = Attacher::AttachEngine3D
  Height = 30
  Placement = pos=(-49,106,4) rot=(-1,0,0;0.328122rad)
  Radius = 3
FEATURE [Part::MultiFuse] Fusion035
  Placement = pos=(31,-29.4,0) rot=(0,0,1;0rad)
  Shapes = -> [Cylinder018,Cylinder019]
FEATURE [Part::Cylinder] Cylinder020
  Angle = 360
  AttacherType = Attacher::AttachEngine3D
  Height = 10
  Placement = pos=(-49,103,-5) rot=(-1,0,0;0.328122rad)
  Radius = 1.1
FEATURE [Part::Cylinder] Cylinder021
  Angle = 360
  AttacherType = Attacher::AttachEngine3D
  Height = 30
  Placement = pos=(-49,106,4) rot=(-1,0,0;0.328122rad)
  Radius = 3
FEATURE [Part::MultiFuse] Fusion034
  Placement = pos=(63,0,0) rot=(0,0,1;0rad)
  Shapes = -> [Cylinder020,Cylinder021]
FEATURE [Part::Cylinder] Cylinder022
  Angle = 360
  AttacherType = Attacher::AttachEngine3D
  Height = 10
  Placement = pos=(-49,103,-5) rot=(-1,0,0;0.328122rad)
  Radius = 1.1
FEATURE [Part::Cylinder] Cylinder023
  Angle = 360
  AttacherType = Attacher::AttachEngine3D
  Height = 30
  Placement = pos=(-49,106,4) rot=(-1,0,0;0.328122rad)
  Radius = 3
FEATURE [Part::MultiFuse] Fusion036
  Placement = pos=(63,-29.4,0) rot=(0,0,1;0rad)
  Shapes = -> [Cylinder022,Cylinder023]
FEATURE [Part::MultiFuse] Fusion037
  Placement = pos=(369,0,0) rot=(0,0,1;0rad)
  Shapes = -> [Fusion036,Fusion035,Fusion034,Fusion033]
FEATURE [Part::Box] Box039  label="Cube026"
  AttacherType = Attacher::AttachEngine3D
  Height = 30
  Length = 10
  Placement = pos=(-34,58.6,-40) rot=(-1,0,0;0.364774rad)
  Width = 3
FEATURE [Part::Box] Box040  label="Cube027"
  AttacherType = Attacher::AttachEngine3D
  Height = 30
  Length = 10
  Placement = pos=(-34,58.6,-40) rot=(-1,0,0;0.364774rad)
  Width = 3
FEATURE [Part::Box] Box041  label="Cube028"
  AttacherType = Attacher::AttachEngine3D
  Height = 30
  Length = 10
  Placement = pos=(-34,88.4,-40) rot=(-1,0,0;0.364774rad)
  Width = 3
FEATURE [Part::Box] Box042  label="Cube029"
  AttacherType = Attacher::AttachEngine3D
  Height = 30
  Length = 10
  Placement = pos=(-34,88.4,-40) rot=(-1,0,0;0.364774rad)
  Width = 3
FEATURE [Part::MultiFuse] Fusion041
  Shapes = -> [Box042,Box039]
FEATURE [Part::MultiFuse] Fusion042
  Placement = pos=(0,-19.2,-51) rot=(0,0,1;0rad)
  Shapes = -> [Box041,Box040]
FEATURE [Part::MultiFuse] Fusion043
  Placement = pos=(422.36,0,0) rot=(0,0,1;0rad)
  Shapes = -> [Fusion042,Fusion041]
FEATURE [Sketcher::SketchObject] Sketch036  label="legBottomBack001"
  FullyConstrained = true
  MapMode = 4
  Placement = pos=(0,0,0) rot=(0.57735,0.57735,0.57735;2.0944rad)
  sketch-geometry (76):
    g0: Circle CenterX=-17.0256 CenterY=-190.268 CenterZ=0 NormalX=0 NormalY=0 NormalZ=1 AngleXU=0 Radius=10.5072
    g1: Circle CenterX=-37.7758 CenterY=-187.672 CenterZ=0 NormalX=0 NormalY=0 NormalZ=1 AngleXU=0 Radius=5.64388
    g2: Circle CenterX=-51.4606 CenterY=-185.091 CenterZ=0 NormalX=0 NormalY=0 NormalZ=1 AngleXU=0 Radius=3.01653
    g3: Circle CenterX=-60.4835 CenterY=-182.688 CenterZ=0 NormalX=0 NormalY=0 NormalZ=1 AngleXU=0 Radius=2.12826
    g4: Circle CenterX=-3.29005 CenterY=-177.662 CenterZ=0 NormalX=0 NormalY=0 NormalZ=1 AngleXU=0 Radius=3.26661
    g5: ArcOfCircle CenterX=11.0205 CenterY=-198.019 CenterZ=0 NormalX=0 NormalY=0 NormalZ=1 AngleXU=0 Radius=13 StartAngle=2.78068 EndAngle=5.92131
    g6: LineSegment StartX=5.08312 StartY=-176.581 StartZ=0 EndX=-1.14188 EndY=-193.429 EndZ=0
    g7: ArcOfCircle CenterX=17.2475 CenterY=-181.166 CenterZ=0 NormalX=0 NormalY=0 NormalZ=1 AngleXU=0 Radius=13 StartAngle=1.21042 EndAngle=2.78109
    g8: LineSegment StartX=38.8952 StartY=-231.233 StartZ=0 EndX=39.9512 EndY=-228.425 EndZ=0
    g9: ArcOfCircle CenterX=46.9911 CenterY=-209.705 CenterZ=0 NormalX=0 NormalY=0 NormalZ=1 AngleXU=0 Radius=20 StartAngle=2.78766 EndAngle=4.35269
    g10: LineSegment StartX=23.7323 StartY=-126.969 StartZ=0 EndX=17.4091 EndY=-143.817 EndZ=0
    g11: ArcOfCircle CenterX=29.5716 CenterY=-148.408 CenterZ=0 NormalX=0 NormalY=0 NormalZ=1 AngleXU=0 Radius=13 StartAngle=2.78068 EndAngle=4.35262
    g12: ArcOfCircle CenterX=35.8967 CenterY=-131.555 CenterZ=0 NormalX=0 NormalY=0 NormalZ=1 AngleXU=0 Radius=13 StartAngle=1.21584 EndAngle=2.78109
    g13: ArcOfCircle CenterX=48.1805 CenterY=-98.7782 CenterZ=0 NormalX=0 NormalY=0 NormalZ=1 AngleXU=0 Radius=13 StartAngle=2.78068 EndAngle=4.35005
    g14: LineSegment StartX=42.354 StartY=-77.3391 StartZ=0 EndX=36.018 EndY=-94.1875 EndZ=0
    g15: ArcOfCircle CenterX=54.5183 CenterY=-81.9247 CenterZ=0 NormalX=0 NormalY=0 NormalZ=1 AngleXU=0 Radius=13 StartAngle=2.42113 EndAngle=2.78109
    g16: ArcOfCircle CenterX=20.184 CenterY=-217.506 CenterZ=0 NormalX=0 NormalY=0 NormalZ=1 AngleXU=0 Radius=3.81084 StartAngle=1.88136 EndAngle=6.80465
    g17: LineSegment StartX=38.4753 StartY=-115.966 StartZ=0 EndX=41.2852 EndY=-117.017 EndZ=0
    g18: ArcOfCircle CenterX=36.3663 CenterY=-113.042 CenterZ=0 NormalX=0 NormalY=0 NormalZ=1 AngleXU=0 Radius=3.60555 StartAngle=0.230024 EndAngle=5.3372
    g19: LineSegment StartX=39.8769 StartY=-112.22 StartZ=0 EndX=42.6867 EndY=-113.271 EndZ=0
    g20: LineSegment StartX=19.9036 StartY=-165.61 StartZ=0 EndX=22.7134 EndY=-166.661 EndZ=0
    g21: ArcOfCircle CenterX=17.7945 CenterY=-162.686 CenterZ=0 NormalX=0 NormalY=0 NormalZ=1 AngleXU=0 Radius=3.60555 StartAngle=0.230024 EndAngle=5.3372
    g22: LineSegment StartX=21.3051 StartY=-161.864 StartZ=0 EndX=24.1149 EndY=-162.915 EndZ=0
    g23: LineSegment StartX=41.085 StartY=-66.3176 StartZ=0 EndX=46.0385 EndY=-62.5254 EndZ=0
    g24: LineSegment StartX=48.9563 StartY=-66.3367 StartZ=0 EndX=44.7488 EndY=-73.3482 EndZ=0
    g25: ArcOfCircle CenterX=49.8795 CenterY=-62.6074 CenterZ=0 NormalX=0 NormalY=0 NormalZ=1 AngleXU=0 Radius=3.84187 StartAngle=4.46973 EndAngle=9.40343
    g26: LineSegment StartX=43.5724 StartY=-110.934 StartZ=0 EndX=42.6867 EndY=-113.271 EndZ=0
    g27: LineSegment StartX=40.4148 StartY=-119.365 StartZ=0 EndX=41.2852 EndY=-117.017 EndZ=0
    g28: LineSegment StartX=21.8316 StartY=-169.001 StartZ=0 EndX=22.7134 EndY=-166.661 EndZ=0
    g29: LineSegment StartX=24.9948 StartY=-160.575 StartZ=0 EndX=24.1149 EndY=-162.915 EndZ=0
    g30: LineSegment StartX=23.1786 StartY=-202.622 StartZ=0 EndX=19.0195 EndY=-213.878 EndZ=0
    g31: LineSegment StartX=28.2308 StartY=-202.773 StartZ=0 EndX=23.4884 EndY=-215.608 EndZ=0
    g32: LineSegment StartX=-76.2249 StartY=-179.393 StartZ=0 EndX=-72.8553 EndY=-180.66 EndZ=0
    g33: ArcOfCircle CenterX=-71.1257 CenterY=-183.448 CenterZ=0 NormalX=0 NormalY=0 NormalZ=1 AngleXU=0 Radius=3.28025 StartAngle=3.43759 EndAngle=8.40938
    g34: LineSegment StartX=-79.0409 StartY=-186.881 StartZ=0 EndX=38.8952 EndY=-231.233 EndZ=0
    g35-g53: Circle x19 (B-spline internal-alignment scaffolding for g54; pole/knot coordinates omitted)
    g54: BSplineCurve PolesCount=19 KnotsCount=17 Degree=3 IsPeriodic=0
    g55-g71: GeomPoint x17 (B-spline internal-alignment scaffolding for g54; pole/knot coordinates omitted)
    g72: LineSegment StartX=-74.2633 StartY=-184.404 StartZ=0 EndX=-77.6329 EndY=-183.137 EndZ=0
    g73: LineSegment StartX=-79.0409 StartY=-186.881 StartZ=0 EndX=-77.6329 EndY=-183.137 EndZ=0
    g74: LineSegment StartX=8.65492 StartY=-152.553 StartZ=0 EndX=41.085 EndY=-66.3176 EndZ=0
    g75: LineSegment StartX=-74.4658 StartY=-174.715 StartZ=0 EndX=-76.2249 EndY=-179.393 EndZ=0
  constraints (76):
    c: Block(g5)
    c: Block(g7)
    c: Block(g0)
    c: Block(g4)
    c: Block(g1)
    c: Block(g2)
    c: Block(g3)
    c: Block(g9)
    c: Coincident(g8,g9)
    c: Block(g8)
    c: Coincident(g6,g7)
    c: Coincident(g6,g5)
    c: Block(g11)
    c: Block(g12)
    c: Coincident(g10,g12)
    c: Coincident(g10,g11)
    c: Block(g13)
    c: Block(g15)
    c: Coincident(g14,g15)
    c: Coincident(g14,g13)
    c: Block(g16)
    c: Block(g18)
    c: Coincident(g19,g18)
    c: Coincident(g17,g18)
    c: Parallel(g19,g17)
    c: Block(g17)
    c: Block(g19)
    c: Block(g21)
    c: Coincident(g22,g21)
    c: Coincident(g20,g21)
    c: Parallel(g22,g20)
    c: Block(g20)
    c: Block(g22)
    c: Block(g23)
    c: Coincident(g25,g23)
    c: Coincident(g25,g24)
    c: Block(g25)
    c: Block(g24)
    c: Coincident(g26,g19)
    c: Block(g26)
    c: Coincident(g27,g17)
    c: Block(g27)
    c: Coincident(g28,g20)
    c: Coincident(g29,g22)
    c: Block(g29)
    c: Block(g28)
    c: Coincident(g30,g5)
    c: Coincident(g30,g16)
    c: Block(g30)
    c: Coincident(g7,g28)
    c: Coincident(g11,g29)
    c: Coincident(g12,g27)
    c: Coincident(g13,g26)
    c: Coincident(g15,g24)
    c: Coincident(g31,g9)
    c: Coincident(g31,g16)
    c: Distance(g32) = 3.6
    c: Block(g32)
    c: Coincident(g33,g32)
    c: Coincident(g34,g8)
    c: Weight(g35) = 1
    c: Equal(g35, g36-g53) x18
    c: InternalAlignment(g35-g53 -> g54) x19
    c: InternalAlignment(g55-g71 -> g54) x17
    c: Block(g33)
    c: Block(g54)
    c: Coincident(g72,g33)
    c: Coincident(g73,g34)
    c: Block(g34)
    c: Parallel(g72,g34)
    c: Perpendicular(g73,g34)
    c: Coincident(g72,g73)
    c: Coincident(g74,g54)
    c: Coincident(g74,g23)
    c: Coincident(g75,g54)
    c: Coincident(g75,g32)
FEATURE [Part::Extrusion] Extrude037
  Base = -> Sketch036
  Dir = (1,0,0)
  DirMode = 2
  FaceMakerClass = Part::FaceMakerBullseye
  LengthFwd = 12
  LengthRev = 0
  Placement = pos=(392.24,11,16) rot=(0,0,1;0rad)
  Solid = true
  Symmetric = false
FEATURE [Part::Box] Box047  label="Cube034"
  AttacherType = Attacher::AttachEngine3D
  Height = 30
  Length = 10
  Placement = pos=(-34,58.6,-40) rot=(-1,0,0;0.364774rad)
  Width = 3
FEATURE [Part::Box] Box048  label="Cube035"
  AttacherType = Attacher::AttachEngine3D
  Height = 30
  Length = 10
  Placement = pos=(-34,58.6,-40) rot=(-1,0,0;0.364774rad)
  Width = 3
FEATURE [Part::Box] Box049  label="Cube036"
  AttacherType = Attacher::AttachEngine3D
  Height = 30
  Length = 10
  Placement = pos=(-34,88.4,-40) rot=(-1,0,0;0.364774rad)
  Width = 3
FEATURE [Part::MultiFuse] Fusion047
  Placement = pos=(0,-19.2,-51) rot=(0,0,1;0rad)
  Shapes = -> [Box049,Box048]
FEATURE [Part::Box] Box050  label="Cube037"
  AttacherType = Attacher::AttachEngine3D
  Height = 30
  Length = 10
  Placement = pos=(-34,88.4,-40) rot=(-1,0,0;0.364774rad)
  Width = 3
FEATURE [Part::MultiFuse] Fusion046
  Shapes = -> [Box050,Box047]
FEATURE [Part::MultiFuse] Fusion048
  Placement = pos=(422.36,0,0) rot=(0,0,1;0rad)
  Shapes = -> [Fusion047,Fusion046]
FEATURE [Part::Cut] Cut024  label="rightTopLeg"
  Base = -> Extrude022
  Tool = -> Fusion048
FEATURE [Part::Box] Box051  label="Cube038"
  AttacherType = Attacher::AttachEngine3D
  Height = 30
  Length = 10
  Placement = pos=(-34,58.6,-40) rot=(-1,0,0;0.364774rad)
  Width = 3
FEATURE [Part::Box] Box052  label="Cube039"
  AttacherType = Attacher::AttachEngine3D
  Height = 30
  Length = 10
  Placement = pos=(-34,58.6,-40) rot=(-1,0,0;0.364774rad)
  Width = 3
FEATURE [Part::Box] Box053  label="Cube040"
  AttacherType = Attacher::AttachEngine3D
  Height = 30
  Length = 10
  Placement = pos=(-34,88.4,-40) rot=(-1,0,0;0.364774rad)
  Width = 3
FEATURE [Part::MultiFuse] Fusion050
  Placement = pos=(0,-19.2,-51) rot=(0,0,1;0rad)
  Shapes = -> [Box053,Box052]
FEATURE [Part::Box] Box054  label="Cube041"
  AttacherType = Attacher::AttachEngine3D
  Height = 30
  Length = 10
  Placement = pos=(-34,88.4,-40) rot=(-1,0,0;0.364774rad)
  Width = 3
FEATURE [Part::MultiFuse] Fusion049
  Shapes = -> [Box054,Box051]
FEATURE [Part::MultiFuse] Fusion051  label="rightLegBraceAttatchments"
  Placement = pos=(422.36,0,0) rot=(0,0,1;0rad)
  Shapes = -> [Fusion050,Fusion049]
FEATURE [Part::Cut] Cut025  label="rightBottomLeg"
  Base = -> Extrude037
  Tool = -> Fusion043
FEATURE [Part::Box] Box055  label="Cube042"
  AttacherType = Attacher::AttachEngine3D
  Height = 30
  Length = 10
  Placement = pos=(-34,58.6,-40) rot=(-1,0,0;0.364774rad)
  Width = 3
FEATURE [Part::Box] Box056  label="Cube043"
  AttacherType = Attacher::AttachEngine3D
  Height = 30
  Length = 10
  Placement = pos=(-34,58.6,-40) rot=(-1,0,0;0.364774rad)
  Width = 3
FEATURE [Part::Box] Box057  label="Cube044"
  AttacherType = Attacher::AttachEngine3D
  Height = 30
  Length = 10
  Placement = pos=(-34,88.4,-40) rot=(-1,0,0;0.364774rad)
  Width = 3
FEATURE [Part::Box] Box058  label="Cube045"
  AttacherType = Attacher::AttachEngine3D
  Height = 30
  Length = 10
  Placement = pos=(-34,88.4,-40) rot=(-1,0,0;0.364774rad)
  Width = 3
FEATURE [Part::MultiFuse] Fusion052
  Shapes = -> [Box058,Box055]
FEATURE [Part::MultiFuse] Fusion053
  Placement = pos=(0,-19.2,-51) rot=(0,0,1;0rad)
  Shapes = -> [Box057,Box056]
FEATURE [Part::MultiFuse] Fusion054  label="leftLegBraceAttatchments"
  Shapes = -> [Fusion053,Fusion052]
FEATURE [Part::MultiFuse] Fusion055  label="leftLegBraceAttatchments001"
  Shapes = -> [Fusion053,Fusion052]
FEATURE [Part::Cut] Cut026
  Base = -> Extrude006
  Tool = -> Fusion055
FEATURE [Part::MultiFuse] Fusion056  label="leftLegBraceAttatchments002"
  Shapes = -> [Fusion053,Fusion052]
FEATURE [Part::Cut] Cut027
  Base = -> Extrude005
  Tool = -> Fusion054
FEATURE [Part::Chamfer] Chamfer
  Base = -> Cut014
  Edges = 1 edges r=3: [Edge39]
FEATURE [Part::Chamfer] Chamfer001
  Base = -> Fusion018
  Edges = 1 edges r=3: [Edge36]
FEATURE [Part::Chamfer] Chamfer002
  Base = -> Cut011
  Edges = 1 edges r=3: [Edge40]
FEATURE [Part::Fillet] Fillet004
  Base = -> Chamfer002
  Edges = 1 edges r=7: [Edge3]
FEATURE [Part::Fillet] Fillet005
  Base = -> Chamfer
  Edges = 1 edges r=7: [Edge15]
FEATURE [Part::MultiFuse] Fusion057  label="removeForScrewHolesRight"
  Shapes = -> [Fusion027,Fusion037]
FEATURE [Part::MultiFuse] Fusion058  label="removeFromScrewHolesLeft"
  Shapes = -> [Fusion024,Fusion032]
FEATURE [Part::Cylinder] Cylinder024
  Angle = 360
  AttacherType = Attacher::AttachEngine3D
  Height = 10
  Placement = pos=(-49,103,-5) rot=(-1,0,0;0.328122rad)
  Radius = 1.1
FEATURE [Part::Cylinder] Cylinder025
  Angle = 360
  AttacherType = Attacher::AttachEngine3D
  Height = 30
  Placement = pos=(-49,106,4) rot=(-1,0,0;0.328122rad)
  Radius = 3
FEATURE [Part::MultiFuse] Fusion059
  Placement = pos=(15,0,0) rot=(0,0,1;0rad)
  Shapes = -> [Cylinder024,Cylinder025]
FEATURE [Part::Cylinder] Cylinder026
  Angle = 360
  AttacherType = Attacher::AttachEngine3D
  Height = 10
  Placement = pos=(-49,103,-5) rot=(-1,0,0;0.328122rad)
  Radius = 1.1
FEATURE [Part::Cylinder] Cylinder027
  Angle = 360
  AttacherType = Attacher::AttachEngine3D
  Height = 30
  Placement = pos=(-49,106,4) rot=(-1,0,0;0.328122rad)
  Radius = 3
FEATURE [Part::MultiFuse] Fusion061
  Placement = pos=(15,-32,0) rot=(0,0,1;0rad)
  Shapes = -> [Cylinder026,Cylinder027]
FEATURE [Part::MultiFuse] Fusion063
  Shapes = -> [Fusion059,Fusion061]
FEATURE [Part::Cylinder] Cylinder028
  Angle = 360
  AttacherType = Attacher::AttachEngine3D
  Height = 10
  Placement = pos=(-49,103,-5) rot=(-1,0,0;0.328122rad)
  Radius = 1.1
FEATURE [Part::Cylinder] Cylinder029
  Angle = 360
  AttacherType = Attacher::AttachEngine3D
  Height = 30
  Placement = pos=(-49,106,4) rot=(-1,0,0;0.328122rad)
  Radius = 3
FEATURE [Part::MultiFuse] Fusion060
  Placement = pos=(31,0,0) rot=(0,0,1;0rad)
  Shapes = -> [Cylinder028,Cylinder029]
FEATURE [Part::Cylinder] Cylinder030
  Angle = 360
  AttacherType = Attacher::AttachEngine3D
  Height = 10
  Placement = pos=(-49,103,-5) rot=(-1,0,0;0.328122rad)
  Radius = 1.1
FEATURE [Part::Cylinder] Cylinder031
  Angle = 360
  AttacherType = Attacher::AttachEngine3D
  Height = 30
  Placement = pos=(-49,106,4) rot=(-1,0,0;0.328122rad)
  Radius = 3
FEATURE [Part::MultiFuse] Fusion065
  Placement = pos=(31,-29.4,0) rot=(0,0,1;0rad)
  Shapes = -> [Cylinder030,Cylinder031]
FEATURE [Part::Cylinder] Cylinder032
  Angle = 360
  AttacherType = Attacher::AttachEngine3D
  Height = 10
  Placement = pos=(-49,103,-5) rot=(-1,0,0;0.328122rad)
  Radius = 1.1
FEATURE [Part::Cylinder] Cylinder033
  Angle = 360
  AttacherType = Attacher::AttachEngine3D
  Height = 30
  Placement = pos=(-49,106,4) rot=(-1,0,0;0.328122rad)
  Radius = 3
FEATURE [Part::MultiFuse] Fusion064
  Placement = pos=(63,0,0) rot=(0,0,1;0rad)
  Shapes = -> [Cylinder032,Cylinder033]
FEATURE [Part::Cylinder] Cylinder034
  Angle = 360
  AttacherType = Attacher::AttachEngine3D
  Height = 10
  Placement = pos=(-49,103,-5) rot=(-1,0,0;0.328122rad)
  Radius = 1.1
FEATURE [Part::Cylinder] Cylinder035
  Angle = 360
  AttacherType = Attacher::AttachEngine3D
  Height = 30
  Placement = pos=(-49,106,4) rot=(-1,0,0;0.328122rad)
  Radius = 3
FEATURE [Part::MultiFuse] Fusion066
  Placement = pos=(63,-29.4,0) rot=(0,0,1;0rad)
  Shapes = -> [Cylinder034,Cylinder035]
FEATURE [Part::MultiFuse] Fusion067
  Shapes = -> [Fusion066,Fusion065,Fusion064,Fusion060]
FEATURE [Part::MultiFuse] Fusion062  label="removeFromScrewHolesLeft001"
  Shapes = -> [Fusion063,Fusion067]
FEATURE [Part::Cut] Cut028
  Base = -> Cut018
  Tool = -> Fusion058
FEATURE [Part::Cylinder] Cylinder036
  Angle = 360
  AttacherType = Attacher::AttachEngine3D
  Height = 10
  Placement = pos=(-49,103,-5) rot=(-1,0,0;0.328122rad)
  Radius = 1.1
FEATURE [Part::Cylinder] Cylinder037
  Angle = 360
  AttacherType = Attacher::AttachEngine3D
  Height = 30
  Placement = pos=(-49,106,4) rot=(-1,0,0;0.328122rad)
  Radius = 3
FEATURE [Part::Cylinder] Cylinder038
  Angle = 360
  AttacherType = Attacher::AttachEngine3D
  Height = 10
  Placement = pos=(-49,103,-5) rot=(-1,0,0;0.328122rad)
  Radius = 1.1
FEATURE [Part::Cylinder] Cylinder039
  Angle = 360
  AttacherType = Attacher::AttachEngine3D
  Height = 30
  Placement = pos=(-49,106,4) rot=(-1,0,0;0.328122rad)
  Radius = 3
FEATURE [Part::MultiFuse] Fusion068
  Placement = pos=(15,0,0) rot=(0,0,1;0rad)
  Shapes = -> [Cylinder038,Cylinder039]
FEATURE [Part::Cylinder] Cylinder040
  Angle = 360
  AttacherType = Attacher::AttachEngine3D
  Height = 10
  Placement = pos=(-49,103,-5) rot=(-1,0,0;0.328122rad)
  Radius = 1.1
FEATURE [Part::Cylinder] Cylinder041
  Angle = 360
  AttacherType = Attacher::AttachEngine3D
  Height = 30
  Placement = pos=(-49,106,4) rot=(-1,0,0;0.328122rad)
  Radius = 3
FEATURE [Part::MultiFuse] Fusion069
  Placement = pos=(15,-32,0) rot=(0,0,1;0rad)
  Shapes = -> [Cylinder040,Cylinder041]
FEATURE [Part::MultiFuse] Fusion070
  Placement = pos=(432,0,0) rot=(0,0,1;0rad)
  Shapes = -> [Fusion068,Fusion069]
FEATURE [Part::Cylinder] Cylinder042
  Angle = 360
  AttacherType = Attacher::AttachEngine3D
  Height = 10
  Placement = pos=(-49,103,-5) rot=(-1,0,0;0.328122rad)
  Radius = 1.1
FEATURE [Part::Cylinder] Cylinder043
  Angle = 360
  AttacherType = Attacher::AttachEngine3D
  Height = 30
  Placement = pos=(-49,106,4) rot=(-1,0,0;0.328122rad)
  Radius = 3
FEATURE [Part::MultiFuse] Fusion072
  Placement = pos=(63,0,0) rot=(0,0,1;0rad)
  Shapes = -> [Cylinder042,Cylinder043]
FEATURE [Part::Cylinder] Cylinder044
  Angle = 360
  AttacherType = Attacher::AttachEngine3D
  Height = 10
  Placement = pos=(-49,103,-5) rot=(-1,0,0;0.328122rad)
  Radius = 1.1
FEATURE [Part::Cylinder] Cylinder045
  Angle = 360
  AttacherType = Attacher::AttachEngine3D
  Height = 30
  Placement = pos=(-49,106,4) rot=(-1,0,0;0.328122rad)
  Radius = 3
FEATURE [Part::MultiFuse] Fusion073
  Placement = pos=(31,-29.4,0) rot=(0,0,1;0rad)
  Shapes = -> [Cylinder036,Cylinder037]
FEATURE [Part::MultiFuse] Fusion074
  Placement = pos=(63,-29.4,0) rot=(0,0,1;0rad)
  Shapes = -> [Cylinder044,Cylinder045]
FEATURE [Part::Cylinder] Cylinder046
  Angle = 360
  AttacherType = Attacher::AttachEngine3D
  Height = 10
  Placement = pos=(-49,103,-5) rot=(-1,0,0;0.328122rad)
  Radius = 1.1
FEATURE [Part::Cylinder] Cylinder047
  Angle = 360
  AttacherType = Attacher::AttachEngine3D
  Height = 30
  Placement = pos=(-49,106,4) rot=(-1,0,0;0.328122rad)
  Radius = 3
FEATURE [Part::MultiFuse] Fusion071
  Placement = pos=(31,0,0) rot=(0,0,1;0rad)
  Shapes = -> [Cylinder046,Cylinder047]
FEATURE [Part::MultiFuse] Fusion075
  Placement = pos=(369,0,0) rot=(0,0,1;0rad)
  Shapes = -> [Fusion074,Fusion073,Fusion072,Fusion071]
FEATURE [Part::MultiFuse] Fusion076  label="removeForScrewHolesRight001"
  Shapes = -> [Fusion070,Fusion075]
FEATURE [Part::Cut] Cut029
  Base = -> Cut022
  Tool = -> Fusion057
FEATURE [Part::Cylinder] Cylinder048
  Angle = 360
  AttacherType = Attacher::AttachEngine3D
  Height = 10
  Placement = pos=(-49,103,-5) rot=(-1,0,0;0.328122rad)
  Radius = 1.1
FEATURE [Part::Cylinder] Cylinder049
  Angle = 360
  AttacherType = Attacher::AttachEngine3D
  Height = 30
  Placement = pos=(-49,106,4) rot=(-1,0,0;0.328122rad)
  Radius = 3
FEATURE [Part::Cylinder] Cylinder050
  Angle = 360
  AttacherType = Attacher::AttachEngine3D
  Height = 10
  Placement = pos=(-49,103,-5) rot=(-1,0,0;0.328122rad)
  Radius = 1.1
FEATURE [Part::Cylinder] Cylinder051
  Angle = 360
  AttacherType = Attacher::AttachEngine3D
  Height = 30
  Placement = pos=(-49,106,4) rot=(-1,0,0;0.328122rad)
  Radius = 3
FEATURE [Part::Cylinder] Cylinder052
  Angle = 360
  AttacherType = Attacher::AttachEngine3D
  Height = 10
  Placement = pos=(-49,103,-5) rot=(-1,0,0;0.328122rad)
  Radius = 1.1
FEATURE [Part::Cylinder] Cylinder053
  Angle = 360
  AttacherType = Attacher::AttachEngine3D
  Height = 30
  Placement = pos=(-49,106,4) rot=(-1,0,0;0.328122rad)
  Radius = 3
FEATURE [Part::Cylinder] Cylinder054
  Angle = 360
  AttacherType = Attacher::AttachEngine3D
  Height = 10
  Placement = pos=(-49,103,-5) rot=(-1,0,0;0.328122rad)
  Radius = 1.1
FEATURE [Part::MultiFuse] Fusion078
  Placement = pos=(63,0,0) rot=(0,0,1;0rad)
  Shapes = -> [Cylinder048,Cylinder049]
FEATURE [Part::MultiFuse] Fusion079
  Placement = pos=(31,-29.4,0) rot=(0,0,1;0rad)
  Shapes = -> [Cylinder054,Cylinder053]
FEATURE [Part::MultiFuse] Fusion081
  Placement = pos=(63,-29.4,0) rot=(0,0,1;0rad)
  Shapes = -> [Cylinder050,Cylinder051]
FEATURE [Part::Cylinder] Cylinder055
  Angle = 360
  AttacherType = Attacher::AttachEngine3D
  Height = 10
  Placement = pos=(-49,103,-5) rot=(-1,0,0;0.328122rad)
  Radius = 1.1
FEATURE [Part::Cylinder] Cylinder056
  Angle = 360
  AttacherType = Attacher::AttachEngine3D
  Height = 30
  Placement = pos=(-49,106,4) rot=(-1,0,0;0.328122rad)
  Radius = 3
FEATURE [Part::MultiFuse] Fusion080
  Placement = pos=(15,0,0) rot=(0,0,1;0rad)
  Shapes = -> [Cylinder055,Cylinder056]
FEATURE [Part::Cylinder] Cylinder057
  Angle = 360
  AttacherType = Attacher::AttachEngine3D
  Height = 10
  Placement = pos=(-49,103,-5) rot=(-1,0,0;0.328122rad)
  Radius = 1.1
FEATURE [Part::Cylinder] Cylinder058
  Angle = 360
  AttacherType = Attacher::AttachEngine3D
  Height = 30
  Placement = pos=(-49,106,4) rot=(-1,0,0;0.328122rad)
  Radius = 3
FEATURE [Part::MultiFuse] Fusion083
  Placement = pos=(15,-32,0) rot=(0,0,1;0rad)
  Shapes = -> [Cylinder057,Cylinder058]
FEATURE [Part::MultiFuse] Fusion077
  Shapes = -> [Fusion080,Fusion083]
FEATURE [Part::Cylinder] Cylinder059
  Angle = 360
  AttacherType = Attacher::AttachEngine3D
  Height = 30
  Placement = pos=(-49,106,4) rot=(-1,0,0;0.328122rad)
  Radius = 3
FEATURE [Part::MultiFuse] Fusion082
  Placement = pos=(31,0,0) rot=(0,0,1;0rad)
  Shapes = -> [Cylinder052,Cylinder059]
FEATURE [Part::MultiFuse] Fusion085
  Shapes = -> [Fusion081,Fusion079,Fusion078,Fusion082]
FEATURE [Part::MultiFuse] Fusion084  label="removeFromScrewHolesLeft002"
  Shapes = -> [Fusion077,Fusion085]
FEATURE [Part::Cylinder] Cylinder060
  Angle = 360
  AttacherType = Attacher::AttachEngine3D
  Height = 30
  Placement = pos=(-49,106,4) rot=(-1,0,0;0.328122rad)
  Radius = 3
FEATURE [Part::Cylinder] Cylinder061
  Angle = 360
  AttacherType = Attacher::AttachEngine3D
  Height = 10
  Placement = pos=(-49,103,-5) rot=(-1,0,0;0.328122rad)
  Radius = 1.1
FEATURE [Part::Cylinder] Cylinder062
  Angle = 360
  AttacherType = Attacher::AttachEngine3D
  Height = 30
  Placement = pos=(-49,106,4) rot=(-1,0,0;0.328122rad)
  Radius = 3
FEATURE [Part::Cylinder] Cylinder063
  Angle = 360
  AttacherType = Attacher::AttachEngine3D
  Height = 30
  Placement = pos=(-49,106,4) rot=(-1,0,0;0.328122rad)
  Radius = 3
FEATURE [Part::Cylinder] Cylinder064
  Angle = 360
  AttacherType = Attacher::AttachEngine3D
  Height = 10
  Placement = pos=(-49,103,-5) rot=(-1,0,0;0.328122rad)
  Radius = 1.1
FEATURE [Part::Cylinder] Cylinder065
  Angle = 360
  AttacherType = Attacher::AttachEngine3D
  Height = 30
  Placement = pos=(-49,106,4) rot=(-1,0,0;0.328122rad)
  Radius = 3
FEATURE [Part::Cylinder] Cylinder066
  Angle = 360
  AttacherType = Attacher::AttachEngine3D
  Height = 10
  Placement = pos=(-49,103,-5) rot=(-1,0,0;0.328122rad)
  Radius = 1.1
FEATURE [Part::Cylinder] Cylinder067
  Angle = 360
  AttacherType = Attacher::AttachEngine3D
  Height = 30
  Placement = pos=(-49,106,4) rot=(-1,0,0;0.328122rad)
  Radius = 3
FEATURE [Part::Cylinder] Cylinder068
  Angle = 360
  AttacherType = Attacher::AttachEngine3D
  Height = 10
  Placement = pos=(-49,103,-5) rot=(-1,0,0;0.328122rad)
  Radius = 1.1
FEATURE [Part::Cylinder] Cylinder069
  Angle = 360
  AttacherType = Attacher::AttachEngine3D
  Height = 30
  Placement = pos=(-49,106,4) rot=(-1,0,0;0.328122rad)
  Radius = 3
FEATURE [Part::Cylinder] Cylinder070
  Angle = 360
  AttacherType = Attacher::AttachEngine3D
  Height = 10
  Placement = pos=(-49,103,-5) rot=(-1,0,0;0.328122rad)
  Radius = 1.1
FEATURE [Part::Cylinder] Cylinder071
  Angle = 360
  AttacherType = Attacher::AttachEngine3D
  Height = 10
  Placement = pos=(-49,103,-5) rot=(-1,0,0;0.328122rad)
  Radius = 1.1
FEATURE [Part::MultiFuse] Fusion087
  Placement = pos=(63,0,0) rot=(0,0,1;0rad)
  Shapes = -> [Cylinder064,Cylinder065]
FEATURE [Part::MultiFuse] Fusion088
  Placement = pos=(31,-29.4,0) rot=(0,0,1;0rad)
  Shapes = -> [Cylinder070,Cylinder069]
FEATURE [Part::MultiFuse] Fusion089
  Placement = pos=(15,0,0) rot=(0,0,1;0rad)
  Shapes = -> [Cylinder071,Cylinder060]
FEATURE [Part::MultiFuse] Fusion090
  Placement = pos=(63,-29.4,0) rot=(0,0,1;0rad)
  Shapes = -> [Cylinder066,Cylinder067]
FEATURE [Part::MultiFuse] Fusion091
  Placement = pos=(31,0,0) rot=(0,0,1;0rad)
  Shapes = -> [Cylinder068,Cylinder063]
FEATURE [Part::MultiFuse] Fusion092
  Placement = pos=(15,-32,0) rot=(0,0,1;0rad)
  Shapes = -> [Cylinder061,Cylinder062]
FEATURE [Part::MultiFuse] Fusion086
  Shapes = -> [Fusion089,Fusion092]
FEATURE [Part::MultiFuse] Fusion094
  Shapes = -> [Fusion090,Fusion088,Fusion087,Fusion091]
FEATURE [Part::MultiFuse] Fusion093  label="removeFromScrewHolesLeft003"
  Shapes = -> [Fusion086,Fusion094]
FEATURE [Part::Cut] Cut030
  Base = -> Fillet001
  Tool = -> Fusion062
FEATURE [Part::Cut] Cut031
  Base = -> Cut026
  Placement = pos=(0,0,0.08) rot=(0,0,1;0rad)
  Tool = -> Fusion084
FEATURE [Part::Cut] Cut032
  Base = -> Fillet
  Tool = -> Fusion093
FEATURE [Part::Cylinder] Cylinder072
  Angle = 360
  AttacherType = Attacher::AttachEngine3D
  Height = 10
  Placement = pos=(-49,103,-5) rot=(-1,0,0;0.328122rad)
  Radius = 1.1
FEATURE [Part::Cylinder] Cylinder073
  Angle = 360
  AttacherType = Attacher::AttachEngine3D
  Height = 30
  Placement = pos=(-49,106,4) rot=(-1,0,0;0.328122rad)
  Radius = 3
FEATURE [Part::Cylinder] Cylinder074
  Angle = 360
  AttacherType = Attacher::AttachEngine3D
  Height = 10
  Placement = pos=(-49,103,-5) rot=(-1,0,0;0.328122rad)
  Radius = 1.1
FEATURE [Part::Cylinder] Cylinder075
  Angle = 360
  AttacherType = Attacher::AttachEngine3D
  Height = 30
  Placement = pos=(-49,106,4) rot=(-1,0,0;0.328122rad)
  Radius = 3
FEATURE [Part::Cylinder] Cylinder076
  Angle = 360
  AttacherType = Attacher::AttachEngine3D
  Height = 10
  Placement = pos=(-49,103,-5) rot=(-1,0,0;0.328122rad)
  Radius = 1.1
FEATURE [Part::Cylinder] Cylinder077
  Angle = 360
  AttacherType = Attacher::AttachEngine3D
  Height = 30
  Placement = pos=(-49,106,4) rot=(-1,0,0;0.328122rad)
  Radius = 3
FEATURE [Part::MultiFuse] Fusion098
  Placement = pos=(31,0,0) rot=(0,0,1;0rad)
  Shapes = -> [Cylinder074,Cylinder075]
FEATURE [Part::Cylinder] Cylinder078
  Angle = 360
  AttacherType = Attacher::AttachEngine3D
  Height = 10
  Placement = pos=(-49,103,-5) rot=(-1,0,0;0.328122rad)
  Radius = 1.1
FEATURE [Part::Cylinder] Cylinder079
  Angle = 360
  AttacherType = Attacher::AttachEngine3D
  Height = 30
  Placement = pos=(-49,106,4) rot=(-1,0,0;0.328122rad)
  Radius = 3
FEATURE [Part::MultiFuse] Fusion095
  Placement = pos=(15,0,0) rot=(0,0,1;0rad)
  Shapes = -> [Cylinder078,Cylinder079]
FEATURE [Part::Cylinder] Cylinder080
  Angle = 360
  AttacherType = Attacher::AttachEngine3D
  Height = 10
  Placement = pos=(-49,103,-5) rot=(-1,0,0;0.328122rad)
  Radius = 1.1
FEATURE [Part::Cylinder] Cylinder081
  Angle = 360
  AttacherType = Attacher::AttachEngine3D
  Height = 30
  Placement = pos=(-49,106,4) rot=(-1,0,0;0.328122rad)
  Radius = 3
FEATURE [Part::MultiFuse] Fusion096
  Placement = pos=(15,-32,0) rot=(0,0,1;0rad)
  Shapes = -> [Cylinder080,Cylinder081]
FEATURE [Part::MultiFuse] Fusion097
  Placement = pos=(432,0,0) rot=(0,0,1;0rad)
  Shapes = -> [Fusion095,Fusion096]
FEATURE [Part::Cylinder] Cylinder082
  Angle = 360
  AttacherType = Attacher::AttachEngine3D
  Height = 10
  Placement = pos=(-49,103,-5) rot=(-1,0,0;0.328122rad)
  Radius = 1.1
FEATURE [Part::Cylinder] Cylinder083
  Angle = 360
  AttacherType = Attacher::AttachEngine3D
  Height = 30
  Placement = pos=(-49,106,4) rot=(-1,0,0;0.328122rad)
  Radius = 3
FEATURE [Part::MultiFuse] Fusion099
  Placement = pos=(63,0,0) rot=(0,0,1;0rad)
  Shapes = -> [Cylinder082,Cylinder083]
FEATURE [Part::MultiFuse] Fusion100
  Placement = pos=(31,-29.4,0) rot=(0,0,1;0rad)
  Shapes = -> [Cylinder076,Cylinder077]
FEATURE [Part::MultiFuse] Fusion101
  Placement = pos=(63,-29.4,0) rot=(0,0,1;0rad)
  Shapes = -> [Cylinder072,Cylinder073]
FEATURE [Part::MultiFuse] Fusion102
  Placement = pos=(369,0,0) rot=(0,0,1;0rad)
  Shapes = -> [Fusion101,Fusion100,Fusion099,Fusion098]
FEATURE [Part::MultiFuse] Fusion103  label="removeForScrewHolesRight002"
  Shapes = -> [Fusion097,Fusion102]
FEATURE [Part::Cylinder] Cylinder084
  Angle = 360
  AttacherType = Attacher::AttachEngine3D
  Height = 10
  Placement = pos=(-49,103,-5) rot=(-1,0,0;0.328122rad)
  Radius = 1.1
FEATURE [Part::Cylinder] Cylinder085
  Angle = 360
  AttacherType = Attacher::AttachEngine3D
  Height = 30
  Placement = pos=(-49,106,4) rot=(-1,0,0;0.328122rad)
  Radius = 3
FEATURE [Part::Cylinder] Cylinder086
  Angle = 360
  AttacherType = Attacher::AttachEngine3D
  Height = 10
  Placement = pos=(-49,103,-5) rot=(-1,0,0;0.328122rad)
  Radius = 1.1
FEATURE [Part::Cylinder] Cylinder087
  Angle = 360
  AttacherType = Attacher::AttachEngine3D
  Height = 30
  Placement = pos=(-49,106,4) rot=(-1,0,0;0.328122rad)
  Radius = 3
FEATURE [Part::Cylinder] Cylinder088
  Angle = 360
  AttacherType = Attacher::AttachEngine3D
  Height = 10
  Placement = pos=(-49,103,-5) rot=(-1,0,0;0.328122rad)
  Radius = 1.1
FEATURE [Part::Cylinder] Cylinder089
  Angle = 360
  AttacherType = Attacher::AttachEngine3D
  Height = 30
  Placement = pos=(-49,106,4) rot=(-1,0,0;0.328122rad)
  Radius = 3
FEATURE [Part::MultiFuse] Fusion107
  Placement = pos=(31,0,0) rot=(0,0,1;0rad)
  Shapes = -> [Cylinder086,Cylinder087]
FEATURE [Part::Cylinder] Cylinder090
  Angle = 360
  AttacherType = Attacher::AttachEngine3D
  Height = 10
  Placement = pos=(-49,103,-5) rot=(-1,0,0;0.328122rad)
  Radius = 1.1
FEATURE [Part::Cylinder] Cylinder091
  Angle = 360
  AttacherType = Attacher::AttachEngine3D
  Height = 30
  Placement = pos=(-49,106,4) rot=(-1,0,0;0.328122rad)
  Radius = 3
FEATURE [Part::MultiFuse] Fusion104
  Placement = pos=(15,0,0) rot=(0,0,1;0rad)
  Shapes = -> [Cylinder090,Cylinder091]
FEATURE [Part::Cylinder] Cylinder092
  Angle = 360
  AttacherType = Attacher::AttachEngine3D
  Height = 10
  Placement = pos=(-49,103,-5) rot=(-1,0,0;0.328122rad)
  Radius = 1.1
FEATURE [Part::Cylinder] Cylinder093
  Angle = 360
  AttacherType = Attacher::AttachEngine3D
  Height = 30
  Placement = pos=(-49,106,4) rot=(-1,0,0;0.328122rad)
  Radius = 3
FEATURE [Part::MultiFuse] Fusion105
  Placement = pos=(15,-32,0) rot=(0,0,1;0rad)
  Shapes = -> [Cylinder092,Cylinder093]
FEATURE [Part::MultiFuse] Fusion106
  Placement = pos=(432,0,0) rot=(0,0,1;0rad)
  Shapes = -> [Fusion104,Fusion105]
FEATURE [Part::Cylinder] Cylinder094
  Angle = 360
  AttacherType = Attacher::AttachEngine3D
  Height = 10
  Placement = pos=(-49,103,-5) rot=(-1,0,0;0.328122rad)
  Radius = 1.1
FEATURE [Part::Cylinder] Cylinder095
  Angle = 360
  AttacherType = Attacher::AttachEngine3D
  Height = 30
  Placement = pos=(-49,106,4) rot=(-1,0,0;0.328122rad)
  Radius = 3
FEATURE [Part::MultiFuse] Fusion108
  Placement = pos=(63,0,0) rot=(0,0,1;0rad)
  Shapes = -> [Cylinder094,Cylinder095]
FEATURE [Part::MultiFuse] Fusion109
  Placement = pos=(31,-29.4,0) rot=(0,0,1;0rad)
  Shapes = -> [Cylinder088,Cylinder089]
FEATURE [Part::MultiFuse] Fusion110
  Placement = pos=(63,-29.4,0) rot=(0,0,1;0rad)
  Shapes = -> [Cylinder084,Cylinder085]
FEATURE [Part::MultiFuse] Fusion111
  Placement = pos=(369,0,0) rot=(0,0,1;0rad)
  Shapes = -> [Fusion110,Fusion109,Fusion108,Fusion107]
FEATURE [Part::MultiFuse] Fusion112  label="removeForScrewHolesRight003"
  Shapes = -> [Fusion106,Fusion111]
FEATURE [Part::Cut] Cut033
  Base = -> Fillet003
  Tool = -> Fusion076
FEATURE [Part::Cut] Cut034
  Base = -> Fillet002
  Tool = -> Fusion103
FEATURE [Part::Cut] Cut035
  Base = -> Cut024
  Placement = pos=(0,0,0.08) rot=(0,0,1;0rad)
  Tool = -> Fusion112
FEATURE [Part::MultiFuse] Fusion113
  Shapes = -> [Fusion056,Cut032,Cut030]
FEATURE [Part::MultiFuse] Fusion114
  Shapes = -> [Fusion051,Cut033,Cut034]
FEATURE [Part::Cylinder] Cylinder096
  Angle = 360
  AttacherType = Attacher::AttachEngine3D
  Height = 10
  Placement = pos=(-49,103,-5) rot=(-1,0,0;0.328122rad)
  Radius = 1.1
FEATURE [Part::Cylinder] Cylinder097
  Angle = 360
  AttacherType = Attacher::AttachEngine3D
  Height = 30
  Placement = pos=(-49,106,4) rot=(-1,0,0;0.328122rad)
  Radius = 3
FEATURE [Part::MultiFuse] Fusion115
  Placement = pos=(15,-68.4,0) rot=(0,0,1;0rad)
  Shapes = -> [Cylinder096,Cylinder097]
FEATURE [Part::Cylinder] Cylinder098
  Angle = 360
  AttacherType = Attacher::AttachEngine3D
  Height = 10
  Placement = pos=(-49,103,-5) rot=(-1,0,0;0.328122rad)
  Radius = 1.1
FEATURE [Part::Cylinder] Cylinder099
  Angle = 360
  AttacherType = Attacher::AttachEngine3D
  Height = 30
  Placement = pos=(-49,106,4) rot=(-1,0,0;0.328122rad)
  Radius = 3
FEATURE [Part::MultiFuse] Fusion116
  Placement = pos=(15,17.6,0) rot=(0,0,1;0rad)
  Shapes = -> [Cylinder098,Cylinder099]
FEATURE [Part::Cylinder] Cylinder100
  Angle = 360
  AttacherType = Attacher::AttachEngine3D
  Height = 5
  Placement = pos=(-34,119.5,-6) rot=(-1,0,0;0.328122rad)
  Radius = 6
FEATURE [Part::Cylinder] Cylinder101
  Angle = 360
  AttacherType = Attacher::AttachEngine3D
  Height = 5
  Placement = pos=(-34,35.5,-6) rot=(-1,0,0;0.328122rad)
  Radius = 6
FEATURE [Part::Fillet] Fillet006
  Base = -> Cylinder100
  Edges = 1 edges r=4: [Edge3]
FEATURE [Part::Fillet] Fillet007
  Base = -> Cylinder101
  Edges = 1 edges r=4: [Edge3]
FEATURE [Part::MultiFuse] Fusion117
  Shapes = -> [Cut031,Fillet007]
FEATURE [Part::MultiFuse] Fusion118  label="lefttopLeg"
  Shapes = -> [Fusion117,Fillet006]
FEATURE [Part::Cylinder] Cylinder102
  Angle = 360
  AttacherType = Attacher::AttachEngine3D
  Height = 5
  Placement = pos=(-34,119.5,-6) rot=(-1,0,0;0.328122rad)
  Radius = 6
FEATURE [Part::Fillet] Fillet008
  Base = -> Cylinder102
  Edges = 1 edges r=4: [Edge3]
  Placement = pos=(432.24,0,0) rot=(0,0,1;0rad)
FEATURE [Part::Cylinder] Cylinder103
  Angle = 360
  AttacherType = Attacher::AttachEngine3D
  Height = 5
  Placement = pos=(-34,35.5,-6) rot=(-1,0,0;0.328122rad)
  Radius = 6
FEATURE [Part::Fillet] Fillet009
  Base = -> Cylinder103
  Edges = 1 edges r=4: [Edge3]
  Placement = pos=(432.24,0,0) rot=(0,0,1;0rad)
FEATURE [Part::MultiFuse] Fusion119
  Shapes = -> [Cut035,Fillet008]
FEATURE [Part::MultiFuse] Fusion120  label="rightTopLeg001"
  Shapes = -> [Fusion119,Fillet009]
FEATURE [Part::MultiFuse] Fusion121  label="removeToCreateOutterTopScrewHolesRight"
  Placement = pos=(432.24,0,0) rot=(0,0,1;0rad)
  Shapes = -> [Fusion116,Fusion115]
FEATURE [Part::Cylinder] Cylinder104
  Angle = 360
  AttacherType = Attacher::AttachEngine3D
  Height = 10
  Placement = pos=(-49,103,-5) rot=(-1,0,0;0.328122rad)
  Radius = 1.1
FEATURE [Part::Cylinder] Cylinder105
  Angle = 360
  AttacherType = Attacher::AttachEngine3D
  Height = 30
  Placement = pos=(-49,106,4) rot=(-1,0,0;0.328122rad)
  Radius = 3
FEATURE [Part::MultiFuse] Fusion122
  Placement = pos=(15,-68.4,0) rot=(0,0,1;0rad)
  Shapes = -> [Cylinder104,Cylinder105]
FEATURE [Part::Cylinder] Cylinder106
  Angle = 360
  AttacherType = Attacher::AttachEngine3D
  Height = 10
  Placement = pos=(-49,103,-5) rot=(-1,0,0;0.328122rad)
  Radius = 1.1
FEATURE [Part::Cylinder] Cylinder107
  Angle = 360
  AttacherType = Attacher::AttachEngine3D
  Height = 30
  Placement = pos=(-49,106,4) rot=(-1,0,0;0.328122rad)
  Radius = 3
FEATURE [Part::MultiFuse] Fusion123
  Placement = pos=(15,17.6,0) rot=(0,0,1;0rad)
  Shapes = -> [Cylinder106,Cylinder107]
FEATURE [Part::MultiFuse] Fusion124  label="removeToCreateOutterTopScrewHolesLeft001"
  Shapes = -> [Fusion123,Fusion122]
FEATURE [Part::Cylinder] Cylinder108
  Angle = 360
  AttacherType = Attacher::AttachEngine3D
  Height = 30
  Placement = pos=(-49,106,4) rot=(-1,0,0;0.328122rad)
  Radius = 3
FEATURE [Part::Cylinder] Cylinder109
  Angle = 360
  AttacherType = Attacher::AttachEngine3D
  Height = 10
  Placement = pos=(-49,103,-5) rot=(-1,0,0;0.328122rad)
  Radius = 1.1
FEATURE [Part::Cylinder] Cylinder110
  Angle = 360
  AttacherType = Attacher::AttachEngine3D
  Height = 30
  Placement = pos=(-49,106,4) rot=(-1,0,0;0.328122rad)
  Radius = 3
FEATURE [Part::Cylinder] Cylinder111
  Angle = 360
  AttacherType = Attacher::AttachEngine3D
  Height = 10
  Placement = pos=(-49,103,-5) rot=(-1,0,0;0.328122rad)
  Radius = 1.1
FEATURE [Part::MultiFuse] Fusion125
  Placement = pos=(15,-68.4,0) rot=(0,0,1;0rad)
  Shapes = -> [Cylinder109,Cylinder110]
FEATURE [Part::MultiFuse] Fusion126
  Placement = pos=(15,17.6,0) rot=(0,0,1;0rad)
  Shapes = -> [Cylinder111,Cylinder108]
FEATURE [Part::MultiFuse] Fusion127  label="removeToCreateOutterTopScrewHolesLeft002"
  Shapes = -> [Fusion126,Fusion125]
FEATURE [Part::Cut] Cut036
  Base = -> Fusion118
  Tool = -> Fusion127
FEATURE [Part::Cylinder] Cylinder112
  Angle = 360
  AttacherType = Attacher::AttachEngine3D
  Height = 30
  Placement = pos=(-49,106,4) rot=(-1,0,0;0.328122rad)
  Radius = 3
FEATURE [Part::Cylinder] Cylinder113
  Angle = 360
  AttacherType = Attacher::AttachEngine3D
  Height = 10
  Placement = pos=(-49,103,-5) rot=(-1,0,0;0.328122rad)
  Radius = 1.1
FEATURE [Part::Cylinder] Cylinder114
  Angle = 360
  AttacherType = Attacher::AttachEngine3D
  Height = 30
  Placement = pos=(-49,106,4) rot=(-1,0,0;0.328122rad)
  Radius = 3
FEATURE [Part::Cylinder] Cylinder115
  Angle = 360
  AttacherType = Attacher::AttachEngine3D
  Height = 10
  Placement = pos=(-49,103,-5) rot=(-1,0,0;0.328122rad)
  Radius = 1.1
FEATURE [Part::MultiFuse] Fusion128
  Placement = pos=(15,-68.4,0) rot=(0,0,1;0rad)
  Shapes = -> [Cylinder113,Cylinder114]
FEATURE [Part::MultiFuse] Fusion129
  Placement = pos=(15,17.6,0) rot=(0,0,1;0rad)
  Shapes = -> [Cylinder115,Cylinder112]
FEATURE [Part::MultiFuse] Fusion130  label="removeToCreateOutterTopScrewHolesLeft003"
  Shapes = -> [Fusion129,Fusion128]
FEATURE [Part::Cut] Cut037  label="topLeftBase"
  Base = -> Cut028
  Tool = -> Fusion124
FEATURE [Part::Cut] Cut038  label="bottomLeftBase"
  Base = -> Cut012
  Tool = -> Fusion130
FEATURE [Part::Cylinder] Cylinder116
  Angle = 360
  AttacherType = Attacher::AttachEngine3D
  Height = 10
  Placement = pos=(-49,103,-5) rot=(-1,0,0;0.328122rad)
  Radius = 1.1
FEATURE [Part::Cylinder] Cylinder117
  Angle = 360
  AttacherType = Attacher::AttachEngine3D
  Height = 30
  Placement = pos=(-49,106,4) rot=(-1,0,0;0.328122rad)
  Radius = 3
FEATURE [Part::MultiFuse] Fusion131
  Placement = pos=(15,-68.4,0) rot=(0,0,1;0rad)
  Shapes = -> [Cylinder116,Cylinder117]
FEATURE [Part::Cylinder] Cylinder118
  Angle = 360
  AttacherType = Attacher::AttachEngine3D
  Height = 10
  Placement = pos=(-49,103,-5) rot=(-1,0,0;0.328122rad)
  Radius = 1.1
FEATURE [Part::Cylinder] Cylinder119
  Angle = 360
  AttacherType = Attacher::AttachEngine3D
  Height = 30
  Placement = pos=(-49,106,4) rot=(-1,0,0;0.328122rad)
  Radius = 3
FEATURE [Part::MultiFuse] Fusion132
  Placement = pos=(15,17.6,0) rot=(0,0,1;0rad)
  Shapes = -> [Cylinder118,Cylinder119]
FEATURE [Part::MultiFuse] Fusion133  label="removeToCreateOutterTopScrewHolesRight001"
  Placement = pos=(432.24,0,0) rot=(0,0,1;0rad)
  Shapes = -> [Fusion132,Fusion131]
FEATURE [Part::Cylinder] Cylinder120
  Angle = 360
  AttacherType = Attacher::AttachEngine3D
  Height = 10
  Placement = pos=(-49,103,-5) rot=(-1,0,0;0.328122rad)
  Radius = 1.1
FEATURE [Part::Cylinder] Cylinder121
  Angle = 360
  AttacherType = Attacher::AttachEngine3D
  Height = 30
  Placement = pos=(-49,106,4) rot=(-1,0,0;0.328122rad)
  Radius = 3
FEATURE [Part::MultiFuse] Fusion134
  Placement = pos=(15,-68.4,0) rot=(0,0,1;0rad)
  Shapes = -> [Cylinder120,Cylinder121]
FEATURE [Part::Cylinder] Cylinder122
  Angle = 360
  AttacherType = Attacher::AttachEngine3D
  Height = 10
  Placement = pos=(-49,103,-5) rot=(-1,0,0;0.328122rad)
  Radius = 1.1
FEATURE [Part::Cylinder] Cylinder123
  Angle = 360
  AttacherType = Attacher::AttachEngine3D
  Height = 30
  Placement = pos=(-49,106,4) rot=(-1,0,0;0.328122rad)
  Radius = 3
FEATURE [Part::MultiFuse] Fusion135
  Placement = pos=(15,17.6,0) rot=(0,0,1;0rad)
  Shapes = -> [Cylinder122,Cylinder123]
FEATURE [Part::MultiFuse] Fusion136  label="removeToCreateOutterTopScrewHolesRight002"
  Placement = pos=(432.24,0,0) rot=(0,0,1;0rad)
  Shapes = -> [Fusion135,Fusion134]
FEATURE [Part::Cut] Cut039
  Base = -> Fusion120
  Tool = -> Fusion121
FEATURE [Part::Cut] Cut040
  Base = -> Cut029
  Tool = -> Fusion133
FEATURE [Part::Cut] Cut041
  Base = -> Cut015
  Tool = -> Fusion136
FEATURE [Part::Cylinder] Cylinder124
  Angle = 360
  AttacherType = Attacher::AttachEngine3D
  Height = 10
  Placement = pos=(-49,103,-5) rot=(-1,0,0;0.328122rad)
  Radius = 1.1
FEATURE [Part::Cylinder] Cylinder125
  Angle = 360
  AttacherType = Attacher::AttachEngine3D
  Height = 30
  Placement = pos=(-49,106,4) rot=(-1,0,0;0.328122rad)
  Radius = 3
FEATURE [Sketcher::SketchObject] Sketch037  label="rightSideTop003"
  FullyConstrained = false
  sketch-geometry (93):
    g0: Circle CenterX=302.996 CenterY=111.695 CenterZ=0 NormalX=0 NormalY=0 NormalZ=1 AngleXU=0 Radius=1
    g1: Circle CenterX=306.073 CenterY=114.251 CenterZ=0 NormalX=0 NormalY=0 NormalZ=1 AngleXU=0 Radius=1
    g2: Circle CenterX=306.073 CenterY=110.251 CenterZ=0 NormalX=0 NormalY=0 NormalZ=1 AngleXU=0 Radius=1
    g3: BSplineCurve PolesCount=3 KnotsCount=2 Degree=2 IsPeriodic=0
    g4: GeomPoint X=302.996 Y=111.695 Z=0
    g5: GeomPoint X=306.073 Y=110.251 Z=0
    g6: Circle CenterX=306.073 CenterY=95.2763 CenterZ=0 NormalX=0 NormalY=0 NormalZ=1 AngleXU=0 Radius=1
    g7: Circle CenterX=306.073 CenterY=91.2763 CenterZ=0 NormalX=0 NormalY=0 NormalZ=1 AngleXU=0 Radius=1
    g8: Circle CenterX=302.567 CenterY=89.3511 CenterZ=0 NormalX=0 NormalY=0 NormalZ=1 AngleXU=0 Radius=1
    g9: BSplineCurve PolesCount=3 KnotsCount=2 Degree=2 IsPeriodic=0
    g10: GeomPoint X=306.073 Y=95.2763 Z=0
    g11: GeomPoint X=302.567 Y=89.3511 Z=0
    g12: LineSegment StartX=306.073 StartY=110.251 StartZ=0 EndX=306.073 EndY=95.2763 EndZ=0
    g13: Circle CenterX=302.073 CenterY=124.221 CenterZ=0 NormalX=0 NormalY=0 NormalZ=1 AngleXU=0 Radius=1
    g14: Circle CenterX=306.073 CenterY=124.221 CenterZ=0 NormalX=0 NormalY=0 NormalZ=1 AngleXU=0 Radius=1
    g15: Circle CenterX=302.996 CenterY=121.665 CenterZ=0 NormalX=0 NormalY=0 NormalZ=1 AngleXU=0 Radius=1
    g16: BSplineCurve PolesCount=3 KnotsCount=2 Degree=2 IsPeriodic=0
    g17: GeomPoint X=302.073 Y=124.221 Z=0
    g18: GeomPoint X=302.996 Y=121.665 Z=0
    g19: Circle CenterX=306.073 CenterY=73.3346 CenterZ=0 NormalX=0 NormalY=0 NormalZ=1 AngleXU=0 Radius=1
    g20: Circle CenterX=306.073 CenterY=77.3346 CenterZ=0 NormalX=0 NormalY=0 NormalZ=1 AngleXU=0 Radius=1
    g21: Circle CenterX=302.535 CenterY=75.4095 CenterZ=0 NormalX=0 NormalY=0 NormalZ=1 AngleXU=0 Radius=1
    g22: BSplineCurve PolesCount=3 KnotsCount=2 Degree=2 IsPeriodic=0
    g23: GeomPoint X=306.073 Y=73.3346 Z=0
    g24: GeomPoint X=302.535 Y=75.4095 Z=0
    g25: Circle CenterX=362.073 CenterY=124.221 CenterZ=0 NormalX=0 NormalY=0 NormalZ=1 AngleXU=0 Radius=1
    g26: Circle CenterX=366.073 CenterY=124.221 CenterZ=0 NormalX=0 NormalY=0 NormalZ=1 AngleXU=0 Radius=1
    g27: Circle CenterX=362.567 CenterY=122.294 CenterZ=0 NormalX=0 NormalY=0 NormalZ=1 AngleXU=0 Radius=1
    g28: BSplineCurve PolesCount=3 KnotsCount=2 Degree=2 IsPeriodic=0
    g29: GeomPoint X=362.073 Y=124.221 Z=0
    g30: GeomPoint X=362.567 Y=122.294 Z=0
    g31: Circle CenterX=322.073 CenterY=124.221 CenterZ=0 NormalX=0 NormalY=0 NormalZ=1 AngleXU=0 Radius=1
    g32: Circle CenterX=318.073 CenterY=124.221 CenterZ=0 NormalX=0 NormalY=0 NormalZ=1 AngleXU=0 Radius=1
    g33: Circle CenterX=318.073 CenterY=120.221 CenterZ=0 NormalX=0 NormalY=0 NormalZ=1 AngleXU=0 Radius=1
    g34: BSplineCurve PolesCount=3 KnotsCount=2 Degree=2 IsPeriodic=0
    g35: GeomPoint X=322.073 Y=124.221 Z=0
    g36: GeomPoint X=318.073 Y=120.221 Z=0
    g37: Circle CenterX=318.073 CenterY=109.865 CenterZ=0 NormalX=0 NormalY=0 NormalZ=1 AngleXU=0 Radius=1
    g38: GeomPoint X=318.073 Y=109.865 Z=0
    g39: Circle CenterX=322.073 CenterY=76.4095 CenterZ=0 NormalX=0 NormalY=0 NormalZ=1 AngleXU=0 Radius=4
    g40: Circle CenterX=232.072 CenterY=133.221 CenterZ=0 NormalX=0 NormalY=0 NormalZ=1 AngleXU=0 Radius=1
    g41: Circle CenterX=226.072 CenterY=136.221 CenterZ=0 NormalX=0 NormalY=0 NormalZ=1 AngleXU=0 Radius=1
    g42: Circle CenterX=226.072 CenterY=124.221 CenterZ=0 NormalX=0 NormalY=0 NormalZ=1 AngleXU=0 Radius=1
    g43: Circle CenterX=232.072 CenterY=127.221 CenterZ=0 NormalX=0 NormalY=0 NormalZ=1 AngleXU=0 Radius=1
    g44: BSplineCurve PolesCount=5 KnotsCount=3 Degree=3 IsPeriodic=0
    g45: GeomPoint X=232.072 Y=133.221 Z=0
    g46: GeomPoint X=223.072 Y=130.221 Z=0
    g47: GeomPoint X=232.072 Y=127.221 Z=0
    g48: LineSegment StartX=240.687 StartY=51.8263 StartZ=0 EndX=243.317 EndY=53.2701 EndZ=0
    g49: LineSegment StartX=243.575 StartY=46.5669 StartZ=0 EndX=246.205 EndY=48.0108 EndZ=0
    g50: ArcOfCircle CenterX=247.391 CenterY=52.0843 CenterZ=0 NormalX=0 NormalY=0 NormalZ=1 AngleXU=0 Radius=4.24264 StartAngle=4.42912 EndAngle=9.14151
    g51: LineSegment StartX=243.475 StartY=65.4951 StartZ=0 EndX=245.073 EndY=63.5726 EndZ=0
    g52: LineSegment StartX=243.575 StartY=46.5669 StartZ=0 EndX=245.072 EndY=43.8408 EndZ=0
    g53: LineSegment StartX=245.072 StartY=43.8408 StartZ=0 EndX=302.535 EndY=75.4095 EndZ=0
    g54: LineSegment StartX=239.192 StartY=54.5542 StartZ=0 EndX=302.567 EndY=89.3511 EndZ=0
    g55: LineSegment StartX=232.072 StartY=127.221 StartZ=0 EndX=232.072 EndY=124.221 EndZ=0
    g56: LineSegment StartX=232.072 StartY=136.221 StartZ=0 EndX=232.072 EndY=133.221 EndZ=0
    g57: LineSegment StartX=232.072 StartY=136.221 StartZ=0 EndX=407.073 EndY=136.221 EndZ=0
    g58: LineSegment StartX=322.073 StartY=124.221 StartZ=0 EndX=362.073 EndY=124.221 EndZ=0
    g59: LineSegment StartX=232.072 StartY=124.221 StartZ=0 EndX=302.073 EndY=124.221 EndZ=0
    g60: LineSegment StartX=302.996 StartY=121.665 StartZ=0 EndX=240.171 EndY=69.471 EndZ=0
    g61: LineSegment StartX=240.171 StartY=69.471 StartZ=0 EndX=241.711 EndY=67.6177 EndZ=0
    g62: LineSegment StartX=241.711 StartY=67.6177 StartZ=0 EndX=246.787 EndY=71.8365 EndZ=0
    g63: LineSegment StartX=246.787 StartY=71.8365 StartZ=0 EndX=248.551 EndY=69.712 EndZ=0
    g64: LineSegment StartX=248.551 StartY=69.712 StartZ=0 EndX=243.475 EndY=65.4951 EndZ=0
    g65: LineSegment StartX=245.073 StartY=63.5726 StartZ=0 EndX=302.996 EndY=111.695 EndZ=0
    g66: LineSegment StartX=239.192 StartY=54.5542 StartZ=0 EndX=240.687 EndY=51.8263 EndZ=0
    g67: LineSegment StartX=375.073 StartY=48.2206 StartZ=0 EndX=382.073 EndY=48.2206 EndZ=0
    g68: LineSegment StartX=407.073 StartY=48.2206 StartZ=0 EndX=400.073 EndY=48.2206 EndZ=0
    g69: LineSegment StartX=394.073 StartY=48.2206 StartZ=0 EndX=394.073 EndY=52.2206 EndZ=0
    g70: LineSegment StartX=388.073 StartY=48.2206 StartZ=0 EndX=388.073 EndY=58.2206 EndZ=0
    g71: ArcOfCircle CenterX=385.073 CenterY=61.2206 CenterZ=0 NormalX=0 NormalY=0 NormalZ=1 AngleXU=0 Radius=4.24264 StartAngle=5.49779 EndAngle=10.2102
    g72: ArcOfCircle CenterX=397.073 CenterY=55.2206 CenterZ=0 NormalX=0 NormalY=0 NormalZ=1 AngleXU=0 Radius=4.24264 StartAngle=5.49779 EndAngle=10.2102
    g73: LineSegment StartX=382.073 StartY=58.2206 StartZ=0 EndX=382.073 EndY=48.2206 EndZ=0
    g74: LineSegment StartX=400.073 StartY=52.2206 StartZ=0 EndX=400.073 EndY=48.2206 EndZ=0
    g75: LineSegment StartX=394.073 StartY=48.2206 StartZ=0 EndX=388.073 EndY=48.2206 EndZ=0
    g76: LineSegment StartX=306.073 StartY=-27.5935 StartZ=0 EndX=310.073 EndY=-27.5935 EndZ=0
    g77: LineSegment StartX=318.073 StartY=-27.5935 StartZ=0 EndX=314.073 EndY=-27.5935 EndZ=0
    g78: LineSegment StartX=310.073 StartY=-27.5935 StartZ=0 EndX=310.073 EndY=-31.5935 EndZ=0
    g79: LineSegment StartX=314.073 StartY=-27.5935 StartZ=0 EndX=314.073 EndY=-31.5935 EndZ=0
    g80: ArcOfCircle CenterX=312.073 CenterY=-33.5935 CenterZ=0 NormalX=0 NormalY=0 NormalZ=1 AngleXU=0 Radius=2.82843 StartAngle=2.35619 EndAngle=7.06858
    g81: LineSegment StartX=407.073 StartY=48.2206 StartZ=0 EndX=407.073 EndY=136.221 EndZ=0
    g82: LineSegment StartX=306.073 StartY=73.3346 StartZ=0 EndX=306.073 EndY=-27.5935 EndZ=0
    g83: BSplineCurve PolesCount=3 KnotsCount=2 Degree=2 IsPeriodic=0
    g84: BSplineCurve PolesCount=3 KnotsCount=2 Degree=2 IsPeriodic=0
    g85: LineSegment StartX=375.073 StartY=64.4106 StartZ=0 EndX=375.073 EndY=48.2206 EndZ=0
    g86: LineSegment StartX=318.073 StartY=64.4065 StartZ=0 EndX=318.073 EndY=-27.5935 EndZ=0
    g87: LineSegment StartX=322.073 StartY=68.4065 StartZ=0 EndX=371.073 EndY=68.4065 EndZ=0
    g88: BSplineCurve PolesCount=3 KnotsCount=2 Degree=2 IsPeriodic=0
    g89: LineSegment StartX=318.073 StartY=120.221 StartZ=0 EndX=318.073 EndY=113.865 EndZ=0
    g90: BSplineCurve PolesCount=3 KnotsCount=2 Degree=2 IsPeriodic=0
    g91: LineSegment StartX=322.073 StartY=109.865 StartZ=0 EndX=328.643 EndY=109.865 EndZ=0
    g92: LineSegment StartX=336.157 StartY=111.779 StartZ=0 EndX=362.567 EndY=122.294 EndZ=0
  constraints (140):
    c: Weight(g0) = 1
    c: Equal(g0,g1)
    c: Equal(g0,g2)
    c: InternalAlignment(g0,g3)
    c: InternalAlignment(g1,g3)
    c: InternalAlignment(g2,g3)
    c: InternalAlignment(g4,g3)
    c: InternalAlignment(g5,g3)
    c: Weight(g6) = 1
    c: Equal(g6,g7)
    c: Equal(g6,g8)
    c: InternalAlignment(g6,g9)
    c: InternalAlignment(g7,g9)
    c: InternalAlignment(g8,g9)
    c: InternalAlignment(g10,g9)
    c: InternalAlignment(g11,g9)
    c: Block(g3)
    c: Block(g9)
    c: Coincident(g12,g3)
    c: Coincident(g12,g9)
    c: Vertical(g12)
    c: Weight(g13) = 1
    c: Equal(g13,g14)
    c: Equal(g13,g15)
    c: InternalAlignment(g14,g16)
    c: InternalAlignment(g15,g16)
    c: InternalAlignment(g17,g16)
    c: InternalAlignment(g18,g16)
    c: Block(g51)
    c: Block(g52)
    c: Coincident(g53,g52)
    c: Coincident(g53,g22)
    c: Block(g53)
    c: Coincident(g50,g49)
    c: Coincident(g50,g48)
    c: Coincident(g54,g9)
    c: Block(g54)
    c: Distance(g51) = 2.5
    c: Block(g44)
    c: Coincident(g55,g44)
    c: Vertical(g55)
    c: Coincident(g56,g44)
    c: Vertical(g56)
    c: Coincident(g57,g56)
    c: Horizontal(g57)
    c: Coincident(g58,g34)
    c: Coincident(g58,g28)
    c: Horizontal(g58)
    c: Block(g34)
    c: Block(g28)
    c: Coincident(g59,g55)
    c: Coincident(g59,g16)
    c: Horizontal(g59)
    c: Coincident(g60,g16)
    c: Block(g59)
    c: Block(g60)
    c: Block(g16)
    c: Coincident(g61,g60)
    c: Block(g61)
    c: Coincident(g62,g61)
    c: Block(g62)
    c: Coincident(g63,g62)
    c: Coincident(g64,g63)
    c: Coincident(g64,g51)
    c: Block(g64)
    c: Coincident(g65,g51)
    c: Coincident(g65,g3)
    c: Block(g65)
    c: Coincident(g66,g54)
    c: Coincident(g66,g48)
    c: Block(g50)
    c: Block(g48)
    c: Block(g49)
    c: Block(g22)
    c: Horizontal(g67)
    c: Distance(g67) = 7
    c: Horizontal(g68)
    c: Distance(g68) = 7
    c: Vertical(g69)
    c: Distance(g69) = 4
    c: Vertical(g70)
    c: Distance(g70) = 10
    c: Coincident(g71,g70)
    c: Coincident(g72,g69)
    c: Block(g72)
    c: Block(g71)
    c: Coincident(g73,g71)
    c: Coincident(g73,g67)
    c: Vertical(g73)
    c: Coincident(g74,g72)
    c: Coincident(g74,g68)
    c: Vertical(g74)
    c: Coincident(g75,g69)
    c: Coincident(g75,g70)
    c: Horizontal(g75)
    c: Horizontal(g76)
    c: Distance(g76) = 4
    c: Horizontal(g77)
    c: Distance(g77) = 4
    c: Coincident(g78,g76)
    c: Vertical(g78)
    c: Coincident(g79,g77)
    c: Vertical(g79)
    c: Distance(g78) = 4
    c: Distance(g79) = 4
    c: Coincident(g80,g78)
    c: Coincident(g80,g79)
    c: Block(g80)
    c: Coincident(g81,g68)
    c: Coincident(g81,g57)
    c: Vertical(g81)
    c: Block(g57)
    c: Block(g81)
    c: Coincident(g82,g22)
    c: Coincident(g82,g76)
    c: Vertical(g82)
    c: Block(g67)
    c: Block(g83)
    c: Block(g84)
    c: Coincident(g85,g83)
    c: Coincident(g85,g67)
    c: Vertical(g85)
    c: Coincident(g86,g84)
    c: Coincident(g86,g77)
    c: Vertical(g86)
    c: Coincident(g87,g84)
    c: Coincident(g87,g83)
    c: Horizontal(g87)
    c: Block(g88)
    c: Coincident(g89,g34)
    c: Coincident(g89,g88)
    c: Vertical(g89)
    c: Block(g90)
    c: Coincident(g91,g88)
    c: Coincident(g91,g90)
    c: Horizontal(g91)
    c: Coincident(g92,g90)
    c: Coincident(g92,g28)
    c: Distance(g57) = 175.001
    c: Distance(g81) = 88
FEATURE [Part::Extrusion] Extrude038
  Base = -> Sketch037
  Dir = (0,0,1)
  DirMode = 2
  FaceMakerClass = Part::FaceMakerBullseye
  LengthFwd = 28
  LengthRev = 0
  Solid = true
  Symmetric = false
FEATURE [Part::Box] Box059  label="removeFromtTop010"
  AttacherType = Attacher::AttachEngine3D
  Height = 56
  Length = 470
  Placement = pos=(-47.93,-106.78,8) rot=(1,0,0;0.080285rad)
  Width = 260
FEATURE [Part::Cut] Cut042
  Base = -> Extrude038
  Tool = -> Box059
FEATURE [Part::Cylinder] Cylinder126
  Angle = 360
  AttacherType = Attacher::AttachEngine3D
  Height = 10
  Placement = pos=(-49,103,-5) rot=(-1,0,0;0.328122rad)
  Radius = 1.1
FEATURE [Part::Cylinder] Cylinder127
  Angle = 360
  AttacherType = Attacher::AttachEngine3D
  Height = 30
  Placement = pos=(-49,106,4) rot=(-1,0,0;0.328122rad)
  Radius = 3
FEATURE [Part::MultiFuse] Fusion137
  Placement = pos=(15,0,0) rot=(0,0,1;0rad)
  Shapes = -> [Cylinder126,Cylinder127]
FEATURE [Part::Cylinder] Cylinder128
  Angle = 360
  AttacherType = Attacher::AttachEngine3D
  Height = 10
  Placement = pos=(-49,103,-5) rot=(-1,0,0;0.328122rad)
  Radius = 1.1
FEATURE [Part::Cylinder] Cylinder129
  Angle = 360
  AttacherType = Attacher::AttachEngine3D
  Height = 30
  Placement = pos=(-49,106,4) rot=(-1,0,0;0.328122rad)
  Radius = 3
FEATURE [Part::MultiFuse] Fusion138
  Placement = pos=(15,-32,0) rot=(0,0,1;0rad)
  Shapes = -> [Cylinder128,Cylinder129]
FEATURE [Part::MultiFuse] Fusion139
  Placement = pos=(432,0,0) rot=(0,0,1;0rad)
  Shapes = -> [Fusion137,Fusion138]
FEATURE [Part::Cylinder] Cylinder130
  Angle = 360
  AttacherType = Attacher::AttachEngine3D
  Height = 10
  Placement = pos=(-49,103,-5) rot=(-1,0,0;0.328122rad)
  Radius = 1.1
FEATURE [Part::Cylinder] Cylinder131
  Angle = 360
  AttacherType = Attacher::AttachEngine3D
  Height = 30
  Placement = pos=(-49,106,4) rot=(-1,0,0;0.328122rad)
  Radius = 3
FEATURE [Part::MultiFuse] Fusion141
  Placement = pos=(63,0,0) rot=(0,0,1;0rad)
  Shapes = -> [Cylinder130,Cylinder131]
FEATURE [Part::Cylinder] Cylinder132
  Angle = 360
  AttacherType = Attacher::AttachEngine3D
  Height = 10
  Placement = pos=(-49,103,-5) rot=(-1,0,0;0.328122rad)
  Radius = 1.1
FEATURE [Part::Cylinder] Cylinder133
  Angle = 360
  AttacherType = Attacher::AttachEngine3D
  Height = 30
  Placement = pos=(-49,106,4) rot=(-1,0,0;0.328122rad)
  Radius = 3
FEATURE [Part::MultiFuse] Fusion142
  Placement = pos=(31,-29.4,0) rot=(0,0,1;0rad)
  Shapes = -> [Cylinder124,Cylinder125]
FEATURE [Part::MultiFuse] Fusion143
  Placement = pos=(63,-29.4,0) rot=(0,0,1;0rad)
  Shapes = -> [Cylinder132,Cylinder133]
FEATURE [Part::Cylinder] Cylinder134
  Angle = 360
  AttacherType = Attacher::AttachEngine3D
  Height = 10
  Placement = pos=(-49,103,-5) rot=(-1,0,0;0.328122rad)
  Radius = 1.1
FEATURE [Part::Cylinder] Cylinder135
  Angle = 360
  AttacherType = Attacher::AttachEngine3D
  Height = 30
  Placement = pos=(-49,106,4) rot=(-1,0,0;0.328122rad)
  Radius = 3
FEATURE [Part::MultiFuse] Fusion140
  Placement = pos=(31,0,0) rot=(0,0,1;0rad)
  Shapes = -> [Cylinder134,Cylinder135]
FEATURE [Part::MultiFuse] Fusion144
  Placement = pos=(369,0,0) rot=(0,0,1;0rad)
  Shapes = -> [Fusion143,Fusion142,Fusion141,Fusion140]
FEATURE [Part::MultiFuse] Fusion145  label="removeForScrewHolesRight004"
  Shapes = -> [Fusion139,Fusion144]
FEATURE [Part::Cut] Cut043
  Base = -> Cut042
  Tool = -> Fusion145
FEATURE [Part::Cylinder] Cylinder136
  Angle = 360
  AttacherType = Attacher::AttachEngine3D
  Height = 10
  Placement = pos=(-49,103,-5) rot=(-1,0,0;0.328122rad)
  Radius = 1.1
FEATURE [Part::Cylinder] Cylinder137
  Angle = 360
  AttacherType = Attacher::AttachEngine3D
  Height = 30
  Placement = pos=(-49,106,4) rot=(-1,0,0;0.328122rad)
  Radius = 3
FEATURE [Part::MultiFuse] Fusion146
  Placement = pos=(15,-68.4,0) rot=(0,0,1;0rad)
  Shapes = -> [Cylinder136,Cylinder137]
FEATURE [Part::Cylinder] Cylinder138
  Angle = 360
  AttacherType = Attacher::AttachEngine3D
  Height = 10
  Placement = pos=(-49,103,-5) rot=(-1,0,0;0.328122rad)
  Radius = 1.1
FEATURE [Part::Cylinder] Cylinder139
  Angle = 360
  AttacherType = Attacher::AttachEngine3D
  Height = 30
  Placement = pos=(-49,106,4) rot=(-1,0,0;0.328122rad)
  Radius = 3
FEATURE [Part::MultiFuse] Fusion147
  Placement = pos=(15,17.6,0) rot=(0,0,1;0rad)
  Shapes = -> [Cylinder138,Cylinder139]
FEATURE [Part::MultiFuse] Fusion148  label="removeToCreateOutterTopScrewHolesRight003"
  Placement = pos=(432.24,0,0) rot=(0,0,1;0rad)
  Shapes = -> [Fusion147,Fusion146]
FEATURE [Part::Cut] Cut044  label="topRightBase"
  Base = -> Cut043
  Tool = -> Fusion148
FEATURE [Part::Cut] Cut045
  Base = -> Cut039
  Tool = -> Cut040
FEATURE [Sketcher::SketchObject] Sketch038  label="rightSideBottom001"
  FullyConstrained = false
  sketch-geometry (91):
    g0: ArcOfCircle CenterX=391.073 CenterY=-83.7794 CenterZ=0 NormalX=0 NormalY=0 NormalZ=1 AngleXU=0 Radius=8 StartAngle=3.14159 EndAngle=6.28319
    g1: Circle CenterX=306.073 CenterY=-81.8102 CenterZ=0 NormalX=0 NormalY=0 NormalZ=1 AngleXU=0 Radius=1
    g2: Circle CenterX=306.073 CenterY=-77.8102 CenterZ=0 NormalX=0 NormalY=0 NormalZ=1 AngleXU=0 Radius=1
    g3: Circle CenterX=302.567 CenterY=-42.9683 CenterZ=0 NormalX=0 NormalY=0 NormalZ=1 AngleXU=0 Radius=1
    g4: Circle CenterX=306.073 CenterY=-44.8935 CenterZ=0 NormalX=0 NormalY=0 NormalZ=1 AngleXU=0 Radius=1
    g5: Circle CenterX=306.073 CenterY=-40.8935 CenterZ=0 NormalX=0 NormalY=0 NormalZ=1 AngleXU=0 Radius=1
    g6: BSplineCurve PolesCount=3 KnotsCount=2 Degree=2 IsPeriodic=0
    g7: GeomPoint X=302.567 Y=-42.9683 Z=0
    g8: GeomPoint X=306.073 Y=-40.8935 Z=0
    g9: Circle CenterX=371.567 CenterY=-80.8644 CenterZ=0 NormalX=0 NormalY=0 NormalZ=1 AngleXU=0 Radius=1
    g10: Circle CenterX=375.073 CenterY=-82.7896 CenterZ=0 NormalX=0 NormalY=0 NormalZ=1 AngleXU=0 Radius=1
    g11: Circle CenterX=375.073 CenterY=-78.7896 CenterZ=0 NormalX=0 NormalY=0 NormalZ=1 AngleXU=0 Radius=1
    g12: GeomPoint X=371.567 Y=-80.8644 Z=0
    g13: GeomPoint X=375.073 Y=-78.7896 Z=0
    g14: Circle CenterX=318.073 CenterY=-51.4823 CenterZ=0 NormalX=0 NormalY=0 NormalZ=1 AngleXU=0 Radius=1
    g15: Circle CenterX=318.073 CenterY=-47.4805 CenterZ=0 NormalX=0 NormalY=0 NormalZ=1 AngleXU=0 Radius=1
    g16: GeomPoint X=321.579 Y=-53.4075 Z=0
    g17: GeomPoint X=318.073 Y=-47.4805 Z=0
    g18: Circle CenterX=321.579 CenterY=-67.3492 CenterZ=0 NormalX=0 NormalY=0 NormalZ=1 AngleXU=0 Radius=1
    g19: Circle CenterX=318.073 CenterY=-65.424 CenterZ=0 NormalX=0 NormalY=0 NormalZ=1 AngleXU=0 Radius=1
    g20: Circle CenterX=318.073 CenterY=-69.424 CenterZ=0 NormalX=0 NormalY=0 NormalZ=1 AngleXU=0 Radius=1
    g21: GeomPoint X=321.579 Y=-67.3492 Z=0
    g22: GeomPoint X=318.073 Y=-69.424 Z=0
    g23: Circle CenterX=362.567 CenterY=-89.8542 CenterZ=0 NormalX=0 NormalY=0 NormalZ=1 AngleXU=0 Radius=1
    g24: Circle CenterX=366.073 CenterY=-91.7794 CenterZ=0 NormalX=0 NormalY=0 NormalZ=1 AngleXU=0 Radius=1
    g25: Circle CenterX=362.073 CenterY=-91.7794 CenterZ=0 NormalX=0 NormalY=0 NormalZ=1 AngleXU=0 Radius=1
    g26: GeomPoint X=362.567 Y=-89.8542 Z=0
    g27: GeomPoint X=362.073 Y=-91.7794 Z=0
    g28: Circle CenterX=322.073 CenterY=-91.7794 CenterZ=0 NormalX=0 NormalY=0 NormalZ=1 AngleXU=0 Radius=1
    g29: Circle CenterX=318.073 CenterY=-91.7794 CenterZ=0 NormalX=0 NormalY=0 NormalZ=1 AngleXU=0 Radius=1
    g30: Circle CenterX=318.073 CenterY=-87.7794 CenterZ=0 NormalX=0 NormalY=0 NormalZ=1 AngleXU=0 Radius=1
    g31: GeomPoint X=322.073 Y=-91.7794 Z=0
    g32: GeomPoint X=318.073 Y=-87.7794 Z=0
    g33: ArcOfCircle CenterX=391.073 CenterY=22.1087 CenterZ=0 NormalX=0 NormalY=0 NormalZ=1 AngleXU=0 Radius=4 StartAngle=0 EndAngle=3.14159
    g34: LineSegment StartX=387.073 StartY=22.1087 StartZ=0 EndX=383.073 EndY=-83.7794 EndZ=0
    g35: LineSegment StartX=395.073 StartY=22.1087 StartZ=0 EndX=399.073 EndY=-83.7794 EndZ=0
    g36: LineSegment StartX=232.072 StartY=-103.779 StartZ=0 EndX=232.072 EndY=-100.779 EndZ=0
    g37: GeomPoint X=232.072 Y=-94.7794 Z=0
    g38: GeomPoint X=223.072 Y=-97.7794 Z=0
    g39: Circle CenterX=232.072 CenterY=-94.7794 CenterZ=0 NormalX=0 NormalY=0 NormalZ=1 AngleXU=0 Radius=1
    g40: Circle CenterX=232.072 CenterY=-100.779 CenterZ=0 NormalX=0 NormalY=0 NormalZ=1 AngleXU=0 Radius=1
    g41: BSplineCurve PolesCount=5 KnotsCount=3 Degree=3 IsPeriodic=0
    g42: GeomPoint X=232.072 Y=-100.779 Z=0
    g43: LineSegment StartX=232.072 StartY=-94.7794 StartZ=0 EndX=232.072 EndY=-91.7794 EndZ=0
    g44: LineSegment StartX=245.072 StartY=-31.3037 StartZ=0 EndX=243.535 EndY=-33.1602 EndZ=0
    g45: LineSegment StartX=241.775 StartY=-35.2862 StartZ=0 EndX=240.266 EndY=-37.1092 EndZ=0
    g46: LineSegment StartX=243.535 StartY=-33.1602 StartZ=0 EndX=248.619 EndY=-37.3688 EndZ=0
    g47: LineSegment StartX=241.775 StartY=-35.2862 StartZ=0 EndX=246.859 EndY=-39.4949 EndZ=0
    g48: LineSegment StartX=248.619 StartY=-37.3688 StartZ=0 EndX=246.859 EndY=-39.4949 EndZ=0
    g49: LineSegment StartX=232.072 StartY=-103.779 StartZ=0 EndX=407.073 EndY=-103.779 EndZ=0
    g50: LineSegment StartX=299.888 StartY=-86.6413 StartZ=0 EndX=240.266 EndY=-37.1092 EndZ=0
    g51: LineSegment StartX=245.072 StartY=-11.4025 StartZ=0 EndX=302.567 EndY=-42.9683 EndZ=0
    g52: BSplineCurve PolesCount=3 KnotsCount=2 Degree=2 IsPeriodic=0
    g53: BSplineCurve PolesCount=3 KnotsCount=2 Degree=2 IsPeriodic=0
    g54: LineSegment StartX=321.579 StartY=-53.4075 StartZ=0 EndX=371.567 EndY=-80.8644 EndZ=0
    g55: BSplineCurve PolesCount=3 KnotsCount=2 Degree=2 IsPeriodic=0
    g56: BSplineCurve PolesCount=3 KnotsCount=2 Degree=2 IsPeriodic=0
    g57: BSplineCurve PolesCount=3 KnotsCount=2 Degree=2 IsPeriodic=0
    g58: LineSegment StartX=318.073 StartY=-69.424 StartZ=0 EndX=318.073 EndY=-87.7794 EndZ=0
    g59: LineSegment StartX=321.579 StartY=-67.3492 StartZ=0 EndX=362.567 EndY=-89.8542 EndZ=0
    g60: LineSegment StartX=362.073 StartY=-91.7794 StartZ=0 EndX=322.073 EndY=-91.7794 EndZ=0
    g61: BSplineCurve PolesCount=3 KnotsCount=2 Degree=2 IsPeriodic=0
    g62: BSplineCurve PolesCount=3 KnotsCount=2 Degree=2 IsPeriodic=0
    g63: LineSegment StartX=245.072 StartY=-31.3037 StartZ=0 EndX=302.996 EndY=-79.2541 EndZ=0
    g64: LineSegment StartX=302.567 StartY=-56.9099 StartZ=0 EndX=239.193 EndY=-22.1109 EndZ=0
    g65: LineSegment StartX=306.073 StartY=-62.8351 StartZ=0 EndX=306.073 EndY=-77.8102 EndZ=0
    g66: BSplineCurve PolesCount=3 KnotsCount=2 Degree=2 IsPeriodic=0
    g67: LineSegment StartX=298.776 StartY=-91.7794 StartZ=0 EndX=232.072 EndY=-91.7794 EndZ=0
    g68: LineSegment StartX=245.072 StartY=-11.4025 StartZ=0 EndX=243.628 EndY=-14.0323 EndZ=0
    g69: LineSegment StartX=240.741 StartY=-19.2917 StartZ=0 EndX=239.193 EndY=-22.1109 EndZ=0
    g70: LineSegment StartX=243.628 StartY=-14.0323 StartZ=0 EndX=246.258 EndY=-15.476 EndZ=0
    g71: LineSegment StartX=240.741 StartY=-19.2917 StartZ=0 EndX=243.37 EndY=-20.7355 EndZ=0
    g72: ArcOfCircle CenterX=247.444 CenterY=-19.5495 CenterZ=0 NormalX=0 NormalY=0 NormalZ=1 AngleXU=0 Radius=4.24264 StartAngle=3.4249 EndAngle=8.13729
    g73: LineSegment StartX=407.073 StartY=-103.779 StartZ=0 EndX=407.073 EndY=48.2206 EndZ=0
    g74: LineSegment StartX=375.073 StartY=48.2206 StartZ=0 EndX=375.073 EndY=-78.7896 EndZ=0
    g75: LineSegment StartX=375.073 StartY=48.2206 StartZ=0 EndX=382.073 EndY=48.2206 EndZ=0
    g76: LineSegment StartX=407.073 StartY=48.2206 StartZ=0 EndX=400.073 EndY=48.2206 EndZ=0
    g77: LineSegment StartX=394.073 StartY=48.2206 StartZ=0 EndX=394.073 EndY=52.2206 EndZ=0
    g78: LineSegment StartX=388.073 StartY=48.2206 StartZ=0 EndX=388.073 EndY=58.2206 EndZ=0
    g79: ArcOfCircle CenterX=385.073 CenterY=61.2206 CenterZ=0 NormalX=0 NormalY=0 NormalZ=1 AngleXU=0 Radius=4.24264 StartAngle=5.49779 EndAngle=10.2102
    g80: ArcOfCircle CenterX=397.073 CenterY=55.2206 CenterZ=0 NormalX=0 NormalY=0 NormalZ=1 AngleXU=0 Radius=4.24264 StartAngle=5.49779 EndAngle=10.2102
    g81: LineSegment StartX=382.073 StartY=58.2206 StartZ=0 EndX=382.073 EndY=48.2206 EndZ=0
    g82: LineSegment StartX=400.073 StartY=52.2206 StartZ=0 EndX=400.073 EndY=48.2206 EndZ=0
    g83: LineSegment StartX=394.073 StartY=48.2206 StartZ=0 EndX=388.073 EndY=48.2206 EndZ=0
    g84: LineSegment StartX=306.073 StartY=-40.8935 StartZ=0 EndX=306.073 EndY=-27.5935 EndZ=0
    g85: LineSegment StartX=318.073 StartY=-27.5935 StartZ=0 EndX=318.073 EndY=-47.4805 EndZ=0
    g86: LineSegment StartX=306.073 StartY=-27.5935 StartZ=0 EndX=310.073 EndY=-27.5935 EndZ=0
    g87: LineSegment StartX=318.073 StartY=-27.5935 StartZ=0 EndX=314.073 EndY=-27.5935 EndZ=0
    g88: LineSegment StartX=310.073 StartY=-27.5935 StartZ=0 EndX=310.073 EndY=-31.5935 EndZ=0
    g89: LineSegment StartX=314.073 StartY=-27.5935 StartZ=0 EndX=314.073 EndY=-31.5935 EndZ=0
    g90: ArcOfCircle CenterX=312.073 CenterY=-33.5935 CenterZ=0 NormalX=0 NormalY=0 NormalZ=1 AngleXU=0 Radius=2.82843 StartAngle=2.35619 EndAngle=7.06858
  constraints (121):
    c: Distance(g44) = 2.41
    c: Block(g44)
    c: Coincident(g46,g44)
    c: Coincident(g49,g36)
    c: Horizontal(g49)
    c: Block(g49)
    c: Coincident(g50,g45)
    c: Block(g50)
    c: Coincident(g51,g6)
    c: Block(g51)
    c: Coincident(g54,g52)
    c: Coincident(g54,g53)
    c: Coincident(g58,g56)
    c: Coincident(g58,g57)
    c: Vertical(g58)
    c: Coincident(g59,g56)
    c: Coincident(g59,g55)
    c: Coincident(g60,g55)
    c: Coincident(g60,g57)
    c: Horizontal(g60)
    c: Block(g61)
    c: Block(g62)
    c: Coincident(g63,g44)
    c: Coincident(g63,g62)
    c: Coincident(g64,g61)
    c: Coincident(g65,g61)
    c: Coincident(g65,g62)
    c: Vertical(g65)
    c: Block(g66)
    c: Coincident(g66,g50)
    c: Coincident(g67,g66)
    c: Coincident(g67,g43)
    c: Horizontal(g67)
    c: Coincident(g68,g51)
    c: Perpendicular(g68,g51)
    c: Coincident(g69,g64)
    c: Coincident(g70,g68)
    c: Distance(g70) = 3
    c: Distance(g71) = 3
    c: Perpendicular(g68,g70)
    c: Coincident(g72,g70)
    c: Coincident(g72,g71)
    c: Block(g72)
    c: Block(g69)
    c: Block(g71)
    c: Block(g54)
    c: Block(g59)
    c: Block(g58)
    c: Block(g60)
    c: Block(g67)
    c: Block(g43)
    c: Block(g36)
    c: Block(g48)
    c: Block(g46)
    c: Block(g47)
    c: Block(g45)
    c: Block(g35)
    c: Block(g34)
    c: Block(g0)
    c: Block(g33)
    c: Block(g52)
    c: Block(g6)
    c: Block(g41)
    c: Block(g57)
    c: Block(g55)
    c: Block(g53)
    c: Block(g68)
    c: Distance(g48) = 2.76
    c: Distance(g47) = 6.6
    c: Distance(g45) = 2.36657
    c: Coincident(g73,g49)
    c: Vertical(g73)
    c: Distance(g73) = 152
    c: Coincident(g74,g53)
    c: Vertical(g74)
    c: Block(g74)
    c: Coincident(g75,g74)
    c: Horizontal(g75)
    c: Distance(g75) = 7
    c: Horizontal(g76)
    c: Distance(g76) = 7
    c: Coincident(g76,g73)
    c: Vertical(g77)
    c: Distance(g77) = 4
    c: Vertical(g78)
    c: Distance(g78) = 10
    c: Coincident(g79,g78)
    c: Coincident(g80,g77)
    c: Block(g80)
    c: Block(g79)
    c: Coincident(g81,g79)
    c: Coincident(g81,g75)
    c: Vertical(g81)
    c: Coincident(g82,g80)
    c: Coincident(g82,g76)
    c: Vertical(g82)
    c: Coincident(g83,g77)
    c: Coincident(g83,g78)
    c: Horizontal(g83)
    c: Coincident(g84,g6)
    c: Vertical(g84)
    c: Distance(g84) = 13.3
    c: Coincident(g85,g52)
    c: Vertical(g85)
    c: Block(g85)
    c: Coincident(g86,g84)
    c: Horizontal(g86)
    c: Distance(g86) = 4
    c: Coincident(g87,g85)
    c: Horizontal(g87)
    c: Distance(g87) = 4
    c: Coincident(g88,g86)
    c: Vertical(g88)
    c: Coincident(g89,g87)
    c: Vertical(g89)
    c: Distance(g88) = 4
    c: Distance(g89) = 4
    c: Coincident(g90,g88)
    c: Coincident(g90,g89)
    c: Block(g90)
    c: Block(g56)
FEATURE [Sketcher::SketchObject] Sketch039
  FullyConstrained = true
  Placement = pos=(0,0,0) rot=(0.57735,0.57735,0.57735;2.0944rad)
  sketch-geometry (18):
    g0: LineSegment StartX=-152.23 StartY=29.0049 StartZ=0 EndX=-143.23 EndY=29.0049 EndZ=0
    g1: LineSegment StartX=-152.23 StartY=29.0049 StartZ=0 EndX=-152.23 EndY=51.0049 EndZ=0
    g2: LineSegment StartX=-152.23 StartY=51.0049 StartZ=0 EndX=-130.23 EndY=51.0049 EndZ=0
    g3: LineSegment StartX=-130.23 StartY=51.0049 StartZ=0 EndX=-130.23 EndY=46.0049 EndZ=0
    g4: LineSegment StartX=-130.23 StartY=46.0049 StartZ=0 EndX=-143.23 EndY=46.0049 EndZ=0
    g5: Circle CenterX=-145.23 CenterY=31.0049 CenterZ=0 NormalX=0 NormalY=0 NormalZ=1 AngleXU=0 Radius=1
    g6: Circle CenterX=-145.23 CenterY=29.0049 CenterZ=0 NormalX=0 NormalY=0 NormalZ=1 AngleXU=0 Radius=1
    g7: Circle CenterX=-143.23 CenterY=29.0049 CenterZ=0 NormalX=0 NormalY=0 NormalZ=1 AngleXU=0 Radius=1
    g8: BSplineCurve PolesCount=3 KnotsCount=2 Degree=2 IsPeriodic=0
    g9: GeomPoint X=-145.23 Y=31.0049 Z=0
    g10: GeomPoint X=-143.23 Y=29.0049 Z=0
    g11: Circle CenterX=-145.23 CenterY=44.0049 CenterZ=0 NormalX=0 NormalY=0 NormalZ=1 AngleXU=0 Radius=1
    g12: Circle CenterX=-145.23 CenterY=46.0049 CenterZ=0 NormalX=0 NormalY=0 NormalZ=1 AngleXU=0 Radius=1
    g13: Circle CenterX=-143.23 CenterY=46.0049 CenterZ=0 NormalX=0 NormalY=0 NormalZ=1 AngleXU=0 Radius=1
    g14: BSplineCurve PolesCount=3 KnotsCount=2 Degree=2 IsPeriodic=0
    g15: GeomPoint X=-145.23 Y=44.0049 Z=0
    g16: GeomPoint X=-143.23 Y=46.0049 Z=0
    g17: LineSegment StartX=-145.23 StartY=44.0049 StartZ=0 EndX=-145.23 EndY=31.0049 EndZ=0
  constraints (40):
    c: Horizontal(g0)
    c: Distance(g0) = 9
    c: Coincident(g1,g0)
    c: Vertical(g1)
    c: Distance(g1) = 22
    c: Coincident(g2,g1)
    c: Horizontal(g2)
    c: Coincident(g3,g2)
    c: Vertical(g3)
    c: Distance(g3) = 5
    c: Coincident(g4,g3)
    c: Horizontal(g4)
    c: Distance(g4) = 13
    c: PointOnObject(g6,g0)
    c: Weight(g5) = 1
    c: Equal(g5,g6)
    c: Equal(g5,g7)
    c: Coincident(g8,g0)
    c: InternalAlignment(g5,g8)
    c: InternalAlignment(g6,g8)
    c: InternalAlignment(g7,g8)
    c: InternalAlignment(g9,g8)
    c: InternalAlignment(g10,g8)
    c: Weight(g11) = 1
    c: Equal(g11,g12)
    c: Equal(g11,g13)
    c: Coincident(g14,g4)
    c: InternalAlignment(g11,g14)
    c: InternalAlignment(g12,g14)
    c: InternalAlignment(g13,g14)
    c: InternalAlignment(g15,g14)
    c: InternalAlignment(g16,g14)
    c: Coincident(g17,g14)
    c: Coincident(g17,g8)
    c: Vertical(g17)
    c: Block(g4)
    c: Block(g17)
    c: Block(g14)
    c: Block(g8)
    c: Distance(g2) = 22
FEATURE [Sketcher::SketchObject] Sketch040
  FullyConstrained = true
  Placement = pos=(0,0,0) rot=(0.57735,0.57735,0.57735;2.0944rad)
  sketch-geometry (18):
    g0: LineSegment StartX=-152.23 StartY=29.0049 StartZ=0 EndX=-143.23 EndY=29.0049 EndZ=0
    g1: LineSegment StartX=-152.23 StartY=29.0049 StartZ=0 EndX=-152.23 EndY=51.0049 EndZ=0
    g2: LineSegment StartX=-152.23 StartY=51.0049 StartZ=0 EndX=-130.23 EndY=51.0049 EndZ=0
    g3: LineSegment StartX=-130.23 StartY=51.0049 StartZ=0 EndX=-130.23 EndY=46.0049 EndZ=0
    g4: LineSegment StartX=-130.23 StartY=46.0049 StartZ=0 EndX=-143.23 EndY=46.0049 EndZ=0
    g5: Circle CenterX=-145.23 CenterY=31.0049 CenterZ=0 NormalX=0 NormalY=0 NormalZ=1 AngleXU=0 Radius=1
    g6: Circle CenterX=-145.23 CenterY=29.0049 CenterZ=0 NormalX=0 NormalY=0 NormalZ=1 AngleXU=0 Radius=1
    g7: Circle CenterX=-143.23 CenterY=29.0049 CenterZ=0 NormalX=0 NormalY=0 NormalZ=1 AngleXU=0 Radius=1
    g8: BSplineCurve PolesCount=3 KnotsCount=2 Degree=2 IsPeriodic=0
    g9: GeomPoint X=-145.23 Y=31.0049 Z=0
    g10: GeomPoint X=-143.23 Y=29.0049 Z=0
    g11: Circle CenterX=-145.23 CenterY=44.0049 CenterZ=0 NormalX=0 NormalY=0 NormalZ=1 AngleXU=0 Radius=1
    g12: Circle CenterX=-145.23 CenterY=46.0049 CenterZ=0 NormalX=0 NormalY=0 NormalZ=1 AngleXU=0 Radius=1
    g13: Circle CenterX=-143.23 CenterY=46.0049 CenterZ=0 NormalX=0 NormalY=0 NormalZ=1 AngleXU=0 Radius=1
    g14: BSplineCurve PolesCount=3 KnotsCount=2 Degree=2 IsPeriodic=0
    g15: GeomPoint X=-145.23 Y=44.0049 Z=0
    g16: GeomPoint X=-143.23 Y=46.0049 Z=0
    g17: LineSegment StartX=-145.23 StartY=44.0049 StartZ=0 EndX=-145.23 EndY=31.0049 EndZ=0
  constraints (40):
    c: Horizontal(g0)
    c: Distance(g0) = 9
    c: Coincident(g1,g0)
    c: Vertical(g1)
    c: Distance(g1) = 22
    c: Coincident(g2,g1)
    c: Horizontal(g2)
    c: Coincident(g3,g2)
    c: Vertical(g3)
    c: Distance(g3) = 5
    c: Coincident(g4,g3)
    c: Horizontal(g4)
    c: Distance(g4) = 13
    c: PointOnObject(g6,g0)
    c: Weight(g5) = 1
    c: Equal(g5,g6)
    c: Equal(g5,g7)
    c: Coincident(g8,g0)
    c: InternalAlignment(g5,g8)
    c: InternalAlignment(g6,g8)
    c: InternalAlignment(g7,g8)
    c: InternalAlignment(g9,g8)
    c: InternalAlignment(g10,g8)
    c: Weight(g11) = 1
    c: Equal(g11,g12)
    c: Equal(g11,g13)
    c: Coincident(g14,g4)
    c: InternalAlignment(g11,g14)
    c: InternalAlignment(g12,g14)
    c: InternalAlignment(g13,g14)
    c: InternalAlignment(g15,g14)
    c: InternalAlignment(g16,g14)
    c: Coincident(g17,g14)
    c: Coincident(g17,g8)
    c: Vertical(g17)
    c: Block(g4)
    c: Block(g17)
    c: Block(g14)
    c: Block(g8)
    c: Distance(g2) = 22
FEATURE [Part::Extrusion] Extrude039
  Base = -> Sketch038
  Dir = (0,0,1)
  DirMode = 2
  FaceMakerClass = Part::FaceMakerBullseye
  LengthFwd = 28
  LengthRev = 0
  Solid = true
  Symmetric = false
FEATURE [Part::Box] Box060  label="removeFromtTop011"
  AttacherType = Attacher::AttachEngine3D
  Height = 56
  Length = 470
  Placement = pos=(-47.93,-106.78,8) rot=(1,0,0;0.080285rad)
  Width = 260
FEATURE [Part::Box] Box061  label="removeFromBottomOfTop003"
  AttacherType = Attacher::AttachEngine3D
  Height = 10
  Length = 475
  Placement = pos=(-51,-113,-1) rot=(1,0,0;0.080285rad)
  Width = 10
FEATURE [Part::Cut] Cut046
  Base = -> Extrude039
  Tool = -> Box060
FEATURE [Part::Cut] Cut047
  Base = -> Cut046
  Tool = -> Box061
FEATURE [Part::Extrusion] Extrude040  label="laptopRetainer028"
  Base = -> Sketch039
  Dir = (1,0,0)
  DirMode = 2
  FaceMakerClass = Part::FaceMakerBullseye
  LengthFwd = 150
  LengthRev = 0
  Placement = pos=(107.08,50.35,-8.45) rot=(1,0,0;0.080285rad)
  Solid = true
  Symmetric = false
FEATURE [Part::Extrusion] Extrude041  label="laptopRetainer029"
  Base = -> Sketch040
  Dir = (1,0,0)
  DirMode = 2
  FaceMakerClass = Part::FaceMakerBullseye
  LengthFwd = 150
  LengthRev = 0
  Placement = pos=(257.08,50.35,-8.45) rot=(1,0,0;0.080285rad)
  Solid = true
  Symmetric = false
FEATURE [Part::Box] Box062  label="Cube046"
  AttacherType = Attacher::AttachEngine3D
  Height = 10
  Length = 40
  Placement = pos=(162.7,-101,0) rot=(0,0,1;0rad)
  Width = 4
FEATURE [Part::Fuse] Fusion149  label="laptopRetainer027"
  Base = -> Extrude040
  Tool = -> Box062
FEATURE [Part::Box] Box063  label="Cube047"
  AttacherType = Attacher::AttachEngine3D
  Height = 10
  Length = 40
  Placement = pos=(312.07,-101,0) rot=(0,0,1;0rad)
  Width = 4
FEATURE [Part::Box] Box064  label="Cube048"
  AttacherType = Attacher::AttachEngine3D
  Height = 10
  Length = 10
  Placement = pos=(101,-102.5,12) rot=(1,0,0;0.080285rad)
  Width = 4
FEATURE [Part::MultiFuse] Fusion150  label="laptopRetainer030"
  Shapes = -> [Extrude041,Box063]
FEATURE [Part::Box] Box065  label="Cube049"
  AttacherType = Attacher::AttachEngine3D
  Height = 10
  Length = 10
  Placement = pos=(253,-102.5,12) rot=(1,0,0;0.080285rad)
  Width = 4
FEATURE [Part::MultiFuse] Fusion151  label="laptopRetainer031"
  Shapes = -> [Box065,Fusion149,Box064]
FEATURE [Part::Cut] Cut048  label="laptopRetainer032"
  Base = -> Fusion150
  Tool = -> Fusion151
FEATURE [Part::Cut] Cut049
  Base = -> Cut047
  Tool = -> Cut048
FEATURE [Part::Cylinder] Cylinder140
  Angle = 360
  AttacherType = Attacher::AttachEngine3D
  Height = 10
  Placement = pos=(-49,103,-5) rot=(-1,0,0;0.328122rad)
  Radius = 1.1
FEATURE [Part::Cylinder] Cylinder141
  Angle = 360
  AttacherType = Attacher::AttachEngine3D
  Height = 30
  Placement = pos=(-49,106,4) rot=(-1,0,0;0.328122rad)
  Radius = 3
FEATURE [Part::MultiFuse] Fusion152
  Placement = pos=(15,-68.4,0) rot=(0,0,1;0rad)
  Shapes = -> [Cylinder140,Cylinder141]
FEATURE [Part::Cylinder] Cylinder142
  Angle = 360
  AttacherType = Attacher::AttachEngine3D
  Height = 10
  Placement = pos=(-49,103,-5) rot=(-1,0,0;0.328122rad)
  Radius = 1.1
FEATURE [Part::Cylinder] Cylinder143
  Angle = 360
  AttacherType = Attacher::AttachEngine3D
  Height = 30
  Placement = pos=(-49,106,4) rot=(-1,0,0;0.328122rad)
  Radius = 3
FEATURE [Part::MultiFuse] Fusion153
  Placement = pos=(15,17.6,0) rot=(0,0,1;0rad)
  Shapes = -> [Cylinder142,Cylinder143]
FEATURE [Part::MultiFuse] Fusion154  label="removeToCreateOutterTopScrewHolesRight004"
  Placement = pos=(432.24,0,0) rot=(0,0,1;0rad)
  Shapes = -> [Fusion153,Fusion152]
FEATURE [Part::Cut] Cut050  label="bottomRightBase"
  Base = -> Cut049
  Tool = -> Fusion154
FEATURE [Part::Cut] Cut051
  Base = -> Cut045
  Tool = -> Cut041
FEATURE [Sketcher::SketchObject] Sketch041  label="leftSideTop003"
  FullyConstrained = true
  sketch-geometry (89):
    g0: Circle CenterX=61.1495 CenterY=111.695 CenterZ=0 NormalX=0 NormalY=0 NormalZ=1 AngleXU=0 Radius=1
    g1: Circle CenterX=58.0728 CenterY=114.251 CenterZ=0 NormalX=0 NormalY=0 NormalZ=1 AngleXU=0 Radius=1
    g2: Circle CenterX=58.0728 CenterY=110.251 CenterZ=0 NormalX=0 NormalY=0 NormalZ=1 AngleXU=0 Radius=1
    g3: BSplineCurve PolesCount=3 KnotsCount=2 Degree=2 IsPeriodic=0
    g4: GeomPoint X=61.1495 Y=111.695 Z=0
    g5: GeomPoint X=58.0728 Y=110.251 Z=0
    g6: Circle CenterX=61.5791 CenterY=89.3511 CenterZ=0 NormalX=0 NormalY=0 NormalZ=1 AngleXU=0 Radius=1
    g7: Circle CenterX=58.0728 CenterY=91.2763 CenterZ=0 NormalX=0 NormalY=0 NormalZ=1 AngleXU=0 Radius=1
    g8: Circle CenterX=58.0728 CenterY=95.2763 CenterZ=0 NormalX=0 NormalY=0 NormalZ=1 AngleXU=0 Radius=1
    g9: BSplineCurve PolesCount=3 KnotsCount=2 Degree=2 IsPeriodic=0
    g10: GeomPoint X=61.5791 Y=89.3511 Z=0
    g11: GeomPoint X=58.0728 Y=95.2763 Z=0
    g12: Circle CenterX=62.0728 CenterY=124.221 CenterZ=0 NormalX=0 NormalY=0 NormalZ=1 AngleXU=0 Radius=1
    g13: Circle CenterX=58.0728 CenterY=124.221 CenterZ=0 NormalX=0 NormalY=0 NormalZ=1 AngleXU=0 Radius=1
    g14: Circle CenterX=61.1496 CenterY=121.665 CenterZ=0 NormalX=0 NormalY=0 NormalZ=1 AngleXU=0 Radius=1
    g15: BSplineCurve PolesCount=3 KnotsCount=2 Degree=2 IsPeriodic=0
    g16: GeomPoint X=62.0728 Y=124.221 Z=0
    g17: GeomPoint X=61.1496 Y=121.665 Z=0
    g18: Circle CenterX=61.5791 CenterY=75.4095 CenterZ=0 NormalX=0 NormalY=0 NormalZ=1 AngleXU=0 Radius=1
    g19: Circle CenterX=58.0728 CenterY=77.3346 CenterZ=0 NormalX=0 NormalY=0 NormalZ=1 AngleXU=0 Radius=1
    g20: Circle CenterX=58.0728 CenterY=73.3346 CenterZ=0 NormalX=0 NormalY=0 NormalZ=1 AngleXU=0 Radius=1
    g21: BSplineCurve PolesCount=3 KnotsCount=2 Degree=2 IsPeriodic=0
    g22: GeomPoint X=61.5791 Y=75.4095 Z=0
    g23: GeomPoint X=58.0728 Y=73.3346 Z=0
    g24: Circle CenterX=2.07281 CenterY=124.221 CenterZ=0 NormalX=0 NormalY=0 NormalZ=1 AngleXU=0 Radius=1
    g25: Circle CenterX=1.57905 CenterY=122.295 CenterZ=0 NormalX=0 NormalY=0 NormalZ=1 AngleXU=0 Radius=1
    g26: BSplineCurve PolesCount=3 KnotsCount=2 Degree=2 IsPeriodic=0
    g27: GeomPoint X=2.07281 Y=124.221 Z=0
    g28: GeomPoint X=1.57905 Y=122.295 Z=0
    g29: Circle CenterX=46.0728 CenterY=124.221 CenterZ=0 NormalX=0 NormalY=0 NormalZ=1 AngleXU=0 Radius=1
    g30: Circle CenterX=46.0728 CenterY=120.221 CenterZ=0 NormalX=0 NormalY=0 NormalZ=1 AngleXU=0 Radius=1
    g31: BSplineCurve PolesCount=3 KnotsCount=2 Degree=2 IsPeriodic=0
    g32: GeomPoint X=42.0728 Y=124.221 Z=0
    g33: GeomPoint X=46.0728 Y=120.221 Z=0
    g34-g38: Circle x5 (B-spline internal-alignment scaffolding for g39; pole/knot coordinates omitted)
    g39: BSplineCurve PolesCount=5 KnotsCount=3 Degree=3 IsPeriodic=0
    g40: GeomPoint X=132.072 Y=133.221 Z=0
    g41: GeomPoint X=141.072 Y=130.221 Z=0
    g42: GeomPoint X=132.072 Y=127.221 Z=0
    g43: ArcOfCircle CenterX=116.562 CenterY=52.0649 CenterZ=0 NormalX=0 NormalY=0 NormalZ=1 AngleXU=0 Radius=4.24264 StartAngle=0.283268 EndAngle=4.99566
    g44: LineSegment StartX=123.967 StartY=69.4706 StartZ=0 EndX=122.37 EndY=67.5474 EndZ=0
    g45: LineSegment StartX=117.293 StartY=71.7641 StartZ=0 EndX=115.591 EndY=69.7147 EndZ=0
    g46: LineSegment StartX=120.669 StartY=65.4973 StartZ=0 EndX=119.072 EndY=63.5741 EndZ=0
    g47: LineSegment StartX=124.73 StartY=54.6766 StartZ=0 EndX=123.265 EndY=51.8068 EndZ=0
    g48: LineSegment StartX=120.377 StartY=46.5474 StartZ=0 EndX=118.934 EndY=43.9178 EndZ=0
    g49: LineSegment StartX=61.5791 StartY=75.4095 StartZ=0 EndX=118.934 EndY=43.9178 EndZ=0
    g50: LineSegment StartX=117.748 StartY=47.9913 StartZ=0 EndX=120.377 EndY=46.5474 EndZ=0
    g51: LineSegment StartX=120.635 StartY=53.2507 StartZ=0 EndX=123.265 EndY=51.8068 EndZ=0
    g52: LineSegment StartX=124.73 StartY=54.6766 StartZ=0 EndX=61.5791 EndY=89.3511 EndZ=0
    g53: LineSegment StartX=58.0728 StartY=95.2763 StartZ=0 EndX=58.0728 EndY=110.251 EndZ=0
    g54: LineSegment StartX=61.1495 StartY=111.695 StartZ=0 EndX=119.072 EndY=63.5741 EndZ=0
    g55: LineSegment StartX=120.669 StartY=65.4973 StartZ=0 EndX=115.591 EndY=69.7147 EndZ=0
    g56: LineSegment StartX=117.293 StartY=71.7641 StartZ=0 EndX=122.37 EndY=67.5474 EndZ=0
    g57: LineSegment StartX=123.967 StartY=69.4706 StartZ=0 EndX=61.1496 EndY=121.665 EndZ=0
    g58: LineSegment StartX=62.0728 StartY=124.221 StartZ=0 EndX=132.072 EndY=124.221 EndZ=0
    g59: LineSegment StartX=132.072 StartY=127.221 StartZ=0 EndX=132.072 EndY=124.221 EndZ=0
    g60: LineSegment StartX=132.072 StartY=133.221 StartZ=0 EndX=132.072 EndY=136.221 EndZ=0
    g61: LineSegment StartX=132.072 StartY=136.221 StartZ=0 EndX=-42.9272 EndY=136.221 EndZ=0
    g62: LineSegment StartX=2.07281 StartY=124.221 StartZ=0 EndX=42.0728 EndY=124.221 EndZ=0
    g63: LineSegment StartX=-17.9272 StartY=48.2206 StartZ=0 EndX=-17.9272 EndY=58.2206 EndZ=0
    g64: LineSegment StartX=-35.9272 StartY=48.2206 StartZ=0 EndX=-35.9272 EndY=52.2206 EndZ=0
    g65: LineSegment StartX=-29.9272 StartY=48.2206 StartZ=0 EndX=-29.9272 EndY=52.2206 EndZ=0
    g66: LineSegment StartX=-23.9272 StartY=48.2206 StartZ=0 EndX=-23.9272 EndY=58.2206 EndZ=0
    g67: ArcOfCircle CenterX=-32.9272 CenterY=55.2206 CenterZ=0 NormalX=0 NormalY=0 NormalZ=1 AngleXU=0 Radius=4.24264 StartAngle=5.49779 EndAngle=10.2102
    g68: ArcOfCircle CenterX=-20.9272 CenterY=61.2206 CenterZ=0 NormalX=0 NormalY=0 NormalZ=1 AngleXU=0 Radius=4.24264 StartAngle=5.49779 EndAngle=10.2102
    g69: LineSegment StartX=-42.9272 StartY=48.2206 StartZ=0 EndX=-42.9272 EndY=136.221 EndZ=0
    g70: LineSegment StartX=58.0728 StartY=-27.5905 StartZ=0 EndX=58.0728 EndY=73.3346 EndZ=0
    g71: LineSegment StartX=50.0728 StartY=-27.5905 StartZ=0 EndX=50.0728 EndY=-31.5905 EndZ=0
    g72: LineSegment StartX=54.0728 StartY=-27.5905 StartZ=0 EndX=54.0728 EndY=-31.5905 EndZ=0
    g73: ArcOfCircle CenterX=52.0728 CenterY=-33.5905 CenterZ=0 NormalX=0 NormalY=0 NormalZ=1 AngleXU=0 Radius=2.82843 StartAngle=2.35619 EndAngle=7.06858
    g74: LineSegment StartX=54.0728 StartY=-27.5905 StartZ=0 EndX=58.0728 EndY=-27.5905 EndZ=0
    g75: LineSegment StartX=-17.9272 StartY=48.2206 StartZ=0 EndX=-10.9272 EndY=48.2206 EndZ=0
    g76: LineSegment StartX=-29.9272 StartY=48.2206 StartZ=0 EndX=-23.9272 EndY=48.2206 EndZ=0
    g77: LineSegment StartX=-42.9272 StartY=48.2206 StartZ=0 EndX=-35.9272 EndY=48.2206 EndZ=0
    g78: BSplineCurve PolesCount=3 KnotsCount=2 Degree=2 IsPeriodic=0
    g79: LineSegment StartX=46.0728 StartY=-27.5905 StartZ=0 EndX=46.0728 EndY=64.4095 EndZ=0
    g80: BSplineCurve PolesCount=3 KnotsCount=2 Degree=2 IsPeriodic=0
    g81: LineSegment StartX=-6.92718 StartY=68.4095 StartZ=0 EndX=42.0728 EndY=68.4095 EndZ=0
    g82: LineSegment StartX=-10.9272 StartY=64.4095 StartZ=0 EndX=-10.9272 EndY=48.2206 EndZ=0
    g83: LineSegment StartX=46.0728 StartY=-27.5905 StartZ=0 EndX=50.0728 EndY=-27.5905 EndZ=0
    g84: LineSegment StartX=46.0728 StartY=120.221 StartZ=0 EndX=46.0728 EndY=113.861 EndZ=0
    g85: BSplineCurve PolesCount=3 KnotsCount=2 Degree=2 IsPeriodic=0
    g86: LineSegment StartX=42.0728 StartY=109.861 StartZ=0 EndX=35.5028 EndY=109.861 EndZ=0
    g87: BSplineCurve PolesCount=3 KnotsCount=2 Degree=2 IsPeriodic=0
    g88: LineSegment StartX=1.57905 StartY=122.295 StartZ=0 EndX=27.9965 EndY=111.786 EndZ=0
  constraints (158):
    c: Weight(g0) = 1
    c: Equal(g0,g1)
    c: Equal(g0,g2)
    c: InternalAlignment(g0,g3)
    c: InternalAlignment(g1,g3)
    c: InternalAlignment(g2,g3)
    c: InternalAlignment(g4,g3)
    c: InternalAlignment(g5,g3)
    c: Weight(g6) = 1
    c: Equal(g6,g7)
    c: Equal(g6,g8)
    c: InternalAlignment(g6,g9)
    c: InternalAlignment(g7,g9)
    c: InternalAlignment(g8,g9)
    c: InternalAlignment(g10,g9)
    c: InternalAlignment(g11,g9)
    c: Block(g3)
    c: Block(g9)
    c: Weight(g12) = 1
    c: Equal(g12,g13)
    c: Equal(g12,g14)
    c: InternalAlignment(g12,g15)
    c: InternalAlignment(g13,g15)
    c: InternalAlignment(g14,g15)
    c: InternalAlignment(g16,g15)
    c: InternalAlignment(g17,g15)
    c: Block(g15)
    c: Weight(g18) = 1
    c: Equal(g18,g19)
    c: Equal(g18,g20)
    c: InternalAlignment(g18,g21)
    c: InternalAlignment(g19,g21)
    c: InternalAlignment(g20,g21)
    c: InternalAlignment(g22,g21)
    c: InternalAlignment(g23,g21)
    c: Block(g21)
    c: Weight(g24) = 1
    c: Equal(g24,g25)
    c: InternalAlignment(g24,g26)
    c: InternalAlignment(g25,g26)
    c: InternalAlignment(g27,g26)
    c: InternalAlignment(g28,g26)
    c: InternalAlignment(g29,g31)
    c: InternalAlignment(g30,g31)
    c: InternalAlignment(g32,g31)
    c: InternalAlignment(g33,g31)
    c: Block(g31)
    c: Block(g26)
    c: Weight(g34) = 1
    c: Equal(g34, g35-g38) x4
    c: InternalAlignment(g34-g38 -> g39) x5
    c: InternalAlignment(g40,g39)
    c: InternalAlignment(g41,g39)
    c: InternalAlignment(g42,g39)
    c: Block(g39)
    c: Block(g43)
    c: Block(g44)
    c: Block(g45)
    c: Block(g46)
    c: Block(g47)
    c: Block(g48)
    c: Coincident(g70,g21)
    c: Coincident(g49,g21)
    c: Coincident(g49,g48)
    c: Coincident(g50,g43)
    c: Coincident(g50,g48)
    c: Coincident(g51,g43)
    c: Coincident(g51,g47)
    c: Coincident(g52,g47)
    c: Coincident(g52,g9)
    c: Coincident(g53,g9)
    c: Coincident(g53,g3)
    c: Vertical(g53)
    c: Coincident(g54,g3)
    c: Coincident(g54,g46)
    c: Coincident(g55,g46)
    c: Coincident(g55,g45)
    c: Coincident(g56,g45)
    c: Coincident(g56,g44)
    c: Coincident(g57,g44)
    c: Coincident(g57,g15)
    c: Coincident(g58,g15)
    c: Horizontal(g58)
    c: Coincident(g59,g39)
    c: Coincident(g59,g58)
    c: Vertical(g59)
    c: Coincident(g60,g39)
    c: Vertical(g60)
    c: Coincident(g61,g60)
    c: Horizontal(g61)
    c: Coincident(g62,g26)
    c: Coincident(g62,g31)
    c: Horizontal(g62)
    c: Vertical(g63)
    c: Distance(g63) = 10
    c: Vertical(g64)
    c: Distance(g64) = 4
    c: Vertical(g65)
    c: Distance(g65) = 4
    c: Vertical(g66)
    c: Distance(g66) = 10
    c: Coincident(g67,g65)
    c: Coincident(g67,g64)
    c: Block(g67)
    c: Coincident(g68,g66)
    c: Coincident(g68,g63)
    c: Block(g68)
    c: Coincident(g69,g61)
    c: Vertical(g69)
    c: Block(g61)
    c: Block(g70)
    c: Vertical(g71)
    c: Distance(g71) = 4
    c: Vertical(g72)
    c: Distance(g72) = 4
    c: Coincident(g73,g71)
    c: Coincident(g73,g72)
    c: Block(g73)
    c: Coincident(g74,g72)
    c: Coincident(g74,g70)
    c: Horizontal(g74)
    c: Distance(g74) = 4
    c: Block(g69)
    c: Coincident(g75,g63)
    c: Horizontal(g75)
    c: Coincident(g76,g65)
    c: Coincident(g76,g66)
    c: Horizontal(g76)
    c: Coincident(g77,g69)
    c: Coincident(g77,g64)
    c: Horizontal(g77)
    c: Block(g78)
    c: Vertical(g79)
    c: Distance(g79) = 92
    c: Block(g80)
    c: Coincident(g80,g79)
    c: Coincident(g81,g78)
    c: Coincident(g81,g80)
    c: Horizontal(g81)
    c: Coincident(g82,g78)
    c: Coincident(g82,g75)
    c: Vertical(g82)
    c: Coincident(g83,g79)
    c: Coincident(g83,g71)
    c: Horizontal(g83)
    c: Coincident(g84,g31)
    c: Vertical(g84)
    c: Distance(g84) = 6.36
    c: Block(g85)
    c: Coincident(g85,g84)
    c: Horizontal(g86)
    c: Coincident(g86,g85)
    c: Block(g87)
    c: Coincident(g87,g86)
    c: Coincident(g88,g26)
    c: Coincident(g88,g87)
    c: Distance(g61) = 174.999
    c: Distance(g61) = 174.999
FEATURE [Part::Extrusion] Extrude042
  Base = -> Sketch041
  Dir = (0,0,1)
  DirMode = 2
  FaceMakerClass = Part::FaceMakerBullseye
  LengthFwd = 28
  LengthRev = 0
  Solid = true
  Symmetric = false
FEATURE [Part::Box] Box066  label="removeFromtTop012"
  AttacherType = Attacher::AttachEngine3D
  Height = 56
  Length = 470
  Placement = pos=(-47.93,-106.78,8) rot=(1,0,0;0.080285rad)
  Width = 260
FEATURE [Part::Cut] Cut052
  Base = -> Extrude042
  Tool = -> Box066
FEATURE [Part::Cylinder] Cylinder144
  Angle = 360
  AttacherType = Attacher::AttachEngine3D
  Height = 10
  Placement = pos=(-49,103,-5) rot=(-1,0,0;0.328122rad)
  Radius = 1.1
FEATURE [Part::Cylinder] Cylinder145
  Angle = 360
  AttacherType = Attacher::AttachEngine3D
  Height = 30
  Placement = pos=(-49,106,4) rot=(-1,0,0;0.328122rad)
  Radius = 3
FEATURE [Part::MultiFuse] Fusion155
  Placement = pos=(15,0,0) rot=(0,0,1;0rad)
  Shapes = -> [Cylinder144,Cylinder145]
FEATURE [Part::Cylinder] Cylinder146
  Angle = 360
  AttacherType = Attacher::AttachEngine3D
  Height = 10
  Placement = pos=(-49,103,-5) rot=(-1,0,0;0.328122rad)
  Radius = 1.1
FEATURE [Part::Cylinder] Cylinder147
  Angle = 360
  AttacherType = Attacher::AttachEngine3D
  Height = 30
  Placement = pos=(-49,106,4) rot=(-1,0,0;0.328122rad)
  Radius = 3
FEATURE [Part::MultiFuse] Fusion157
  Placement = pos=(15,-32,0) rot=(0,0,1;0rad)
  Shapes = -> [Cylinder146,Cylinder147]
FEATURE [Part::MultiFuse] Fusion159
  Shapes = -> [Fusion155,Fusion157]
FEATURE [Part::Cylinder] Cylinder148
  Angle = 360
  AttacherType = Attacher::AttachEngine3D
  Height = 10
  Placement = pos=(-49,103,-5) rot=(-1,0,0;0.328122rad)
  Radius = 1.1
FEATURE [Part::Cylinder] Cylinder149
  Angle = 360
  AttacherType = Attacher::AttachEngine3D
  Height = 30
  Placement = pos=(-49,106,4) rot=(-1,0,0;0.328122rad)
  Radius = 3
FEATURE [Part::MultiFuse] Fusion156
  Placement = pos=(31,0,0) rot=(0,0,1;0rad)
  Shapes = -> [Cylinder148,Cylinder149]
FEATURE [Part::Cylinder] Cylinder150
  Angle = 360
  AttacherType = Attacher::AttachEngine3D
  Height = 10
  Placement = pos=(-49,103,-5) rot=(-1,0,0;0.328122rad)
  Radius = 1.1
FEATURE [Part::Cylinder] Cylinder151
  Angle = 360
  AttacherType = Attacher::AttachEngine3D
  Height = 30
  Placement = pos=(-49,106,4) rot=(-1,0,0;0.328122rad)
  Radius = 3
FEATURE [Part::MultiFuse] Fusion161
  Placement = pos=(31,-29.4,0) rot=(0,0,1;0rad)
  Shapes = -> [Cylinder150,Cylinder151]
FEATURE [Part::Cylinder] Cylinder152
  Angle = 360
  AttacherType = Attacher::AttachEngine3D
  Height = 10
  Placement = pos=(-49,103,-5) rot=(-1,0,0;0.328122rad)
  Radius = 1.1
FEATURE [Part::Cylinder] Cylinder153
  Angle = 360
  AttacherType = Attacher::AttachEngine3D
  Height = 30
  Placement = pos=(-49,106,4) rot=(-1,0,0;0.328122rad)
  Radius = 3
FEATURE [Part::MultiFuse] Fusion160
  Placement = pos=(63,0,0) rot=(0,0,1;0rad)
  Shapes = -> [Cylinder152,Cylinder153]
FEATURE [Part::Cylinder] Cylinder154
  Angle = 360
  AttacherType = Attacher::AttachEngine3D
  Height = 10
  Placement = pos=(-49,103,-5) rot=(-1,0,0;0.328122rad)
  Radius = 1.1
FEATURE [Part::Cylinder] Cylinder155
  Angle = 360
  AttacherType = Attacher::AttachEngine3D
  Height = 30
  Placement = pos=(-49,106,4) rot=(-1,0,0;0.328122rad)
  Radius = 3
FEATURE [Part::MultiFuse] Fusion162
  Placement = pos=(63,-29.4,0) rot=(0,0,1;0rad)
  Shapes = -> [Cylinder154,Cylinder155]
FEATURE [Part::MultiFuse] Fusion163
  Shapes = -> [Fusion162,Fusion161,Fusion160,Fusion156]
FEATURE [Part::MultiFuse] Fusion158  label="removeFromScrewHolesLeft004"
  Shapes = -> [Fusion159,Fusion163]
FEATURE [Part::Cut] Cut054
  Base = -> Cut052
  Tool = -> Fusion158
FEATURE [Part::Cylinder] Cylinder156
  Angle = 360
  AttacherType = Attacher::AttachEngine3D
  Height = 30
  Placement = pos=(-49,106,4) rot=(-1,0,0;0.328122rad)
  Radius = 3
FEATURE [Part::Cylinder] Cylinder157
  Angle = 360
  AttacherType = Attacher::AttachEngine3D
  Height = 10
  Placement = pos=(-49,103,-5) rot=(-1,0,0;0.328122rad)
  Radius = 1.1
FEATURE [Part::Cylinder] Cylinder158
  Angle = 360
  AttacherType = Attacher::AttachEngine3D
  Height = 30
  Placement = pos=(-49,106,4) rot=(-1,0,0;0.328122rad)
  Radius = 3
FEATURE [Part::Cylinder] Cylinder159
  Angle = 360
  AttacherType = Attacher::AttachEngine3D
  Height = 10
  Placement = pos=(-49,103,-5) rot=(-1,0,0;0.328122rad)
  Radius = 1.1
FEATURE [Part::MultiFuse] Fusion164
  Placement = pos=(15,-68.4,0) rot=(0,0,1;0rad)
  Shapes = -> [Cylinder157,Cylinder158]
FEATURE [Part::MultiFuse] Fusion165
  Placement = pos=(15,17.6,0) rot=(0,0,1;0rad)
  Shapes = -> [Cylinder159,Cylinder156]
FEATURE [Part::MultiFuse] Fusion166  label="removeToCreateOutterTopScrewHolesLeft004"
  Shapes = -> [Fusion165,Fusion164]
FEATURE [Part::Cut] Cut053  label="topLeftBase001"
  Base = -> Cut054
  Tool = -> Fusion166
FEATURE [Part::Cut] Cut055
  Base = -> Cut036
  Tool = -> Cut037
FEATURE [Sketcher::SketchObject] Sketch042  label="leftSideBottom001"
  FullyConstrained = true
  sketch-geometry (92):
    g0: ArcOfCircle CenterX=-26.9272 CenterY=-83.7794 CenterZ=0 NormalX=0 NormalY=0 NormalZ=1 AngleXU=0 Radius=8 StartAngle=3.14159 EndAngle=6.28319
    g1: Circle CenterX=61.5791 CenterY=-56.9099 CenterZ=0 NormalX=0 NormalY=0 NormalZ=1 AngleXU=0 Radius=1
    g2: Circle CenterX=58.0728 CenterY=-58.8351 CenterZ=0 NormalX=0 NormalY=0 NormalZ=1 AngleXU=0 Radius=1
    g3: Circle CenterX=58.0728 CenterY=-62.8351 CenterZ=0 NormalX=0 NormalY=0 NormalZ=1 AngleXU=0 Radius=1
    g4: BSplineCurve PolesCount=3 KnotsCount=2 Degree=2 IsPeriodic=0
    g5: GeomPoint X=61.5791 Y=-56.9099 Z=0
    g6: GeomPoint X=58.0728 Y=-62.8351 Z=0
    g7: Circle CenterX=58.0728 CenterY=-77.8102 CenterZ=0 NormalX=0 NormalY=0 NormalZ=1 AngleXU=0 Radius=1
    g8: Circle CenterX=58.0728 CenterY=-81.8102 CenterZ=0 NormalX=0 NormalY=0 NormalZ=1 AngleXU=0 Radius=1
    g9: Circle CenterX=61.1496 CenterY=-79.2541 CenterZ=0 NormalX=0 NormalY=0 NormalZ=1 AngleXU=0 Radius=1
    g10: BSplineCurve PolesCount=3 KnotsCount=2 Degree=2 IsPeriodic=0
    g11: GeomPoint X=58.0728 Y=-77.8102 Z=0
    g12: GeomPoint X=61.1496 Y=-79.2541 Z=0
    g13: Circle CenterX=61.6457 CenterY=-88.8112 CenterZ=0 NormalX=0 NormalY=0 NormalZ=1 AngleXU=0 Radius=1
    g14: Circle CenterX=58.0728 CenterY=-91.7794 CenterZ=0 NormalX=0 NormalY=0 NormalZ=1 AngleXU=0 Radius=1
    g15: Circle CenterX=63.9135 CenterY=-91.8014 CenterZ=0 NormalX=0 NormalY=0 NormalZ=1 AngleXU=0 Radius=1
    g16: BSplineCurve PolesCount=3 KnotsCount=2 Degree=2 IsPeriodic=0
    g17: GeomPoint X=61.6457 Y=-88.8112 Z=0
    g18: GeomPoint X=63.9135 Y=-91.8014 Z=0
    g19: Circle CenterX=58.0728 CenterY=-40.8935 CenterZ=0 NormalX=0 NormalY=0 NormalZ=1 AngleXU=0 Radius=1
    g20: Circle CenterX=58.0728 CenterY=-44.8935 CenterZ=0 NormalX=0 NormalY=0 NormalZ=1 AngleXU=0 Radius=1
    g21: Circle CenterX=61.5791 CenterY=-42.9683 CenterZ=0 NormalX=0 NormalY=0 NormalZ=1 AngleXU=0 Radius=1
    g22: BSplineCurve PolesCount=3 KnotsCount=2 Degree=2 IsPeriodic=0
    g23: GeomPoint X=58.0728 Y=-40.8935 Z=0
    g24: GeomPoint X=61.5791 Y=-42.9683 Z=0
    g25: Circle CenterX=42.5666 CenterY=-67.3492 CenterZ=0 NormalX=0 NormalY=0 NormalZ=1 AngleXU=0 Radius=1
    g26: Circle CenterX=46.0728 CenterY=-65.424 CenterZ=0 NormalX=0 NormalY=0 NormalZ=1 AngleXU=0 Radius=1
    g27: Circle CenterX=46.0728 CenterY=-69.424 CenterZ=0 NormalX=0 NormalY=0 NormalZ=1 AngleXU=0 Radius=1
    g28: BSplineCurve PolesCount=3 KnotsCount=2 Degree=2 IsPeriodic=0
    g29: GeomPoint X=42.5666 Y=-67.3492 Z=0
    g30: GeomPoint X=46.0728 Y=-69.424 Z=0
    g31: Circle CenterX=2.07281 CenterY=-91.7794 CenterZ=0 NormalX=0 NormalY=0 NormalZ=1 AngleXU=0 Radius=1
    g32: Circle CenterX=-1.92719 CenterY=-91.7794 CenterZ=0 NormalX=0 NormalY=0 NormalZ=1 AngleXU=0 Radius=1
    g33: Circle CenterX=1.57905 CenterY=-89.8542 CenterZ=0 NormalX=0 NormalY=0 NormalZ=1 AngleXU=0 Radius=1
    g34: BSplineCurve PolesCount=3 KnotsCount=2 Degree=2 IsPeriodic=0
    g35: GeomPoint X=2.07281 Y=-91.7794 Z=0
    g36: GeomPoint X=1.57905 Y=-89.8542 Z=0
    g37: ArcOfCircle CenterX=-26.9272 CenterY=22.1087 CenterZ=0 NormalX=0 NormalY=0 NormalZ=1 AngleXU=0 Radius=4 StartAngle=5e-16 EndAngle=3.14159
    g38: Circle CenterX=-10.9272 CenterY=-78.7794 CenterZ=0 NormalX=0 NormalY=0 NormalZ=1 AngleXU=0 Radius=1
    g39: Circle CenterX=-10.9272 CenterY=-82.7794 CenterZ=0 NormalX=0 NormalY=0 NormalZ=1 AngleXU=0 Radius=1
    g40: Circle CenterX=-7.42095 CenterY=-80.8542 CenterZ=0 NormalX=0 NormalY=0 NormalZ=1 AngleXU=0 Radius=1
    g41: BSplineCurve PolesCount=3 KnotsCount=2 Degree=2 IsPeriodic=0
    g42: GeomPoint X=-10.9272 Y=-78.7794 Z=0
    g43: GeomPoint X=-7.42095 Y=-80.8542 Z=0
    g44: BSplineCurve PolesCount=3 KnotsCount=2 Degree=2 IsPeriodic=0
    g45: GeomPoint X=42.5666 Y=-53.4075 Z=0
    g46: GeomPoint X=46.0728 Y=-47.4823 Z=0
    g47: BSplineCurve PolesCount=5 KnotsCount=3 Degree=3 IsPeriodic=0
    g48: LineSegment StartX=124.814 StartY=-22.1885 StartZ=0 EndX=123.265 EndY=-19.3655 EndZ=0
    g49: ArcOfCircle CenterX=116.562 CenterY=-19.6236 CenterZ=0 NormalX=0 NormalY=0 NormalZ=1 AngleXU=0 Radius=4.24264 StartAngle=1.28753 EndAngle=6.00037
    g50: LineSegment StartX=-30.9272 StartY=22.1087 StartZ=0 EndX=-34.9272 EndY=-83.7794 EndZ=0
    g51: LineSegment StartX=-22.9272 StartY=22.1087 StartZ=0 EndX=-18.9272 EndY=-83.7794 EndZ=0
    g52: LineSegment StartX=118.934 StartY=-11.4765 StartZ=0 EndX=120.377 EndY=-14.1062 EndZ=0
    g53: LineSegment StartX=118.86 StartY=-31.3104 StartZ=0 EndX=120.377 EndY=-33.1447 EndZ=0
    g54: LineSegment StartX=115.291 StartY=-37.3514 StartZ=0 EndX=117.05 EndY=-39.4781 EndZ=0
    g55: LineSegment StartX=122.136 StartY=-35.2714 StartZ=0 EndX=123.656 EndY=-37.1092 EndZ=0
    g56: BSplineCurve PolesCount=3 KnotsCount=2 Degree=2 IsPeriodic=0
    g57: LineSegment StartX=132.072 StartY=-100.779 StartZ=0 EndX=132.072 EndY=-103.779 EndZ=0
    g58: LineSegment StartX=132.072 StartY=-91.8014 StartZ=0 EndX=132.072 EndY=-94.7791 EndZ=0
    g59: LineSegment StartX=63.9135 StartY=-91.8014 StartZ=0 EndX=132.072 EndY=-91.8014 EndZ=0
    g60: LineSegment StartX=61.6457 StartY=-88.8112 StartZ=0 EndX=123.656 EndY=-37.1092 EndZ=0
    g61: LineSegment StartX=122.136 StartY=-35.2714 StartZ=0 EndX=117.05 EndY=-39.4781 EndZ=0
    g62: LineSegment StartX=115.291 StartY=-37.3514 StartZ=0 EndX=120.377 EndY=-33.1447 EndZ=0
    g63: LineSegment StartX=118.86 StartY=-31.3104 StartZ=0 EndX=61.1496 EndY=-79.2541 EndZ=0
    g64: LineSegment StartX=58.0728 StartY=-77.8102 StartZ=0 EndX=58.0728 EndY=-62.8351 EndZ=0
    g65: LineSegment StartX=61.5791 StartY=-56.9099 StartZ=0 EndX=124.814 EndY=-22.1885 EndZ=0
    g66: LineSegment StartX=120.636 StartY=-20.8076 StartZ=0 EndX=123.265 EndY=-19.3655 EndZ=0
    g67: LineSegment StartX=117.748 StartY=-15.55 StartZ=0 EndX=120.377 EndY=-14.1062 EndZ=0
    g68: LineSegment StartX=118.934 StartY=-11.4765 StartZ=0 EndX=61.5791 EndY=-42.9683 EndZ=0
    g69: LineSegment StartX=-42.9272 StartY=-103.779 StartZ=0 EndX=132.072 EndY=-103.779 EndZ=0
    g70: LineSegment StartX=42.5666 StartY=-53.4075 StartZ=0 EndX=-7.42095 EndY=-80.8542 EndZ=0
    g71: LineSegment StartX=-10.9272 StartY=-78.7794 StartZ=0 EndX=-10.9272 EndY=48.2206 EndZ=0
    g72: LineSegment StartX=2.07281 StartY=-91.7794 StartZ=0 EndX=42.0728 EndY=-91.7794 EndZ=0
    g73: LineSegment StartX=46.0728 StartY=-87.7794 StartZ=0 EndX=46.0728 EndY=-69.424 EndZ=0
    g74: LineSegment StartX=42.5666 StartY=-67.3492 StartZ=0 EndX=1.57905 EndY=-89.8542 EndZ=0
    g75: LineSegment StartX=-42.9272 StartY=-103.779 StartZ=0 EndX=-42.9272 EndY=48.2206 EndZ=0
    g76: LineSegment StartX=-17.9272 StartY=48.2206 StartZ=0 EndX=-17.9272 EndY=58.2206 EndZ=0
    g77: LineSegment StartX=-35.9272 StartY=48.2206 StartZ=0 EndX=-35.9272 EndY=52.2206 EndZ=0
    g78: LineSegment StartX=-29.9272 StartY=48.2206 StartZ=0 EndX=-29.9272 EndY=52.2206 EndZ=0
    g79: LineSegment StartX=-23.9272 StartY=48.2206 StartZ=0 EndX=-23.9272 EndY=58.2206 EndZ=0
    g80: ArcOfCircle CenterX=-32.9272 CenterY=55.2206 CenterZ=0 NormalX=0 NormalY=0 NormalZ=1 AngleXU=0 Radius=4.24264 StartAngle=5.49779 EndAngle=10.2102
    g81: ArcOfCircle CenterX=-20.9272 CenterY=61.2206 CenterZ=0 NormalX=0 NormalY=0 NormalZ=1 AngleXU=0 Radius=4.24264 StartAngle=5.49779 EndAngle=10.2102
    g82: LineSegment StartX=-17.9272 StartY=48.2206 StartZ=0 EndX=-10.9272 EndY=48.2206 EndZ=0
    g83: LineSegment StartX=-42.9272 StartY=48.2206 StartZ=0 EndX=-35.9272 EndY=48.2206 EndZ=0
    g84: LineSegment StartX=50.0728 StartY=-27.5905 StartZ=0 EndX=50.0728 EndY=-31.5905 EndZ=0
    g85: LineSegment StartX=54.0728 StartY=-27.5905 StartZ=0 EndX=54.0728 EndY=-31.5905 EndZ=0
    g86: ArcOfCircle CenterX=52.0728 CenterY=-33.5905 CenterZ=0 NormalX=0 NormalY=0 NormalZ=1 AngleXU=0 Radius=2.82843 StartAngle=2.35619 EndAngle=7.06858
    g87: LineSegment StartX=46.0728 StartY=-27.5905 StartZ=0 EndX=50.0728 EndY=-27.5905 EndZ=0
    g88: LineSegment StartX=54.0728 StartY=-27.5905 StartZ=0 EndX=58.0728 EndY=-27.5905 EndZ=0
    g89: LineSegment StartX=46.0728 StartY=-27.5905 StartZ=0 EndX=46.0728 EndY=-47.4823 EndZ=0
    g90: LineSegment StartX=58.0728 StartY=-27.5905 StartZ=0 EndX=58.0728 EndY=-40.8935 EndZ=0
    g91: LineSegment StartX=-29.9272 StartY=48.2206 StartZ=0 EndX=-23.9272 EndY=48.2206 EndZ=0
  constraints (170):
    c: Weight(g1) = 1
    c: Equal(g1,g2)
    c: Equal(g1,g3)
    c: InternalAlignment(g1,g4)
    c: InternalAlignment(g2,g4)
    c: InternalAlignment(g3,g4)
    c: InternalAlignment(g5,g4)
    c: InternalAlignment(g6,g4)
    c: Weight(g7) = 1
    c: Equal(g7,g8)
    c: Equal(g7,g9)
    c: InternalAlignment(g7,g10)
    c: InternalAlignment(g8,g10)
    c: InternalAlignment(g9,g10)
    c: InternalAlignment(g11,g10)
    c: InternalAlignment(g12,g10)
    c: Block(g4)
    c: Block(g10)
    c: Weight(g13) = 1
    c: Equal(g13,g14)
    c: Equal(g13,g15)
    c: InternalAlignment(g13,g16)
    c: InternalAlignment(g14,g16)
    c: InternalAlignment(g15,g16)
    c: InternalAlignment(g17,g16)
    c: InternalAlignment(g18,g16)
    c: Block(g16)
    c: Weight(g19) = 1
    c: Equal(g19,g20)
    c: Equal(g19,g21)
    c: InternalAlignment(g19,g22)
    c: InternalAlignment(g20,g22)
    c: InternalAlignment(g21,g22)
    c: InternalAlignment(g23,g22)
    c: InternalAlignment(g24,g22)
    c: Block(g22)
    c: Weight(g25) = 1
    c: Equal(g25,g26)
    c: Equal(g25,g27)
    c: InternalAlignment(g25,g28)
    c: InternalAlignment(g26,g28)
    c: InternalAlignment(g27,g28)
    c: InternalAlignment(g29,g28)
    c: InternalAlignment(g30,g28)
    c: Weight(g31) = 1
    c: Equal(g31,g32)
    c: Equal(g31,g33)
    c: InternalAlignment(g31,g34)
    c: InternalAlignment(g32,g34)
    c: InternalAlignment(g33,g34)
    c: InternalAlignment(g35,g34)
    c: InternalAlignment(g36,g34)
    c: Block(g34)
    c: Block(g28)
    c: Block(g37)
    c: Block(g0)
    c: Weight(g38) = 1
    c: Equal(g38,g40)
    c: InternalAlignment(g38,g41)
    c: InternalAlignment(g39,g41)
    c: InternalAlignment(g40,g41)
    c: InternalAlignment(g42,g41)
    c: InternalAlignment(g43,g41)
    c: InternalAlignment(g45,g44)
    c: InternalAlignment(g46,g44)
    c: Block(g47)
    c: Block(g44)
    c: Block(g41)
    c: Block(g48)
    c: Block(g49)
    c: Coincident(g50,g37)
    c: Coincident(g50,g0)
    c: Coincident(g51,g37)
    c: Coincident(g51,g0)
    c: Block(g51)
    c: Block(g50)
    c: Block(g52)
    c: Block(g53)
    c: Block(g54)
    c: Block(g55)
    c: Block(g56)
    c: Coincident(g57,g47)
    c: Vertical(g57)
    c: Coincident(g58,g47)
    c: Vertical(g58)
    c: Coincident(g59,g16)
    c: Coincident(g59,g58)
    c: Horizontal(g59)
    c: Coincident(g60,g16)
    c: Coincident(g60,g55)
    c: Coincident(g61,g55)
    c: Coincident(g61,g54)
    c: Coincident(g62,g54)
    c: Coincident(g62,g53)
    c: Coincident(g63,g53)
    c: Coincident(g63,g10)
    c: Coincident(g64,g10)
    c: Coincident(g64,g4)
    c: Vertical(g64)
    c: Coincident(g65,g4)
    c: Coincident(g65,g48)
    c: Coincident(g66,g49)
    c: Coincident(g66,g48)
    c: Coincident(g67,g49)
    c: Coincident(g67,g52)
    c: Coincident(g68,g52)
    c: Coincident(g68,g22)
    c: Coincident(g69,g57)
    c: Horizontal(g69)
    c: Coincident(g70,g44)
    c: Coincident(g70,g41)
    c: Coincident(g71,g41)
    c: Vertical(g71)
    c: Coincident(g72,g34)
    c: Coincident(g72,g56)
    c: Horizontal(g72)
    c: Coincident(g73,g56)
    c: Coincident(g73,g28)
    c: Vertical(g73)
    c: Coincident(g74,g28)
    c: Coincident(g74,g34)
    c: Block(g69)
    c: Coincident(g75,g69)
    c: Vertical(g75)
    c: Distance(g75) = 152
    c: Block(g71)
    c: Vertical(g76)
    c: Distance(g76) = 10
    c: Vertical(g77)
    c: Distance(g77) = 4
    c: Vertical(g78)
    c: Distance(g78) = 4
    c: Vertical(g79)
    c: Distance(g79) = 10
    c: Coincident(g80,g78)
    c: Coincident(g80,g77)
    c: Block(g80)
    c: Coincident(g81,g79)
    c: Coincident(g81,g76)
    c: Block(g81)
    c: Coincident(g82,g76)
    c: Coincident(g82,g71)
    c: Horizontal(g82)
    c: Coincident(g83,g75)
    c: Coincident(g83,g77)
    c: Horizontal(g83)
    c: Distance(g83) = 7
    c: Distance(g82) = 7
    c: Vertical(g84)
    c: Distance(g84) = 4
    c: Vertical(g85)
    c: Distance(g85) = 4
    c: Coincident(g86,g84)
    c: Coincident(g86,g85)
    c: Block(g86)
    c: Coincident(g87,g84)
    c: Horizontal(g87)
    c: Distance(g87) = 4
    c: Coincident(g88,g85)
    c: Horizontal(g88)
    c: Distance(g88) = 4
    c: Coincident(g89,g87)
    c: Coincident(g89,g44)
    c: Vertical(g89)
    c: Coincident(g90,g88)
    c: Coincident(g90,g22)
    c: Vertical(g90)
    c: Coincident(g91,g78)
    c: Coincident(g91,g79)
    c: Horizontal(g91)
FEATURE [Part::Extrusion] Extrude043
  Base = -> Sketch042
  Dir = (0,0,1)
  DirMode = 2
  FaceMakerClass = Part::FaceMakerBullseye
  LengthFwd = 28
  LengthRev = 0
  Solid = true
  Symmetric = false
FEATURE [Sketcher::SketchObject] Sketch043
  FullyConstrained = true
  Placement = pos=(0,0,0) rot=(0.57735,0.57735,0.57735;2.0944rad)
  sketch-geometry (18):
    g0: LineSegment StartX=-152.23 StartY=29.0049 StartZ=0 EndX=-143.23 EndY=29.0049 EndZ=0
    g1: LineSegment StartX=-152.23 StartY=29.0049 StartZ=0 EndX=-152.23 EndY=51.0049 EndZ=0
    g2: LineSegment StartX=-152.23 StartY=51.0049 StartZ=0 EndX=-130.23 EndY=51.0049 EndZ=0
    g3: LineSegment StartX=-130.23 StartY=51.0049 StartZ=0 EndX=-130.23 EndY=46.0049 EndZ=0
    g4: LineSegment StartX=-130.23 StartY=46.0049 StartZ=0 EndX=-143.23 EndY=46.0049 EndZ=0
    g5: Circle CenterX=-145.23 CenterY=31.0049 CenterZ=0 NormalX=0 NormalY=0 NormalZ=1 AngleXU=0 Radius=1
    g6: Circle CenterX=-145.23 CenterY=29.0049 CenterZ=0 NormalX=0 NormalY=0 NormalZ=1 AngleXU=0 Radius=1
    g7: Circle CenterX=-143.23 CenterY=29.0049 CenterZ=0 NormalX=0 NormalY=0 NormalZ=1 AngleXU=0 Radius=1
    g8: BSplineCurve PolesCount=3 KnotsCount=2 Degree=2 IsPeriodic=0
    g9: GeomPoint X=-145.23 Y=31.0049 Z=0
    g10: GeomPoint X=-143.23 Y=29.0049 Z=0
    g11: Circle CenterX=-145.23 CenterY=44.0049 CenterZ=0 NormalX=0 NormalY=0 NormalZ=1 AngleXU=0 Radius=1
    g12: Circle CenterX=-145.23 CenterY=46.0049 CenterZ=0 NormalX=0 NormalY=0 NormalZ=1 AngleXU=0 Radius=1
    g13: Circle CenterX=-143.23 CenterY=46.0049 CenterZ=0 NormalX=0 NormalY=0 NormalZ=1 AngleXU=0 Radius=1
    g14: BSplineCurve PolesCount=3 KnotsCount=2 Degree=2 IsPeriodic=0
    g15: GeomPoint X=-145.23 Y=44.0049 Z=0
    g16: GeomPoint X=-143.23 Y=46.0049 Z=0
    g17: LineSegment StartX=-145.23 StartY=44.0049 StartZ=0 EndX=-145.23 EndY=31.0049 EndZ=0
  constraints (40):
    c: Horizontal(g0)
    c: Distance(g0) = 9
    c: Coincident(g1,g0)
    c: Vertical(g1)
    c: Distance(g1) = 22
    c: Coincident(g2,g1)
    c: Horizontal(g2)
    c: Coincident(g3,g2)
    c: Vertical(g3)
    c: Distance(g3) = 5
    c: Coincident(g4,g3)
    c: Horizontal(g4)
    c: Distance(g4) = 13
    c: PointOnObject(g6,g0)
    c: Weight(g5) = 1
    c: Equal(g5,g6)
    c: Equal(g5,g7)
    c: Coincident(g8,g0)
    c: InternalAlignment(g5,g8)
    c: InternalAlignment(g6,g8)
    c: InternalAlignment(g7,g8)
    c: InternalAlignment(g9,g8)
    c: InternalAlignment(g10,g8)
    c: Weight(g11) = 1
    c: Equal(g11,g12)
    c: Equal(g11,g13)
    c: Coincident(g14,g4)
    c: InternalAlignment(g11,g14)
    c: InternalAlignment(g12,g14)
    c: InternalAlignment(g13,g14)
    c: InternalAlignment(g15,g14)
    c: InternalAlignment(g16,g14)
    c: Coincident(g17,g14)
    c: Coincident(g17,g8)
    c: Vertical(g17)
    c: Block(g4)
    c: Block(g17)
    c: Block(g14)
    c: Block(g8)
    c: Distance(g2) = 22
FEATURE [Part::Box] Box067  label="removeFromtTop013"
  AttacherType = Attacher::AttachEngine3D
  Height = 56
  Length = 470
  Placement = pos=(-47.93,-106.78,8) rot=(1,0,0;0.080285rad)
  Width = 260
FEATURE [Part::Cut] Cut056
  Base = -> Extrude043
  Tool = -> Box067
FEATURE [Part::Box] Box068  label="removeFromBottomOfTop004"
  AttacherType = Attacher::AttachEngine3D
  Height = 10
  Length = 475
  Placement = pos=(-51,-113,-1) rot=(1,0,0;0.080285rad)
  Width = 10
FEATURE [Part::Cut] Cut057
  Base = -> Cut056
  Tool = -> Box068
FEATURE [Part::Extrusion] Extrude044  label="laptopRetainer034"
  Base = -> Sketch043
  Dir = (1,0,0)
  DirMode = 2
  FaceMakerClass = Part::FaceMakerBullseye
  LengthFwd = 150
  LengthRev = 0
  Placement = pos=(-42.925,50.355,-8.454) rot=(1,0,0;0.080285rad)
  Solid = true
  Symmetric = false
FEATURE [Part::Box] Box069  label="Cube050"
  AttacherType = Attacher::AttachEngine3D
  Height = 10
  Length = 40
  Placement = pos=(12.07,-101,0) rot=(0,0,1;0rad)
  Width = 4
FEATURE [Part::Fuse] Fusion167  label="laptopRetainer033"
  Base = -> Extrude044
  Tool = -> Box069
FEATURE [Sketcher::SketchObject] Sketch044
  FullyConstrained = true
  Placement = pos=(0,0,0) rot=(0.57735,0.57735,0.57735;2.0944rad)
  sketch-geometry (18):
    g0: LineSegment StartX=-152.23 StartY=29.0049 StartZ=0 EndX=-143.23 EndY=29.0049 EndZ=0
    g1: LineSegment StartX=-152.23 StartY=29.0049 StartZ=0 EndX=-152.23 EndY=51.0049 EndZ=0
    g2: LineSegment StartX=-152.23 StartY=51.0049 StartZ=0 EndX=-130.23 EndY=51.0049 EndZ=0
    g3: LineSegment StartX=-130.23 StartY=51.0049 StartZ=0 EndX=-130.23 EndY=46.0049 EndZ=0
    g4: LineSegment StartX=-130.23 StartY=46.0049 StartZ=0 EndX=-143.23 EndY=46.0049 EndZ=0
    g5: Circle CenterX=-145.23 CenterY=31.0049 CenterZ=0 NormalX=0 NormalY=0 NormalZ=1 AngleXU=0 Radius=1
    g6: Circle CenterX=-145.23 CenterY=29.0049 CenterZ=0 NormalX=0 NormalY=0 NormalZ=1 AngleXU=0 Radius=1
    g7: Circle CenterX=-143.23 CenterY=29.0049 CenterZ=0 NormalX=0 NormalY=0 NormalZ=1 AngleXU=0 Radius=1
    g8: BSplineCurve PolesCount=3 KnotsCount=2 Degree=2 IsPeriodic=0
    g9: GeomPoint X=-145.23 Y=31.0049 Z=0
    g10: GeomPoint X=-143.23 Y=29.0049 Z=0
    g11: Circle CenterX=-145.23 CenterY=44.0049 CenterZ=0 NormalX=0 NormalY=0 NormalZ=1 AngleXU=0 Radius=1
    g12: Circle CenterX=-145.23 CenterY=46.0049 CenterZ=0 NormalX=0 NormalY=0 NormalZ=1 AngleXU=0 Radius=1
    g13: Circle CenterX=-143.23 CenterY=46.0049 CenterZ=0 NormalX=0 NormalY=0 NormalZ=1 AngleXU=0 Radius=1
    g14: BSplineCurve PolesCount=3 KnotsCount=2 Degree=2 IsPeriodic=0
    g15: GeomPoint X=-145.23 Y=44.0049 Z=0
    g16: GeomPoint X=-143.23 Y=46.0049 Z=0
    g17: LineSegment StartX=-145.23 StartY=44.0049 StartZ=0 EndX=-145.23 EndY=31.0049 EndZ=0
  constraints (40):
    c: Horizontal(g0)
    c: Distance(g0) = 9
    c: Coincident(g1,g0)
    c: Vertical(g1)
    c: Distance(g1) = 22
    c: Coincident(g2,g1)
    c: Horizontal(g2)
    c: Coincident(g3,g2)
    c: Vertical(g3)
    c: Distance(g3) = 5
    c: Coincident(g4,g3)
    c: Horizontal(g4)
    c: Distance(g4) = 13
    c: PointOnObject(g6,g0)
    c: Weight(g5) = 1
    c: Equal(g5,g6)
    c: Equal(g5,g7)
    c: Coincident(g8,g0)
    c: InternalAlignment(g5,g8)
    c: InternalAlignment(g6,g8)
    c: InternalAlignment(g7,g8)
    c: InternalAlignment(g9,g8)
    c: InternalAlignment(g10,g8)
    c: Weight(g11) = 1
    c: Equal(g11,g12)
    c: Equal(g11,g13)
    c: Coincident(g14,g4)
    c: InternalAlignment(g11,g14)
    c: InternalAlignment(g12,g14)
    c: InternalAlignment(g13,g14)
    c: InternalAlignment(g15,g14)
    c: InternalAlignment(g16,g14)
    c: Coincident(g17,g14)
    c: Coincident(g17,g8)
    c: Vertical(g17)
    c: Block(g4)
    c: Block(g17)
    c: Block(g14)
    c: Block(g8)
    c: Distance(g2) = 22
FEATURE [Part::Extrusion] Extrude045  label="laptopRetainer037"
  Base = -> Sketch044
  Dir = (1,0,0)
  DirMode = 2
  FaceMakerClass = Part::FaceMakerBullseye
  LengthFwd = 150
  LengthRev = 0
  Placement = pos=(107.08,50.35,-8.45) rot=(1,0,0;0.080285rad)
  Solid = true
  Symmetric = false
FEATURE [Part::Box] Box070  label="Cube051"
  AttacherType = Attacher::AttachEngine3D
  Height = 10
  Length = 40
  Placement = pos=(162.7,-101,0) rot=(0,0,1;0rad)
  Width = 4
FEATURE [Part::Fuse] Fusion168  label="laptopRetainer035"
  Base = -> Extrude045
  Tool = -> Box070
FEATURE [Part::Box] Box071  label="Cube052"
  AttacherType = Attacher::AttachEngine3D
  Height = 10
  Length = 10
  Placement = pos=(101,-102.5,12) rot=(1,0,0;0.080285rad)
  Width = 4
FEATURE [Part::Box] Box072  label="Cube053"
  AttacherType = Attacher::AttachEngine3D
  Height = 10
  Length = 10
  Placement = pos=(253,-102.5,12) rot=(1,0,0;0.080285rad)
  Width = 4
FEATURE [Part::MultiFuse] Fusion169  label="laptopRetainer036"
  Shapes = -> [Box072,Fusion168,Box071]
FEATURE [Part::Cut] Cut058  label="laptopRetainer038"
  Base = -> Fusion167
  Tool = -> Fusion169
FEATURE [Part::Cut] Cut059
  Base = -> Cut057
  Tool = -> Cut058
FEATURE [Part::Cylinder] Cylinder160
  Angle = 360
  AttacherType = Attacher::AttachEngine3D
  Height = 30
  Placement = pos=(-49,106,4) rot=(-1,0,0;0.328122rad)
  Radius = 3
FEATURE [Part::Cylinder] Cylinder161
  Angle = 360
  AttacherType = Attacher::AttachEngine3D
  Height = 10
  Placement = pos=(-49,103,-5) rot=(-1,0,0;0.328122rad)
  Radius = 1.1
FEATURE [Part::Cylinder] Cylinder162
  Angle = 360
  AttacherType = Attacher::AttachEngine3D
  Height = 30
  Placement = pos=(-49,106,4) rot=(-1,0,0;0.328122rad)
  Radius = 3
FEATURE [Part::MultiFuse] Fusion170
  Placement = pos=(15,-68.4,0) rot=(0,0,1;0rad)
  Shapes = -> [Cylinder161,Cylinder162]
FEATURE [Part::Cylinder] Cylinder163
  Angle = 360
  AttacherType = Attacher::AttachEngine3D
  Height = 10
  Placement = pos=(-49,103,-5) rot=(-1,0,0;0.328122rad)
  Radius = 1.1
FEATURE [Part::MultiFuse] Fusion171
  Placement = pos=(15,17.6,0) rot=(0,0,1;0rad)
  Shapes = -> [Cylinder163,Cylinder160]
FEATURE [Part::MultiFuse] Fusion172  label="removeToCreateOutterTopScrewHolesLeft005"
  Shapes = -> [Fusion171,Fusion170]
FEATURE [Part::Cut] Cut060  label="bottomLeftBase001"
  Base = -> Cut059
  Tool = -> Fusion172
FEATURE [Part::Cut] Cut061
  Base = -> Cut055
  Tool = -> Cut038
